FCSTD DOCUMENT  (FreeCAD 0.18.4R)
Label: Frame-03
License: CC-BY 3.0
LicenseURL: http://creativecommons.org/licenses/by/3.0/
objects: Part::Cylinder×968, Part::Box×648, Part::MultiFuse×634, Part::Cut×624, Part::Fillet×374, Part::Chamfer×146, Part::Mirroring×97, Part::Feature×58, Part::Loft×23, Part::Cone×22, App::DocumentObjectGroup×19, Part::Extrusion×14, Part::Part2DObjectPython×5, Part::Sphere×2, Mesh::Feature×2
note: 3615 computed .brp shape members not serialized (recipe doc carries the construction recipe); baked Part::Feature solids carry a one-line shape summary decoded from their .brp

FEATURE [Part::Box] Box  label="Cube250"
  AttacherType = Attacher::AttachEngine3D
  Height = 64
  Length = 126
  Width = 170
FEATURE [Part::Fillet] Fillet001
  Base = -> Box
  Edges = 2 edges r=15: [Edge1,Edge3]
FEATURE [Part::Fillet] Fillet
  Base = -> Fillet001
  Edges = 2 edges r=10: [Edge17,Edge18]
FEATURE [Part::Box] Box001  label="Cube251"
  AttacherType = Attacher::AttachEngine3D
  Height = 64
  Length = 120
  Placement = pos=(4,4,0) rot=(0,0,1;0rad)
  Width = 164
FEATURE [Part::Fillet] Fillet003
  Base = -> Box001
  Edges = 2 edges r=12: [Edge1,Edge3]
FEATURE [Part::Fillet] Fillet002
  Base = -> Fillet003
  Edges = 2 edges r=6: [Edge17,Edge18]
  Placement = pos=(-1,-1,0) rot=(0,0,1;0rad)
FEATURE [Part::Cut] Cut001
  Base = -> Fillet
  Refine = true
  Tool = -> Fillet002
FEATURE [Part::Cylinder] Cylinder004
  Angle = 360
  AttacherType = Attacher::AttachEngine3D
  Height = 174
  Placement = pos=(98,174,-23) rot=(1,0,0;1.5708rad)
  Radius = 52
FEATURE [Part::Cut] Cut
  Base = -> Cut001
  Refine = true
  Tool = -> Cylinder004
FEATURE [Part::Box] Box002  label="Cube252"
  AttacherType = Attacher::AttachEngine3D
  Height = 25
  Length = 131
  Placement = pos=(11,0,6) rot=(0,0,1;0rad)
  Width = 170
FEATURE [Part::Box] Box003  label="Cube253"
  AttacherType = Attacher::AttachEngine3D
  Height = 25
  Length = 148
  Placement = pos=(2,2,6) rot=(0,0,1;0rad)
  Width = 166
FEATURE [Part::Box] Box009  label="Cube192"
  AttacherType = Attacher::AttachEngine3D
  Height = 5.8
  Length = 13.6
  Placement = pos=(91.2,163,27) rot=(0,0,1;0rad)
  Width = 4
FEATURE [Part::Box] Box010  label="Cube254"
  AttacherType = Attacher::AttachEngine3D
  Height = 23
  Length = 37
  Placement = pos=(15,152,-23) rot=(0,0,1;0rad)
  Width = 18
FEATURE [Part::Cylinder] Cylinder012
  Angle = 360
  AttacherType = Attacher::AttachEngine3D
  Height = 22
  Placement = pos=(98,174,-23) rot=(1,0,0;1.5708rad)
  Radius = 52
FEATURE [Part::Box] Box011  label="Cube255"
  AttacherType = Attacher::AttachEngine3D
  Height = 9
  Length = 31
  Placement = pos=(17,156,-29) rot=(0,0,1;0rad)
  Width = 14
FEATURE [Part::Cylinder] Cylinder013
  Angle = 360
  AttacherType = Attacher::AttachEngine3D
  Height = 22
  Placement = pos=(98,174,-23) rot=(1,0,0;1.5708rad)
  Radius = 54
FEATURE [Part::Cut] Cut059
  Base = -> Box002
  Placement = pos=(0,0,2) rot=(0,0,1;0rad)
  Refine = true
  Tool = -> Box003
FEATURE [Part::Cut] Cut060
  Base = -> Cut059
  Placement = pos=(0,0,-3) rot=(0,0,1;0rad)
  Refine = true
FEATURE [Part::Cut] Cut061
  Base = -> Cut
  Refine = true
  Tool = -> Cut060
FEATURE [Part::Box] Box036  label="Cube274"
  AttacherType = Attacher::AttachEngine3D
  Height = 64
  Length = 21
  Width = 164
FEATURE [Part::Fillet] Fillet010
  Base = -> Box036
  Edges = 2 edges r=12: [Edge1,Edge3]
  Placement = pos=(3,3,0) rot=(0,0,1;0rad)
FEATURE [Part::Box] Box038  label="Cube276"
  AttacherType = Attacher::AttachEngine3D
  Height = 59
  Length = 16
  Placement = pos=(15,0,0) rot=(0,0,1;0rad)
  Width = 170
FEATURE [Part::Box] Box039  label="Cube277"
  AttacherType = Attacher::AttachEngine3D
  Height = 59
  Length = 21
  Placement = pos=(-13,3,0) rot=(0,0,1;0rad)
  Width = 164
FEATURE [Part::Box] Box040  label="Cube278"
  AttacherType = Attacher::AttachEngine3D
  Height = 59
  Length = 21
  Placement = pos=(-13,0,0) rot=(0,0,1;0rad)
  Width = 170
FEATURE [Part::Fillet] Fillet011
  Base = -> Box040
  Edges = 2 edges r=15: [Edge1,Edge3]
FEATURE [Part::Fillet] Fillet012
  Base = -> Box039
  Edges = 2 edges r=12: [Edge1,Edge3]
  Placement = pos=(3,0,0) rot=(0,0,1;0rad)
FEATURE [Part::Cut] Cut063
  Base = -> Fillet011
  Placement = pos=(13,0,0) rot=(0,0,1;0rad)
  Refine = true
  Tool = -> Fillet012
FEATURE [Part::Cut] Cut064
  Base = -> Cut063
  Refine = true
  Tool = -> Box038
FEATURE [Part::Box] Box041  label="Cube279"
  AttacherType = Attacher::AttachEngine3D
  Height = 28
  Length = 21
  Placement = pos=(-13,3,0) rot=(0,0,1;0rad)
  Width = 164
FEATURE [Part::Fillet] Fillet014
  Base = -> Box041
  Edges = 2 edges r=12: [Edge1,Edge3]
  Placement = pos=(2.5,0,0) rot=(0,0,1;0rad)
FEATURE [Part::Box] Box042  label="Cube280"
  AttacherType = Attacher::AttachEngine3D
  Height = 28
  Length = 21
  Placement = pos=(-13,0,0) rot=(0,0,1;0rad)
  Width = 170
FEATURE [Part::Fillet] Fillet013
  Base = -> Box042
  Edges = 2 edges r=15: [Edge1,Edge3]
FEATURE [Part::Cut] Cut067
  Base = -> Fillet013
  Placement = pos=(13,0,30) rot=(0,0,1;0rad)
  Refine = true
  Tool = -> Fillet014
FEATURE [Part::Box] Box043  label="Cube281"
  AttacherType = Attacher::AttachEngine3D
  Height = 59
  Length = 16
  Placement = pos=(14.5,0,0) rot=(0,0,1;0rad)
  Width = 170
FEATURE [Part::Cut] Cut066
  Base = -> Cut067
  Refine = true
  Tool = -> Box043
FEATURE [Part::Box] Box044  label="Cube282"
  AttacherType = Attacher::AttachEngine3D
  Height = 3
  Length = 3
  Placement = pos=(0,63,55) rot=(0,0,1;0rad)
  Width = 44
FEATURE [Part::Fillet] Fillet015
  Base = -> Box044
  Edges = 2 edges r=2: [Edge9,Edge11]
FEATURE [Part::Box] Box047  label="Cube285"
  AttacherType = Attacher::AttachEngine3D
  Height = 33
  Length = 21
  Placement = pos=(-13,3,0) rot=(0,0,1;0rad)
  Width = 164
FEATURE [Part::Fillet] Fillet016
  Base = -> Box047
  Edges = 2 edges r=12: [Edge1,Edge3]
  Placement = pos=(15.5,0,0) rot=(0,0,1;0rad)
FEATURE [Part::Box] Box070  label="Cube308"
  AttacherType = Attacher::AttachEngine3D
  Height = 4
  Length = 21
  Placement = pos=(-13,0,26) rot=(0,0,1;0rad)
  Width = 170
FEATURE [Part::Fillet] Fillet026
  Base = -> Box070
  Edges = 2 edges r=15: [Edge1,Edge3]
FEATURE [Part::Chamfer] Chamfer011
  Base = -> Fillet026
  Edges = 1 edges r=3.5: [Edge1]
  Placement = pos=(13,0,2) rot=(0,0,1;0rad)
FEATURE [Part::Box] Box071  label="Cube309"
  AttacherType = Attacher::AttachEngine3D
  Height = 4
  Length = 11
  Placement = pos=(10.5,0,28) rot=(0,0,1;0rad)
  Width = 170
FEATURE [Part::Cut] Cut077
  Base = -> Chamfer011
  Placement = pos=(0,0,-28) rot=(0,0,1;0rad)
  Refine = true
  Tool = -> Box071
FEATURE [Part::Box] Box072  label="Cube310"
  AttacherType = Attacher::AttachEngine3D
  Height = 4
  Length = 21
  Placement = pos=(-13,0,26) rot=(0,0,1;0rad)
  Width = 170
FEATURE [Part::Box] Box073  label="Cube311"
  AttacherType = Attacher::AttachEngine3D
  Height = 4
  Length = 11
  Placement = pos=(10.5,0,28) rot=(0,0,1;0rad)
  Width = 170
FEATURE [Part::Fillet] Fillet027
  Base = -> Box072
  Edges = 2 edges r=15: [Edge1,Edge3]
FEATURE [Part::Chamfer] Chamfer012
  Base = -> Fillet027
  Edges = 1 edges r=3.5: [Edge1]
  Placement = pos=(13,0,2) rot=(0,0,1;0rad)
FEATURE [Part::Cut] Cut078
  Base = -> Chamfer012
  Placement = pos=(0,0,-24) rot=(0,0,1;0rad)
  Refine = true
  Tool = -> Box073
FEATURE [Part::Box] Box074  label="Cube312"
  AttacherType = Attacher::AttachEngine3D
  Height = 4
  Length = 21
  Placement = pos=(-13,0,26) rot=(0,0,1;0rad)
  Width = 170
FEATURE [Part::Box] Box075  label="Cube313"
  AttacherType = Attacher::AttachEngine3D
  Height = 4
  Length = 11
  Placement = pos=(10.5,0,28) rot=(0,0,1;0rad)
  Width = 170
FEATURE [Part::Fillet] Fillet028
  Base = -> Box074
  Edges = 2 edges r=15: [Edge1,Edge3]
FEATURE [Part::Chamfer] Chamfer013
  Base = -> Fillet028
  Edges = 1 edges r=3.5: [Edge1]
  Placement = pos=(13,0,2) rot=(0,0,1;0rad)
FEATURE [Part::Cut] Cut079
  Base = -> Chamfer013
  Placement = pos=(0,0,-20) rot=(0,0,1;0rad)
  Refine = true
  Tool = -> Box075
FEATURE [Part::Box] Box076  label="Cube314"
  AttacherType = Attacher::AttachEngine3D
  Height = 4
  Length = 21
  Placement = pos=(-13,0,26) rot=(0,0,1;0rad)
  Width = 170
FEATURE [Part::Box] Box077  label="Cube315"
  AttacherType = Attacher::AttachEngine3D
  Height = 4
  Length = 11
  Placement = pos=(10.5,0,28) rot=(0,0,1;0rad)
  Width = 170
FEATURE [Part::Fillet] Fillet029
  Base = -> Box076
  Edges = 2 edges r=15: [Edge1,Edge3]
FEATURE [Part::Chamfer] Chamfer014
  Base = -> Fillet029
  Edges = 1 edges r=3.5: [Edge1]
  Placement = pos=(13,0,2) rot=(0,0,1;0rad)
FEATURE [Part::Cut] Cut080
  Base = -> Chamfer014
  Placement = pos=(0,0,-16) rot=(0,0,1;0rad)
  Refine = true
  Tool = -> Box077
FEATURE [Part::Box] Box078  label="Cube316"
  AttacherType = Attacher::AttachEngine3D
  Height = 4
  Length = 21
  Placement = pos=(-13,0,26) rot=(0,0,1;0rad)
  Width = 170
FEATURE [Part::Box] Box079  label="Cube317"
  AttacherType = Attacher::AttachEngine3D
  Height = 4
  Length = 11
  Placement = pos=(10.5,0,28) rot=(0,0,1;0rad)
  Width = 170
FEATURE [Part::Fillet] Fillet030
  Base = -> Box078
  Edges = 2 edges r=15: [Edge1,Edge3]
FEATURE [Part::Chamfer] Chamfer015
  Base = -> Fillet030
  Edges = 1 edges r=3.5: [Edge1]
  Placement = pos=(13,0,2) rot=(0,0,1;0rad)
FEATURE [Part::Cut] Cut081
  Base = -> Chamfer015
  Placement = pos=(0,0,-12) rot=(0,0,1;0rad)
  Refine = true
  Tool = -> Box079
FEATURE [Part::Box] Box080  label="Cube318"
  AttacherType = Attacher::AttachEngine3D
  Height = 4
  Length = 21
  Placement = pos=(-13,0,26) rot=(0,0,1;0rad)
  Width = 170
FEATURE [Part::Box] Box081  label="Cube319"
  AttacherType = Attacher::AttachEngine3D
  Height = 4
  Length = 11
  Placement = pos=(10.5,0,28) rot=(0,0,1;0rad)
  Width = 170
FEATURE [Part::Fillet] Fillet031
  Base = -> Box080
  Edges = 2 edges r=15: [Edge1,Edge3]
FEATURE [Part::Chamfer] Chamfer016
  Base = -> Fillet031
  Edges = 1 edges r=3.5: [Edge1]
  Placement = pos=(13,0,2) rot=(0,0,1;0rad)
FEATURE [Part::Cut] Cut082
  Base = -> Chamfer016
  Placement = pos=(0,0,-8) rot=(0,0,1;0rad)
  Refine = true
  Tool = -> Box081
FEATURE [Part::Box] Box082  label="Cube320"
  AttacherType = Attacher::AttachEngine3D
  Height = 4
  Length = 21
  Placement = pos=(-13,0,26) rot=(0,0,1;0rad)
  Width = 170
FEATURE [Part::Box] Box083  label="Cube321"
  AttacherType = Attacher::AttachEngine3D
  Height = 4
  Length = 11
  Placement = pos=(10.5,0,28) rot=(0,0,1;0rad)
  Width = 170
FEATURE [Part::Fillet] Fillet032
  Base = -> Box082
  Edges = 2 edges r=15: [Edge1,Edge3]
FEATURE [Part::Chamfer] Chamfer017
  Base = -> Fillet032
  Edges = 1 edges r=3.5: [Edge1]
  Placement = pos=(13,0,2) rot=(0,0,1;0rad)
FEATURE [Part::Cut] Cut083
  Base = -> Chamfer017
  Placement = pos=(0,0,-4) rot=(0,0,1;0rad)
  Refine = true
  Tool = -> Box083
FEATURE [Part::Box] Box084  label="Cube322"
  AttacherType = Attacher::AttachEngine3D
  Height = 4
  Length = 21
  Placement = pos=(-13,0,26) rot=(0,0,1;0rad)
  Width = 170
FEATURE [Part::Box] Box085  label="Cube323"
  AttacherType = Attacher::AttachEngine3D
  Height = 4
  Length = 11
  Placement = pos=(10.5,0,28) rot=(0,0,1;0rad)
  Width = 170
FEATURE [Part::Fillet] Fillet033
  Base = -> Box084
  Edges = 2 edges r=15: [Edge1,Edge3]
FEATURE [Part::Chamfer] Chamfer018
  Base = -> Fillet033
  Edges = 1 edges r=3.5: [Edge1]
  Placement = pos=(13,0,2) rot=(0,0,1;0rad)
FEATURE [Part::Cut] Cut084
  Base = -> Chamfer018
  Refine = true
  Tool = -> Box085
FEATURE [Part::MultiFuse] Fusion011
  Refine = true
  Shapes = -> [Cut084,Cut083,Cut080,Cut081,Cut078,Cut079,Cut082,Cut077]
FEATURE [Part::Box] Box086  label="Cube324"
  AttacherType = Attacher::AttachEngine3D
  Height = 30
  Length = 21
  Placement = pos=(-13,3,0) rot=(0,0,1;0rad)
  Width = 164
FEATURE [Part::Fillet] Fillet034
  Base = -> Box086
  Edges = 2 edges r=12: [Edge1,Edge3]
  Placement = pos=(15.5,0,0) rot=(0,0,1;0rad)
FEATURE [Part::Box] Box087  label="Cube325"
  AttacherType = Attacher::AttachEngine3D
  Height = 30
  Length = 21
  Placement = pos=(-13,2.5,0) rot=(0,0,1;0rad)
  Width = 165
FEATURE [Part::Fillet] Fillet035
  Base = -> Box087
  Edges = 2 edges r=12.5: [Edge1,Edge3]
  Placement = pos=(15,0,0) rot=(0,0,1;0rad)
FEATURE [Part::Cut] Cut086
  Base = -> Fillet035
  Refine = true
  Tool = -> Fillet034
FEATURE [Part::Box] Box088  label="Cube326"
  AttacherType = Attacher::AttachEngine3D
  Height = 30
  Length = 16
  Placement = pos=(10.5,0,0) rot=(0,0,1;0rad)
  Width = 170
FEATURE [Part::Cut] Cut087
  Base = -> Cut086
  Refine = true
  Tool = -> Box088
FEATURE [Part::Box] Box089  label="Cube327"
  AttacherType = Attacher::AttachEngine3D
  Height = 3
  Length = 21
  Placement = pos=(-5,0,30) rot=(0,0,1;0rad)
  Width = 170
FEATURE [Part::Feature] Face
  Placement = pos=(0,0,-10) rot=(0,0,1;0rad)
  shape: bbox 128.7 x 180.4 x 2e-07 mm, 1 faces, 0 solids (baked)
FEATURE [Part::Feature] Face002
  Placement = pos=(0,0,50) rot=(0,0,1;0rad)
  shape: bbox 110 x 176 x 2e-07 mm, 1 faces, 0 solids (baked)
FEATURE [Part::Loft] Loft
  Closed = false
  MaxDegree = 5
  Ruled = false
  Sections = -> [Face002,Face]
  Solid = true
FEATURE [Part::Feature] Face003
  Placement = pos=(0,0,50) rot=(0,0,1;0rad)
  shape: bbox 103.4 x 169.4 x 2e-07 mm, 1 faces, 0 solids (baked)
FEATURE [Part::Feature] Face004
  Placement = pos=(0,0,-10) rot=(0,0,1;0rad)
  shape: bbox 122.1 x 173.8 x 2e-07 mm, 1 faces, 0 solids (baked)
FEATURE [Part::Loft] Loft001
  Closed = false
  MaxDegree = 5
  Ruled = false
  Sections = -> [Face003,Face004]
  Solid = true
FEATURE [Part::Cut] Cut091
  Base = -> Loft
  Refine = true
  Tool = -> Loft001
FEATURE [Part::Box] Box094  label="Cube332"
  AttacherType = Attacher::AttachEngine3D
  Height = 30
  Length = 21
  Placement = pos=(-13,0,0) rot=(0,0,1;0rad)
  Width = 170
FEATURE [Part::Fillet] Fillet044
  Base = -> Box094
  Edges = 2 edges r=15: [Edge1,Edge3]
FEATURE [Part::Box] Box095  label="Cube333"
  AttacherType = Attacher::AttachEngine3D
  Height = 30
  Length = 21
  Placement = pos=(-13,3,0) rot=(0,0,1;0rad)
  Width = 164
FEATURE [Part::Fillet] Fillet045
  Base = -> Box095
  Edges = 2 edges r=12: [Edge1,Edge3]
  Placement = pos=(2.5,0,0) rot=(0,0,1;0rad)
FEATURE [Part::Cut] Cut092
  Base = -> Fillet044
  Placement = pos=(13,0,0) rot=(0,0,1;0rad)
  Refine = true
  Tool = -> Fillet045
FEATURE [Part::Box] Box096  label="Cube334"
  AttacherType = Attacher::AttachEngine3D
  Height = 30
  Length = 16
  Placement = pos=(14.5,0,0) rot=(0,0,1;0rad)
  Width = 170
FEATURE [Part::Cut] Cut093
  Base = -> Cut092
  Refine = true
  Tool = -> Box096
FEATURE [Part::Box] Box097  label="Cube335"
  AttacherType = Attacher::AttachEngine3D
  Height = 30
  Length = 16
  Placement = pos=(0,10,0) rot=(0,0,1;0rad)
  Width = 150
FEATURE [Part::Cut] Cut094
  Base = -> Cut093
  Refine = true
  Tool = -> Box097
FEATURE [Part::Box] Box098  label="Cube336"
  AttacherType = Attacher::AttachEngine3D
  Height = 30
  Length = 16
  Placement = pos=(10.5,0,0) rot=(0,0,1;0rad)
  Width = 170
FEATURE [Part::Box] Box099  label="Cube337"
  AttacherType = Attacher::AttachEngine3D
  Height = 30
  Length = 21
  Placement = pos=(-13,0,0) rot=(0,0,1;0rad)
  Width = 170
FEATURE [Part::Fillet] Fillet047
  Base = -> Box099
  Edges = 2 edges r=15: [Edge1,Edge3]
FEATURE [Part::Box] Box100  label="Cube338"
  AttacherType = Attacher::AttachEngine3D
  Height = 30
  Length = 21
  Placement = pos=(-13,3,0) rot=(0,0,1;0rad)
  Width = 164
FEATURE [Part::Fillet] Fillet046
  Base = -> Box100
  Edges = 2 edges r=12: [Edge1,Edge3]
  Placement = pos=(2.5,0,0) rot=(0,0,1;0rad)
FEATURE [Part::Cut] Cut096
  Base = -> Fillet047
  Placement = pos=(13,0,0) rot=(0,0,1;0rad)
  Refine = true
  Tool = -> Fillet046
FEATURE [Part::Cut] Cut097
  Base = -> Cut096
  Refine = true
  Tool = -> Box098
FEATURE [Part::Box] Box101  label="Cube339"
  AttacherType = Attacher::AttachEngine3D
  Height = 30
  Length = 16
  Placement = pos=(0,10.5,0) rot=(0,0,1;0rad)
  Width = 149
FEATURE [Part::Cut] Cut095
  Base = -> Cut097
  Refine = true
  Tool = -> Box101
FEATURE [Part::Box] Box102  label="Cube340"
  AttacherType = Attacher::AttachEngine3D
  Height = 55
  Length = 10
  Placement = pos=(0,7,68) rot=(0,1,0;0.226893rad)
  Width = 156
FEATURE [Part::Cut] Cut099
  Base = -> Cut066
  Refine = true
  Tool = -> Fillet015
FEATURE [Part::Cut] Cut100
  Base = -> Fusion011
  Refine = true
  Tool = -> Fillet016
FEATURE [Part::MultiFuse] Fusion016
  Refine = true
  Shapes = -> [Cut087,Cut100]
FEATURE [Part::Cut] Cut101
  Base = -> Fusion016
  Refine = true
  Tool = -> Box089
FEATURE [Part::Cut] Cut102  label="radiator-grid-00"
  Base = -> Cut101
  Refine = true
  Tool = -> Cut095
FEATURE [Part::Chamfer] Chamfer
  Base = -> Cut061
  Edges = 4 edges r=2.5: [Edge1,Edge4,Edge5,Edge8]
FEATURE [Part::Chamfer] Chamfer019
  Base = -> Chamfer
  Edges = 4 edges r=0.9: [Edge52,Edge80,Edge102,Edge110]
FEATURE [Part::Box] Box104  label="Cube342"
  AttacherType = Attacher::AttachEngine3D
  Height = 7.5
  Length = 4
  Placement = pos=(44,152,-31) rot=(0,0,1;0rad)
  Width = 22
FEATURE [Part::Box] Box105  label="Cube343"
  AttacherType = Attacher::AttachEngine3D
  Height = 18
  Length = 31
  Placement = pos=(17,158,-20) rot=(0,0,1;0rad)
  Width = 12
FEATURE [Part::Cylinder] Cylinder043
  Angle = 360
  AttacherType = Attacher::AttachEngine3D
  Height = 22
  Placement = pos=(98,174,-23) rot=(1,0,0;1.5708rad)
  Radius = 54
FEATURE [Part::Cut] Cut108
  Base = -> Box105
  Refine = true
  Tool = -> Cylinder043
FEATURE [Part::Box] Box106  label="Cube344"
  AttacherType = Attacher::AttachEngine3D
  Height = 21
  Length = 38
  Placement = pos=(15,167,-23) rot=(0,0,1;0rad)
  Width = 3
FEATURE [Part::Box] Box107  label="Cube345"
  AttacherType = Attacher::AttachEngine3D
  Height = 7
  Length = 10
  Placement = pos=(46,152,-30) rot=(0,0,1;0rad)
  Width = 25
FEATURE [Part::Cylinder] Cylinder044
  Angle = 360
  AttacherType = Attacher::AttachEngine3D
  Height = 25
  Placement = pos=(98,177,-23) rot=(0.799251,-0.424969,0.424969;1.79303rad)
  Radius = 52
FEATURE [Part::Cylinder] Cylinder045
  Angle = 360
  AttacherType = Attacher::AttachEngine3D
  Height = 28
  Placement = pos=(98,175,-23) rot=(0.799251,-0.424969,0.424969;1.79303rad)
  Radius = 50
FEATURE [Part::Cylinder] Cylinder046
  Angle = 360
  AttacherType = Attacher::AttachEngine3D
  Height = 30
  Placement = pos=(98,177,-30) rot=(0.799251,-0.424969,0.424969;1.79303rad)
  Radius = 48
FEATURE [Part::MultiFuse] Fusion018
  Refine = true
  Shapes = -> [Box107,Cylinder044]
FEATURE [Part::Box] Box108  label="Cube346"
  AttacherType = Attacher::AttachEngine3D
  Height = 7
  Length = 10
  Placement = pos=(48,147,-30) rot=(0,0,1;0rad)
  Width = 28
FEATURE [Part::Cut] Cut111
  Base = -> Fusion018
  Refine = true
  Tool = -> Cylinder045
FEATURE [Part::Cut] Cut112
  Base = -> Cut111
  Refine = true
  Tool = -> Cylinder046
FEATURE [Part::Cut] Cut113
  Base = -> Cut112
  Refine = true
  Tool = -> Box108
FEATURE [Part::Box] Box109  label="Cube347"
  AttacherType = Attacher::AttachEngine3D
  Height = 7
  Length = 45
  Placement = pos=(76,175,14) rot=(0,0,1;0rad)
  Width = 2
FEATURE [Part::MultiFuse] Fusion019
  Refine = true
  Shapes = -> [Cut113,Box109]
FEATURE [Part::Box] Box110  label="Cube348"
  AttacherType = Attacher::AttachEngine3D
  Height = 14
  Length = 10
  Placement = pos=(116,168,12) rot=(0,1,0;0.401426rad)
  Width = 9
FEATURE [Part::Fillet] Fillet050
  Base = -> Box102
  Edges = 4 edges r=5: [Edge9,Edge10,Edge11,Edge12]
  Placement = pos=(6,0,-1) rot=(0,0,1;0rad)
FEATURE [Part::Box] Box124  label="Cube024"
  AttacherType = Attacher::AttachEngine3D
  Height = 42
  Length = 26
  Placement = pos=(89,4.3,70) rot=(-1,0,0;0.038397rad)
  Width = 5
FEATURE [Part::Fillet] Fillet051
  Base = -> Box124
  Edges = 4 edges r=3: [Edge2,Edge4,Edge6,Edge8]
  Placement = pos=(-3,-2,0) rot=(0,0,1;0rad)
FEATURE [Part::Box] Box126  label="Cube048"
  AttacherType = Attacher::AttachEngine3D
  Height = 42
  Length = 58
  Placement = pos=(19.5,2,70) rot=(-1,0,0;0.038397rad)
  Width = 5
FEATURE [Part::Box] Box127  label="Cube049"
  AttacherType = Attacher::AttachEngine3D
  Height = 48
  Length = 11
  Placement = pos=(8.5,1,70) rot=(-0.179679,0.983544,0.018885;0.212918rad)
  Width = 7
FEATURE [Part::Cut] Cut129
  Base = -> Box126
  Refine = true
  Tool = -> Box127
FEATURE [Part::Fillet] Fillet052
  Base = -> Cut129
  Edges = 4 edges r=3: [Edge2,Edge4,Edge8,Edge12]
FEATURE [Part::MultiFuse] Fusion029  label="left-windows-holes"
  Refine = true
  Shapes = -> [Fillet051,Fillet052]
FEATURE [Part::Box] Box128  label="Cube362"
  AttacherType = Attacher::AttachEngine3D
  Height = 42
  Length = 26
  Placement = pos=(89,4.3,70) rot=(-1,0,0;0.038397rad)
  Width = 5
FEATURE [Part::Fillet] Fillet053
  Base = -> Box128
  Edges = 4 edges r=3: [Edge2,Edge4,Edge6,Edge8]
  Placement = pos=(-3,-2,0) rot=(0,0,1;0rad)
FEATURE [Part::Box] Box129  label="Cube363"
  AttacherType = Attacher::AttachEngine3D
  Height = 42
  Length = 58
  Placement = pos=(19.5,2,70) rot=(-1,0,0;0.038397rad)
  Width = 5
FEATURE [Part::Box] Box130  label="Cube364"
  AttacherType = Attacher::AttachEngine3D
  Height = 48
  Length = 11
  Placement = pos=(8.5,1,70) rot=(-0.179679,0.983544,0.018885;0.212918rad)
  Width = 7
FEATURE [Part::Cut] Cut130
  Base = -> Box129
  Refine = true
  Tool = -> Box130
FEATURE [Part::Fillet] Fillet054
  Base = -> Cut130
  Edges = 4 edges r=3: [Edge2,Edge4,Edge8,Edge12]
FEATURE [Part::MultiFuse] Fusion030
  Refine = true
  Shapes = -> [Fillet053,Fillet054]
FEATURE [Part::Mirroring] Part__Mirroring  label="right-windows-holes"
  Base = (0,0,0)
  Normal = (0,1,0)
  Placement = pos=(0,170,0) rot=(0,0,1;0rad)
  Source = -> Fusion030
FEATURE [Part::Box] Box131  label="Cube086"
  AttacherType = Attacher::AttachEngine3D
  Height = 25
  Length = 10
  Placement = pos=(150,40,0) rot=(0,0,1;0rad)
  Width = 100
FEATURE [Part::Box] Box132  label="Cube089"
  AttacherType = Attacher::AttachEngine3D
  Height = 40
  Length = 10
  Placement = pos=(150,19,0) rot=(-1,0,0;0.383972rad)
  Width = 20
FEATURE [Part::Box] Box133  label="Cube088"
  AttacherType = Attacher::AttachEngine3D
  Height = 40
  Length = 10
  Placement = pos=(150,19,0) rot=(-1,0,0;0.383972rad)
  Width = 20
FEATURE [Part::Mirroring] Part__Mirroring003  label="Cube088 (Mirror #13)"
  Base = (0,0,0)
  Normal = (0,1,0)
  Placement = pos=(0,180,0) rot=(0,0,1;0rad)
  Source = -> Box133
FEATURE [Part::MultiFuse] Fusion033
  Refine = true
  Shapes = -> [Box132,Part__Mirroring003]
FEATURE [Part::Cut] Cut132
  Base = -> Box131
  Placement = pos=(-30,-5,20) rot=(0,0,1;0rad)
  Refine = true
  Tool = -> Fusion033
FEATURE [Part::Fillet] Fillet055
  Base = -> Cut132
  Edges = 2 edges r=6: [Edge5,Edge6]
FEATURE [Part::Cut] Cut134
  Base = -> Fusion019
  Refine = true
  Tool = -> Box110
FEATURE [Part::Box] Box134  label="Cube365"
  AttacherType = Attacher::AttachEngine3D
  Height = 10
  Length = 10
  Placement = pos=(46,152,-31) rot=(0,1,0;0.785398rad)
  Width = 25
FEATURE [Part::Box] Box147  label="Cube074"
  AttacherType = Attacher::AttachEngine3D
  Height = 27
  Length = 7
  Placement = pos=(116,55,85) rot=(0,-1,0;0.034907rad)
  Width = 60
FEATURE [Part::Box] Box148  label="Cube079"
  AttacherType = Attacher::AttachEngine3D
  Height = 38
  Length = 5
  Placement = pos=(175,0,0) rot=(0,0,1;0rad)
  Width = 25
FEATURE [Part::Box] Box149  label="Cube080"
  AttacherType = Attacher::AttachEngine3D
  Height = 40
  Length = 5
  Placement = pos=(175,-24,-1) rot=(-1,0,0;0.038397rad)
  Width = 24
FEATURE [Part::Cut] Cut149
  Base = -> Box148
  Placement = pos=(0,1,1) rot=(0,0,1;0rad)
  Refine = true
  Tool = -> Box149
FEATURE [Part::Cylinder] Cylinder052
  Angle = 360
  AttacherType = Attacher::AttachEngine3D
  Height = 134
  Radius = 3.7
FEATURE [Part::Fillet] Fillet062
  Base = -> Cylinder052
  Edges = 2 edges r=2: [Edge1,Edge3]
  Placement = pos=(128,152,53) rot=(1,0,0;1.5708rad)
FEATURE [Part::Box] Box150  label="Cube378"
  AttacherType = Attacher::AttachEngine3D
  Height = 38
  Length = 5
  Placement = pos=(175,0,0) rot=(0,0,1;0rad)
  Width = 25
FEATURE [Part::Box] Box151  label="Cube379"
  AttacherType = Attacher::AttachEngine3D
  Height = 40
  Length = 5
  Placement = pos=(175,-24,-1) rot=(-1,0,0;0.038397rad)
  Width = 24
FEATURE [Part::Cut] Cut150
  Base = -> Box150
  Placement = pos=(-57,17,74) rot=(0,0,1;0rad)
  Refine = true
  Tool = -> Box151
FEATURE [Part::Mirroring] Part__Mirroring005  label="Cut212"
  Base = (0,0,0)
  Normal = (0,1,0)
  Placement = pos=(-57,154,73) rot=(0,0,1;0rad)
  Source = -> Cut149
FEATURE [Part::Fillet] Fillet063
  Base = -> Cut150
  Edges = 4 edges r=3: [Edge1,Edge3,Edge5,Edge10]
  Placement = pos=(3,0,-4) rot=(0,-1,0;0.034907rad)
FEATURE [Part::Fillet] Fillet064
  Base = -> Part__Mirroring005
  Edges = 4 edges r=3: [Edge1,Edge3,Edge5,Edge10]
  Placement = pos=(3,0,-4) rot=(0,-1,0;0.034907rad)
FEATURE [Part::Cylinder] Cylinder053
  Angle = 360
  AttacherType = Attacher::AttachEngine3D
  Height = 60
  Radius = 3.7
FEATURE [Part::Fillet] Fillet066
  Base = -> Cylinder053
  Edges = 2 edges r=2: [Edge1,Edge3]
  Placement = pos=(125,115,75) rot=(1,0,0;1.5708rad)
FEATURE [Part::Box] Box152  label="Cube070"
  AttacherType = Attacher::AttachEngine3D
  Height = 9
  Length = 14
  Width = 2
FEATURE [Part::Fillet] Fillet068
  Base = -> Box152
  Edges = 4 edges r=2: [Edge2,Edge4,Edge6,Edge8]
  Placement = pos=(68.5,0,46.5) rot=(0,0,1;0rad)
FEATURE [Part::Box] Box153  label="Cube071"
  AttacherType = Attacher::AttachEngine3D
  Height = 9
  Length = 14
  Width = 2
FEATURE [Part::Fillet] Fillet069
  Base = -> Box153
  Edges = 4 edges r=2: [Edge2,Edge4,Edge6,Edge8]
  Placement = pos=(68.5,168,46.5) rot=(0,0,1;0rad)
FEATURE [Part::MultiFuse] Fusion042
  Placement = pos=(-4,0,-13) rot=(0,0,1;0rad)
  Refine = true
  Shapes = -> [Fillet069,Fillet068]
FEATURE [Part::Box] Box154  label="Cube380"
  AttacherType = Attacher::AttachEngine3D
  Height = 9
  Length = 14
  Width = 2
FEATURE [Part::Fillet] Fillet071
  Base = -> Box154
  Edges = 4 edges r=2: [Edge2,Edge4,Edge6,Edge8]
  Placement = pos=(64.5,-1,36.5) rot=(0,0,1;0rad)
FEATURE [Part::Box] Box156  label="Cube382"
  AttacherType = Attacher::AttachEngine3D
  Height = 11
  Length = 16
  Width = 1
FEATURE [Part::Fillet] Fillet072
  Base = -> Box156
  Edges = 4 edges r=3: [Edge2,Edge4,Edge6,Edge8]
  Placement = pos=(63.5,-1,35.5) rot=(0,0,1;0rad)
FEATURE [Part::Box] Box157  label="Cube383"
  AttacherType = Attacher::AttachEngine3D
  Height = 9
  Length = 14
  Width = 2
FEATURE [Part::Fillet] Fillet073
  Base = -> Box157
  Edges = 4 edges r=2: [Edge2,Edge4,Edge6,Edge8]
  Placement = pos=(64.5,-1,36.5) rot=(0,0,1;0rad)
FEATURE [Part::Cut] Cut157  label="Cut591"
  Base = -> Fillet072
  Refine = true
  Tool = -> Fillet071
FEATURE [Part::Box] Box158  label="Cube384"
  AttacherType = Attacher::AttachEngine3D
  Height = 8
  Length = 13
  Placement = pos=(0.5,0,0.5) rot=(0,0,1;0rad)
  Width = 2
FEATURE [Part::Fillet] Fillet074
  Base = -> Box158
  Edges = 4 edges r=1.5: [Edge2,Edge4,Edge6,Edge8]
  Placement = pos=(64.5,-1,36.5) rot=(0,0,1;0rad)
FEATURE [Part::Cut] Cut158  label="Cut592"
  Base = -> Fillet073
  Refine = true
  Tool = -> Fillet074
FEATURE [Part::MultiFuse] Fusion043
  Refine = true
  Shapes = -> [Cut157,Cut158]
FEATURE [Part::Box] Box159  label="Cube385"
  AttacherType = Attacher::AttachEngine3D
  Height = 2
  Length = 13
  Placement = pos=(65,-1,40) rot=(0,0,1;0rad)
  Width = 1
FEATURE [Part::Box] Box160  label="Cube386"
  AttacherType = Attacher::AttachEngine3D
  Height = 8
  Length = 3
  Placement = pos=(75,-1,37) rot=(0,0,1;0rad)
  Width = 2
FEATURE [Part::Fillet] Fillet075
  Base = -> Box160
  Edges = 2 edges r=1.5: [Edge6,Edge8]
FEATURE [Part::MultiFuse] Fusion044
  Refine = true
  Shapes = -> [Fusion043,Box159,Fillet075]
FEATURE [Part::Cylinder] Cylinder054
  Angle = 360
  AttacherType = Attacher::AttachEngine3D
  Height = 1
  Placement = pos=(77,0,41) rot=(1,0,0;1.5708rad)
  Radius = 1.5
FEATURE [Part::Cut] Cut159  label="Cut584"
  Base = -> Fusion044
  Refine = true
  Tool = -> Cylinder054
FEATURE [Part::Fillet] Fillet076  label="left-door-knob"
  Base = -> Cut159
  Edges = 4 edges r=0.75: [Edge1,Edge5,Edge8,Edge11]
  Placement = pos=(0,0,5) rot=(0,0,1;0rad)
FEATURE [Part::Box] Box161  label="Cube387"
  AttacherType = Attacher::AttachEngine3D
  Height = 9
  Length = 14
  Width = 2
FEATURE [Part::Box] Box162  label="Cube388"
  AttacherType = Attacher::AttachEngine3D
  Height = 8
  Length = 3
  Placement = pos=(75,-1,37) rot=(0,0,1;0rad)
  Width = 2
FEATURE [Part::Fillet] Fillet079
  Base = -> Box162
  Edges = 2 edges r=1.5: [Edge6,Edge8]
FEATURE [Part::Box] Box163  label="Cube389"
  AttacherType = Attacher::AttachEngine3D
  Height = 11
  Length = 16
  Width = 1
FEATURE [Part::Fillet] Fillet078
  Base = -> Box163
  Edges = 4 edges r=3: [Edge2,Edge4,Edge6,Edge8]
  Placement = pos=(63.5,-1,35.5) rot=(0,0,1;0rad)
FEATURE [Part::Box] Box164  label="Cube390"
  AttacherType = Attacher::AttachEngine3D
  Height = 9
  Length = 14
  Width = 2
FEATURE [Part::Fillet] Fillet080
  Base = -> Box164
  Edges = 4 edges r=2: [Edge2,Edge4,Edge6,Edge8]
  Placement = pos=(64.5,-1,36.5) rot=(0,0,1;0rad)
FEATURE [Part::Fillet] Fillet081
  Base = -> Box161
  Edges = 4 edges r=2: [Edge2,Edge4,Edge6,Edge8]
  Placement = pos=(64.5,-1,36.5) rot=(0,0,1;0rad)
FEATURE [Part::Box] Box165  label="Cube391"
  AttacherType = Attacher::AttachEngine3D
  Height = 8
  Length = 13
  Placement = pos=(0.5,0,0.5) rot=(0,0,1;0rad)
  Width = 2
FEATURE [Part::Cylinder] Cylinder055
  Angle = 360
  AttacherType = Attacher::AttachEngine3D
  Height = 1
  Placement = pos=(77,0,41) rot=(1,0,0;1.5708rad)
  Radius = 1.5
FEATURE [Part::Box] Box166  label="Cube392"
  AttacherType = Attacher::AttachEngine3D
  Height = 2
  Length = 13
  Placement = pos=(65,-1,40) rot=(0,0,1;0rad)
  Width = 1
FEATURE [Part::Fillet] Fillet082
  Base = -> Box165
  Edges = 4 edges r=1.5: [Edge2,Edge4,Edge6,Edge8]
  Placement = pos=(64.5,-1,36.5) rot=(0,0,1;0rad)
FEATURE [Part::Cut] Cut161  label="Cut327"
  Base = -> Fillet081
  Refine = true
  Tool = -> Fillet082
FEATURE [Part::Cut] Cut162  label="Cut621"
  Base = -> Fillet078
  Refine = true
  Tool = -> Fillet080
FEATURE [Part::MultiFuse] Fusion046
  Refine = true
  Shapes = -> [Cut162,Cut161]
FEATURE [Part::MultiFuse] Fusion045
  Refine = true
  Shapes = -> [Fusion046,Box166,Fillet079]
FEATURE [Part::Cut] Cut160  label="Cut326"
  Base = -> Fusion045
  Refine = true
  Tool = -> Cylinder055
FEATURE [Part::Fillet] Fillet077
  Base = -> Cut160
  Edges = 4 edges r=0.75: [Edge1,Edge5,Edge8,Edge11]
FEATURE [Part::Mirroring] Part__Mirroring006  label="right-door-knob"
  Base = (0,0,0)
  Normal = (0,1,0)
  Placement = pos=(0,170,5) rot=(0,0,1;0rad)
  Source = -> Fillet077
FEATURE [Part::Part2DObjectPython] ShapeString  # Draft 2D object (typed FeaturePython)
  FontFile = <userpath>/Data/Temp/Futura Extra Bold.ttf
  MapMode = 5
  Placement = pos=(0,103,12) rot=(0.57735,-0.57735,-0.57735;2.0944rad)
  Size = 3.5
  String = IVECO
  Tracking = 0.5
FEATURE [Part::Extrusion] Extrude  label="iveco-logo"
  Base = -> ShapeString
  Dir = (1,0,0)
  DirMode = 0
  FaceMakerClass = Part::FaceMakerExtrusion
  LengthFwd = 0
  LengthRev = 0
  Placement = pos=(-1,0,0) rot=(0,0,1;0rad)
  Solid = false
  Symmetric = false
FEATURE [Part::Part2DObjectPython] ShapeString001  # Draft 2D object (typed FeaturePython)
  FontFile = <path>
  MapMode = 5
  Placement = pos=(0,55,34) rot=(0.57735,-0.57735,-0.57735;2.0944rad)
  Size = 1.35
  String = T
  Tracking = 0
FEATURE [Part::Part2DObjectPython] ShapeString002  # Draft 2D object (typed FeaturePython)
  FontFile = <path>
  MapMode = 5
  Placement = pos=(0,51,34) rot=(0.57735,-0.57735,-0.57735;2.0944rad)
  Size = 1.3
  String = urbo
  Tracking = 0
FEATURE [Part::Extrusion] Extrude001
  Base = -> ShapeString001
  Dir = (1,0,0)
  DirMode = 0
  FaceMakerClass = Part::FaceMakerExtrusion
  LengthFwd = 0
  LengthRev = 0
  Solid = false
  Symmetric = false
FEATURE [Part::Extrusion] Extrude002
  Base = -> ShapeString002
  Dir = (1,0,0)
  DirMode = 0
  FaceMakerClass = Part::FaceMakerExtrusion
  LengthFwd = 0
  LengthRev = 0
  Solid = false
  Symmetric = false
FEATURE [Part::MultiFuse] Fusion047  label="turbo-logo"
  Placement = pos=(-1,-3,6) rot=(0,0,1;0rad)
  Refine = true
  Shapes = -> [Extrude001,Extrude002]
FEATURE [Part::Box] Box167  label="Cube393"
  AttacherType = Attacher::AttachEngine3D
  Height = 21
  Length = 16
  Placement = pos=(-2,0,-30) rot=(0,0,1;0rad)
  Width = 170
FEATURE [Part::Cylinder] Cylinder056
  Angle = 360
  AttacherType = Attacher::AttachEngine3D
  Height = 21
  Placement = pos=(796.4,85,-30) rot=(0,0,1;2.96706rad)
  Radius = 800
FEATURE [Part::Box] Box168  label="Cube394"
  AttacherType = Attacher::AttachEngine3D
  Height = 21
  Length = 16
  Placement = pos=(-2,0,-30) rot=(0,0,1;0rad)
  Width = 170
FEATURE [Part::Cut] Cut163  label="Cut622"
  Base = -> Box168
  Refine = true
  Tool = -> Cylinder056
FEATURE [Part::Cut] Cut164  label="Cut177"
  Base = -> Box167
  Refine = true
  Tool = -> Cut163
FEATURE [Part::Fillet] Fillet083
  Base = -> Cut164
  Edges = 2 edges r=4: [Edge6,Edge12]
FEATURE [Part::Box] Box169  label="Cube395"
  AttacherType = Attacher::AttachEngine3D
  Height = 17
  Length = 20
  Placement = pos=(-2,0,-28) rot=(0,0,1;0rad)
  Width = 30
FEATURE [Part::Fillet] Fillet084
  Base = -> Box169
  Edges = 4 edges r=2: [Edge9,Edge10,Edge11,Edge12]
  Placement = pos=(-1,2,0) rot=(0,0,1;0rad)
FEATURE [Part::Box] Box170  label="Cube396"
  AttacherType = Attacher::AttachEngine3D
  Height = 17
  Length = 20
  Placement = pos=(-2,0,-28) rot=(0,0,1;0rad)
  Width = 30
FEATURE [Part::Fillet] Fillet085
  Base = -> Box170
  Edges = 4 edges r=2: [Edge9,Edge10,Edge11,Edge12]
  Placement = pos=(-1,138,0) rot=(0,0,1;0rad)
FEATURE [Part::MultiFuse] Fusion048
  Refine = true
  Shapes = -> [Fillet085,Fillet084]
FEATURE [Part::Box] Box171  label="Cube397"
  AttacherType = Attacher::AttachEngine3D
  Height = 17
  Length = 16
  Placement = pos=(-2,4,-30) rot=(0,0,1;0rad)
  Width = 162
FEATURE [Part::Fillet] Fillet086
  Base = -> Box171
  Edges = 2 edges r=3: [Edge1,Edge3]
  Placement = pos=(5,0,2) rot=(0,0,1;0rad)
FEATURE [Part::Cut] Cut165  label="Cut178"
  Base = -> Fillet083
  Refine = true
  Tool = -> Fillet086
FEATURE [Part::Box] Box172  label="Cube398"
  AttacherType = Attacher::AttachEngine3D
  Height = 17
  Length = 15
  Placement = pos=(2,30,-28) rot=(0,0,1;0rad)
  Width = 5
FEATURE [Part::Box] Box173  label="Cube399"
  AttacherType = Attacher::AttachEngine3D
  Height = 17
  Length = 15
  Placement = pos=(2,135,-28) rot=(0,0,1;0rad)
  Width = 5
FEATURE [Part::MultiFuse] Fusion049
  Refine = true
  Shapes = -> [Box173,Box172]
FEATURE [Part::Cut] Cut166  label="Cut623"
  Base = -> Fusion048
  Refine = true
  Tool = -> Fusion049
FEATURE [Part::Cut] Cut167  label="Cut624"
  Base = -> Cut165
  Refine = true
  Tool = -> Cut166
FEATURE [Part::Fillet] Fillet087
  Base = -> Cut167
  Edges = 4 edges r=2: [Edge60,Edge62,Edge92,Edge93]
FEATURE [Part::Box] Box174  label="Cube400"
  AttacherType = Attacher::AttachEngine3D
  Height = 21
  Length = 16
  Placement = pos=(6,5,-30) rot=(0,0,1;0rad)
  Width = 160
FEATURE [Part::Cylinder] Cylinder057
  Angle = 360
  AttacherType = Attacher::AttachEngine3D
  Height = 21
  Placement = pos=(504,85,-30) rot=(0,0,1;2.96706rad)
  Radius = 500
FEATURE [Part::Box] Box175  label="Cube401"
  AttacherType = Attacher::AttachEngine3D
  Height = 21
  Length = 16
  Placement = pos=(6,5,-30) rot=(0,0,1;0rad)
  Width = 160
FEATURE [Part::Cut] Cut168  label="Cut625"
  Base = -> Box174
  Refine = true
  Tool = -> Cylinder057
FEATURE [Part::Cut] Cut169  label="Cut626"
  Base = -> Box175
  Placement = pos=(2,0,0) rot=(0,0,1;0rad)
  Refine = true
  Tool = -> Cut168
FEATURE [Part::Fillet] Fillet088
  Base = -> Cut169
  Edges = 2 edges r=3: [Edge6,Edge12]
FEATURE [Part::Box] Box176  label="Cube402"
  AttacherType = Attacher::AttachEngine3D
  Height = 21
  Length = 16
  Placement = pos=(6,5,-30) rot=(0,0,1;0rad)
  Width = 160
FEATURE [Part::Box] Box177  label="Cube403"
  AttacherType = Attacher::AttachEngine3D
  Height = 21
  Length = 16
  Placement = pos=(6,5,-30) rot=(0,0,1;0rad)
  Width = 160
FEATURE [Part::Cylinder] Cylinder058
  Angle = 360
  AttacherType = Attacher::AttachEngine3D
  Height = 21
  Placement = pos=(504,85,-30) rot=(0,0,1;2.96706rad)
  Radius = 500
FEATURE [Part::Cut] Cut171  label="Cut628"
  Base = -> Box176
  Refine = true
  Tool = -> Cylinder058
FEATURE [Part::Cut] Cut170  label="Cut627"
  Base = -> Box177
  Placement = pos=(2,0,0) rot=(0,0,1;0rad)
  Refine = true
  Tool = -> Cut171
FEATURE [Part::Fillet] Fillet089
  Base = -> Cut170
  Edges = 2 edges r=3: [Edge6,Edge12]
  Placement = pos=(0,0,13) rot=(0,0,1;0rad)
FEATURE [Part::Box] Box178  label="Cube404"
  AttacherType = Attacher::AttachEngine3D
  Height = 21
  Length = 16
  Placement = pos=(6,5,-30) rot=(0,0,1;0rad)
  Width = 160
FEATURE [Part::Box] Box179  label="Cube405"
  AttacherType = Attacher::AttachEngine3D
  Height = 8
  Length = 8
  Placement = pos=(6,5,-30) rot=(0,0,1;0rad)
  Width = 160
FEATURE [Part::Cylinder] Cylinder059
  Angle = 360
  AttacherType = Attacher::AttachEngine3D
  Height = 21
  Placement = pos=(504,85,-30) rot=(0,0,1;2.96706rad)
  Radius = 500
FEATURE [Part::Cut] Cut173  label="Cut346"
  Base = -> Box178
  Refine = true
  Tool = -> Cylinder059
FEATURE [Part::Cut] Cut172  label="Cut345"
  Base = -> Box179
  Placement = pos=(0,0,21) rot=(0,0,1;0rad)
  Refine = true
  Tool = -> Cut173
FEATURE [Part::Cut] Cut174  label="Cut347"
  Base = -> Fillet087
  Refine = true
  Tool = -> Fillet088
FEATURE [Part::Fillet] Fillet090
  Base = -> Cut172
  Edges = 2 edges r=2: [Edge6,Edge13]
  Placement = pos=(0,0,-1) rot=(0,0,1;0rad)
FEATURE [Part::Cut] Cut175  label="Cut348"
  Base = -> Fillet090
  Refine = true
  Tool = -> Fillet089
FEATURE [Part::Box] Box180  label="Cube406"
  AttacherType = Attacher::AttachEngine3D
  Height = 10
  Length = 13
  Placement = pos=(0,30,-7) rot=(0,0,1;0rad)
  Width = 109
FEATURE [Part::Fillet] Fillet091
  Base = -> Box180
  Edges = 2 edges r=3: [Edge9,Edge11]
  Placement = pos=(1,0,1) rot=(0,0,1;0rad)
FEATURE [Part::Cut] Cut176  label="Cut349"
  Base = -> Cut175
  Refine = true
  Tool = -> Fillet091
FEATURE [Part::Box] Box181  label="Cube407"
  AttacherType = Attacher::AttachEngine3D
  Height = 17
  Length = 8
  Placement = pos=(0,53.5,-28) rot=(0,0,1;0rad)
  Width = 10
FEATURE [Part::Feature] Cut179  label="cab_tilt_lower002"
  Placement = pos=(15.5,45,-15) rot=(0,0,1;0rad)
  shape: bbox 4 x 120 x 28 mm, 33 faces (baked)
FEATURE [Part::Feature] Cut180  label="cab_tilt_upper002"
  Placement = pos=(15.5,45,-15) rot=(0,0,1;0rad)
  shape: bbox 5.33 x 120 x 34.16 mm, 49 faces (baked)
FEATURE [Part::Box] Box182  label="Cube408"
  AttacherType = Attacher::AttachEngine3D
  Height = 17
  Length = 8
  Placement = pos=(0,106.5,-28) rot=(0,0,1;0rad)
  Width = 10
FEATURE [Part::Cylinder] Cylinder060
  Angle = 360
  AttacherType = Attacher::AttachEngine3D
  Height = 13
  Placement = pos=(-2,58.5,-22) rot=(0,1,0;1.5708rad)
  Radius = 5
FEATURE [Part::Cylinder] Cylinder061
  Angle = 360
  AttacherType = Attacher::AttachEngine3D
  Height = 13
  Placement = pos=(-2,58.5,-22) rot=(0,1,0;1.5708rad)
  Radius = 1.6
FEATURE [Part::Cylinder] Cylinder062
  Angle = 360
  AttacherType = Attacher::AttachEngine3D
  Height = 2.5
  Placement = pos=(-2,58.5,-22) rot=(0,1,0;1.5708rad)
  Radius = 3.1
FEATURE [Part::MultiFuse] Fusion050
  Refine = true
  Shapes = -> [Cylinder062,Cylinder061]
FEATURE [Part::Cylinder] Cylinder063
  Angle = 360
  AttacherType = Attacher::AttachEngine3D
  Height = 13
  Placement = pos=(-2,58.5,-22) rot=(0,1,0;1.5708rad)
  Radius = 1.6
FEATURE [Part::Cylinder] Cylinder064
  Angle = 360
  AttacherType = Attacher::AttachEngine3D
  Height = 2.5
  Placement = pos=(-2,58.5,-22) rot=(0,1,0;1.5708rad)
  Radius = 3.1
FEATURE [Part::MultiFuse] Fusion052
  Placement = pos=(0,53,0) rot=(0,0,1;0rad)
  Refine = true
  Shapes = -> [Cylinder064,Cylinder063]
FEATURE [Part::Cylinder] Cylinder065
  Angle = 360
  AttacherType = Attacher::AttachEngine3D
  Height = 13
  Placement = pos=(-2,111.5,-22) rot=(0,1,0;1.5708rad)
  Radius = 5
FEATURE [Part::MultiFuse] Fusion053
  Refine = true
  Shapes = -> [Fusion052,Fusion050]
FEATURE [Part::MultiFuse] Fusion054
  Refine = true
  Shapes = -> [Cut174,Cut176,Box181,Box182,Cylinder060,Cylinder065]
FEATURE [Part::Cut] Cut181  label="Cut350"
  Base = -> Fusion054
  Refine = true
  Tool = -> Fusion053
FEATURE [Part::Fillet] Fillet092
  Base = -> Cut181
  Edges = 2 edges r=1: [Edge70,Edge189]
FEATURE [Part::Fillet] Fillet093
  Base = -> Fillet092
  Edges = 2 edges r=0.99: [Edge119,Edge180]
FEATURE [Part::Fillet] Fillet094
  Base = -> Fillet093
  Edges = 2 edges r=1: [Edge27,Edge225]
FEATURE [Part::Cylinder] Cylinder066
  Angle = 360
  AttacherType = Attacher::AttachEngine3D
  Height = 10
  Radius = 1.25
FEATURE [Part::Cylinder] Cylinder067
  Angle = 360
  AttacherType = Attacher::AttachEngine3D
  Height = 10
  Placement = pos=(0,4,0) rot=(0,0,1;0rad)
  Radius = 1.25
FEATURE [Part::Box] Box183  label="Cube409"
  AttacherType = Attacher::AttachEngine3D
  Height = 10
  Length = 2.5
  Placement = pos=(-1.25,0,0) rot=(0,0,1;0rad)
  Width = 4
FEATURE [Part::MultiFuse] Fusion055
  Refine = true
  Shapes = -> [Box183,Cylinder067,Cylinder066]
FEATURE [Part::Box] Box184  label="Cube410"
  AttacherType = Attacher::AttachEngine3D
  Height = 10
  Length = 2.5
  Placement = pos=(-1.25,0,0) rot=(0,0,1;0rad)
  Width = 4
FEATURE [Part::Cylinder] Cylinder068
  Angle = 360
  AttacherType = Attacher::AttachEngine3D
  Height = 10
  Placement = pos=(0,4,0) rot=(0,0,1;0rad)
  Radius = 1.25
FEATURE [Part::Cylinder] Cylinder069
  Angle = 360
  AttacherType = Attacher::AttachEngine3D
  Height = 10
  Radius = 1.25
FEATURE [Part::MultiFuse] Fusion056
  Placement = pos=(0,8,0) rot=(0,0,1;0rad)
  Refine = true
  Shapes = -> [Box184,Cylinder068,Cylinder069]
FEATURE [Part::Box] Box185  label="Cube411"
  AttacherType = Attacher::AttachEngine3D
  Height = 10
  Length = 2.5
  Placement = pos=(-1.25,0,0) rot=(0,0,1;0rad)
  Width = 4
FEATURE [Part::Cylinder] Cylinder070
  Angle = 360
  AttacherType = Attacher::AttachEngine3D
  Height = 10
  Placement = pos=(0,4,0) rot=(0,0,1;0rad)
  Radius = 1.25
FEATURE [Part::Cylinder] Cylinder071
  Angle = 360
  AttacherType = Attacher::AttachEngine3D
  Height = 10
  Radius = 1.25
FEATURE [Part::MultiFuse] Fusion057
  Placement = pos=(0,16,0) rot=(0,0,1;0rad)
  Refine = true
  Shapes = -> [Box185,Cylinder070,Cylinder071]
FEATURE [Part::Box] Box186  label="Cube412"
  AttacherType = Attacher::AttachEngine3D
  Height = 10
  Length = 2.5
  Placement = pos=(-1.25,0,0) rot=(0,0,1;0rad)
  Width = 4
FEATURE [Part::Cylinder] Cylinder072
  Angle = 360
  AttacherType = Attacher::AttachEngine3D
  Height = 10
  Placement = pos=(0,4,0) rot=(0,0,1;0rad)
  Radius = 1.25
FEATURE [Part::Cylinder] Cylinder073
  Angle = 360
  AttacherType = Attacher::AttachEngine3D
  Height = 10
  Radius = 1.25
FEATURE [Part::MultiFuse] Fusion058
  Placement = pos=(0,24,0) rot=(0,0,1;0rad)
  Refine = true
  Shapes = -> [Box186,Cylinder072,Cylinder073]
FEATURE [Part::Box] Box187  label="Cube413"
  AttacherType = Attacher::AttachEngine3D
  Height = 10
  Length = 2.5
  Placement = pos=(-1.25,0,0) rot=(0,0,1;0rad)
  Width = 4
FEATURE [Part::Cylinder] Cylinder074
  Angle = 360
  AttacherType = Attacher::AttachEngine3D
  Height = 10
  Placement = pos=(0,4,0) rot=(0,0,1;0rad)
  Radius = 1.25
FEATURE [Part::Cylinder] Cylinder075
  Angle = 360
  AttacherType = Attacher::AttachEngine3D
  Height = 10
  Radius = 1.25
FEATURE [Part::MultiFuse] Fusion059
  Placement = pos=(0,32,0) rot=(0,0,1;0rad)
  Refine = true
  Shapes = -> [Box187,Cylinder074,Cylinder075]
FEATURE [Part::MultiFuse] Fusion060
  Placement = pos=(12.5,67,-12) rot=(0,-1,0;1.0472rad)
  Refine = true
  Shapes = -> [Fusion055,Fusion057,Fusion058,Fusion056,Fusion059]
FEATURE [Part::Cut] Cut182  label="bumper-00"
  Base = -> Fillet094
  Placement = pos=(0,0,-1) rot=(0,0,1;0rad)
  Refine = true
  Tool = -> Fusion060
FEATURE [Part::MultiFuse] Fusion061
  Refine = true
  Shapes = -> [Fillet064,Box147,Part__Mirroring,Fusion029,Fillet063]
FEATURE [Part::Box] Box188  label="Cube414"
  AttacherType = Attacher::AttachEngine3D
  Height = 116
  Length = 66.5
  Placement = pos=(14.5,0,-0.5) rot=(0,0,1;0rad)
  Width = 180
FEATURE [Part::Box] Box189  label="Cube416"
  AttacherType = Attacher::AttachEngine3D
  Height = 117
  Length = 67.5
  Placement = pos=(14,0,-1) rot=(0,0,1;0rad)
  Width = 180
FEATURE [Part::Box] Box190  label="Cube415"
  AttacherType = Attacher::AttachEngine3D
  Height = 116
  Length = 67
  Placement = pos=(-53.2,0,65) rot=(0,1,0;0.218166rad)
  Width = 180
FEATURE [Part::Cut] Cut185  label="Cut630"
  Base = -> Box188
  Placement = pos=(0,-2,0) rot=(0,0,1;0rad)
  Refine = true
  Tool = -> Box190
FEATURE [Part::Box] Box191  label="Cube417"
  AttacherType = Attacher::AttachEngine3D
  Height = 116
  Length = 67
  Placement = pos=(-53.7,0,65) rot=(0,1,0;0.218166rad)
  Width = 180
FEATURE [Part::Cut] Cut184  label="Cut629"
  Base = -> Box189
  Placement = pos=(0,-2,0) rot=(0,0,1;0rad)
  Refine = true
  Tool = -> Box191
FEATURE [Part::Cut] Cut186
  Base = -> Cut091
  Refine = true
  Tool = -> Fusion061
FEATURE [Part::Cut] Cut187  label="doors-cut-01"
  Base = -> Cut184
  Placement = pos=(0.5,-3,0.5) rot=(0,0,1;0rad)
  Refine = true
  Tool = -> Cut185
FEATURE [Part::Cut] Cut188  label="Cut631"
  Base = -> Cut186
  Refine = true
  Tool = -> Fillet050
FEATURE [Part::Box] Box192  label="Cube418"
  AttacherType = Attacher::AttachEngine3D
  Height = 116
  Length = 67
  Placement = pos=(-53.2,0,65) rot=(0,1,0;0.218166rad)
  Width = 180
FEATURE [Part::Box] Box193  label="Cube419"
  AttacherType = Attacher::AttachEngine3D
  Height = 116
  Length = 67
  Placement = pos=(-53.7,0,65) rot=(0,1,0;0.218166rad)
  Width = 180
FEATURE [Part::Box] Box194  label="Cube420"
  AttacherType = Attacher::AttachEngine3D
  Height = 117
  Length = 67.5
  Placement = pos=(14,0,-1) rot=(0,0,1;0rad)
  Width = 180
FEATURE [Part::Cut] Cut190  label="Cut632"
  Base = -> Box194
  Placement = pos=(0,-2,0) rot=(0,0,1;0rad)
  Refine = true
  Tool = -> Box193
FEATURE [Part::Box] Box195  label="Cube421"
  AttacherType = Attacher::AttachEngine3D
  Height = 116
  Length = 66.5
  Placement = pos=(14.5,0,-0.5) rot=(0,0,1;0rad)
  Width = 180
FEATURE [Part::Cut] Cut191  label="Cut633"
  Base = -> Box195
  Placement = pos=(0,-2,0) rot=(0,0,1;0rad)
  Refine = true
  Tool = -> Box192
FEATURE [Part::Cut] Cut189  label="doors-cut-00"
  Base = -> Cut190
  Placement = pos=(0.5,-3,0.5) rot=(0,0,1;0rad)
  Refine = true
  Tool = -> Cut191
FEATURE [Part::Fillet] Fillet095
  Base = -> Cut188
  Edges = 4 edges r=3: [Edge209,Edge210,Edge211,Edge212]
FEATURE [Part::Cut] Cut192  label="Cut634"
  Base = -> Fillet095
  Refine = true
  Tool = -> Fillet066
FEATURE [Part::Box] Box196  label="Cube422"
  AttacherType = Attacher::AttachEngine3D
  Height = 64
  Length = 21
  Width = 164
FEATURE [Part::Fillet] Fillet096
  Base = -> Box196
  Edges = 2 edges r=18: [Edge1,Edge3]
  Placement = pos=(7,3,0) rot=(0,0,1;0rad)
FEATURE [Part::Cut] Cut193  label="Cut635"
  Base = -> Fillet010
  Refine = true
  Tool = -> Fillet096
FEATURE [Part::MultiFuse] Fusion062
  Refine = true
  Shapes = -> [Chamfer019,Cut193]
FEATURE [Part::Cut] Cut194  label="Cut636"
  Base = -> Fusion062
  Refine = true
  Tool = -> Cut064
FEATURE [Part::Cut] Cut195  label="Cut637"
  Base = -> Cut194
  Refine = true
  Tool = -> Fillet062
FEATURE [Part::Cut] Cut196  label="Cut638"
  Base = -> Cut195
  Refine = true
  Tool = -> Fillet055
FEATURE [Part::Cut] Cut197  label="Cut639"
  Base = -> Cut196
  Refine = true
  Tool = -> Fusion042
FEATURE [Part::Fillet] Fillet097
  Base = -> Cut197
  Edges = 2 edges r=3: [Edge74,Edge149]
FEATURE [Part::Box] Box197  label="Cube423"
  AttacherType = Attacher::AttachEngine3D
  Height = 2
  Length = 117
  Placement = pos=(6,3,54) rot=(0,0,1;0rad)
  Width = 164
FEATURE [Part::Fillet] Fillet098
  Base = -> Box197
  Edges = 2 edges r=15: [Edge1,Edge3]
FEATURE [Part::Fillet] Fillet099
  Base = -> Fillet098
  Edges = 2 edges r=6: [Edge17,Edge18]
FEATURE [Part::Box] Box198  label="Cube424"
  AttacherType = Attacher::AttachEngine3D
  Height = 2
  Length = 111
  Placement = pos=(6,3,54) rot=(0,0,1;0rad)
  Width = 158
FEATURE [Part::Fillet] Fillet101
  Base = -> Box198
  Edges = 2 edges r=12: [Edge1,Edge3]
FEATURE [Part::Fillet] Fillet100
  Base = -> Fillet101
  Edges = 2 edges r=3: [Edge17,Edge18]
  Placement = pos=(3,3,0) rot=(0,0,1;0rad)
FEATURE [Part::Cut] Cut198  label="Cut640"
  Base = -> Fillet099
  Placement = pos=(0,0,8) rot=(0,0,1;0rad)
  Refine = true
  Tool = -> Fillet100
FEATURE [Part::MultiFuse] Fusion063
  Refine = true
  Shapes = -> [Cut198,Fillet097]
FEATURE [Part::Cut] Cut199  label="Cut641"
  Base = -> Cut192
  Refine = true
  Tool = -> Cut187
FEATURE [Part::Cut] Cut200  label="cab-lower-part-00"
  Base = -> Fusion063
  Refine = true
  Tool = -> Cut189
FEATURE [Part::Box] Box203  label="Cube429"
  AttacherType = Attacher::AttachEngine3D
  Height = 58
  Length = 2.5
  Placement = pos=(0,10,0) rot=(0,0,1;0rad)
  Width = 0.5
FEATURE [Part::Box] Box204  label="Cube430"
  AttacherType = Attacher::AttachEngine3D
  Height = 58
  Length = 2.5
  Placement = pos=(0,159.5,0) rot=(0,0,1;0rad)
  Width = 0.5
FEATURE [Part::MultiFuse] Fusion065
  Refine = true
  Shapes = -> [Box204,Box203]
FEATURE [Part::Cylinder] Cylinder076
  Angle = 360
  AttacherType = Attacher::AttachEngine3D
  Height = 10
  Placement = pos=(13,13,0) rot=(0,0,1;3.38594rad)
  Radius = 14
FEATURE [Part::Fillet] Fillet104
  Base = -> Cylinder076
  Edges = 4 edges r=1: [Edge1,Edge2,Edge3,Edge4]
FEATURE [Part::Cylinder] Cylinder077
  Angle = 360
  AttacherType = Attacher::AttachEngine3D
  Height = 10
  Placement = pos=(13,13,0) rot=(0,0,1;3.38594rad)
  Radius = 10
FEATURE [Part::Cut] Cut205  label="Cut642"
  Base = -> Fillet104
  Refine = true
  Tool = -> Cylinder077
FEATURE [Part::Fillet] Fillet105
  Base = -> Cut205
  Edges = 1 edges r=3: [Edge20]
FEATURE [Part::Fillet] Fillet106
  Base = -> Fillet105
  Edges = 1 edges r=3: [Edge9]
FEATURE [Part::Cylinder] Cylinder078
  Angle = 360
  AttacherType = Attacher::AttachEngine3D
  Height = 10
  Placement = pos=(13,13,0) rot=(0,0,1;3.38594rad)
  Radius = 10
FEATURE [Part::Cylinder] Cylinder079
  Angle = 360
  AttacherType = Attacher::AttachEngine3D
  Height = 10
  Placement = pos=(13,13,0) rot=(0,0,1;3.38594rad)
  Radius = 14
FEATURE [Part::Fillet] Fillet108
  Base = -> Cylinder079
  Edges = 4 edges r=1: [Edge1,Edge2,Edge3,Edge4]
FEATURE [Part::Cut] Cut206  label="Cut643"
  Base = -> Fillet108
  Refine = true
  Tool = -> Cylinder078
FEATURE [Part::Fillet] Fillet109
  Base = -> Cut206
  Edges = 1 edges r=3: [Edge20]
FEATURE [Part::Fillet] Fillet107
  Base = -> Fillet109
  Edges = 1 edges r=3: [Edge9]
FEATURE [Part::Mirroring] Part__Mirroring008  label="Fillet107 (Mirror #8)"
  Base = (0,0,0)
  Normal = (0,1,0)
  Placement = pos=(0,170,0) rot=(0,0,1;0rad)
  Source = -> Fillet107
FEATURE [Part::Box] Box208  label="Cube434"
  AttacherType = Attacher::AttachEngine3D
  Height = 4
  Length = 10
  Placement = pos=(100,-19,13) rot=(0,0,1;0.139626rad)
  Width = 4
FEATURE [Part::Box] Box209  label="Cube435"
  AttacherType = Attacher::AttachEngine3D
  Height = 4
  Length = 10
  Placement = pos=(100,-19,13) rot=(0,0,1;0.139626rad)
  Width = 4
FEATURE [Part::Mirroring] Part__Mirroring010  label="Cube432 (Mirror #9)001"
  Base = (0,0,0)
  Normal = (1,0,0)
  Placement = pos=(200,0,0) rot=(0,0,1;0rad)
  Source = -> Box209
FEATURE [Part::Box] Box210  label="Cube436"
  AttacherType = Attacher::AttachEngine3D
  Height = 4
  Length = 10
  Placement = pos=(95,-15,13) rot=(0,0,1;0rad)
  Width = 4
FEATURE [Part::MultiFuse] Fusion068
  Refine = true
  Shapes = -> [Part__Mirroring010,Box208]
FEATURE [Part::Cut] Cut208  label="Cut644"
  Base = -> Box210
  Refine = true
  Tool = -> Fusion068
FEATURE [Part::Fillet] Fillet114
  Base = -> Cut208
  Edges = 3 edges r=0.5: [Edge4,Edge14,Edge15]
FEATURE [Part::Fillet] Fillet113
  Base = -> Fillet114
  Edges = 4 edges r=0.5: [Edge7,Edge11,Edge16,Edge20]
  Placement = pos=(-2,6,2) rot=(0,0,1;0rad)
FEATURE [Part::Mirroring] Part__Mirroring011  label="Fillet113 (Mirror #11)"
  Base = (0,0,0)
  Normal = (0,1,0)
  Placement = pos=(0,170,0) rot=(0,0,1;0rad)
  Source = -> Fillet113
FEATURE [Part::Box] Box211  label="Cube437"
  AttacherType = Attacher::AttachEngine3D
  Height = 1
  Length = 96
  Placement = pos=(26,4,116.5) rot=(0,0,1;0rad)
  Width = 162
FEATURE [Part::Box] Box212  label="Cube438"
  AttacherType = Attacher::AttachEngine3D
  Height = 1
  Length = 94
  Placement = pos=(26,6,116.5) rot=(0,0,1;0rad)
  Width = 158
FEATURE [Part::Fillet] Fillet115
  Base = -> Box212
  Edges = 2 edges r=4: [Edge5,Edge7]
FEATURE [Part::Fillet] Fillet116
  Base = -> Box211
  Edges = 2 edges r=6: [Edge5,Edge7]
FEATURE [Part::Fillet] Fillet117
  Base = -> Fillet116
  Edges = 2 edges r=2: [Edge17,Edge18]
FEATURE [Part::Cut] Cut209  label="Cut645"
  Base = -> Fillet117
  Refine = true
  Tool = -> Fillet115
FEATURE [Part::MultiFuse] Fusion071
  Refine = true
  Shapes = -> [Cut199,Cut209]
FEATURE [Part::Box] Box213  label="Cube439"
  AttacherType = Attacher::AttachEngine3D
  Height = 6.5
  Length = 110
  Placement = pos=(19,4,121.5) rot=(0,0,1;0rad)
  Width = 162
FEATURE [Part::Box] Box215  label="Cube441"
  AttacherType = Attacher::AttachEngine3D
  Height = 5.1
  Length = 100
  Placement = pos=(19.5,5.5,122.5) rot=(0,0,1;0rad)
  Width = 159
FEATURE [Part::Fillet] Fillet120
  Base = -> Box215
  Edges = 2 edges r=10: [Edge1,Edge3]
FEATURE [Part::Fillet] Fillet121
  Base = -> Fillet120
  Edges = 2 edges r=4.5: [Edge17,Edge18]
FEATURE [Part::Fillet] Fillet122
  Base = -> Fillet121
  Edges = 4 edges r=5: [Edge1,Edge4,Edge5,Edge8]
  Placement = pos=(0.7,0,-2) rot=(0,0,1;0rad)
FEATURE [Part::Cylinder] Cylinder080
  Angle = 360
  AttacherType = Attacher::AttachEngine3D
  Height = 10
  Placement = pos=(15,15,48) rot=(0,0,1;0rad)
  Radius = 15
FEATURE [Part::Cylinder] Cylinder081
  Angle = 360
  AttacherType = Attacher::AttachEngine3D
  Height = 10
  Placement = pos=(15,15,10) rot=(0,0,1;0rad)
  Radius = 13
FEATURE [Part::Cylinder] Cylinder082
  Angle = 360
  AttacherType = Attacher::AttachEngine3D
  Height = 42
  Placement = pos=(15,15,13) rot=(0,0,1;3.49066rad)
  Radius = 20
FEATURE [Part::Cylinder] Cylinder083
  Angle = 360
  AttacherType = Attacher::AttachEngine3D
  Height = 31
  Placement = pos=(15,15,19) rot=(0,0,1;3.49066rad)
  Radius = 18.5
FEATURE [Part::Cylinder] Cylinder084
  Angle = 360
  AttacherType = Attacher::AttachEngine3D
  Height = 3
  Placement = pos=(15,15,10) rot=(0,0,1;3.49066rad)
  Radius = 15
FEATURE [Part::Cylinder] Cylinder085
  Angle = 360
  AttacherType = Attacher::AttachEngine3D
  Height = 3
  Placement = pos=(15,15,55) rot=(0,0,1;3.49066rad)
  Radius = 17
FEATURE [Part::MultiFuse] Fusion074
  Refine = true
  Shapes = -> [Cylinder080,Cylinder081]
FEATURE [Part::Box] Box216  label="Cube442"
  AttacherType = Attacher::AttachEngine3D
  Height = 48
  Length = 10
  Placement = pos=(-4,5,10) rot=(0,0,1;0.785398rad)
  Width = 30
FEATURE [Part::Box] Box217  label="Cube443"
  AttacherType = Attacher::AttachEngine3D
  Height = 6
  Length = 10
  Placement = pos=(-4,10,10) rot=(0,0,1;0rad)
  Width = 2
FEATURE [Part::Cut] Cut245  label="Cut646"
  Base = -> Fusion071
  Refine = true
  Tool = -> Box213
FEATURE [Part::Fillet] Fillet123
  Base = -> Cut245
  Edges = 3 edges r=1.49: [Edge7,Edge21,Edge25]
FEATURE [Part::Box] Box220  label="Cube446"
  AttacherType = Attacher::AttachEngine3D
  Height = 5.1
  Length = 95
  Placement = pos=(23,7.5,122.5) rot=(0,0,1;0rad)
  Width = 155
FEATURE [Part::Fillet] Fillet124
  Base = -> Box220
  Edges = 2 edges r=3: [Edge5,Edge7]
FEATURE [Part::Fillet] Fillet125
  Base = -> Fillet124
  Edges = 2 edges r=8: [Edge17,Edge18]
FEATURE [Part::Fillet] Fillet126
  Base = -> Fillet125
  Edges = 1 edges r=4: [Edge4]
  Placement = pos=(0,0,-4) rot=(0,0,1;0rad)
FEATURE [Part::Cut] Cut246  label="Cut647"
  Base = -> Fillet122
  Refine = true
  Tool = -> Fillet126
FEATURE [Part::Box] Box221  label="Cube447"
  AttacherType = Attacher::AttachEngine3D
  Height = 1.5
  Length = 2
  Placement = pos=(0,65,14.5) rot=(0,0,1;0rad)
  Width = 36
FEATURE [Part::Box] Box222  label="Cube448"
  AttacherType = Attacher::AttachEngine3D
  Height = 1.5
  Length = 2
  Placement = pos=(0,68,18.5) rot=(0,0,1;0rad)
  Width = 33
FEATURE [Part::MultiFuse] Fusion094  label="iveco-logo_00"
  Placement = pos=(0,0,8) rot=(0,0,1;0rad)
  Refine = true
  Shapes = -> [Extrude,Box221,Box222]
FEATURE [Part::Cylinder] Cylinder133
  Angle = 360
  AttacherType = Attacher::AttachEngine3D
  Height = 4
  Placement = pos=(2,34,15) rot=(0,1,0;1.5708rad)
  Radius = 2.5
FEATURE [Part::Cylinder] Cylinder134
  Angle = 360
  AttacherType = Attacher::AttachEngine3D
  Height = 4
  Placement = pos=(2,34,15) rot=(0,1,0;1.5708rad)
  Radius = 0.9
FEATURE [Part::Cylinder] Cylinder135
  Angle = 360
  AttacherType = Attacher::AttachEngine3D
  Height = 7
  Placement = pos=(2,34,15) rot=(0,1,0;1.5708rad)
  Radius = 1.2
FEATURE [Part::Cylinder] Cylinder136
  Angle = 360
  AttacherType = Attacher::AttachEngine3D
  Height = 4
  Placement = pos=(2,34,15) rot=(0,1,0;1.5708rad)
  Radius = 2.7
FEATURE [Part::Cut] Cut247  label="Cut648"
  Base = -> Cylinder133
  Refine = true
  Tool = -> Cylinder134
FEATURE [Part::MultiFuse] Fusion095
  Refine = true
  Shapes = -> [Cylinder135,Cylinder136]
FEATURE [Part::Cylinder] Cylinder137
  Angle = 360
  AttacherType = Attacher::AttachEngine3D
  Height = 4
  Placement = pos=(2,34,15) rot=(0,1,0;1.5708rad)
  Radius = 2.5
FEATURE [Part::Cylinder] Cylinder138
  Angle = 360
  AttacherType = Attacher::AttachEngine3D
  Height = 4
  Placement = pos=(2,34,15) rot=(0,1,0;1.5708rad)
  Radius = 0.9
FEATURE [Part::Cut] Cut248  label="Cut649"
  Base = -> Cylinder137
  Placement = pos=(0,102,0) rot=(0,0,1;0rad)
  Refine = true
  Tool = -> Cylinder138
FEATURE [Part::Cylinder] Cylinder139
  Angle = 360
  AttacherType = Attacher::AttachEngine3D
  Height = 4
  Placement = pos=(2,34,15) rot=(0,1,0;1.5708rad)
  Radius = 2.7
FEATURE [Part::Cylinder] Cylinder140
  Angle = 360
  AttacherType = Attacher::AttachEngine3D
  Height = 7
  Placement = pos=(2,34,15) rot=(0,1,0;1.5708rad)
  Radius = 1.2
FEATURE [Part::MultiFuse] Fusion096
  Placement = pos=(0,102,0) rot=(0,0,1;0rad)
  Refine = true
  Shapes = -> [Cylinder140,Cylinder139]
FEATURE [Part::MultiFuse] Fusion097
  Refine = true
  Shapes = -> [Cut247,Cut248]
FEATURE [Part::MultiFuse] Fusion098
  Refine = true
  Shapes = -> [Fusion095,Fusion096]
FEATURE [Part::MultiFuse] Fusion099  label="radiator-grid-01"
  Placement = pos=(0,0,8) rot=(0,0,1;0rad)
  Refine = true
  Shapes = -> [Cut102,Fusion097]
FEATURE [Part::Cut] Cut252  label="Cut650"
  Base = -> Cylinder082
  Refine = true
  Tool = -> Cylinder083
FEATURE [Part::MultiFuse] Fusion106
  Refine = true
  Shapes = -> [Cylinder085,Cylinder084,Cut252]
FEATURE [Part::Cut] Cut253  label="Cut651"
  Base = -> Fusion106
  Refine = true
  Tool = -> Fusion074
FEATURE [Part::MultiFuse] Fusion107
  Refine = true
  Shapes = -> [Box217,Box216]
FEATURE [Part::Chamfer] Chamfer032
  Base = -> Cut253
  Edges = 1 edges r=4.99: [Edge32]
FEATURE [Part::Chamfer] Chamfer033
  Base = -> Chamfer032
  Edges = 1 edges r=5.49: [Edge33]
FEATURE [Part::Chamfer] Chamfer034
  Base = -> Chamfer033
  Edges = 1 edges r=2.99: [Edge36]
FEATURE [Part::Chamfer] Chamfer035
  Base = -> Chamfer034
  Edges = 1 edges r=3.49: [Edge36]
FEATURE [Part::Cut] Cut254
  Base = -> Chamfer035
  Refine = true
  Tool = -> Fusion107
FEATURE [Part::Chamfer] Chamfer036  label="left-deflector"
  Base = -> Cut254
  Edges = 1 edges r=0.9: [Edge25]
FEATURE [Part::Fillet] Fillet127
  Base = -> Cut200
  Edges = 2 edges r=4: [Edge286,Edge354]
FEATURE [Part::Cylinder] Cylinder149
  Angle = 360
  AttacherType = Attacher::AttachEngine3D
  Height = 13.5
  Placement = pos=(11.9886,10.7385,16) rot=(0.884029,-0.330525,-0.330525;1.69375rad)
  Radius = 2
FEATURE [Part::Cylinder] Cylinder150
  Angle = 360
  AttacherType = Attacher::AttachEngine3D
  Height = 10
  Placement = pos=(15,15,13) rot=(0,0,1;0rad)
  Radius = 13
FEATURE [Part::Cylinder] Cylinder151
  Angle = 360
  AttacherType = Attacher::AttachEngine3D
  Height = 10
  Placement = pos=(15,15,48) rot=(0,0,1;0rad)
  Radius = 15
FEATURE [Part::Cylinder] Cylinder152
  Angle = 360
  AttacherType = Attacher::AttachEngine3D
  Height = 10
  Placement = pos=(15,15,13) rot=(0,0,1;0rad)
  Radius = 19.9
FEATURE [Part::Cylinder] Cylinder153
  Angle = 360
  AttacherType = Attacher::AttachEngine3D
  Height = 13.5
  Placement = pos=(11.9886,10.7385,16) rot=(0.884029,-0.330525,-0.330525;1.69375rad)
  Radius = 2
FEATURE [Part::Chamfer] Chamfer037
  Base = -> Cylinder152
  Edges = 1 edges r=4.99: [Edge3]
FEATURE [Part::Cut] Cut256
  Base = -> Cylinder153
  Refine = true
  Tool = -> Chamfer037
FEATURE [Part::Cut] Cut257
  Base = -> Cylinder149
  Refine = true
  Tool = -> Cut256
FEATURE [Part::Cut] Cut258  label="Cut652"
  Base = -> Cut257
  Refine = true
  Tool = -> Cylinder150
FEATURE [Part::Cylinder] Cylinder154
  Angle = 360
  AttacherType = Attacher::AttachEngine3D
  Height = 11.5
  Placement = pos=(11.9886,10.7385,16) rot=(0.884029,-0.330525,-0.330525;1.69375rad)
  Radius = 0.9
FEATURE [Part::Cylinder] Cylinder155
  Angle = 360
  AttacherType = Attacher::AttachEngine3D
  Height = 11.5
  Placement = pos=(11.9886,10.7385,51) rot=(0.884029,-0.330525,-0.330525;1.69375rad)
  Radius = 0.9
FEATURE [Part::Cylinder] Cylinder156
  Angle = 360
  AttacherType = Attacher::AttachEngine3D
  Height = 13.5
  Placement = pos=(11.9886,10.7385,51) rot=(0.884029,-0.330525,-0.330525;1.69375rad)
  Radius = 2
FEATURE [Part::Cut] Cut259  label="Cut653"
  Base = -> Cylinder156
  Refine = true
  Tool = -> Cylinder151
FEATURE [Part::MultiFuse] Fusion108
  Refine = true
  Shapes = -> [Cylinder154,Cylinder155]
FEATURE [Part::MultiFuse] Fusion109
  Refine = true
  Shapes = -> [Cut259,Cut258]
FEATURE [Part::MultiFuse] Fusion110
  Refine = true
  Shapes = -> [Chamfer036,Fusion109]
FEATURE [Part::Cylinder] Cylinder157
  Angle = 360
  AttacherType = Attacher::AttachEngine3D
  Height = 11.5
  Placement = pos=(11.9886,10.7385,16) rot=(0.884029,-0.330525,-0.330525;1.69375rad)
  Radius = 1.2
FEATURE [Part::Cylinder] Cylinder158
  Angle = 360
  AttacherType = Attacher::AttachEngine3D
  Height = 11.5
  Placement = pos=(11.9886,10.7385,51) rot=(0.884029,-0.330525,-0.330525;1.69375rad)
  Radius = 1.2
FEATURE [Part::MultiFuse] Fusion111
  Refine = true
  Shapes = -> [Cylinder157,Cylinder158]
FEATURE [Part::Cut] Cut260  label="left-deflector_01"
  Base = -> Fusion110
  Refine = true
  Tool = -> Fusion108
FEATURE [Part::Cylinder] Cylinder159
  Angle = 360
  AttacherType = Attacher::AttachEngine3D
  Height = 11.5
  Placement = pos=(11.9886,10.7385,51) rot=(0.884029,-0.330525,-0.330525;1.69375rad)
  Radius = 1.2
FEATURE [Part::Cylinder] Cylinder160
  Angle = 360
  AttacherType = Attacher::AttachEngine3D
  Height = 11.5
  Placement = pos=(11.9886,10.7385,16) rot=(0.884029,-0.330525,-0.330525;1.69375rad)
  Radius = 1.2
FEATURE [Part::MultiFuse] Fusion112
  Refine = true
  Shapes = -> [Cylinder160,Cylinder159]
FEATURE [Part::Mirroring] Part__Mirroring012  label="Fusion111 (Mirror #12)"
  Base = (0,0,0)
  Normal = (0,1,0)
  Placement = pos=(0,170,0) rot=(0,0,1;0rad)
  Source = -> Fusion111
FEATURE [Part::Cylinder] Cylinder161
  Angle = 360
  AttacherType = Attacher::AttachEngine3D
  Height = 11.5
  Placement = pos=(11.9886,10.7385,16) rot=(0.884029,-0.330525,-0.330525;1.69375rad)
  Radius = 1.2
FEATURE [Part::Cylinder] Cylinder162
  Angle = 360
  AttacherType = Attacher::AttachEngine3D
  Height = 11.5
  Placement = pos=(11.9886,10.7385,51) rot=(0.884029,-0.330525,-0.330525;1.69375rad)
  Radius = 1.2
FEATURE [Part::MultiFuse] Fusion113
  Refine = true
  Shapes = -> [Cylinder161,Cylinder162]
FEATURE [Part::Mirroring] Part__Mirroring013  label="Fusion113 (Mirror #13)"
  Base = (0,0,0)
  Normal = (0,1,0)
  Placement = pos=(0,170,0) rot=(0,0,1;0rad)
  Source = -> Fusion113
FEATURE [Part::Cylinder] Cylinder163
  Angle = 360
  AttacherType = Attacher::AttachEngine3D
  Height = 11.5
  Placement = pos=(11.9886,10.7385,16) rot=(0.884029,-0.330525,-0.330525;1.69375rad)
  Radius = 1.2
FEATURE [Part::Cylinder] Cylinder164
  Angle = 360
  AttacherType = Attacher::AttachEngine3D
  Height = 11.5
  Placement = pos=(11.9886,10.7385,51) rot=(0.884029,-0.330525,-0.330525;1.69375rad)
  Radius = 1.2
FEATURE [Part::MultiFuse] Fusion114
  Refine = true
  Shapes = -> [Cylinder163,Cylinder164]
FEATURE [Part::MultiFuse] Fusion115
  Refine = true
  Shapes = -> [Fusion112,Part__Mirroring012]
FEATURE [Part::MultiFuse] Fusion116
  Refine = true
  Shapes = -> [Part__Mirroring013,Fusion114]
FEATURE [Part::Cut] Cut261  label="Cut654"
  Base = -> Fillet127
  Refine = true
  Tool = -> Fusion098
FEATURE [Part::Cut] Cut262  label="cab-lower-part-01"
  Base = -> Cut261
  Refine = true
  Tool = -> Fusion115
FEATURE [Part::Cylinder] Cylinder165
  Angle = 360
  AttacherType = Attacher::AttachEngine3D
  Height = 3
  Placement = pos=(15,15,55) rot=(0,0,1;3.49066rad)
  Radius = 17
FEATURE [Part::Cylinder] Cylinder166
  Angle = 360
  AttacherType = Attacher::AttachEngine3D
  Height = 3
  Placement = pos=(15,15,10) rot=(0,0,1;3.49066rad)
  Radius = 15
FEATURE [Part::Cylinder] Cylinder167
  Angle = 360
  AttacherType = Attacher::AttachEngine3D
  Height = 42
  Placement = pos=(15,15,13) rot=(0,0,1;3.49066rad)
  Radius = 20
FEATURE [Part::Cylinder] Cylinder168
  Angle = 360
  AttacherType = Attacher::AttachEngine3D
  Height = 31
  Placement = pos=(15,15,19) rot=(0,0,1;3.49066rad)
  Radius = 18.5
FEATURE [Part::Cut] Cut267  label="Cut657"
  Base = -> Cylinder167
  Refine = true
  Tool = -> Cylinder168
FEATURE [Part::MultiFuse] Fusion118
  Refine = true
  Shapes = -> [Cylinder165,Cylinder166,Cut267]
FEATURE [Part::Cylinder] Cylinder169
  Angle = 360
  AttacherType = Attacher::AttachEngine3D
  Height = 10
  Placement = pos=(15,15,48) rot=(0,0,1;0rad)
  Radius = 15
FEATURE [Part::Cylinder] Cylinder170
  Angle = 360
  AttacherType = Attacher::AttachEngine3D
  Height = 10
  Placement = pos=(15,15,10) rot=(0,0,1;0rad)
  Radius = 13
FEATURE [Part::MultiFuse] Fusion119
  Refine = true
  Shapes = -> [Cylinder169,Cylinder170]
FEATURE [Part::Cut] Cut266  label="Cut656"
  Base = -> Fusion118
  Refine = true
  Tool = -> Fusion119
FEATURE [Part::Chamfer] Chamfer042
  Base = -> Cut266
  Edges = 1 edges r=4.99: [Edge32]
FEATURE [Part::Chamfer] Chamfer041
  Base = -> Chamfer042
  Edges = 1 edges r=5.49: [Edge33]
FEATURE [Part::Chamfer] Chamfer040
  Base = -> Chamfer041
  Edges = 1 edges r=2.99: [Edge36]
FEATURE [Part::Chamfer] Chamfer039
  Base = -> Chamfer040
  Edges = 1 edges r=3.49: [Edge36]
FEATURE [Part::Box] Box223  label="Cube449"
  AttacherType = Attacher::AttachEngine3D
  Height = 6
  Length = 10
  Placement = pos=(-4,10,10) rot=(0,0,1;0rad)
  Width = 2
FEATURE [Part::Box] Box224  label="Cube450"
  AttacherType = Attacher::AttachEngine3D
  Height = 48
  Length = 10
  Placement = pos=(-4,5,10) rot=(0,0,1;0.785398rad)
  Width = 30
FEATURE [Part::MultiFuse] Fusion120
  Refine = true
  Shapes = -> [Box223,Box224]
FEATURE [Part::Cut] Cut265  label="Cut655"
  Base = -> Chamfer039
  Refine = true
  Tool = -> Fusion120
FEATURE [Part::Chamfer] Chamfer038  label="left-deflector001"
  Base = -> Cut265
  Edges = 1 edges r=0.9: [Edge25]
FEATURE [Part::Cylinder] Cylinder171
  Angle = 360
  AttacherType = Attacher::AttachEngine3D
  Height = 13.5
  Placement = pos=(11.9886,10.7385,51) rot=(0.884029,-0.330525,-0.330525;1.69375rad)
  Radius = 2
FEATURE [Part::Cylinder] Cylinder172
  Angle = 360
  AttacherType = Attacher::AttachEngine3D
  Height = 10
  Placement = pos=(15,15,48) rot=(0,0,1;0rad)
  Radius = 15
FEATURE [Part::Cut] Cut268  label="Cut658"
  Base = -> Cylinder171
  Refine = true
  Tool = -> Cylinder172
FEATURE [Part::Cylinder] Cylinder173
  Angle = 360
  AttacherType = Attacher::AttachEngine3D
  Height = 13.5
  Placement = pos=(11.9886,10.7385,16) rot=(0.884029,-0.330525,-0.330525;1.69375rad)
  Radius = 2
FEATURE [Part::Cylinder] Cylinder174
  Angle = 360
  AttacherType = Attacher::AttachEngine3D
  Height = 13.5
  Placement = pos=(11.9886,10.7385,16) rot=(0.884029,-0.330525,-0.330525;1.69375rad)
  Radius = 2
FEATURE [Part::Cylinder] Cylinder175
  Angle = 360
  AttacherType = Attacher::AttachEngine3D
  Height = 10
  Placement = pos=(15,15,13) rot=(0,0,1;0rad)
  Radius = 19.9
FEATURE [Part::Chamfer] Chamfer043
  Base = -> Cylinder175
  Edges = 1 edges r=4.99: [Edge3]
FEATURE [Part::Cut] Cut271  label="Cut661"
  Base = -> Cylinder174
  Refine = true
  Tool = -> Chamfer043
FEATURE [Part::Cut] Cut270  label="Cut660"
  Base = -> Cylinder173
  Refine = true
  Tool = -> Cut271
FEATURE [Part::Cylinder] Cylinder176
  Angle = 360
  AttacherType = Attacher::AttachEngine3D
  Height = 10
  Placement = pos=(15,15,13) rot=(0,0,1;0rad)
  Radius = 13
FEATURE [Part::Cut] Cut269  label="Cut659"
  Base = -> Cut270
  Refine = true
  Tool = -> Cylinder176
FEATURE [Part::MultiFuse] Fusion121
  Refine = true
  Shapes = -> [Cut268,Cut269]
FEATURE [Part::MultiFuse] Fusion117
  Refine = true
  Shapes = -> [Chamfer038,Fusion121]
FEATURE [Part::Cylinder] Cylinder177
  Angle = 360
  AttacherType = Attacher::AttachEngine3D
  Height = 11.5
  Placement = pos=(11.9886,10.7385,16) rot=(0.884029,-0.330525,-0.330525;1.69375rad)
  Radius = 0.9
FEATURE [Part::Cylinder] Cylinder178
  Angle = 360
  AttacherType = Attacher::AttachEngine3D
  Height = 11.5
  Placement = pos=(11.9886,10.7385,51) rot=(0.884029,-0.330525,-0.330525;1.69375rad)
  Radius = 0.9
FEATURE [Part::MultiFuse] Fusion122
  Refine = true
  Shapes = -> [Cylinder177,Cylinder178]
FEATURE [Part::Cut] Cut264  label="left-deflector_002"
  Base = -> Fusion117
  Refine = true
  Tool = -> Fusion122
FEATURE [Part::MultiFuse] Fusion123
  Refine = true
  Shapes = -> [Part__Mirroring011,Box009,Cut134]
FEATURE [Part::Cut] Cut272  label="Cut662"
  Base = -> Fusion123
  Refine = true
  Tool = -> Box134
FEATURE [Part::Fillet] Fillet128
  Base = -> Cut272
  Edges = 1 edges r=1: [Edge14]
FEATURE [Part::Cut] Cut273  label="Cut663"
  Base = -> Box010
  Refine = true
  Tool = -> Cylinder012
FEATURE [Part::Cut] Cut274  label="Cut664"
  Base = -> Cut273
  Refine = true
  Tool = -> Cut108
FEATURE [Part::Cut] Cut275  label="Cut665"
  Base = -> Cut274
  Refine = true
  Tool = -> Box106
FEATURE [Part::Box] Box225  label="Cube451"
  AttacherType = Attacher::AttachEngine3D
  Height = 20
  Length = 33
  Placement = pos=(15,156,-31) rot=(0,0,1;0rad)
  Width = 14
FEATURE [Part::Cylinder] Cylinder179
  Angle = 360
  AttacherType = Attacher::AttachEngine3D
  Height = 22
  Placement = pos=(98,174,-23) rot=(1,0,0;1.5708rad)
  Radius = 52
FEATURE [Part::Box] Box226  label="Cube452"
  AttacherType = Attacher::AttachEngine3D
  Height = 9
  Length = 5
  Placement = pos=(46,152,-32) rot=(0,0,1;0rad)
  Width = 22
FEATURE [Part::MultiFuse] Fusion
  Refine = true
  Shapes = -> [Cylinder179,Box226]
FEATURE [Part::Cut] Cut276  label="Cut666"
  Base = -> Box225
  Refine = true
  Tool = -> Fusion
FEATURE [Part::MultiFuse] Fusion124
  Refine = true
  Shapes = -> [Cylinder013,Box104]
FEATURE [Part::Cut] Cut277  label="Cut667"
  Base = -> Box011
  Refine = true
  Tool = -> Fusion124
FEATURE [Part::Cut] Cut278  label="Cut668"
  Base = -> Cut276
  Refine = true
  Tool = -> Cut277
FEATURE [Part::Box] Box227  label="Cube453"
  AttacherType = Attacher::AttachEngine3D
  Height = 2
  Length = 33
  Placement = pos=(15,156,-31) rot=(0,0,1;0rad)
  Width = 14
FEATURE [Part::Box] Box228  label="Cube454"
  AttacherType = Attacher::AttachEngine3D
  Height = 20
  Length = 33
  Placement = pos=(15,169,-29) rot=(0,0,1;0rad)
  Width = 3
FEATURE [Part::Cut] Cut279  label="Cut669"
  Base = -> Box228
  Refine = true
  Tool = -> Box227
FEATURE [Part::Cut] Cut280  label="Cut670"
  Base = -> Cut278
  Refine = true
  Tool = -> Cut279
FEATURE [Part::Box] Box229  label="Cube455"
  AttacherType = Attacher::AttachEngine3D
  Height = 12
  Length = 28
  Placement = pos=(17,165,-24) rot=(-1,0,0;0.279253rad)
  Width = 3
FEATURE [Part::Cylinder] Cylinder180
  Angle = 360
  AttacherType = Attacher::AttachEngine3D
  Height = 22
  Placement = pos=(98,174,-23) rot=(1,0,0;1.5708rad)
  Radius = 54
FEATURE [Part::Box] Box230  label="Cube456"
  AttacherType = Attacher::AttachEngine3D
  Height = 9
  Length = 5
  Placement = pos=(44,152,-32) rot=(0,0,1;0rad)
  Width = 22
FEATURE [Part::MultiFuse] Fusion125
  Refine = true
  Shapes = -> [Cylinder180,Box230]
FEATURE [Part::Cut] Cut281  label="Cut671"
  Base = -> Box229
  Placement = pos=(0,1,0) rot=(0,0,1;0rad)
  Refine = true
  Tool = -> Fusion125
FEATURE [Part::Cut] Cut282  label="Cut672"
  Base = -> Cut280
  Refine = true
  Tool = -> Cut281
FEATURE [Part::Box] Box231  label="Cube457"
  AttacherType = Attacher::AttachEngine3D
  Height = 23
  Length = 37
  Placement = pos=(15,152,-23) rot=(0,0,1;0rad)
  Width = 18
FEATURE [Part::Cylinder] Cylinder
  Angle = 360
  AttacherType = Attacher::AttachEngine3D
  Height = 22
  Placement = pos=(98,174,-23) rot=(1,0,0;1.5708rad)
  Radius = 52
FEATURE [Part::Cut] Cut285  label="Cut675"
  Base = -> Box231
  Refine = true
  Tool = -> Cylinder
FEATURE [Part::Box] Box232  label="Cube458"
  AttacherType = Attacher::AttachEngine3D
  Height = 18
  Length = 31
  Placement = pos=(17,158,-20) rot=(0,0,1;0rad)
  Width = 12
FEATURE [Part::Cylinder] Cylinder181
  Angle = 360
  AttacherType = Attacher::AttachEngine3D
  Height = 22
  Placement = pos=(98,174,-23) rot=(1,0,0;1.5708rad)
  Radius = 54
FEATURE [Part::Cut] Cut286  label="Cut676"
  Base = -> Box232
  Refine = true
  Tool = -> Cylinder181
FEATURE [Part::Cut] Cut284  label="Cut674"
  Base = -> Cut285
  Refine = true
  Tool = -> Cut286
FEATURE [Part::Box] Box233  label="Cube459"
  AttacherType = Attacher::AttachEngine3D
  Height = 21
  Length = 38
  Placement = pos=(15,167,-23) rot=(0,0,1;0rad)
  Width = 3
FEATURE [Part::Cut] Cut283  label="Cut673"
  Base = -> Cut284
  Refine = true
  Tool = -> Box233
FEATURE [Part::Box] Box234  label="Cube460"
  AttacherType = Attacher::AttachEngine3D
  Height = 20
  Length = 33
  Placement = pos=(15,156,-31) rot=(0,0,1;0rad)
  Width = 14
FEATURE [Part::Cylinder] Cylinder182
  Angle = 360
  AttacherType = Attacher::AttachEngine3D
  Height = 22
  Placement = pos=(98,174,-23) rot=(1,0,0;1.5708rad)
  Radius = 52
FEATURE [Part::Box] Box235  label="Cube461"
  AttacherType = Attacher::AttachEngine3D
  Height = 9
  Length = 5
  Placement = pos=(46,152,-32) rot=(0,0,1;0rad)
  Width = 22
FEATURE [Part::MultiFuse] Fusion128
  Refine = true
  Shapes = -> [Cylinder182,Box235]
FEATURE [Part::Cut] Cut290  label="Cut680"
  Base = -> Box234
  Refine = true
  Tool = -> Fusion128
FEATURE [Part::Box] Box236  label="Cube462"
  AttacherType = Attacher::AttachEngine3D
  Height = 9
  Length = 31
  Placement = pos=(17,156,-29) rot=(0,0,1;0rad)
  Width = 14
FEATURE [Part::Cylinder] Cylinder183
  Angle = 360
  AttacherType = Attacher::AttachEngine3D
  Height = 22
  Placement = pos=(98,174,-23) rot=(1,0,0;1.5708rad)
  Radius = 54
FEATURE [Part::Box] Box237  label="Cube463"
  AttacherType = Attacher::AttachEngine3D
  Height = 7.5
  Length = 4
  Placement = pos=(44,152,-31) rot=(0,0,1;0rad)
  Width = 22
FEATURE [Part::MultiFuse] Fusion129
  Refine = true
  Shapes = -> [Cylinder183,Box237]
FEATURE [Part::Cut] Cut291  label="Cut681"
  Base = -> Box236
  Refine = true
  Tool = -> Fusion129
FEATURE [Part::Cut] Cut289  label="Cut679"
  Base = -> Cut290
  Refine = true
  Tool = -> Cut291
FEATURE [Part::Box] Box238  label="Cube464"
  AttacherType = Attacher::AttachEngine3D
  Height = 20
  Length = 33
  Placement = pos=(15,169,-29) rot=(0,0,1;0rad)
  Width = 3
FEATURE [Part::Box] Box239  label="Cube465"
  AttacherType = Attacher::AttachEngine3D
  Height = 2
  Length = 33
  Placement = pos=(15,156,-31) rot=(0,0,1;0rad)
  Width = 14
FEATURE [Part::Cut] Cut292  label="Cut682"
  Base = -> Box238
  Refine = true
  Tool = -> Box239
FEATURE [Part::Cut] Cut288  label="Cut678"
  Base = -> Cut289
  Refine = true
  Tool = -> Cut292
FEATURE [Part::Box] Box240  label="Cube466"
  AttacherType = Attacher::AttachEngine3D
  Height = 12
  Length = 28
  Placement = pos=(17,165,-24) rot=(-1,0,0;0.279253rad)
  Width = 3
FEATURE [Part::Cylinder] Cylinder184
  Angle = 360
  AttacherType = Attacher::AttachEngine3D
  Height = 22
  Placement = pos=(98,174,-23) rot=(1,0,0;1.5708rad)
  Radius = 54
FEATURE [Part::Box] Box241  label="Cube467"
  AttacherType = Attacher::AttachEngine3D
  Height = 9
  Length = 5
  Placement = pos=(44,152,-32) rot=(0,0,1;0rad)
  Width = 22
FEATURE [Part::MultiFuse] Fusion130
  Refine = true
  Shapes = -> [Cylinder184,Box241]
FEATURE [Part::Cut] Cut293  label="Cut683"
  Base = -> Box240
  Placement = pos=(0,1,0) rot=(0,0,1;0rad)
  Refine = true
  Tool = -> Fusion130
FEATURE [Part::Cut] Cut287  label="Cut677"
  Base = -> Cut288
  Refine = true
  Tool = -> Cut293
FEATURE [Part::Box] Box242  label="Cube468"
  AttacherType = Attacher::AttachEngine3D
  Height = 4
  Length = 10
  Placement = pos=(95,-15,13) rot=(0,0,1;0rad)
  Width = 4
FEATURE [Part::Box] Box243  label="Cube469"
  AttacherType = Attacher::AttachEngine3D
  Height = 4
  Length = 10
  Placement = pos=(100,-19,13) rot=(0,0,1;0.139626rad)
  Width = 4
FEATURE [Part::Mirroring] Part__Mirroring016  label="Cube432 (Mirror #9)002"
  Base = (0,0,0)
  Normal = (1,0,0)
  Placement = pos=(200,0,0) rot=(0,0,1;0rad)
  Source = -> Box243
FEATURE [Part::Box] Box244  label="Cube470"
  AttacherType = Attacher::AttachEngine3D
  Height = 4
  Length = 10
  Placement = pos=(100,-19,13) rot=(0,0,1;0.139626rad)
  Width = 4
FEATURE [Part::MultiFuse] Fusion132
  Refine = true
  Shapes = -> [Part__Mirroring016,Box244]
FEATURE [Part::Cut] Cut295  label="Cut685"
  Base = -> Box242
  Refine = true
  Tool = -> Fusion132
FEATURE [Part::Fillet] Fillet131
  Base = -> Cut295
  Edges = 3 edges r=0.5: [Edge4,Edge14,Edge15]
FEATURE [Part::Fillet] Fillet130
  Base = -> Fillet131
  Edges = 4 edges r=0.5: [Edge7,Edge11,Edge16,Edge20]
  Placement = pos=(-2,6,2) rot=(0,0,1;0rad)
FEATURE [Part::Mirroring] Part__Mirroring015  label="Fillet113 (Mirror #11)001"
  Base = (0,0,0)
  Normal = (0,1,0)
  Placement = pos=(0,170,0) rot=(0,0,1;0rad)
  Source = -> Fillet130
FEATURE [Part::Box] Box245  label="Cube471"
  AttacherType = Attacher::AttachEngine3D
  Height = 5.8
  Length = 13.6
  Placement = pos=(91.2,163,27) rot=(0,0,1;0rad)
  Width = 4
FEATURE [Part::Box] Box246  label="Cube472"
  AttacherType = Attacher::AttachEngine3D
  Height = 7
  Length = 10
  Placement = pos=(46,152,-30) rot=(0,0,1;0rad)
  Width = 25
FEATURE [Part::Cylinder] Cylinder185
  Angle = 360
  AttacherType = Attacher::AttachEngine3D
  Height = 25
  Placement = pos=(98,177,-23) rot=(0.799251,-0.424969,0.424969;1.79303rad)
  Radius = 52
FEATURE [Part::MultiFuse] Fusion134
  Refine = true
  Shapes = -> [Box246,Cylinder185]
FEATURE [Part::Cylinder] Cylinder186
  Angle = 360
  AttacherType = Attacher::AttachEngine3D
  Height = 28
  Placement = pos=(98,175,-23) rot=(0.799251,-0.424969,0.424969;1.79303rad)
  Radius = 50
FEATURE [Part::Cut] Cut299
  Base = -> Fusion134
  Refine = true
  Tool = -> Cylinder186
FEATURE [Part::Cylinder] Cylinder187
  Angle = 360
  AttacherType = Attacher::AttachEngine3D
  Height = 30
  Placement = pos=(98,177,-30) rot=(0.799251,-0.424969,0.424969;1.79303rad)
  Radius = 48
FEATURE [Part::Cut] Cut298  label="Cut687"
  Base = -> Cut299
  Refine = true
  Tool = -> Cylinder187
FEATURE [Part::Box] Box247  label="Cube473"
  AttacherType = Attacher::AttachEngine3D
  Height = 7
  Length = 10
  Placement = pos=(48,147,-30) rot=(0,0,1;0rad)
  Width = 28
FEATURE [Part::Cut] Cut297  label="Cut686"
  Base = -> Cut298
  Refine = true
  Tool = -> Box247
FEATURE [Part::Box] Box248  label="Cube474"
  AttacherType = Attacher::AttachEngine3D
  Height = 7
  Length = 45
  Placement = pos=(76,175,14) rot=(0,0,1;0rad)
  Width = 2
FEATURE [Part::MultiFuse] Fusion133
  Refine = true
  Shapes = -> [Cut297,Box248]
FEATURE [Part::Box] Box249  label="Cube475"
  AttacherType = Attacher::AttachEngine3D
  Height = 14
  Length = 10
  Placement = pos=(116,168,12) rot=(0,1,0;0.401426rad)
  Width = 9
FEATURE [Part::Cut] Cut296
  Base = -> Fusion133
  Refine = true
  Tool = -> Box249
FEATURE [Part::MultiFuse] Fusion131
  Refine = true
  Shapes = -> [Part__Mirroring015,Box245,Cut296]
FEATURE [Part::Box] Box250  label="Cube476"
  AttacherType = Attacher::AttachEngine3D
  Height = 10
  Length = 10
  Placement = pos=(46,152,-31) rot=(0,1,0;0.785398rad)
  Width = 25
FEATURE [Part::Cut] Cut294  label="Cut684"
  Base = -> Fusion131
  Refine = true
  Tool = -> Box250
FEATURE [Part::Fillet] Fillet129
  Base = -> Cut294
  Edges = 1 edges r=1: [Edge14]
FEATURE [Part::Cylinder] Cylinder188
  Angle = 360
  AttacherType = Attacher::AttachEngine3D
  Height = 33
  Placement = pos=(98,175,-23) rot=(1,0,0;1.5708rad)
  Radius = 50
FEATURE [Part::Cylinder] Cylinder189
  Angle = 360
  AttacherType = Attacher::AttachEngine3D
  Height = 35
  Placement = pos=(98,177,-23) rot=(1,0,0;1.5708rad)
  Radius = 52
FEATURE [Part::Cylinder] Cylinder190
  Angle = 360
  AttacherType = Attacher::AttachEngine3D
  Height = 33
  Placement = pos=(98,177,-30) rot=(1,0,0;1.5708rad)
  Radius = 48
FEATURE [Part::MultiFuse] Fusion135
  Refine = true
  Shapes = -> [Cylinder188,Cylinder190]
FEATURE [Part::Cut] Cut300
  Base = -> Cylinder189
  Refine = true
  Tool = -> Fusion135
FEATURE [Part::Box] Box251  label="Cube477"
  AttacherType = Attacher::AttachEngine3D
  Height = 10
  Length = 6.5
  Placement = pos=(145.5,142,-33) rot=(0,0,1;0rad)
  Width = 35
FEATURE [Part::Box] Box252  label="Cube478"
  AttacherType = Attacher::AttachEngine3D
  Height = 10
  Length = 4.5
  Placement = pos=(143.5,140,-33) rot=(0,0,1;0rad)
  Width = 35
FEATURE [Part::Cut] Cut301
  Base = -> Box251
  Refine = true
  Tool = -> Box252
FEATURE [Part::MultiFuse] Fusion136
  Refine = true
  Shapes = -> [Cut300,Cut301]
FEATURE [Part::Chamfer] Chamfer044
  Base = -> Fusion136
  Edges = 1 edges r=1.99: [Edge8]
FEATURE [Part::Chamfer] Chamfer045
  Base = -> Chamfer044
  Edges = 1 edges r=2.49: [Edge30]
FEATURE [Part::Box] Box253  label="Cube479"
  AttacherType = Attacher::AttachEngine3D
  Height = 11
  Length = 7.5
  Placement = pos=(117.3,133.5,15) rot=(0,1,0;0.471239rad)
  Width = 35
FEATURE [Part::Cylinder] Cylinder192
  Angle = 360
  AttacherType = Attacher::AttachEngine3D
  Height = 23
  Placement = pos=(98,175,-23) rot=(0.829023,-0.395424,0.395424;1.75721rad)
  Radius = 50
FEATURE [Part::Cut] Cut302
  Base = -> Chamfer045
  Refine = true
  Tool = -> Box253
FEATURE [Part::Cylinder] Cylinder193
  Angle = 360
  AttacherType = Attacher::AttachEngine3D
  Height = 33
  Placement = pos=(98,175,-23) rot=(1,0,0;1.5708rad)
  Radius = 48
FEATURE [Part::Cut] Cut303
  Base = -> Cylinder192
  Refine = true
  Tool = -> Cylinder193
FEATURE [Part::MultiFuse] Fusion137
  Refine = true
  Shapes = -> [Cut302,Cut303]
FEATURE [Part::Chamfer] Chamfer046
  Base = -> Fusion137
  Edges = 1 edges r=1.99: [Edge50]
  Placement = pos=(1,0,-1) rot=(0,0,1;0rad)
FEATURE [Part::Fillet] Fillet132
  Base = -> Chamfer046
  Edges = 1 edges r=1: [Edge53]
FEATURE [Part::Cylinder] Cylinder194
  Angle = 360
  AttacherType = Attacher::AttachEngine3D
  Height = 10
  Placement = pos=(144,152,0) rot=(1,0,0;1.5708rad)
  Radius = 3
FEATURE [Part::Cylinder] Cylinder195
  Angle = 360
  AttacherType = Attacher::AttachEngine3D
  Height = 10
  Placement = pos=(144,152,0) rot=(1,0,0;1.5708rad)
  Radius = 1.5
FEATURE [Part::Cut] Cut304
  Base = -> Cylinder194
  Placement = pos=(-13,0,12) rot=(0,0,1;0rad)
  Refine = true
  Tool = -> Cylinder195
FEATURE [Part::Cylinder] Cylinder196
  Angle = 360
  AttacherType = Attacher::AttachEngine3D
  Height = 10
  Placement = pos=(144,152,0) rot=(1,0,0;1.5708rad)
  Radius = 3
FEATURE [Part::Cylinder] Cylinder197
  Angle = 360
  AttacherType = Attacher::AttachEngine3D
  Height = 10
  Placement = pos=(144,152,0) rot=(1,0,0;1.5708rad)
  Radius = 1.5
FEATURE [Part::Cut] Cut305
  Base = -> Cylinder196
  Placement = pos=(0,0,-6) rot=(0,0,1;0rad)
  Refine = true
  Tool = -> Cylinder197
FEATURE [Part::MultiFuse] Fusion138  label="right-rear-wing"
  Placement = pos=(0,0,8) rot=(0,0,1;0rad)
  Refine = true
  Shapes = -> [Fillet132,Cut305,Cut304]
FEATURE [Part::Cylinder] Cylinder198
  Angle = 360
  AttacherType = Attacher::AttachEngine3D
  Height = 35
  Placement = pos=(98,177,-23) rot=(1,0,0;1.5708rad)
  Radius = 52
FEATURE [Part::Cylinder] Cylinder199
  Angle = 360
  AttacherType = Attacher::AttachEngine3D
  Height = 33
  Placement = pos=(98,175,-23) rot=(1,0,0;1.5708rad)
  Radius = 50
FEATURE [Part::Cylinder] Cylinder200
  Angle = 360
  AttacherType = Attacher::AttachEngine3D
  Height = 33
  Placement = pos=(98,177,-30) rot=(1,0,0;1.5708rad)
  Radius = 48
FEATURE [Part::MultiFuse] Fusion142
  Refine = true
  Shapes = -> [Cylinder199,Cylinder200]
FEATURE [Part::Cut] Cut307
  Base = -> Cylinder198
  Refine = true
  Tool = -> Fusion142
FEATURE [Part::Box] Box254  label="Cube480"
  AttacherType = Attacher::AttachEngine3D
  Height = 10
  Length = 6.5
  Placement = pos=(145.5,142,-33) rot=(0,0,1;0rad)
  Width = 35
FEATURE [Part::Box] Box255  label="Cube481"
  AttacherType = Attacher::AttachEngine3D
  Height = 10
  Length = 4.5
  Placement = pos=(143.5,140,-33) rot=(0,0,1;0rad)
  Width = 35
FEATURE [Part::Cut] Cut308
  Base = -> Box254
  Refine = true
  Tool = -> Box255
FEATURE [Part::MultiFuse] Fusion141
  Refine = true
  Shapes = -> [Cut307,Cut308]
FEATURE [Part::Chamfer] Chamfer049
  Base = -> Fusion141
  Edges = 1 edges r=1.99: [Edge8]
FEATURE [Part::Chamfer] Chamfer048
  Base = -> Chamfer049
  Edges = 1 edges r=2.49: [Edge30]
FEATURE [Part::Box] Box256  label="Cube482"
  AttacherType = Attacher::AttachEngine3D
  Height = 11
  Length = 7.5
  Placement = pos=(117.3,133.5,15) rot=(0,1,0;0.471239rad)
  Width = 35
FEATURE [Part::Cut] Cut306
  Base = -> Chamfer048
  Refine = true
  Tool = -> Box256
FEATURE [Part::Cylinder] Cylinder201
  Angle = 360
  AttacherType = Attacher::AttachEngine3D
  Height = 23
  Placement = pos=(98,175,-23) rot=(0.829023,-0.395424,0.395424;1.75721rad)
  Radius = 50
FEATURE [Part::Cylinder] Cylinder202
  Angle = 360
  AttacherType = Attacher::AttachEngine3D
  Height = 33
  Placement = pos=(98,175,-23) rot=(1,0,0;1.5708rad)
  Radius = 48
FEATURE [Part::Cut] Cut309
  Base = -> Cylinder201
  Refine = true
  Tool = -> Cylinder202
FEATURE [Part::MultiFuse] Fusion140
  Refine = true
  Shapes = -> [Cut306,Cut309]
FEATURE [Part::Chamfer] Chamfer047
  Base = -> Fusion140
  Edges = 1 edges r=1.99: [Edge50]
  Placement = pos=(1,0,-1) rot=(0,0,1;0rad)
FEATURE [Part::Fillet] Fillet133
  Base = -> Chamfer047
  Edges = 1 edges r=1: [Edge53]
FEATURE [Part::Cylinder] Cylinder203
  Angle = 360
  AttacherType = Attacher::AttachEngine3D
  Height = 10
  Placement = pos=(144,152,0) rot=(1,0,0;1.5708rad)
  Radius = 3
FEATURE [Part::Cylinder] Cylinder204
  Angle = 360
  AttacherType = Attacher::AttachEngine3D
  Height = 10
  Placement = pos=(144,152,0) rot=(1,0,0;1.5708rad)
  Radius = 1.5
FEATURE [Part::Cut] Cut310
  Base = -> Cylinder203
  Placement = pos=(0,0,-6) rot=(0,0,1;0rad)
  Refine = true
  Tool = -> Cylinder204
FEATURE [Part::Cylinder] Cylinder205
  Angle = 360
  AttacherType = Attacher::AttachEngine3D
  Height = 10
  Placement = pos=(144,152,0) rot=(1,0,0;1.5708rad)
  Radius = 3
FEATURE [Part::Cylinder] Cylinder206
  Angle = 360
  AttacherType = Attacher::AttachEngine3D
  Height = 10
  Placement = pos=(144,152,0) rot=(1,0,0;1.5708rad)
  Radius = 1.5
FEATURE [Part::Cut] Cut311
  Base = -> Cylinder205
  Placement = pos=(-13,0,12) rot=(0,0,1;0rad)
  Refine = true
  Tool = -> Cylinder206
FEATURE [Part::MultiFuse] Fusion139  label="right-rear-wing001"
  Refine = true
  Shapes = -> [Fillet133,Cut310,Cut311]
FEATURE [Part::Mirroring] Part__Mirroring018  label="left-rear-wing"
  Base = (0,0,0)
  Normal = (0,1,0)
  Placement = pos=(0,170,9) rot=(0,0,1;0rad)
  Source = -> Fusion139
FEATURE [Part::MultiFuse] Fusion143  label="cab-upper-part-01"
  Refine = true
  Shapes = -> [Fillet123,Cut246]
FEATURE [Part::Box] Box257  label="Cube483"
  AttacherType = Attacher::AttachEngine3D
  Height = 34
  Length = 5
  Placement = pos=(7,38,2) rot=(0,0,1;0rad)
  Width = 94
FEATURE [Part::Chamfer] Chamfer050
  Base = -> Box257
  Edges = 1 edges r=4.99: [Edge6]
FEATURE [Part::Cylinder] Cylinder207
  Angle = 360
  AttacherType = Attacher::AttachEngine3D
  Height = 10
  Placement = pos=(12,57.5,21) rot=(0,1,0;1.5708rad)
  Radius = 1.25
FEATURE [Part::Cylinder] Cylinder208
  Angle = 360
  AttacherType = Attacher::AttachEngine3D
  Height = 10
  Placement = pos=(12,112.5,21) rot=(0,1,0;1.5708rad)
  Radius = 1.25
FEATURE [Part::Cylinder] Cylinder209
  Angle = 360
  AttacherType = Attacher::AttachEngine3D
  Height = 10
  Placement = pos=(12,85,16) rot=(0,1,0;1.5708rad)
  Radius = 1.25
FEATURE [Part::MultiFuse] Fusion144
  Placement = pos=(-7,0,0) rot=(0,0,1;0rad)
  Refine = true
  Shapes = -> [Cylinder207,Cylinder209,Cylinder208]
FEATURE [Part::MultiFuse] Fusion145
  Refine = true
  Shapes = -> [Cut262,Chamfer050]
FEATURE [Part::Cut] Cut312  label="cab-lower-part-02"
  Base = -> Fusion145
  Refine = true
  Tool = -> Fusion144
FEATURE [Part::Fillet] Fillet134
  Base = -> Cut287
  Edges = 2 edges r=1: [Edge4,Edge32]
FEATURE [Part::MultiFuse] Fusion146
  Refine = true
  Shapes = -> [Cut283,Fillet129,Fillet134]
FEATURE [Part::Mirroring] Part__Mirroring019  label="left-wing"
  Base = (0,0,0)
  Normal = (0,1,0)
  Placement = pos=(0,170,0) rot=(0,0,1;0rad)
  Source = -> Fusion146
FEATURE [Part::Fillet] Fillet135
  Base = -> Cut282
  Edges = 2 edges r=1: [Edge4,Edge32]
FEATURE [Part::MultiFuse] Fusion147  label="right-wing"
  Refine = true
  Shapes = -> [Cut275,Fillet128,Fillet135]
FEATURE [Part::Box] Box258  label="Cube484"
  AttacherType = Attacher::AttachEngine3D
  Height = 42
  Length = 58
  Placement = pos=(19.5,0,70) rot=(0,0,1;0rad)
  Width = 1
FEATURE [Part::Box] Box259  label="Cube485"
  AttacherType = Attacher::AttachEngine3D
  Height = 48
  Length = 11
  Placement = pos=(8.5,0,70) rot=(0,1,0;0.20944rad)
  Width = 5
FEATURE [Part::Cut] Cut313  label="Cut014369"
  Base = -> Box258
  Placement = pos=(0,0.5,0) rot=(0,0,1;0rad)
  Refine = true
  Tool = -> Box259
FEATURE [Part::Box] Box260  label="Cube486"
  AttacherType = Attacher::AttachEngine3D
  Height = 39
  Length = 59
  Placement = pos=(19,0,73.5) rot=(0,0,1;0rad)
  Width = 0.5
FEATURE [Part::Box] Box261  label="Cube487"
  AttacherType = Attacher::AttachEngine3D
  Height = 48
  Length = 11
  Placement = pos=(8,0,70) rot=(0,1,0;0.20944rad)
  Width = 5
FEATURE [Part::Cut] Cut314  label="Cut689"
  Base = -> Box260
  Refine = true
  Tool = -> Box261
FEATURE [Part::Box] Box262  label="Cube488"
  AttacherType = Attacher::AttachEngine3D
  Height = 35
  Length = 17
  Placement = pos=(20.5,0,75.5) rot=(0,0,1;0rad)
  Width = 5
FEATURE [Part::Box] Box263  label="Cube489"
  AttacherType = Attacher::AttachEngine3D
  Height = 48
  Length = 11
  Placement = pos=(9.5,0,70) rot=(0,1,0;0.20944rad)
  Width = 5
FEATURE [Part::Cut] Cut315  label="Cut690"
  Base = -> Box262
  Refine = true
  Tool = -> Box263
FEATURE [Part::Box] Box264  label="Cube490"
  AttacherType = Attacher::AttachEngine3D
  Height = 36
  Length = 37.5
  Placement = pos=(39,0,75) rot=(0,0,1;0rad)
  Width = 5
FEATURE [Part::Fillet] Fillet138
  Base = -> Box264
  Edges = 2 edges r=2.5: [Edge6,Edge8]
FEATURE [Part::Fillet] Fillet139
  Base = -> Fillet138
  Edges = 2 edges r=1: [Edge17,Edge18]
FEATURE [Part::Part2DObjectPython] ShapeString003  # Draft 2D object (typed FeaturePython)
  FontFile = <path>
  MapMode = 5
  Placement = pos=(57,0,71) rot=(1,0,0;1.5708rad)
  Size = 4
  String = 250-30
  Tracking = 0
FEATURE [Part::Extrusion] Extrude003
  Base = -> ShapeString003
  Dir = (0,1,0)
  DirMode = 0
  FaceMakerClass = Part::FaceMakerExtrusion
  LengthFwd = 0
  LengthRev = 0
  Placement = pos=(1,-0.25,-1.25) rot=(-1,0,0;0.036652rad)
  Solid = false
  Symmetric = false
FEATURE [Part::Box] Box278  label="Cube504"
  AttacherType = Attacher::AttachEngine3D
  Height = 39
  Length = 27
  Placement = pos=(89.5,0,74.5) rot=(0,0,1;0rad)
  Width = 0.5
FEATURE [Part::Fillet] Fillet161
  Base = -> Box278
  Edges = 4 edges r=3.5: [Edge2,Edge4,Edge6,Edge8]
  Placement = pos=(-3,-2,0) rot=(0,0,1;0rad)
FEATURE [Part::Box] Box279  label="Cube505"
  AttacherType = Attacher::AttachEngine3D
  Height = 36
  Length = 24
  Placement = pos=(89,0,74) rot=(0,0,1;0rad)
  Width = 6
FEATURE [Part::Fillet] Fillet162
  Base = -> Box279
  Edges = 4 edges r=2.5: [Edge2,Edge4,Edge6,Edge8]
  Placement = pos=(-1,-2,2) rot=(0,0,1;0rad)
FEATURE [Part::Box] Box280  label="Cube506"
  AttacherType = Attacher::AttachEngine3D
  Height = 42
  Length = 26
  Placement = pos=(90,0,71) rot=(0,0,1;0rad)
  Width = 1
FEATURE [Part::Fillet] Fillet163
  Base = -> Box280
  Edges = 4 edges r=3: [Edge2,Edge4,Edge6,Edge8]
  Placement = pos=(-3,-1.5,0) rot=(0,0,1;0rad)
FEATURE [Part::Box] Box281  label="Cube507"
  AttacherType = Attacher::AttachEngine3D
  Height = 44
  Length = 27
  Placement = pos=(89.5,0.25,69.5) rot=(0,0,1;0rad)
  Width = 0.25
FEATURE [Part::Fillet] Fillet164
  Base = -> Box281
  Edges = 4 edges r=3.5: [Edge2,Edge4,Edge6,Edge8]
  Placement = pos=(-3,-2,0) rot=(0,0,1;0rad)
FEATURE [Part::Fillet] Fillet165
  Base = -> Fillet161
  Edges = 2 edges r=0.49: [Edge1,Edge8]
FEATURE [Part::Fillet] Fillet166
  Base = -> Fillet164
  Edges = 2 edges r=0.24: [Edge1,Edge8]
FEATURE [Part::MultiFuse] Fusion156
  Refine = true
  Shapes = -> [Fillet166,Fillet165,Fillet163]
FEATURE [Part::Cut] Cut323  label="Cut691"
  Base = -> Fusion156
  Refine = true
  Tool = -> Fillet162
FEATURE [Part::Fillet] Fillet167  label="rear-left-window-frame"
  Base = -> Cut323
  Edges = 2 edges r=1: [Edge81,Edge85]
  Placement = pos=(-1,2,7) rot=(-1,0,0;0.036652rad)
FEATURE [Part::Box] Box282  label="Cube508"
  AttacherType = Attacher::AttachEngine3D
  Height = 39
  Length = 27
  Placement = pos=(89.5,0,74.5) rot=(0,0,1;0rad)
  Width = 0.5
FEATURE [Part::Box] Box283  label="Cube509"
  AttacherType = Attacher::AttachEngine3D
  Height = 44
  Length = 27
  Placement = pos=(89.5,0.25,69.5) rot=(0,0,1;0rad)
  Width = 0.25
FEATURE [Part::Box] Box284  label="Cube510"
  AttacherType = Attacher::AttachEngine3D
  Height = 42
  Length = 26
  Placement = pos=(90,0,71) rot=(0,0,1;0rad)
  Width = 1
FEATURE [Part::Fillet] Fillet169
  Base = -> Box284
  Edges = 4 edges r=3: [Edge2,Edge4,Edge6,Edge8]
  Placement = pos=(-3,-1.5,0) rot=(0,0,1;0rad)
FEATURE [Part::Box] Box285  label="Cube511"
  AttacherType = Attacher::AttachEngine3D
  Height = 36
  Length = 24
  Placement = pos=(89,0,74) rot=(0,0,1;0rad)
  Width = 6
FEATURE [Part::Fillet] Fillet171
  Base = -> Box282
  Edges = 4 edges r=3.5: [Edge2,Edge4,Edge6,Edge8]
  Placement = pos=(-3,-2,0) rot=(0,0,1;0rad)
FEATURE [Part::Fillet] Fillet172
  Base = -> Box285
  Edges = 4 edges r=2.5: [Edge2,Edge4,Edge6,Edge8]
  Placement = pos=(-1,-2,2) rot=(0,0,1;0rad)
FEATURE [Part::Fillet] Fillet173
  Base = -> Box283
  Edges = 4 edges r=3.5: [Edge2,Edge4,Edge6,Edge8]
  Placement = pos=(-3,-2,0) rot=(0,0,1;0rad)
FEATURE [Part::Fillet] Fillet170
  Base = -> Fillet173
  Edges = 2 edges r=0.24: [Edge1,Edge8]
FEATURE [Part::Fillet] Fillet174
  Base = -> Fillet171
  Edges = 2 edges r=0.49: [Edge1,Edge8]
FEATURE [Part::MultiFuse] Fusion157
  Refine = true
  Shapes = -> [Fillet170,Fillet174,Fillet169]
FEATURE [Part::Cut] Cut324  label="Cut692"
  Base = -> Fusion157
  Refine = true
  Tool = -> Fillet172
FEATURE [Part::Fillet] Fillet168  label="rear-left-window-frame001"
  Base = -> Cut324
  Edges = 2 edges r=1: [Edge81,Edge85]
  Placement = pos=(-1,2,-1) rot=(-1,0,0;0.036652rad)
FEATURE [Part::Mirroring] Part__Mirroring022  label="rear-right-window-frame"
  Base = (0,0,0)
  Normal = (0,1,0)
  Placement = pos=(0,170,8) rot=(0,0,1;0rad)
  Source = -> Fillet168
FEATURE [Part::Fillet] Fillet175
  Base = -> Cut314
  Edges = 4 edges r=3: [Edge6,Edge7,Edge8,Edge11]
FEATURE [Part::Box] Box286  label="Cube512"
  AttacherType = Attacher::AttachEngine3D
  Height = 44
  Length = 59
  Placement = pos=(19,0.25,68.5) rot=(0,0,1;0rad)
  Width = 0.25
FEATURE [Part::Box] Box287  label="Cube513"
  AttacherType = Attacher::AttachEngine3D
  Height = 48
  Length = 11
  Placement = pos=(8,0,69) rot=(0,1,0;0.20944rad)
  Width = 5
FEATURE [Part::Cut] Cut325  label="Cut693"
  Base = -> Box286
  Refine = true
  Tool = -> Box287
FEATURE [Part::Fillet] Fillet177
  Base = -> Cut313
  Edges = 4 edges r=3: [Edge6,Edge7,Edge8,Edge11]
FEATURE [Part::Fillet] Fillet178
  Base = -> Fillet175
  Edges = 2 edges r=0.49: [Edge4,Edge5]
FEATURE [Part::Fillet] Fillet180
  Base = -> Cut315
  Edges = 4 edges r=2.5: [Edge6,Edge7,Edge8,Edge11]
FEATURE [Part::MultiFuse] Fusion159
  Refine = true
  Shapes = -> [Fillet139,Fillet180]
FEATURE [Part::Part2DObjectPython] ShapeString005  # Draft 2D object (typed FeaturePython)
  FontFile = <path>
  MapMode = 5
  Placement = pos=(57,0,71) rot=(1,0,0;1.5708rad)
  Size = 4
  String = 250-30
  Tracking = 0
FEATURE [Part::Extrusion] Extrude005
  Base = -> ShapeString005
  Dir = (0,1,0)
  DirMode = 0
  FaceMakerClass = Part::FaceMakerExtrusion
  LengthFwd = 0
  LengthRev = 0
  Placement = pos=(130,170.324,-1.35235) rot=(0,-0.018325,0.999832;3.14159rad)
  Solid = false
  Symmetric = false
FEATURE [Part::Box] Box288  label="Cube514"
  AttacherType = Attacher::AttachEngine3D
  Height = 42
  Length = 58
  Placement = pos=(19.5,0,70) rot=(0,0,1;0rad)
  Width = 1
FEATURE [Part::Box] Box289  label="Cube515"
  AttacherType = Attacher::AttachEngine3D
  Height = 48
  Length = 11
  Placement = pos=(8.5,0,70) rot=(0,1,0;0.20944rad)
  Width = 5
FEATURE [Part::Cut] Cut328  label="Cut014370"
  Base = -> Box288
  Placement = pos=(0,0.5,0) rot=(0,0,1;0rad)
  Refine = true
  Tool = -> Box289
FEATURE [Part::Fillet] Fillet185
  Base = -> Cut328
  Edges = 4 edges r=3: [Edge6,Edge7,Edge8,Edge11]
FEATURE [Part::Box] Box290  label="Cube516"
  AttacherType = Attacher::AttachEngine3D
  Height = 39
  Length = 59
  Placement = pos=(19,0,73.5) rot=(0,0,1;0rad)
  Width = 0.5
FEATURE [Part::Box] Box291  label="Cube517"
  AttacherType = Attacher::AttachEngine3D
  Height = 48
  Length = 11
  Placement = pos=(8,0,70) rot=(0,1,0;0.20944rad)
  Width = 5
FEATURE [Part::Cut] Cut329  label="Cut695"
  Base = -> Box290
  Refine = true
  Tool = -> Box291
FEATURE [Part::Fillet] Fillet187
  Base = -> Cut329
  Edges = 4 edges r=3: [Edge6,Edge7,Edge8,Edge11]
FEATURE [Part::Fillet] Fillet186
  Base = -> Fillet187
  Edges = 2 edges r=0.49: [Edge4,Edge5]
FEATURE [Part::Box] Box292  label="Cube518"
  AttacherType = Attacher::AttachEngine3D
  Height = 44
  Length = 59
  Placement = pos=(19,0.25,68.5) rot=(0,0,1;0rad)
  Width = 0.25
FEATURE [Part::Box] Box293  label="Cube519"
  AttacherType = Attacher::AttachEngine3D
  Height = 48
  Length = 11
  Placement = pos=(8,0,69) rot=(0,1,0;0.20944rad)
  Width = 5
FEATURE [Part::Cut] Cut330  label="Cut696"
  Base = -> Box292
  Refine = true
  Tool = -> Box293
FEATURE [Part::Box] Box294  label="Cube520"
  AttacherType = Attacher::AttachEngine3D
  Height = 36
  Length = 37.5
  Placement = pos=(39,0,75) rot=(0,0,1;0rad)
  Width = 5
FEATURE [Part::Fillet] Fillet191
  Base = -> Box294
  Edges = 2 edges r=2.5: [Edge6,Edge8]
FEATURE [Part::Fillet] Fillet190
  Base = -> Fillet191
  Edges = 2 edges r=1: [Edge17,Edge18]
FEATURE [Part::Box] Box295  label="Cube521"
  AttacherType = Attacher::AttachEngine3D
  Height = 35
  Length = 17
  Placement = pos=(20.5,0,75.5) rot=(0,0,1;0rad)
  Width = 5
FEATURE [Part::Box] Box296  label="Cube522"
  AttacherType = Attacher::AttachEngine3D
  Height = 48
  Length = 11
  Placement = pos=(9.5,0,70) rot=(0,1,0;0.20944rad)
  Width = 5
FEATURE [Part::Cut] Cut331  label="Cut014371"
  Base = -> Box295
  Refine = true
  Tool = -> Box296
FEATURE [Part::Fillet] Fillet192
  Base = -> Cut331
  Edges = 4 edges r=2.5: [Edge6,Edge7,Edge8,Edge11]
FEATURE [Part::MultiFuse] Fusion161
  Refine = true
  Shapes = -> [Fillet190,Fillet192]
FEATURE [Part::Fillet] Fillet193
  Base = -> Cut325
  Edges = 4 edges r=3: [Edge6,Edge7,Edge8,Edge11]
FEATURE [Part::Fillet] Fillet194
  Base = -> Fillet193
  Edges = 2 edges r=0.24: [Edge4,Edge5]
FEATURE [Part::MultiFuse] Fusion163
  Refine = true
  Shapes = -> [Fillet177,Fillet178,Fillet194]
FEATURE [Part::Cut] Cut332  label="Cut014372"
  Base = -> Fusion163
  Refine = true
  Tool = -> Fusion159
FEATURE [Part::Fillet] Fillet195
  Base = -> Cut332
  Edges = 2 edges r=1: [Edge60,Edge64]
FEATURE [Part::Fillet] Fillet196
  Base = -> Fillet195
  Edges = 2 edges r=0.49: [Edge20,Edge24]
  Placement = pos=(0,0,0) rot=(-1,0,0;0.036652rad)
FEATURE [Part::MultiFuse] Fusion164  label="front-left-window-frame"
  Placement = pos=(0,0,8) rot=(0,0,1;0rad)
  Refine = true
  Shapes = -> [Fillet196,Extrude003]
FEATURE [Part::Fillet] Fillet197
  Base = -> Cut330
  Edges = 4 edges r=3: [Edge6,Edge7,Edge8,Edge11]
FEATURE [Part::MultiFuse] Fusion165
  Refine = true
  Shapes = -> [Fillet185,Fillet197,Fillet186]
FEATURE [Part::Cut] Cut333  label="Cut014373"
  Base = -> Fusion165
  Refine = true
  Tool = -> Fusion161
FEATURE [Part::Fillet] Fillet198
  Base = -> Cut333
  Edges = 1 edges r=1: [Edge114]
FEATURE [Part::Fillet] Fillet199
  Base = -> Fillet198
  Edges = 1 edges r=0.49: [Edge24]
  Placement = pos=(0,0,0) rot=(-1,0,0;0.036652rad)
FEATURE [Part::Mirroring] Part__Mirroring023  label="Fillet199 (Mirror #19)"
  Base = (0,0,0)
  Normal = (0,1,0)
  Placement = pos=(0,170,0) rot=(0,0,1;0rad)
  Source = -> Fillet199
FEATURE [Part::MultiFuse] Fusion166  label="front-right-window-frame"
  Placement = pos=(0,0,8) rot=(0,0,1;0rad)
  Refine = true
  Shapes = -> [Part__Mirroring023,Extrude005]
FEATURE [Part::Box] Box297  label="Cube523"
  AttacherType = Attacher::AttachEngine3D
  Height = 57
  Length = 8
  Placement = pos=(-0.5,6,67) rot=(0,1,0;0.244346rad)
  Width = 158
FEATURE [Part::Fillet] Fillet200
  Base = -> Box297
  Edges = 4 edges r=5: [Edge9,Edge10,Edge11,Edge12]
  Placement = pos=(6,0,-1) rot=(0,0,1;0rad)
FEATURE [Part::Feature] Face005
  Placement = pos=(0,0,-10) rot=(0,0,1;0rad)
  shape: bbox 128.7 x 180.4 x 2e-07 mm, 1 faces, 0 solids (baked)
FEATURE [Part::Feature] Face006
  Placement = pos=(0,0,50) rot=(0,0,1;0rad)
  shape: bbox 110 x 176 x 2e-07 mm, 1 faces, 0 solids (baked)
FEATURE [Part::Loft] Loft002
  Closed = false
  MaxDegree = 5
  Ruled = false
  Sections = -> [Face006,Face005]
  Solid = true
FEATURE [Part::Cut] Cut334  label="Cut014374"
  Base = -> Fillet200
  Refine = true
  Tool = -> Loft002
FEATURE [Part::Box] Box298  label="Cube524"
  AttacherType = Attacher::AttachEngine3D
  Height = 57
  Length = 6.5
  Placement = pos=(-0.5,6,67) rot=(0,1,0;0.244346rad)
  Width = 158
FEATURE [Part::Fillet] Fillet201
  Base = -> Box298
  Edges = 4 edges r=5: [Edge9,Edge10,Edge11,Edge12]
  Placement = pos=(6,0,-1) rot=(0,0,1;0rad)
FEATURE [Part::Cut] Cut335  label="Cut701"
  Base = -> Fillet201
  Placement = pos=(-1,0,0) rot=(0,0,1;0rad)
  Refine = true
  Tool = -> Cut334
FEATURE [Part::Feature] Face007
  Placement = pos=(0,0,-10) rot=(0,0,1;0rad)
  shape: bbox 128.7 x 180.4 x 2e-07 mm, 1 faces, 0 solids (baked)
FEATURE [Part::Feature] Face008
  Placement = pos=(0,0,50) rot=(0,0,1;0rad)
  shape: bbox 110 x 176 x 2e-07 mm, 1 faces, 0 solids (baked)
FEATURE [Part::Loft] Loft003
  Closed = false
  MaxDegree = 5
  Ruled = false
  Sections = -> [Face008,Face007]
  Solid = true
FEATURE [Part::Cut] Cut336  label="Cut702"
  Base = -> Cut335
  Refine = true
  Tool = -> Loft003
FEATURE [Part::Box] Box299  label="Cube525"
  AttacherType = Attacher::AttachEngine3D
  Height = 55
  Length = 10
  Placement = pos=(0,7,68) rot=(0,1,0;0.244346rad)
  Width = 156
FEATURE [Part::Fillet] Fillet202
  Base = -> Box299
  Edges = 4 edges r=5: [Edge9,Edge10,Edge11,Edge12]
  Placement = pos=(5,0,-1) rot=(0,0,1;0rad)
FEATURE [Part::Cut] Cut337  label="Cut703"
  Base = -> Cut336
  Refine = true
  Tool = -> Fillet202
FEATURE [Part::Box] Box300  label="Cube526"
  AttacherType = Attacher::AttachEngine3D
  Height = 55
  Length = 6
  Placement = pos=(0,7,68) rot=(0,1,0;0.244346rad)
  Width = 156
FEATURE [Part::Fillet] Fillet203
  Base = -> Box300
  Edges = 4 edges r=5: [Edge9,Edge10,Edge11,Edge12]
  Placement = pos=(6,0,-1) rot=(0,0,1;0rad)
FEATURE [Part::Box] Box301  label="Cube527"
  AttacherType = Attacher::AttachEngine3D
  Height = 57
  Length = 8
  Placement = pos=(-0.5,6,67) rot=(0,1,0;0.244346rad)
  Width = 158
FEATURE [Part::Fillet] Fillet204
  Base = -> Box301
  Edges = 4 edges r=5: [Edge9,Edge10,Edge11,Edge12]
  Placement = pos=(6,0,-1) rot=(0,0,1;0rad)
FEATURE [Part::Feature] Face009
  Placement = pos=(0,0,50) rot=(0,0,1;0rad)
  shape: bbox 110 x 176 x 2e-07 mm, 1 faces, 0 solids (baked)
FEATURE [Part::Feature] Face010
  Placement = pos=(0,0,-10) rot=(0,0,1;0rad)
  shape: bbox 128.7 x 180.4 x 2e-07 mm, 1 faces, 0 solids (baked)
FEATURE [Part::Loft] Loft004
  Closed = false
  MaxDegree = 5
  Ruled = false
  Sections = -> [Face009,Face010]
  Solid = true
FEATURE [Part::Cut] Cut339  label="Cut705"
  Base = -> Fillet204
  Refine = true
  Tool = -> Loft004
FEATURE [Part::Cut] Cut338  label="Cut704"
  Base = -> Fillet203
  Placement = pos=(-1,0,0) rot=(0,0,1;0rad)
  Refine = true
  Tool = -> Cut339
FEATURE [Part::Feature] Face011
  Placement = pos=(0,0,50) rot=(0,0,1;0rad)
  shape: bbox 110 x 176 x 2e-07 mm, 1 faces, 0 solids (baked)
FEATURE [Part::Feature] Face012
  Placement = pos=(0,0,-10) rot=(0,0,1;0rad)
  shape: bbox 128.7 x 180.4 x 2e-07 mm, 1 faces, 0 solids (baked)
FEATURE [Part::Loft] Loft005
  Closed = false
  MaxDegree = 5
  Placement = pos=(1,0,0) rot=(0,0,1;0rad)
  Ruled = false
  Sections = -> [Face011,Face012]
  Solid = true
FEATURE [Part::Cut] Cut340  label="Cut706"
  Base = -> Cut338
  Refine = true
  Tool = -> Loft005
FEATURE [Part::MultiFuse] Fusion167
  Refine = true
  Shapes = -> [Cut337,Cut340]
FEATURE [Part::Box] Box302  label="Cube528"
  AttacherType = Attacher::AttachEngine3D
  Height = 53
  Length = 10
  Placement = pos=(-1,8,69) rot=(0,1,0;0.244346rad)
  Width = 154
FEATURE [Part::Fillet] Fillet205
  Base = -> Box302
  Edges = 4 edges r=5: [Edge9,Edge10,Edge11,Edge12]
  Placement = pos=(6,0,-1) rot=(0,0,1;0rad)
FEATURE [Part::Cut] Cut341  label="Cut707"
  Base = -> Fusion167
  Refine = true
  Tool = -> Fillet205
FEATURE [Part::Fillet] Fillet206  label="windshield-frame"
  Base = -> Cut341
  Edges = 1 edges r=1: [Edge49]
  Placement = pos=(0,0,8) rot=(0,0,1;0rad)
FEATURE [Part::Box] Box303  label="Cube529"
  AttacherType = Attacher::AttachEngine3D
  Height = 39
  Length = 0.5
  Placement = pos=(175,0.5,0.5) rot=(0,0,1;0rad)
  Width = 26
FEATURE [Part::Box] Box304  label="Cube530"
  AttacherType = Attacher::AttachEngine3D
  Height = 42
  Length = 5
  Placement = pos=(175,-23.5,-1) rot=(-1,0,0;0.038397rad)
  Width = 24
FEATURE [Part::Cut] Cut342  label="Cut708"
  Base = -> Box303
  Placement = pos=(-57,16,73) rot=(0,0,1;0rad)
  Refine = true
  Tool = -> Box304
FEATURE [Part::Box] Box305  label="Cube531"
  AttacherType = Attacher::AttachEngine3D
  Height = 38
  Length = 1.5
  Placement = pos=(175,0,0) rot=(0,0,1;0rad)
  Width = 25
FEATURE [Part::Box] Box306  label="Cube532"
  AttacherType = Attacher::AttachEngine3D
  Height = 40
  Length = 5
  Placement = pos=(175,-24,-1) rot=(-1,0,0;0.038397rad)
  Width = 24
FEATURE [Part::Cut] Cut343  label="Cut709"
  Base = -> Box305
  Placement = pos=(-57,17,74) rot=(0,0,1;0rad)
  Refine = true
  Tool = -> Box306
FEATURE [Part::Fillet] Fillet208
  Base = -> Cut343
  Edges = 4 edges r=3: [Edge5,Edge7,Edge8,Edge11]
  Placement = pos=(3,0,0) rot=(0,0,1;0rad)
FEATURE [Part::Box] Box307  label="Cube533"
  AttacherType = Attacher::AttachEngine3D
  Height = 36
  Length = 5
  Placement = pos=(175,0,0) rot=(0,0,1;0rad)
  Width = 23
FEATURE [Part::Box] Box308  label="Cube534"
  AttacherType = Attacher::AttachEngine3D
  Height = 40
  Length = 5
  Placement = pos=(175,-24,-1) rot=(-1,0,0;0.038397rad)
  Width = 24
FEATURE [Part::Cut] Cut344  label="Cut710"
  Base = -> Box307
  Placement = pos=(-57,17,74) rot=(0,0,1;0rad)
  Refine = true
  Tool = -> Box308
FEATURE [Part::Fillet] Fillet209
  Base = -> Cut344
  Edges = 4 edges r=2.5: [Edge5,Edge7,Edge8,Edge11]
  Placement = pos=(0,1,1) rot=(0,0,1;0rad)
FEATURE [Part::Box] Box315  label="Cube541"
  AttacherType = Attacher::AttachEngine3D
  Height = 25
  Length = 5
  Placement = pos=(118,56,86) rot=(0,0,1;0rad)
  Width = 58
FEATURE [Part::Fillet] Fillet217
  Base = -> Box315
  Edges = 4 edges r=2: [Edge9,Edge10,Edge11,Edge12]
FEATURE [Part::Box] Box316  label="Cube542"
  AttacherType = Attacher::AttachEngine3D
  Height = 27
  Length = 1.5
  Placement = pos=(118,55,85) rot=(0,0,1;0rad)
  Width = 60
FEATURE [Part::Fillet] Fillet218
  Base = -> Box316
  Edges = 4 edges r=3: [Edge9,Edge10,Edge11,Edge12]
  Placement = pos=(3,0,0) rot=(0,0,1;0rad)
FEATURE [Part::Box] Box317  label="Cube543"
  AttacherType = Attacher::AttachEngine3D
  Height = 28
  Length = 0.5
  Placement = pos=(118,54.5,84.5) rot=(0,0,1;0rad)
  Width = 61
FEATURE [Part::Fillet] Fillet219
  Base = -> Box317
  Edges = 4 edges r=3.5: [Edge9,Edge10,Edge11,Edge12]
  Placement = pos=(4,0,0) rot=(0,0,1;0rad)
FEATURE [Part::Fillet] Fillet222
  Base = -> Cut342
  Edges = 4 edges r=4: [Edge5,Edge7,Edge8,Edge11]
  Placement = pos=(4,0,0) rot=(0,0,1;0rad)
FEATURE [Part::MultiFuse] Fusion171
  Refine = true
  Shapes = -> [Fillet222,Fillet208]
FEATURE [Part::Cut] Cut351  label="Cut711"
  Base = -> Fusion171
  Placement = pos=(3.5,0,-4) rot=(0,-1,0;0.034907rad)
  Refine = true
  Tool = -> Fillet209
FEATURE [Part::Fillet] Fillet223
  Base = -> Cut351
  Edges = 1 edges r=1: [Edge34]
FEATURE [Part::Fillet] Fillet224  label="back-left-window-frame"
  Base = -> Fillet223
  Edges = 1 edges r=0.49: [Edge9]
  Placement = pos=(0,0,8) rot=(0,0,1;0rad)
FEATURE [Part::Box] Box318  label="Cube544"
  AttacherType = Attacher::AttachEngine3D
  Height = 40
  Length = 5
  Placement = pos=(175,-24,-1) rot=(-1,0,0;0.038397rad)
  Width = 24
FEATURE [Part::Box] Box319  label="Cube545"
  AttacherType = Attacher::AttachEngine3D
  Height = 40
  Length = 5
  Placement = pos=(175,-24,-1) rot=(-1,0,0;0.038397rad)
  Width = 24
FEATURE [Part::Box] Box320  label="Cube546"
  AttacherType = Attacher::AttachEngine3D
  Height = 38
  Length = 1.5
  Placement = pos=(175,0,0) rot=(0,0,1;0rad)
  Width = 25
FEATURE [Part::Box] Box321  label="Cube547"
  AttacherType = Attacher::AttachEngine3D
  Height = 42
  Length = 5
  Placement = pos=(175,-23.5,-1) rot=(-1,0,0;0.038397rad)
  Width = 24
FEATURE [Part::Cut] Cut354  label="Cut714"
  Base = -> Box320
  Placement = pos=(-57,17,74) rot=(0,0,1;0rad)
  Refine = true
  Tool = -> Box319
FEATURE [Part::Box] Box322  label="Cube548"
  AttacherType = Attacher::AttachEngine3D
  Height = 39
  Length = 0.5
  Placement = pos=(175,0.5,0.5) rot=(0,0,1;0rad)
  Width = 26
FEATURE [Part::Box] Box323  label="Cube549"
  AttacherType = Attacher::AttachEngine3D
  Height = 36
  Length = 5
  Placement = pos=(175,0,0) rot=(0,0,1;0rad)
  Width = 23
FEATURE [Part::Cut] Cut353  label="Cut713"
  Base = -> Box323
  Placement = pos=(-57,17,74) rot=(0,0,1;0rad)
  Refine = true
  Tool = -> Box318
FEATURE [Part::Fillet] Fillet228
  Base = -> Cut353
  Edges = 4 edges r=2.5: [Edge5,Edge7,Edge8,Edge11]
  Placement = pos=(0,1,1) rot=(0,0,1;0rad)
FEATURE [Part::Cut] Cut355  label="Cut715"
  Base = -> Box322
  Placement = pos=(-57,16,73) rot=(0,0,1;0rad)
  Refine = true
  Tool = -> Box321
FEATURE [Part::Fillet] Fillet227
  Base = -> Cut355
  Edges = 4 edges r=4: [Edge5,Edge7,Edge8,Edge11]
  Placement = pos=(4,0,0) rot=(0,0,1;0rad)
FEATURE [Part::Fillet] Fillet229
  Base = -> Cut354
  Edges = 4 edges r=3: [Edge5,Edge7,Edge8,Edge11]
  Placement = pos=(3,0,0) rot=(0,0,1;0rad)
FEATURE [Part::MultiFuse] Fusion172
  Refine = true
  Shapes = -> [Fillet227,Fillet229]
FEATURE [Part::Cut] Cut352  label="Cut712"
  Base = -> Fusion172
  Placement = pos=(3.5,0,-4) rot=(0,-1,0;0.034907rad)
  Refine = true
  Tool = -> Fillet228
FEATURE [Part::Fillet] Fillet226
  Base = -> Cut352
  Edges = 1 edges r=1: [Edge34]
FEATURE [Part::Fillet] Fillet225  label="back-left-window-frame001"
  Base = -> Fillet226
  Edges = 1 edges r=0.49: [Edge9]
FEATURE [Part::Mirroring] Part__Mirroring024  label="back-right-window-frame"
  Base = (0,0,0)
  Normal = (0,1,0)
  Placement = pos=(0,170,8) rot=(0,0,1;0rad)
  Source = -> Fillet225
FEATURE [Part::MultiFuse] Fusion173
  Refine = true
  Shapes = -> [Fillet218,Fillet219]
FEATURE [Part::Cut] Cut356  label="Cut716"
  Base = -> Fusion173
  Refine = true
  Tool = -> Fillet217
FEATURE [Part::Fillet] Fillet230
  Base = -> Cut356
  Edges = 1 edges r=1: [Edge48]
FEATURE [Part::Fillet] Fillet231  label="back-window-frame"
  Base = -> Fillet230
  Edges = 1 edges r=0.49: [Edge40]
  Placement = pos=(3.5,0,4) rot=(0,-1,0;0.034907rad)
FEATURE [Part::Box] Box324  label="Cube550"
  AttacherType = Attacher::AttachEngine3D
  Height = 38
  Length = 8
  Placement = pos=(125,10,65) rot=(0,0,1;0rad)
  Width = 31
FEATURE [Part::Box] Box325  label="Cube551"
  AttacherType = Attacher::AttachEngine3D
  Height = 17.5
  Length = 8
  Placement = pos=(126,21,44) rot=(0,0,1;0rad)
  Width = 20
FEATURE [Part::Cone] Cone
  Angle = 360
  AttacherType = Attacher::AttachEngine3D
  Height = 5
  Placement = pos=(136,31,22) rot=(0,0,1;0rad)
  Radius1 = 10
  Radius2 = 7
FEATURE [Part::Feature] Face013
  Placement = pos=(-1,0,0) rot=(0,0,1;0rad)
  shape: bbox 8.8 x 22 x 2e-07 mm, 1 faces, 0 solids (baked)
FEATURE [Part::Feature] Face014
  Placement = pos=(0,0,-3) rot=(0,0,1;0rad)
  shape: bbox 21.12 x 16.6 x 2e-07 mm, 1 faces, 0 solids (baked)
FEATURE [Part::Cone] Cone001
  Angle = 360
  AttacherType = Attacher::AttachEngine3D
  Height = 8
  Placement = pos=(136,31,17) rot=(0,0,1;0rad)
  Radius1 = 10
  Radius2 = 7
FEATURE [Part::Cut] Cut357  label="Cut717"
  Base = -> Cone
  Refine = true
  Tool = -> Cone001
FEATURE [Part::Loft] Loft006
  Closed = false
  MaxDegree = 5
  Ruled = false
  Sections = -> [Face013,Face014]
  Solid = true
FEATURE [Part::Fillet] Fillet232
  Base = -> Cut357
  Edges = 1 edges r=1: [Edge3]
FEATURE [Part::MultiFuse] Fusion174
  Refine = true
  Shapes = -> [Box325,Loft006,Fillet232]
FEATURE [Part::Fillet] Fillet233
  Base = -> Fusion174
  Edges = 8 edges r=1: [Edge5,Edge7,Edge9,Edge10,Edge14,Edge15,Edge17,Edge19]
FEATURE [Part::Box] Box326  label="Cube552"
  AttacherType = Attacher::AttachEngine3D
  Height = 36
  Length = 1.25
  Placement = pos=(125.5,10,66) rot=(0,0,1;0rad)
  Width = 2
FEATURE [Part::Box] Box327  label="Cube553"
  AttacherType = Attacher::AttachEngine3D
  Height = 36
  Length = 1.25
  Placement = pos=(127.25,10,66) rot=(0,0,1;0rad)
  Width = 2
FEATURE [Part::Box] Box328  label="Cube554"
  AttacherType = Attacher::AttachEngine3D
  Height = 36
  Length = 1.25
  Placement = pos=(129,10,66) rot=(0,0,1;0rad)
  Width = 2
FEATURE [Part::Box] Box329  label="Cube555"
  AttacherType = Attacher::AttachEngine3D
  Height = 36
  Length = 1.25
  Placement = pos=(130.75,10,66) rot=(0,0,1;0rad)
  Width = 2
FEATURE [Part::MultiFuse] Fusion175
  Placement = pos=(0.25,0,0) rot=(0,0,1;0rad)
  Refine = true
  Shapes = -> [Box326,Box327,Box329,Box328]
FEATURE [Part::Cut] Cut358
  Base = -> Box324
  Refine = true
  Tool = -> Fusion175
FEATURE [Part::Box] Box330  label="Cube556"
  AttacherType = Attacher::AttachEngine3D
  Height = 0.5
  Length = 8
  Placement = pos=(125,10,78) rot=(0,0,1;0rad)
  Width = 2
FEATURE [Part::Box] Box331  label="Cube557"
  AttacherType = Attacher::AttachEngine3D
  Height = 0.5
  Length = 8
  Placement = pos=(125,10,90) rot=(0,0,1;0rad)
  Width = 2
FEATURE [Part::MultiFuse] Fusion176
  Refine = true
  Shapes = -> [Cut358,Box330,Box331]
FEATURE [Part::Box] Box332  label="Cube558"
  AttacherType = Attacher::AttachEngine3D
  Height = 2
  Length = 8
  Placement = pos=(125,21,63) rot=(0,0,1;0rad)
  Width = 20
FEATURE [Part::MultiFuse] Fusion177
  Refine = true
  Shapes = -> [Fusion176,Box332]
FEATURE [Part::Fillet] Fillet234
  Base = -> Fusion177
  Edges = 1 edges r=1.99: [Edge7]
FEATURE [Part::Fillet] Fillet235
  Base = -> Fillet234
  Edges = 1 edges r=3: [Edge30]
FEATURE [Part::Fillet] Fillet236
  Base = -> Fillet235
  Edges = 2 edges r=1: [Edge4,Edge20]
FEATURE [Part::Fillet] Fillet237
  Base = -> Fillet236
  Edges = 2 edges r=1: [Edge7,Edge29]
  Placement = pos=(2,0,-3) rot=(0,-1,0;0.034907rad)
FEATURE [Part::Feature] Face015
  shape: bbox 8.795 x 22 x 0.3071 mm, 1 faces, 0 solids (baked)
FEATURE [Part::Feature] Face016
  Placement = pos=(0,0,1.5) rot=(0,0,1;0rad)
  shape: bbox 8.801 x 22 x 2.006e-07 mm, 1 faces, 0 solids (baked)
FEATURE [Part::Loft] Loft007
  Closed = false
  MaxDegree = 5
  Ruled = false
  Sections = -> [Face015,Face016]
  Solid = true
FEATURE [Part::MultiFuse] Fusion178  label="air-intake-upper-00"
  Placement = pos=(0.5,0,0) rot=(0,0,1;0rad)
  Refine = true
  Shapes = -> [Fillet233,Loft007,Fillet237]
FEATURE [Part::Box] Box336  label="Cube562"
  AttacherType = Attacher::AttachEngine3D
  Height = 10
  Length = 10
  Placement = pos=(-2,71,-23) rot=(0,0,1;0rad)
  Width = 28
FEATURE [Part::Fillet] Fillet240
  Base = -> Box336
  Edges = 4 edges r=1: [Edge9,Edge10,Edge11,Edge12]
  Placement = pos=(0,0,1) rot=(0,0,1;0rad)
FEATURE [Part::Cut] Cut360  label="Cut719"
  Base = -> Cut182
  Refine = true
  Tool = -> Fillet240
FEATURE [Part::Box] Box337  label="Cube563"
  AttacherType = Attacher::AttachEngine3D
  Height = 10
  Length = 9.5
  Placement = pos=(-2,72,-22) rot=(0,0,1;0rad)
  Width = 26
FEATURE [Part::Box] Box338  label="Cube564"
  AttacherType = Attacher::AttachEngine3D
  Height = 8
  Length = 8
  Placement = pos=(-2,71,-21) rot=(0,0,1;0rad)
  Width = 28
FEATURE [Part::Cut] Cut361  label="Cut720"
  Base = -> Box337
  Refine = true
  Tool = -> Box338
FEATURE [Part::Fillet] Fillet241
  Base = -> Cut361
  Edges = 4 edges r=3: [Edge1,Edge3,Edge7,Edge16]
FEATURE [Part::Cylinder] Cylinder211
  Angle = 360
  AttacherType = Attacher::AttachEngine3D
  Height = 10
  Placement = pos=(2,85,-22) rot=(0,0,1;0rad)
  Radius = 1.6
FEATURE [Part::Cylinder] Cylinder212
  Angle = 360
  AttacherType = Attacher::AttachEngine3D
  Height = 10
  Placement = pos=(-2,85,-22) rot=(0,0,-1;1.5708rad)
  Radius = 10
FEATURE [Part::Box] Box339  label="Cube565"
  AttacherType = Attacher::AttachEngine3D
  Height = 8
  Length = 10
  Placement = pos=(-9,75,-21) rot=(0,0,1;0rad)
  Width = 20
FEATURE [Part::Cut] Cut362  label="Cut721"
  Base = -> Cylinder212
  Refine = true
  Tool = -> Box339
FEATURE [Part::Cylinder] Cylinder213
  Angle = 360
  AttacherType = Attacher::AttachEngine3D
  Height = 8
  Placement = pos=(-1,85,-21) rot=(0,0,-1;1.5708rad)
  Radius = 8.5
FEATURE [Part::Cut] Cut363  label="Cut722"
  Base = -> Cut362
  Refine = true
  Tool = -> Cylinder213
FEATURE [Part::MultiFuse] Fusion181
  Refine = true
  Shapes = -> [Fillet241,Cut363]
FEATURE [Part::Cylinder] Cylinder214
  Angle = 360
  AttacherType = Attacher::AttachEngine3D
  Height = 9
  Placement = pos=(2,85,-31) rot=(0,0,1;0rad)
  Radius = 3
FEATURE [Part::MultiFuse] Fusion182
  Refine = true
  Shapes = -> [Cut360,Cylinder214]
FEATURE [Part::Cylinder] Cylinder215
  Angle = 360
  AttacherType = Attacher::AttachEngine3D
  Height = 21
  Placement = pos=(2,85,-31) rot=(0,0,1;0rad)
  Radius = 1.6
FEATURE [Part::Cut] Cut364  label="bumper-01"
  Base = -> Fusion182
  Placement = pos=(0,0,8) rot=(0,0,1;0rad)
  Refine = true
  Tool = -> Cylinder215
FEATURE [Part::Cut] Cut365  label="Cut723"
  Base = -> Fusion181
  Placement = pos=(0.5,0,0) rot=(0,0,1;0rad)
  Refine = true
  Tool = -> Cylinder211
FEATURE [Part::Box] Box340  label="Cube566"
  AttacherType = Attacher::AttachEngine3D
  Height = 10
  Length = 10
  Placement = pos=(8,75,-22) rot=(0,0,1;0rad)
  Width = 20
FEATURE [Part::Cut] Cut366  label="bumper-insert-00"
  Base = -> Cut365
  Placement = pos=(0,0,8) rot=(0,0,1;0rad)
  Refine = true
  Tool = -> Box340
FEATURE [Part::Box] Box342  label="Cube568"
  AttacherType = Attacher::AttachEngine3D
  Height = 10
  Length = 29
  Placement = pos=(51,55,118) rot=(0,0,1;0rad)
  Width = 54
FEATURE [Part::Fillet] Fillet242
  Base = -> Box342
  Edges = 4 edges r=4: [Edge2,Edge6,Edge10,Edge12]
  Placement = pos=(3,3,0) rot=(0,0,1;0rad)
FEATURE [Part::Box] Box343  label="Cube569"
  AttacherType = Attacher::AttachEngine3D
  Height = 10
  Length = 29
  Placement = pos=(54,58,115.5) rot=(0,0,1;0rad)
  Width = 54
FEATURE [Part::Cut] Cut367  label="top-closer"
  Base = -> Fillet242
  Placement = pos=(0,0,8) rot=(0,0,1;0rad)
  Refine = true
  Tool = -> Box343
FEATURE [Part::Box] Box344  label="Cube570"
  AttacherType = Attacher::AttachEngine3D
  Height = 42
  Length = 26
  Placement = pos=(89,4.3,70) rot=(0,0,1;0rad)
  Width = 1
FEATURE [Part::Fillet] Fillet243
  Base = -> Box344
  Edges = 4 edges r=3: [Edge2,Edge4,Edge6,Edge8]
  Placement = pos=(-3,-2,0) rot=(0,0,1;0rad)
FEATURE [Part::Box] Box345  label="Cube571"
  AttacherType = Attacher::AttachEngine3D
  Height = 42
  Length = 58
  Placement = pos=(19.5,2,70) rot=(0,0,1;0rad)
  Width = 1
FEATURE [Part::Box] Box346  label="Cube572"
  AttacherType = Attacher::AttachEngine3D
  Height = 48
  Length = 11
  Placement = pos=(8.5,-2,70) rot=(-0.179679,0.983544,0.018885;0.212918rad)
  Width = 11
FEATURE [Part::Cut] Cut368  label="Cut724"
  Base = -> Box345
  Refine = true
  Tool = -> Box346
FEATURE [Part::Fillet] Fillet244
  Base = -> Cut368
  Edges = 4 edges r=3: [Edge6,Edge7,Edge8,Edge11]
FEATURE [Part::Box] Box347  label="Cube573"
  AttacherType = Attacher::AttachEngine3D
  Height = 40
  Length = 24
  Placement = pos=(90,4.3,71) rot=(0,0,1;0rad)
  Width = 5
FEATURE [Part::Fillet] Fillet245
  Base = -> Box347
  Edges = 4 edges r=2: [Edge2,Edge4,Edge6,Edge8]
  Placement = pos=(-3,-2,0) rot=(0,0,1;0rad)
FEATURE [Part::Cut] Cut369  label="Cut725"
  Base = -> Fillet243
  Placement = pos=(0,0.4,0) rot=(-1,0,0;0.034907rad)
  Refine = true
  Tool = -> Fillet245
FEATURE [Part::Box] Box348  label="Cube574"
  AttacherType = Attacher::AttachEngine3D
  Height = 48
  Length = 11
  Placement = pos=(9.5,-2,70) rot=(-0.179679,0.983544,0.018885;0.212918rad)
  Width = 11
FEATURE [Part::Box] Box349  label="Cube575"
  AttacherType = Attacher::AttachEngine3D
  Height = 40
  Length = 57
  Placement = pos=(19.5,2,71) rot=(0,0,1;0rad)
  Width = 5
FEATURE [Part::Cut] Cut370  label="Cut726"
  Base = -> Box349
  Refine = true
  Tool = -> Box348
FEATURE [Part::Fillet] Fillet246
  Base = -> Cut370
  Edges = 4 edges r=2.5: [Edge6,Edge7,Edge8,Edge11]
FEATURE [Part::Cut] Cut371  label="Cut727"
  Base = -> Fillet244
  Placement = pos=(0,0.7,0) rot=(-1,0,0;0.034907rad)
  Refine = true
  Tool = -> Fillet246
FEATURE [Part::Box] Box350  label="Cube576"
  AttacherType = Attacher::AttachEngine3D
  Height = 42
  Length = 26
  Placement = pos=(89,4.3,70) rot=(0,0,1;0rad)
  Width = 1
FEATURE [Part::Box] Box351  label="Cube577"
  AttacherType = Attacher::AttachEngine3D
  Height = 40
  Length = 24
  Placement = pos=(90,4.3,71) rot=(0,0,1;0rad)
  Width = 5
FEATURE [Part::Fillet] Fillet247
  Base = -> Box351
  Edges = 4 edges r=2: [Edge2,Edge4,Edge6,Edge8]
  Placement = pos=(-3,-2,0) rot=(0,0,1;0rad)
FEATURE [Part::Fillet] Fillet248
  Base = -> Box350
  Edges = 4 edges r=3: [Edge2,Edge4,Edge6,Edge8]
  Placement = pos=(-3,-2,0) rot=(0,0,1;0rad)
FEATURE [Part::Cut] Cut372  label="Cut728"
  Base = -> Fillet248
  Placement = pos=(0,0.4,0) rot=(-1,0,0;0.034907rad)
  Refine = true
  Tool = -> Fillet247
FEATURE [Part::Box] Box352  label="Cube578"
  AttacherType = Attacher::AttachEngine3D
  Height = 48
  Length = 11
  Placement = pos=(8.5,-2,70) rot=(-0.179679,0.983544,0.018885;0.212918rad)
  Width = 11
FEATURE [Part::Box] Box353  label="Cube579"
  AttacherType = Attacher::AttachEngine3D
  Height = 42
  Length = 58
  Placement = pos=(19.5,2,70) rot=(0,0,1;0rad)
  Width = 1
FEATURE [Part::Cut] Cut374  label="Cut730"
  Base = -> Box353
  Refine = true
  Tool = -> Box352
FEATURE [Part::Fillet] Fillet250
  Base = -> Cut374
  Edges = 4 edges r=3: [Edge6,Edge7,Edge8,Edge11]
FEATURE [Part::Box] Box354  label="Cube580"
  AttacherType = Attacher::AttachEngine3D
  Height = 40
  Length = 57
  Placement = pos=(19.5,2,71) rot=(0,0,1;0rad)
  Width = 5
FEATURE [Part::Box] Box355  label="Cube581"
  AttacherType = Attacher::AttachEngine3D
  Height = 48
  Length = 11
  Placement = pos=(9.5,-2,70) rot=(-0.179679,0.983544,0.018885;0.212918rad)
  Width = 11
FEATURE [Part::Cut] Cut375  label="Cut731"
  Base = -> Box354
  Refine = true
  Tool = -> Box355
FEATURE [Part::Fillet] Fillet249
  Base = -> Cut375
  Edges = 4 edges r=2.5: [Edge6,Edge7,Edge8,Edge11]
FEATURE [Part::Cut] Cut373  label="Cut729"
  Base = -> Fillet250
  Placement = pos=(0,0.7,0) rot=(-1,0,0;0.034907rad)
  Refine = true
  Tool = -> Fillet249
FEATURE [Part::Mirroring] Part__Mirroring025  label="Cut490 (Mirror #20)"
  Base = (0,0,0)
  Normal = (0,1,0)
  Placement = pos=(0,170,0) rot=(0,0,1;0rad)
  Source = -> Cut372
FEATURE [Part::Mirroring] Part__Mirroring026  label="Cut494 (Mirror #21)"
  Base = (0,0,0)
  Normal = (0,1,0)
  Placement = pos=(0,170,0) rot=(0,0,1;0rad)
  Source = -> Cut373
FEATURE [Part::Box] Box356  label="Cube582"
  AttacherType = Attacher::AttachEngine3D
  Height = 27
  Length = 1
  Placement = pos=(118,55,85) rot=(0,0,1;0rad)
  Width = 60
FEATURE [Part::Box] Box357  label="Cube583"
  AttacherType = Attacher::AttachEngine3D
  Height = 38
  Length = 1
  Placement = pos=(175,0,0) rot=(0,0,1;0rad)
  Width = 25
FEATURE [Part::Box] Box358  label="Cube584"
  AttacherType = Attacher::AttachEngine3D
  Height = 40
  Length = 5
  Placement = pos=(175,-24,-1) rot=(-1,0,0;0.038397rad)
  Width = 24
FEATURE [Part::Cut] Cut376  label="Cut732"
  Base = -> Box357
  Placement = pos=(-57,17,74) rot=(0,0,1;0rad)
  Refine = true
  Tool = -> Box358
FEATURE [Part::Fillet] Fillet251
  Base = -> Box356
  Edges = 4 edges r=3: [Edge9,Edge10,Edge11,Edge12]
FEATURE [Part::Fillet] Fillet252
  Base = -> Cut376
  Edges = 4 edges r=3: [Edge5,Edge7,Edge8,Edge11]
FEATURE [Part::Box] Box359  label="Cube585"
  AttacherType = Attacher::AttachEngine3D
  Height = 36
  Length = 1
  Placement = pos=(175,1,1) rot=(0,0,1;0rad)
  Width = 23
FEATURE [Part::Box] Box360  label="Cube586"
  AttacherType = Attacher::AttachEngine3D
  Height = 40
  Length = 5
  Placement = pos=(175,-23,-1) rot=(-1,0,0;0.038397rad)
  Width = 24
FEATURE [Part::Cut] Cut377  label="Cut733"
  Base = -> Box359
  Placement = pos=(-57,17,74) rot=(0,0,1;0rad)
  Refine = true
  Tool = -> Box360
FEATURE [Part::Fillet] Fillet253
  Base = -> Cut377
  Edges = 4 edges r=2.5: [Edge5,Edge7,Edge8,Edge11]
FEATURE [Part::Cut] Cut378  label="Cut734"
  Base = -> Fillet252
  Placement = pos=(4.3,0,-4) rot=(0,-1,0;0.034907rad)
  Refine = true
  Tool = -> Fillet253
FEATURE [Part::Box] Box361  label="Cube587"
  AttacherType = Attacher::AttachEngine3D
  Height = 25
  Length = 5
  Placement = pos=(118,56,86) rot=(0,0,1;0rad)
  Width = 58
FEATURE [Part::Fillet] Fillet254
  Base = -> Box361
  Edges = 4 edges r=2.5: [Edge9,Edge10,Edge11,Edge12]
FEATURE [Part::Cut] Cut379  label="Cut735"
  Base = -> Fillet251
  Placement = pos=(4.35,0,-3.95) rot=(0,-1,0;0.034907rad)
  Refine = true
  Tool = -> Fillet254
FEATURE [Part::Box] Box362  label="Cube588"
  AttacherType = Attacher::AttachEngine3D
  Height = 38
  Length = 1
  Placement = pos=(175,0,0) rot=(0,0,1;0rad)
  Width = 25
FEATURE [Part::Box] Box363  label="Cube589"
  AttacherType = Attacher::AttachEngine3D
  Height = 40
  Length = 5
  Placement = pos=(175,-24,-1) rot=(-1,0,0;0.038397rad)
  Width = 24
FEATURE [Part::Cut] Cut381  label="Cut737"
  Base = -> Box362
  Placement = pos=(-57,17,74) rot=(0,0,1;0rad)
  Refine = true
  Tool = -> Box363
FEATURE [Part::Fillet] Fillet255
  Base = -> Cut381
  Edges = 4 edges r=3: [Edge5,Edge7,Edge8,Edge11]
FEATURE [Part::Box] Box364  label="Cube590"
  AttacherType = Attacher::AttachEngine3D
  Height = 36
  Length = 1
  Placement = pos=(175,1,1) rot=(0,0,1;0rad)
  Width = 23
FEATURE [Part::Box] Box365  label="Cube591"
  AttacherType = Attacher::AttachEngine3D
  Height = 40
  Length = 5
  Placement = pos=(175,-23,-1) rot=(-1,0,0;0.038397rad)
  Width = 24
FEATURE [Part::Cut] Cut382  label="Cut738"
  Base = -> Box364
  Placement = pos=(-57,17,74) rot=(0,0,1;0rad)
  Refine = true
  Tool = -> Box365
FEATURE [Part::Fillet] Fillet256
  Base = -> Cut382
  Edges = 4 edges r=2.5: [Edge5,Edge7,Edge8,Edge11]
FEATURE [Part::Cut] Cut380  label="Cut736"
  Base = -> Fillet255
  Placement = pos=(4.3,0,-4) rot=(0,-1,0;0.034907rad)
  Refine = true
  Tool = -> Fillet256
FEATURE [Part::Mirroring] Part__Mirroring027  label="Cut508 (Mirror #22)"
  Base = (0,0,0)
  Normal = (0,1,0)
  Placement = pos=(0,170,0) rot=(0,0,1;0rad)
  Source = -> Cut380
FEATURE [Part::Feature] Face019
  Placement = pos=(0,0,-10) rot=(0,0,1;0rad)
  shape: bbox 128.7 x 180.4 x 2e-07 mm, 1 faces, 0 solids (baked)
FEATURE [Part::Feature] Face020
  Placement = pos=(0,0,50) rot=(0,0,1;0rad)
  shape: bbox 110 x 176 x 2e-07 mm, 1 faces, 0 solids (baked)
FEATURE [Part::Loft] Loft009
  Closed = false
  MaxDegree = 5
  Ruled = false
  Sections = -> [Face020,Face019]
  Solid = true
FEATURE [Part::Box] Box367  label="Cube593"
  AttacherType = Attacher::AttachEngine3D
  Height = 55
  Length = 10
  Placement = pos=(0,7,68) rot=(0,1,0;0.226893rad)
  Width = 156
FEATURE [Part::Fillet] Fillet257
  Base = -> Box367
  Edges = 4 edges r=5: [Edge9,Edge10,Edge11,Edge12]
  Placement = pos=(6,0,-1) rot=(0,0,1;0rad)
FEATURE [Part::Cut] Cut383  label="Cut739"
  Base = -> Fillet257
  Refine = true
  Tool = -> Loft009
FEATURE [Part::Box] Box368  label="Cube594"
  AttacherType = Attacher::AttachEngine3D
  Height = 55
  Length = 10
  Placement = pos=(0,7,68) rot=(0,1,0;0.226893rad)
  Width = 156
FEATURE [Part::Fillet] Fillet258
  Base = -> Box368
  Edges = 4 edges r=5: [Edge9,Edge10,Edge11,Edge12]
  Placement = pos=(6,0,-1) rot=(0,0,1;0rad)
FEATURE [Part::Cut] Cut384  label="Cut740"
  Base = -> Fillet258
  Refine = true
  Tool = -> Cut383
FEATURE [Part::Feature] Face021
  Placement = pos=(0,0,-10) rot=(0,0,1;0rad)
  shape: bbox 128.7 x 180.4 x 2e-07 mm, 1 faces, 0 solids (baked)
FEATURE [Part::Feature] Face022
  Placement = pos=(0,0,50) rot=(0,0,1;0rad)
  shape: bbox 110 x 176 x 2e-07 mm, 1 faces, 0 solids (baked)
FEATURE [Part::Loft] Loft010
  Closed = false
  MaxDegree = 5
  Placement = pos=(1,0,0) rot=(0,0,1;0rad)
  Ruled = false
  Sections = -> [Face022,Face021]
  Solid = true
FEATURE [Part::Box] Box369  label="Cube595"
  AttacherType = Attacher::AttachEngine3D
  Height = 53
  Length = 10
  Placement = pos=(0,8,69) rot=(0,1,0;0.226893rad)
  Width = 154
FEATURE [Part::Fillet] Fillet259
  Base = -> Box369
  Edges = 4 edges r=4.5: [Edge9,Edge10,Edge11,Edge12]
  Placement = pos=(6,0,-1) rot=(0,0,1;0rad)
FEATURE [Part::Cut] Cut385  label="Cut741"
  Base = -> Cut384
  Refine = true
  Tool = -> Loft010
FEATURE [Part::Cut] Cut386  label="Cut742"
  Base = -> Cut385
  Placement = pos=(1.9,0,-0.5) rot=(0,0,1;0rad)
  Refine = true
  Tool = -> Fillet259
FEATURE [Part::MultiFuse] Fusion183  label="windows-mounts"
  Placement = pos=(0,0,8) rot=(0,0,1;0rad)
  Refine = true
  Shapes = -> [Cut369,Part__Mirroring026,Part__Mirroring025,Cut371,Cut378,Cut379,Part__Mirroring027,Cut386]
FEATURE [Part::Cylinder] Cylinder216
  Angle = 360
  AttacherType = Attacher::AttachEngine3D
  Height = 10
  Placement = pos=(118,31,59.5) rot=(0,1,0;1.5708rad)
  Radius = 1.3
FEATURE [Part::Cylinder] Cylinder217
  Angle = 360
  AttacherType = Attacher::AttachEngine3D
  Height = 10
  Placement = pos=(118,31,46.5) rot=(0,1,0;1.5708rad)
  Radius = 1.3
FEATURE [Part::MultiFuse] Fusion184
  Refine = true
  Shapes = -> [Cylinder216,Cylinder217]
FEATURE [Part::Cylinder] Cylinder218
  Angle = 360
  AttacherType = Attacher::AttachEngine3D
  Height = 10
  Placement = pos=(118,31,46.5) rot=(0,1,0;1.5708rad)
  Radius = 0.9
FEATURE [Part::Cylinder] Cylinder219
  Angle = 360
  AttacherType = Attacher::AttachEngine3D
  Height = 10
  Placement = pos=(118,31,59.5) rot=(0,1,0;1.5708rad)
  Radius = 0.9
FEATURE [Part::MultiFuse] Fusion185
  Placement = pos=(4,0,0) rot=(0,0,1;0rad)
  Refine = true
  Shapes = -> [Cylinder219,Cylinder218]
FEATURE [Part::Cylinder] Cylinder220
  Angle = 360
  AttacherType = Attacher::AttachEngine3D
  Height = 2
  Placement = pos=(118,31,59.5) rot=(0,1,0;1.5708rad)
  Radius = 2
FEATURE [Part::Cylinder] Cylinder221
  Angle = 360
  AttacherType = Attacher::AttachEngine3D
  Height = 2
  Placement = pos=(118,31,46.5) rot=(0,1,0;1.5708rad)
  Radius = 2
FEATURE [Part::MultiFuse] Fusion186
  Placement = pos=(8,0,0) rot=(0,0,1;0rad)
  Refine = true
  Shapes = -> [Cylinder220,Cylinder221]
FEATURE [Part::MultiFuse] Fusion187
  Refine = true
  Shapes = -> [Fusion178,Fusion186]
FEATURE [Part::Cut] Cut387  label="air-intake-upper-01"
  Base = -> Fusion187
  Placement = pos=(0,0,8) rot=(0,0,1;0rad)
  Refine = true
  Tool = -> Fusion185
FEATURE [Part::Box] Box370  label="Cube596"
  AttacherType = Attacher::AttachEngine3D
  Height = 6
  Length = 2
  Placement = pos=(89,3,29) rot=(0,0,1;0rad)
  Width = 2
FEATURE [Part::Box] Box371  label="Cube597"
  AttacherType = Attacher::AttachEngine3D
  Height = 6
  Length = 2
  Placement = pos=(105,3,29) rot=(0,0,1;0rad)
  Width = 2
FEATURE [Part::MultiFuse] Fusion188
  Refine = true
  Shapes = -> [Box370,Box371]
FEATURE [Part::Chamfer] Chamfer051
  Base = -> Fusion188
  Edges = 2 edges r=1.99: [Edge8,Edge20]
FEATURE [Part::Box] Box372  label="Cube598"
  AttacherType = Attacher::AttachEngine3D
  Height = 6
  Length = 2
  Placement = pos=(89,3,29) rot=(0,0,1;0rad)
  Width = 2
FEATURE [Part::Box] Box373  label="Cube599"
  AttacherType = Attacher::AttachEngine3D
  Height = 6
  Length = 2
  Placement = pos=(105,3,29) rot=(0,0,1;0rad)
  Width = 2
FEATURE [Part::MultiFuse] Fusion189
  Refine = true
  Shapes = -> [Box372,Box373]
FEATURE [Part::Chamfer] Chamfer052
  Base = -> Fusion189
  Edges = 2 edges r=1.99: [Edge8,Edge20]
FEATURE [Part::Mirroring] Part__Mirroring028  label="Chamfer052 (Mirror #23)"
  Base = (0,0,0)
  Normal = (0,1,0)
  Placement = pos=(0,170,0) rot=(0,0,1;0rad)
  Source = -> Chamfer052
FEATURE [Part::Cut] Cut388  label="Cut743"
  Base = -> Cut312
  Refine = true
  Tool = -> Fusion184
FEATURE [Part::MultiFuse] Fusion190  label="cab-lower-part-03"
  Refine = true
  Shapes = -> [Cut388,Chamfer051,Part__Mirroring028]
FEATURE [Part::Box] Box374  label="Cube600"
  AttacherType = Attacher::AttachEngine3D
  Height = 1
  Length = 2
  Placement = pos=(14,4,0) rot=(0,0,1;0rad)
  Width = 1
FEATURE [Part::Box] Box376  label="Cube602"
  AttacherType = Attacher::AttachEngine3D
  Height = 1
  Length = 2
  Placement = pos=(14,4,32) rot=(0,0,1;0rad)
  Width = 1
FEATURE [Part::Box] Box377  label="Cube603"
  AttacherType = Attacher::AttachEngine3D
  Height = 1
  Length = 2
  Placement = pos=(14,1,60) rot=(0,0,1;0rad)
  Width = 1
FEATURE [Part::Box] Box378  label="Cube604"
  AttacherType = Attacher::AttachEngine3D
  Height = 1
  Length = 2
  Placement = pos=(81,1,32) rot=(0,0,1;0rad)
  Width = 1
FEATURE [Part::Box] Box379  label="Cube605"
  AttacherType = Attacher::AttachEngine3D
  Height = 1
  Length = 2
  Placement = pos=(81,1,60) rot=(0,0,1;0rad)
  Width = 1
FEATURE [Part::Box] Box380  label="Cube606"
  AttacherType = Attacher::AttachEngine3D
  Height = 1
  Length = 2
  Placement = pos=(81,4,64) rot=(0,0,1;0rad)
  Width = 1
FEATURE [Part::Box] Box381  label="Cube607"
  AttacherType = Attacher::AttachEngine3D
  Height = 1
  Length = 2
  Placement = pos=(81,5,90) rot=(0,0,1;0rad)
  Width = 1
FEATURE [Part::MultiFuse] Fusion191
  Refine = true
  Shapes = -> [Box374,Box379,Box377,Box376,Box378]
FEATURE [Part::Box] Box382  label="Cube608"
  AttacherType = Attacher::AttachEngine3D
  Height = 1
  Length = 2
  Placement = pos=(81,1,60) rot=(0,0,1;0rad)
  Width = 1
FEATURE [Part::Box] Box383  label="Cube609"
  AttacherType = Attacher::AttachEngine3D
  Height = 1
  Length = 2
  Placement = pos=(14,1,60) rot=(0,0,1;0rad)
  Width = 1
FEATURE [Part::Box] Box384  label="Cube610"
  AttacherType = Attacher::AttachEngine3D
  Height = 1
  Length = 2
  Placement = pos=(14,4,32) rot=(0,0,1;0rad)
  Width = 1
FEATURE [Part::Box] Box385  label="Cube611"
  AttacherType = Attacher::AttachEngine3D
  Height = 1
  Length = 2
  Placement = pos=(81,1,32) rot=(0,0,1;0rad)
  Width = 1
FEATURE [Part::Box] Box386  label="Cube612"
  AttacherType = Attacher::AttachEngine3D
  Height = 1
  Length = 2
  Placement = pos=(14,4,0) rot=(0,0,1;0rad)
  Width = 1
FEATURE [Part::MultiFuse] Fusion192
  Refine = true
  Shapes = -> [Box386,Box382,Box383,Box384,Box385]
FEATURE [Part::Mirroring] Part__Mirroring029  label="Fusion192 (Mirror #24)"
  Base = (0,0,0)
  Normal = (0,1,0)
  Placement = pos=(0,170,0) rot=(0,0,1;0rad)
  Source = -> Fusion192
FEATURE [Part::Box] Box387  label="Cube613"
  AttacherType = Attacher::AttachEngine3D
  Height = 1
  Length = 2
  Placement = pos=(80,5,115.5) rot=(0,0,1;0rad)
  Width = 2
FEATURE [Part::Box] Box388  label="Cube614"
  AttacherType = Attacher::AttachEngine3D
  Height = 1
  Length = 2
  Placement = pos=(15,5,64) rot=(0,0,1;0rad)
  Width = 1
FEATURE [Part::Box] Box389  label="Cube615"
  AttacherType = Attacher::AttachEngine3D
  Height = 1
  Length = 2
  Placement = pos=(21,5,90) rot=(0,0,1;0rad)
  Width = 1
FEATURE [Part::Box] Box390  label="Cube616"
  AttacherType = Attacher::AttachEngine3D
  Height = 1
  Length = 2
  Placement = pos=(26.5,5.4,115.5) rot=(0,0,1;0rad)
  Width = 2
FEATURE [Part::Box] Box391  label="Cube617"
  AttacherType = Attacher::AttachEngine3D
  Height = 1
  Length = 2
  Placement = pos=(37,6,115.5) rot=(0,0,1;0rad)
  Width = 1
FEATURE [Part::Box] Box392  label="Cube618"
  AttacherType = Attacher::AttachEngine3D
  Height = 1
  Length = 2
  Placement = pos=(53,6,115.5) rot=(0,0,1;0rad)
  Width = 1
FEATURE [Part::Box] Box393  label="Cube619"
  AttacherType = Attacher::AttachEngine3D
  Height = 1
  Length = 2
  Placement = pos=(70,6,115.5) rot=(0,0,1;0rad)
  Width = 1
FEATURE [Part::MultiFuse] Fusion194
  Refine = true
  Shapes = -> [Box380,Box381,Box387,Box388,Box389,Box390,Box391,Box392,Box393]
FEATURE [Part::Box] Box394  label="Cube620"
  AttacherType = Attacher::AttachEngine3D
  Height = 1
  Length = 2
  Placement = pos=(80,5,115.5) rot=(0,0,1;0rad)
  Width = 2
FEATURE [Part::Box] Box395  label="Cube621"
  AttacherType = Attacher::AttachEngine3D
  Height = 1
  Length = 2
  Placement = pos=(53,6,115.5) rot=(0,0,1;0rad)
  Width = 1
FEATURE [Part::Box] Box396  label="Cube622"
  AttacherType = Attacher::AttachEngine3D
  Height = 1
  Length = 2
  Placement = pos=(70,6,115.5) rot=(0,0,1;0rad)
  Width = 1
FEATURE [Part::Box] Box397  label="Cube623"
  AttacherType = Attacher::AttachEngine3D
  Height = 1
  Length = 2
  Placement = pos=(15,5,64) rot=(0,0,1;0rad)
  Width = 1
FEATURE [Part::Box] Box398  label="Cube624"
  AttacherType = Attacher::AttachEngine3D
  Height = 1
  Length = 2
  Placement = pos=(21,5,90) rot=(0,0,1;0rad)
  Width = 1
FEATURE [Part::Box] Box399  label="Cube625"
  AttacherType = Attacher::AttachEngine3D
  Height = 1
  Length = 2
  Placement = pos=(37,6,115.5) rot=(0,0,1;0rad)
  Width = 1
FEATURE [Part::Box] Box400  label="Cube626"
  AttacherType = Attacher::AttachEngine3D
  Height = 1
  Length = 2
  Placement = pos=(26.5,5.4,115.5) rot=(0,0,1;0rad)
  Width = 2
FEATURE [Part::Box] Box401  label="Cube627"
  AttacherType = Attacher::AttachEngine3D
  Height = 1
  Length = 2
  Placement = pos=(81,5,90) rot=(0,0,1;0rad)
  Width = 1
FEATURE [Part::Box] Box402  label="Cube628"
  AttacherType = Attacher::AttachEngine3D
  Height = 1
  Length = 2
  Placement = pos=(81,4,64) rot=(0,0,1;0rad)
  Width = 1
FEATURE [Part::MultiFuse] Fusion195
  Refine = true
  Shapes = -> [Box402,Box401,Box394,Box397,Box398,Box400,Box399,Box395,Box396]
FEATURE [Part::Mirroring] Part__Mirroring030  label="Fusion195 (Mirror #25)"
  Base = (0,0,0)
  Normal = (0,1,0)
  Placement = pos=(0,170,0) rot=(0,0,1;0rad)
  Source = -> Fusion195
FEATURE [Part::MultiFuse] Fusion196  label="doors-retainers-upper-part"
  Placement = pos=(0,0,8) rot=(0,0,1;0rad)
  Refine = true
  Shapes = -> [Fusion194,Part__Mirroring030]
FEATURE [Part::MultiFuse] Fusion197  label="doors-retainers-lower-part"
  Placement = pos=(0,0,8) rot=(0,0,1;0rad)
  Refine = true
  Shapes = -> [Part__Mirroring029,Fusion191]
FEATURE [Part::Chamfer] Chamfer053  label="cab-lower-part-04"
  Base = -> Fusion190
  Edges = 1 edges r=0.9: [Edge492]
FEATURE [Part::Cylinder] Cylinder222
  Angle = 360
  AttacherType = Attacher::AttachEngine3D
  Height = 10
  Placement = pos=(15,15,10) rot=(0,0,1;0rad)
  Radius = 13.5
FEATURE [Part::Cylinder] Cylinder223
  Angle = 360
  AttacherType = Attacher::AttachEngine3D
  Height = 10
  Placement = pos=(15,15,10) rot=(0,0,1;0rad)
  Radius = 13.5
FEATURE [Part::Cut] Cut390  label="left-deflector_02"
  Base = -> Cut260
  Placement = pos=(0,0,8) rot=(0,0,1;0rad)
  Refine = true
  Tool = -> Cylinder222
FEATURE [Part::Cut] Cut391  label="Cut744"
  Base = -> Cut264
  Refine = true
  Tool = -> Cylinder223
FEATURE [Part::Mirroring] Part__Mirroring031  label="right-deflector_02"
  Base = (0,0,0)
  Normal = (0,1,0)
  Placement = pos=(0,170,8) rot=(0,0,1;0rad)
  Source = -> Cut391
FEATURE [Part::Cylinder] Cylinder224
  Angle = 360
  AttacherType = Attacher::AttachEngine3D
  Height = 25
  Placement = pos=(15,15,5) rot=(0,0,1;0rad)
  Radius = 13.5
FEATURE [Part::Cylinder] Cylinder225
  Angle = 360
  AttacherType = Attacher::AttachEngine3D
  Height = 25
  Placement = pos=(15,15,5) rot=(0,0,1;0rad)
  Radius = 15.5
FEATURE [Part::Cut] Cut392  label="Cut745"
  Base = -> Cylinder225
  Refine = true
  Tool = -> Cylinder224
FEATURE [Part::Cylinder] Cylinder226
  Angle = 360
  AttacherType = Attacher::AttachEngine3D
  Height = 25
  Placement = pos=(15,15,5) rot=(0,0,1;0rad)
  Radius = 13.5
FEATURE [Part::Cylinder] Cylinder227
  Angle = 360
  AttacherType = Attacher::AttachEngine3D
  Height = 25
  Placement = pos=(15,15,5) rot=(0,0,1;0rad)
  Radius = 15.5
FEATURE [Part::Cut] Cut393  label="Cut746"
  Base = -> Cylinder227
  Refine = true
  Tool = -> Cylinder226
FEATURE [Part::Mirroring] Part__Mirroring032  label="Cut522 (Mirror #25)"
  Base = (0,0,0)
  Normal = (0,1,0)
  Placement = pos=(0,170,0) rot=(0,0,1;0rad)
  Source = -> Cut393
FEATURE [Part::MultiFuse] Fusion198
  Placement = pos=(-0.5,0,0) rot=(0,0,1;0rad)
  Refine = true
  Shapes = -> [Part__Mirroring032,Cut392]
FEATURE [Part::Cut] Cut394  label="Cut747"
  Base = -> Cut094
  Refine = true
  Tool = -> Fusion198
FEATURE [Part::MultiFuse] Fusion199
  Refine = true
  Shapes = -> [Cut099,Cut394]
FEATURE [Part::Cut] Cut395  label="Cut748"
  Base = -> Fusion199
  Refine = true
  Tool = -> Fusion065
FEATURE [Part::MultiFuse] Fusion200
  Refine = true
  Shapes = -> [Part__Mirroring008,Fillet106]
FEATURE [Part::Chamfer] Chamfer054
  Base = -> Cut395
  Edges = 5 edges r=1: [Edge9,Edge64,Edge71,Edge89,Edge97]
FEATURE [Part::MultiFuse] Fusion201
  Refine = true
  Shapes = -> [Chamfer054,Fusion200]
FEATURE [Part::Cut] Cut396  label="front-panel-01"
  Base = -> Fusion201
  Placement = pos=(0,0,8) rot=(0,0,1;0rad)
  Refine = true
  Tool = -> Fusion116
FEATURE [Part::Cylinder] Cylinder228
  Angle = 360
  AttacherType = Attacher::AttachEngine3D
  Height = 10
  Placement = pos=(30,11,114) rot=(1,0,0;1.5708rad)
  Radius = 1
FEATURE [Part::Cylinder] Cylinder229
  Angle = 360
  AttacherType = Attacher::AttachEngine3D
  Height = 10
  Placement = pos=(26,11,66) rot=(1,0,0;1.5708rad)
  Radius = 1
FEATURE [Part::MultiFuse] Fusion202
  Refine = true
  Shapes = -> [Cylinder228,Cylinder229]
FEATURE [Part::Cylinder] Cylinder230
  Angle = 360
  AttacherType = Attacher::AttachEngine3D
  Height = 10
  Placement = pos=(26,11,66) rot=(1,0,0;1.5708rad)
  Radius = 1
FEATURE [Part::Cylinder] Cylinder231
  Angle = 360
  AttacherType = Attacher::AttachEngine3D
  Height = 10
  Placement = pos=(30,11,114) rot=(1,0,0;1.5708rad)
  Radius = 1
FEATURE [Part::MultiFuse] Fusion203
  Refine = true
  Shapes = -> [Cylinder231,Cylinder230]
FEATURE [Part::Mirroring] Part__Mirroring033  label="Fusion203 (Mirror #26)"
  Base = (0,0,0)
  Normal = (0,1,0)
  Placement = pos=(0,170,0) rot=(0,0,1;0rad)
  Source = -> Fusion203
FEATURE [Part::MultiFuse] Fusion204
  Refine = true
  Shapes = -> [Fusion202,Part__Mirroring033]
FEATURE [Part::Cylinder] Cylinder232
  Angle = 360
  AttacherType = Attacher::AttachEngine3D
  Height = 10
  Placement = pos=(119,65,45) rot=(0,1,0;1.5708rad)
  Radius = 1
FEATURE [Part::Cylinder] Cylinder233
  Angle = 360
  AttacherType = Attacher::AttachEngine3D
  Height = 10
  Placement = pos=(119,105,45) rot=(0,1,0;1.5708rad)
  Radius = 1
FEATURE [Part::MultiFuse] Fusion205
  Placement = pos=(0,0,2) rot=(0,0,1;0rad)
  Refine = true
  Shapes = -> [Cylinder232,Cylinder233]
FEATURE [Part::Cut] Cut397  label="cab-upper-part-02"
  Base = -> Fusion143
  Placement = pos=(0,0,8) rot=(0,0,1;0rad)
  Refine = true
  Tool = -> Fusion204
FEATURE [Part::Cut] Cut398  label="cab-lower-part-05"
  Base = -> Chamfer053
  Placement = pos=(0,0,8) rot=(0,0,1;0rad)
  Refine = true
  Tool = -> Fusion205
FEATURE [Part::Cylinder] Cylinder236
  Angle = 360
  AttacherType = Attacher::AttachEngine3D
  Height = 62
  Placement = pos=(25,21,0) rot=(0,0,1;3.28122rad)
  Radius = 29
FEATURE [Part::Cylinder] Cylinder237
  Angle = 360
  AttacherType = Attacher::AttachEngine3D
  Height = 62
  Placement = pos=(25,21,0) rot=(0,0,1;0rad)
  Radius = 18
FEATURE [Part::Cut] Cut401  label="Cut749"
  Base = -> Cylinder236
  Refine = true
  Tool = -> Cylinder237
FEATURE [Part::Box] Box406  label="Cube632"
  AttacherType = Attacher::AttachEngine3D
  Height = 2
  Length = 48
  Placement = pos=(5,3,0) rot=(0,0,1;0rad)
  Width = 15
FEATURE [Part::Cylinder] Cylinder238
  Angle = 360
  AttacherType = Attacher::AttachEngine3D
  Height = 62
  Placement = pos=(25,21,0) rot=(0,0,1;0rad)
  Radius = 16.5
FEATURE [Part::Cylinder] Cylinder239
  Angle = 360
  AttacherType = Attacher::AttachEngine3D
  Height = 62
  Placement = pos=(25,21,0) rot=(0,0,1;3.3074rad)
  Radius = 18
FEATURE [Part::Cut] Cut402  label="Cut750"
  Base = -> Cylinder239
  Refine = true
  Tool = -> Cylinder238
FEATURE [Part::Cut] Cut403  label="Cut751"
  Base = -> Box406
  Refine = true
  Tool = -> Cut401
FEATURE [Part::Box] Box407  label="Cube633"
  AttacherType = Attacher::AttachEngine3D
  Height = 62
  Length = 3
  Placement = pos=(6,18,0) rot=(0,0,1;0rad)
  Width = 1
FEATURE [Part::Cut] Cut404  label="Cut752"
  Base = -> Cut402
  Refine = true
  Tool = -> Box407
FEATURE [Part::Cylinder] Cylinder240
  Angle = 360
  AttacherType = Attacher::AttachEngine3D
  Height = 22
  Placement = pos=(98,18,-23) rot=(1,0,0;1.5708rad)
  Radius = 52
FEATURE [Part::Cut] Cut405  label="Cut753"
  Base = -> Cut403
  Refine = true
  Tool = -> Cylinder240
FEATURE [Part::Cylinder] Cylinder241
  Angle = 360
  AttacherType = Attacher::AttachEngine3D
  Height = 13
  Placement = pos=(11.9886,10.7385,16) rot=(0.884029,-0.330525,-0.330525;1.69375rad)
  Radius = 1.2
FEATURE [Part::Cylinder] Cylinder242
  Angle = 360
  AttacherType = Attacher::AttachEngine3D
  Height = 13
  Placement = pos=(11.9886,10.7385,51) rot=(0.884029,-0.330525,-0.330525;1.69375rad)
  Radius = 1.2
FEATURE [Part::MultiFuse] Fusion206
  Placement = pos=(0.87,1,0) rot=(0,0,1;0rad)
  Refine = true
  Shapes = -> [Cylinder241,Cylinder242]
FEATURE [Part::Cylinder] Cylinder243
  Angle = 360
  AttacherType = Attacher::AttachEngine3D
  Height = 1.6
  Placement = pos=(11.9886,10.7385,16) rot=(0.884029,-0.330525,-0.330525;1.69375rad)
  Radius = 2
FEATURE [Part::Cylinder] Cylinder244
  Angle = 360
  AttacherType = Attacher::AttachEngine3D
  Height = 1.6
  Placement = pos=(11.9886,10.7385,51) rot=(0.884029,-0.330525,-0.330525;1.69375rad)
  Radius = 2
FEATURE [Part::MultiFuse] Fusion207
  Placement = pos=(0.87,1,0) rot=(0,0,1;0rad)
  Refine = true
  Shapes = -> [Cylinder243,Cylinder244]
FEATURE [Part::MultiFuse] Fusion208
  Refine = true
  Shapes = -> [Cut404,Cut405,Fusion207]
FEATURE [Part::Cut] Cut406  label="Cut754"
  Base = -> Fusion208
  Refine = true
  Tool = -> Fusion206
FEATURE [Part::Cylinder] Cylinder245
  Angle = 360
  AttacherType = Attacher::AttachEngine3D
  Height = 10
  Placement = pos=(18,15,-5) rot=(0,0,1;0rad)
  Radius = 0.9
FEATURE [Part::Cylinder] Cylinder246
  Angle = 360
  AttacherType = Attacher::AttachEngine3D
  Height = 10
  Placement = pos=(49,15,-5) rot=(0,0,1;0rad)
  Radius = 0.9
FEATURE [Part::MultiFuse] Fusion209
  Refine = true
  Shapes = -> [Cylinder245,Cylinder246]
FEATURE [Part::Cylinder] Cylinder247
  Angle = 360
  AttacherType = Attacher::AttachEngine3D
  Height = 10
  Placement = pos=(18,15,-5) rot=(0,0,1;0rad)
  Radius = 1.2
FEATURE [Part::Cylinder] Cylinder248
  Angle = 360
  AttacherType = Attacher::AttachEngine3D
  Height = 10
  Placement = pos=(49,15,-5) rot=(0,0,1;0rad)
  Radius = 1.2
FEATURE [Part::MultiFuse] Fusion210
  Refine = true
  Shapes = -> [Cylinder247,Cylinder248]
FEATURE [Part::Cut] Cut407  label="Cut755"
  Base = -> Cut406
  Refine = true
  Tool = -> Fusion210
FEATURE [Part::Cylinder] Cylinder249
  Angle = 360
  AttacherType = Attacher::AttachEngine3D
  Height = 10
  Placement = pos=(18,15,-5) rot=(0,0,1;0rad)
  Radius = 0.9
FEATURE [Part::Cylinder] Cylinder250
  Angle = 360
  AttacherType = Attacher::AttachEngine3D
  Height = 10
  Placement = pos=(49,15,-5) rot=(0,0,1;0rad)
  Radius = 0.9
FEATURE [Part::MultiFuse] Fusion211
  Refine = true
  Shapes = -> [Cylinder249,Cylinder250]
FEATURE [Part::Mirroring] Part__Mirroring034  label="Fusion211 (Mirror #27)"
  Base = (0,0,0)
  Normal = (0,1,0)
  Placement = pos=(0,170,0) rot=(0,0,1;0rad)
  Source = -> Fusion211
FEATURE [Part::Cut] Cut408  label="left-wing-01"
  Base = -> Part__Mirroring019
  Placement = pos=(0,0,8) rot=(0,0,1;0rad)
  Refine = true
  Tool = -> Fusion209
FEATURE [Part::Cut] Cut409  label="right-wing-01"
  Base = -> Fusion147
  Placement = pos=(0,0,8) rot=(0,0,1;0rad)
  Refine = true
  Tool = -> Part__Mirroring034
FEATURE [Part::Cylinder] Cylinder251
  Angle = 360
  AttacherType = Attacher::AttachEngine3D
  Height = 8.5
  Placement = pos=(13.2,11,53.5) rot=(0,0,1;0rad)
  Radius = 2.5
FEATURE [Part::Cylinder] Cylinder254
  Angle = 360
  AttacherType = Attacher::AttachEngine3D
  Height = 11.5
  Placement = pos=(13.2,11,2) rot=(0,0,1;0rad)
  Radius = 2.5
FEATURE [Part::Box] Box408  label="Cube"
  AttacherType = Attacher::AttachEngine3D
  Height = 3
  Length = 10
  Placement = pos=(8,1,7) rot=(0,0,1;0rad)
  Width = 10
FEATURE [Part::Cylinder] Cylinder255
  Angle = 360
  AttacherType = Attacher::AttachEngine3D
  Height = 3
  Placement = pos=(13.2,11,7) rot=(0,0,1;0rad)
  Radius = 3
FEATURE [Part::Cylinder] Cylinder256
  Angle = 360
  AttacherType = Attacher::AttachEngine3D
  Height = 3
  Placement = pos=(13.2,11,7) rot=(0,0,1;0rad)
  Radius = 3
FEATURE [Part::Box] Box409  label="Cube634"
  AttacherType = Attacher::AttachEngine3D
  Height = 3
  Length = 10
  Placement = pos=(8,1,7) rot=(0,0,1;0rad)
  Width = 10
FEATURE [Part::MultiFuse] Fusion212
  Refine = true
  Shapes = -> [Box408,Cylinder255]
FEATURE [Part::MultiFuse] Fusion213
  Placement = pos=(0,0,49) rot=(0,0,1;0rad)
  Refine = true
  Shapes = -> [Cylinder256,Box409]
FEATURE [Part::MultiFuse] Fusion214
  Refine = true
  Shapes = -> [Fusion213,Fusion212]
FEATURE [Part::Cylinder] Cylinder257
  Angle = 360
  AttacherType = Attacher::AttachEngine3D
  Height = 8.5
  Placement = pos=(13.2,11,53.5) rot=(0,0,1;0rad)
  Radius = 1.1
FEATURE [Part::Cylinder] Cylinder258
  Angle = 360
  AttacherType = Attacher::AttachEngine3D
  Height = 13.5
  Placement = pos=(13.2,11,0) rot=(0,0,1;0rad)
  Radius = 1.1
FEATURE [Part::MultiFuse] Fusion215
  Refine = true
  Shapes = -> [Cylinder257,Cylinder258]
FEATURE [Part::MultiFuse] Fusion216
  Refine = true
  Shapes = -> [Cylinder251,Cylinder254]
FEATURE [Part::MultiFuse] Fusion217
  Refine = true
  Shapes = -> [Cut407,Fusion216]
FEATURE [Part::Cut] Cut410  label="Cut756"
  Base = -> Fusion217
  Refine = true
  Tool = -> Fusion214
FEATURE [Part::Cut] Cut411  label="inner-door-swing-arm-left"
  Base = -> Cut410
  Placement = pos=(0,0,8) rot=(0,0,1;0rad)
  Refine = true
  Tool = -> Fusion215
FEATURE [Part::Cylinder] Cylinder259
  Angle = 360
  AttacherType = Attacher::AttachEngine3D
  Height = 62
  Placement = pos=(25,21,0) rot=(0,0,1;3.28122rad)
  Radius = 29
FEATURE [Part::Cylinder] Cylinder260
  Angle = 360
  AttacherType = Attacher::AttachEngine3D
  Height = 62
  Placement = pos=(25,21,0) rot=(0,0,1;0rad)
  Radius = 18
FEATURE [Part::Cut] Cut412  label="Cut757"
  Base = -> Cylinder259
  Refine = true
  Tool = -> Cylinder260
FEATURE [Part::Box] Box410  label="Cube635"
  AttacherType = Attacher::AttachEngine3D
  Height = 2
  Length = 48
  Placement = pos=(5,3,0) rot=(0,0,1;0rad)
  Width = 15
FEATURE [Part::Cylinder] Cylinder261
  Angle = 360
  AttacherType = Attacher::AttachEngine3D
  Height = 62
  Placement = pos=(25,21,0) rot=(0,0,1;0rad)
  Radius = 16.5
FEATURE [Part::Cylinder] Cylinder262
  Angle = 360
  AttacherType = Attacher::AttachEngine3D
  Height = 62
  Placement = pos=(25,21,0) rot=(0,0,1;3.3074rad)
  Radius = 18
FEATURE [Part::Cut] Cut413  label="Cut758"
  Base = -> Cylinder262
  Refine = true
  Tool = -> Cylinder261
FEATURE [Part::Cut] Cut414  label="Cut759"
  Base = -> Box410
  Refine = true
  Tool = -> Cut412
FEATURE [Part::Box] Box411  label="Cube636"
  AttacherType = Attacher::AttachEngine3D
  Height = 62
  Length = 3
  Placement = pos=(6,18,0) rot=(0,0,1;0rad)
  Width = 1
FEATURE [Part::Cut] Cut415  label="Cut760"
  Base = -> Cut413
  Refine = true
  Tool = -> Box411
FEATURE [Part::Cylinder] Cylinder263
  Angle = 360
  AttacherType = Attacher::AttachEngine3D
  Height = 22
  Placement = pos=(98,18,-23) rot=(1,0,0;1.5708rad)
  Radius = 52
FEATURE [Part::Cut] Cut416  label="Cut761"
  Base = -> Cut414
  Refine = true
  Tool = -> Cylinder263
FEATURE [Part::Cylinder] Cylinder264
  Angle = 360
  AttacherType = Attacher::AttachEngine3D
  Height = 13
  Placement = pos=(11.9886,10.7385,16) rot=(0.884029,-0.330525,-0.330525;1.69375rad)
  Radius = 1.2
FEATURE [Part::Cylinder] Cylinder265
  Angle = 360
  AttacherType = Attacher::AttachEngine3D
  Height = 13
  Placement = pos=(11.9886,10.7385,51) rot=(0.884029,-0.330525,-0.330525;1.69375rad)
  Radius = 1.2
FEATURE [Part::MultiFuse] Fusion218
  Placement = pos=(0.87,1,0) rot=(0,0,1;0rad)
  Refine = true
  Shapes = -> [Cylinder264,Cylinder265]
FEATURE [Part::Cylinder] Cylinder266
  Angle = 360
  AttacherType = Attacher::AttachEngine3D
  Height = 1.6
  Placement = pos=(11.9886,10.7385,16) rot=(0.884029,-0.330525,-0.330525;1.69375rad)
  Radius = 2
FEATURE [Part::Cylinder] Cylinder267
  Angle = 360
  AttacherType = Attacher::AttachEngine3D
  Height = 1.6
  Placement = pos=(11.9886,10.7385,51) rot=(0.884029,-0.330525,-0.330525;1.69375rad)
  Radius = 2
FEATURE [Part::MultiFuse] Fusion219
  Placement = pos=(0.87,1,0) rot=(0,0,1;0rad)
  Refine = true
  Shapes = -> [Cylinder266,Cylinder267]
FEATURE [Part::MultiFuse] Fusion220
  Refine = true
  Shapes = -> [Cut415,Cut416,Fusion219]
FEATURE [Part::Cut] Cut417  label="Cut762"
  Base = -> Fusion220
  Refine = true
  Tool = -> Fusion218
FEATURE [Part::Cylinder] Cylinder268
  Angle = 360
  AttacherType = Attacher::AttachEngine3D
  Height = 10
  Placement = pos=(18,15,-5) rot=(0,0,1;0rad)
  Radius = 1.2
FEATURE [Part::Cylinder] Cylinder269
  Angle = 360
  AttacherType = Attacher::AttachEngine3D
  Height = 10
  Placement = pos=(49,15,-5) rot=(0,0,1;0rad)
  Radius = 1.2
FEATURE [Part::MultiFuse] Fusion221
  Refine = true
  Shapes = -> [Cylinder268,Cylinder269]
FEATURE [Part::Cut] Cut418  label="Cut763"
  Base = -> Cut417
  Refine = true
  Tool = -> Fusion221
FEATURE [Part::Cylinder] Cylinder270
  Angle = 360
  AttacherType = Attacher::AttachEngine3D
  Height = 8.5
  Placement = pos=(13.2,11,53.5) rot=(0,0,1;0rad)
  Radius = 2.5
FEATURE [Part::Cylinder] Cylinder271
  Angle = 360
  AttacherType = Attacher::AttachEngine3D
  Height = 11.5
  Placement = pos=(13.2,11,2) rot=(0,0,1;0rad)
  Radius = 2.5
FEATURE [Part::Box] Box412  label="Cube637"
  AttacherType = Attacher::AttachEngine3D
  Height = 3
  Length = 10
  Placement = pos=(8,1,7) rot=(0,0,1;0rad)
  Width = 10
FEATURE [Part::Cylinder] Cylinder272
  Angle = 360
  AttacherType = Attacher::AttachEngine3D
  Height = 3
  Placement = pos=(13.2,11,7) rot=(0,0,1;0rad)
  Radius = 3
FEATURE [Part::Cylinder] Cylinder273
  Angle = 360
  AttacherType = Attacher::AttachEngine3D
  Height = 3
  Placement = pos=(13.2,11,7) rot=(0,0,1;0rad)
  Radius = 3
FEATURE [Part::Box] Box413  label="Cube638"
  AttacherType = Attacher::AttachEngine3D
  Height = 3
  Length = 10
  Placement = pos=(8,1,7) rot=(0,0,1;0rad)
  Width = 10
FEATURE [Part::MultiFuse] Fusion222
  Refine = true
  Shapes = -> [Box412,Cylinder272]
FEATURE [Part::MultiFuse] Fusion223
  Placement = pos=(0,0,49) rot=(0,0,1;0rad)
  Refine = true
  Shapes = -> [Cylinder273,Box413]
FEATURE [Part::MultiFuse] Fusion224
  Refine = true
  Shapes = -> [Fusion223,Fusion222]
FEATURE [Part::Cylinder] Cylinder274
  Angle = 360
  AttacherType = Attacher::AttachEngine3D
  Height = 8.5
  Placement = pos=(13.2,11,53.5) rot=(0,0,1;0rad)
  Radius = 1.1
FEATURE [Part::Cylinder] Cylinder275
  Angle = 360
  AttacherType = Attacher::AttachEngine3D
  Height = 13.5
  Placement = pos=(13.2,11,0) rot=(0,0,1;0rad)
  Radius = 1.1
FEATURE [Part::MultiFuse] Fusion225
  Refine = true
  Shapes = -> [Cylinder274,Cylinder275]
FEATURE [Part::MultiFuse] Fusion226
  Refine = true
  Shapes = -> [Cylinder270,Cylinder271]
FEATURE [Part::MultiFuse] Fusion227
  Refine = true
  Shapes = -> [Cut418,Fusion226]
FEATURE [Part::Cut] Cut419  label="Cut764"
  Base = -> Fusion227
  Refine = true
  Tool = -> Fusion224
FEATURE [Part::Cut] Cut420  label="inner-door-swing-arm-left001"
  Base = -> Cut419
  Refine = true
  Tool = -> Fusion225
FEATURE [Part::Mirroring] Part__Mirroring035  label="inner-door-swing-arm-right"
  Base = (0,0,0)
  Normal = (0,1,0)
  Placement = pos=(0,170,8) rot=(0,0,1;0rad)
  Source = -> Cut420
FEATURE [Part::Cylinder] Cylinder276
  Angle = 360
  AttacherType = Attacher::AttachEngine3D
  Height = 22
  Placement = pos=(0,0,0) rot=(1,0,0;1.5708rad)
  Radius = 41
FEATURE [Part::Cylinder] Cylinder277
  Angle = 360
  AttacherType = Attacher::AttachEngine3D
  Height = 22
  Placement = pos=(0,0,0) rot=(1,0,0;1.5708rad)
  Radius = 20
FEATURE [Part::Cut] Cut421  label="Cut765"
  Base = -> Cylinder276
  Refine = true
  Tool = -> Cylinder277
FEATURE [Part::Fillet] Fillet260  label="wheel-000"
  Base = -> Cut421
  Edges = 2 edges r=1: [Edge1,Edge3]
  Placement = pos=(0,17,0) rot=(0,0,1;0rad)
FEATURE [Part::Cylinder] Cylinder278
  Angle = 360
  AttacherType = Attacher::AttachEngine3D
  Height = 22
  Placement = pos=(0,0,0) rot=(1,0,0;1.5708rad)
  Radius = 41
FEATURE [Part::Cylinder] Cylinder279
  Angle = 360
  AttacherType = Attacher::AttachEngine3D
  Height = 22
  Placement = pos=(0,0,0) rot=(1,0,0;1.5708rad)
  Radius = 20
FEATURE [Part::Cut] Cut422  label="Cut766"
  Base = -> Cylinder278
  Refine = true
  Tool = -> Cylinder279
FEATURE [Part::Fillet] Fillet261  label="wheel-001"
  Base = -> Cut422
  Edges = 2 edges r=1: [Edge1,Edge3]
  Placement = pos=(0,175,0) rot=(0,0,1;0rad)
FEATURE [Part::Box] Box414  label="floor"
  AttacherType = Attacher::AttachEngine3D
  Height = 1
  Length = 600
  Placement = pos=(-10,-15,-93) rot=(0,0,1;0rad)
  Width = 200
FEATURE [Part::Cylinder] Cylinder288
  Angle = 360
  AttacherType = Attacher::AttachEngine3D
  Height = 22
  Placement = pos=(0,0,0) rot=(1,0,0;1.5708rad)
  Radius = 41
FEATURE [Part::Cylinder] Cylinder289
  Angle = 360
  AttacherType = Attacher::AttachEngine3D
  Height = 22
  Placement = pos=(0,0,0) rot=(1,0,0;1.5708rad)
  Radius = 41
FEATURE [Part::Cylinder] Cylinder290
  Angle = 360
  AttacherType = Attacher::AttachEngine3D
  Height = 22
  Placement = pos=(0,0,0) rot=(1,0,0;1.5708rad)
  Radius = 20
FEATURE [Part::Cut] Cut427  label="Cut767"
  Base = -> Cylinder289
  Refine = true
  Tool = -> Cylinder290
FEATURE [Part::Fillet] Fillet267  label="wheel-007"
  Base = -> Cut427
  Edges = 2 edges r=1: [Edge1,Edge3]
  Placement = pos=(0,174,0) rot=(0,0,1;0rad)
FEATURE [Part::Cylinder] Cylinder291
  Angle = 360
  AttacherType = Attacher::AttachEngine3D
  Height = 22
  Placement = pos=(0,0,0) rot=(1,0,0;1.5708rad)
  Radius = 20
FEATURE [Part::Cut] Cut428  label="Cut768"
  Base = -> Cylinder288
  Refine = true
  Tool = -> Cylinder291
FEATURE [Part::Fillet] Fillet266  label="wheel-006"
  Base = -> Cut428
  Edges = 2 edges r=1: [Edge1,Edge3]
  Placement = pos=(0,18,0) rot=(0,0,1;0rad)
FEATURE [Part::Box] Box416  label="Cube641"
  AttacherType = Attacher::AttachEngine3D
  Height = 20
  Length = 490
  Placement = pos=(0,0,-92) rot=(0,0,1;0rad)
  Width = 11.5
FEATURE [Part::Box] Box417  label="Cube642"
  AttacherType = Attacher::AttachEngine3D
  Height = 17
  Length = 490
  Placement = pos=(0,1.5,-90.5) rot=(0,0,1;0rad)
  Width = 10
FEATURE [Part::Cut] Cut429  label="Cut769"
  Base = -> Box416
  Refine = true
  Tool = -> Box417
FEATURE [Part::Fillet] Fillet268
  Base = -> Cut429
  Edges = 2 edges r=3: [Edge11,Edge23]
  Placement = pos=(0,-1.5,0) rot=(0,0,1;0rad)
FEATURE [Part::Box] Box418  label="Cube643"
  AttacherType = Attacher::AttachEngine3D
  Height = 20
  Length = 490
  Placement = pos=(0,0,-92) rot=(0,0,1;0rad)
  Width = 11.5
FEATURE [Part::Box] Box419  label="Cube644"
  AttacherType = Attacher::AttachEngine3D
  Height = 17
  Length = 490
  Placement = pos=(0,1.5,-90.5) rot=(0,0,1;0rad)
  Width = 10
FEATURE [Part::Cut] Cut430  label="Cut770"
  Base = -> Box418
  Refine = true
  Tool = -> Box419
FEATURE [Part::Fillet] Fillet269
  Base = -> Cut430
  Edges = 2 edges r=3: [Edge11,Edge23]
FEATURE [Part::Mirroring] Part__Mirroring036  label="Fillet269 (Mirror #29)"
  Base = (0,0,0)
  Normal = (0,1,0)
  Placement = pos=(0,61.5,0) rot=(0,0,1;0rad)
  Source = -> Fillet269
FEATURE [Part::MultiFuse] Fusion231  label="frame-00"
  Placement = pos=(23.5,55,74) rot=(0,0,1;0rad)
  Refine = true
  Shapes = -> [Part__Mirroring036,Fillet268]
FEATURE [App::DocumentObjectGroup] Group  label="cab"
  Group = -> [Fillet076,Part__Mirroring006,Fusion047,Fusion094,Fusion099,Fusion138,Part__Mirroring018,Fillet167,Part__Mirroring022,Fusion164,Fusion166,Fillet206,Fillet224,Part__Mirroring024,Fillet231,Cut364,Cut366,Cut367,Fusion183,Cut387,Fusion196,Fusion197,Cut390,Part__Mirroring031,Cut396,Cut397,Cut398,Cut408,Cut409,Cut411,Part__Mirroring035,Cut180,Cut179]
FEATURE [Part::Cylinder] Cylinder310
  Angle = 360
  AttacherType = Attacher::AttachEngine3D
  Height = 22
  Placement = pos=(0,0,0) rot=(1,0,0;1.5708rad)
  Radius = 41
FEATURE [Part::Cylinder] Cylinder311
  Angle = 360
  AttacherType = Attacher::AttachEngine3D
  Height = 22
  Placement = pos=(0,0,0) rot=(1,0,0;1.5708rad)
  Radius = 20
FEATURE [Part::Cut] Cut432  label="Cut771"
  Base = -> Cylinder310
  Refine = true
  Tool = -> Cylinder311
FEATURE [Part::Fillet] Fillet273  label="wheel-008"
  Base = -> Cut432
  Edges = 2 edges r=1: [Edge1,Edge3]
  Placement = pos=(0,17,0) rot=(0,0,1;0rad)
FEATURE [Part::Cylinder] Cylinder312
  Angle = 360
  AttacherType = Attacher::AttachEngine3D
  Height = 22
  Placement = pos=(0,0,0) rot=(1,0,0;1.5708rad)
  Radius = 41
FEATURE [Part::Cylinder] Cylinder313
  Angle = 360
  AttacherType = Attacher::AttachEngine3D
  Height = 22
  Placement = pos=(0,0,0) rot=(1,0,0;1.5708rad)
  Radius = 20
FEATURE [Part::Cut] Cut433  label="Cut772"
  Base = -> Cylinder312
  Refine = true
  Tool = -> Cylinder313
FEATURE [Part::Fillet] Fillet274  label="wheel-009"
  Base = -> Cut433
  Edges = 2 edges r=1: [Edge1,Edge3]
  Placement = pos=(0,177,0) rot=(0,0,1;0rad)
FEATURE [Part::Cylinder] Cylinder314
  Angle = 360
  AttacherType = Attacher::AttachEngine3D
  Height = 22
  Placement = pos=(0,0,0) rot=(1,0,0;1.5708rad)
  Radius = 41
FEATURE [Part::Cylinder] Cylinder315
  Angle = 360
  AttacherType = Attacher::AttachEngine3D
  Height = 22
  Placement = pos=(0,0,0) rot=(1,0,0;1.5708rad)
  Radius = 20
FEATURE [Part::Cut] Cut434  label="Cut773"
  Base = -> Cylinder314
  Refine = true
  Tool = -> Cylinder315
FEATURE [Part::Fillet] Fillet275  label="wheel-010"
  Base = -> Cut434
  Edges = 2 edges r=1: [Edge1,Edge3]
  Placement = pos=(0,41,0) rot=(0,0,1;0rad)
FEATURE [Part::Cylinder] Cylinder316
  Angle = 360
  AttacherType = Attacher::AttachEngine3D
  Height = 22
  Placement = pos=(0,0,0) rot=(1,0,0;1.5708rad)
  Radius = 41
FEATURE [Part::Cylinder] Cylinder317
  Angle = 360
  AttacherType = Attacher::AttachEngine3D
  Height = 22
  Placement = pos=(0,0,0) rot=(1,0,0;1.5708rad)
  Radius = 20
FEATURE [Part::Cut] Cut435  label="Cut774"
  Base = -> Cylinder316
  Refine = true
  Tool = -> Cylinder317
FEATURE [Part::Fillet] Fillet276  label="wheel-011"
  Base = -> Cut435
  Edges = 2 edges r=1: [Edge1,Edge3]
  Placement = pos=(1,153,0) rot=(0,0,1;0rad)
FEATURE [Part::MultiFuse] Fusion243  label="wheels-rear001"
  Placement = pos=(0,0,-130) rot=(1,0,0;1.5708rad)
  Refine = true
  Shapes = -> [Fillet273,Fillet276,Fillet274,Fillet275]
FEATURE [Part::Chamfer] Chamfer055  label="wheels-rear"
  Base = -> Fusion243
  Edges = 8 edges r=5: [Edge8,Edge9,Edge18,Edge19,Edge28,Edge29,Edge38,Edge39]
  Placement = pos=(453,129,-51) rot=(-1,0,0;1.5708rad)
FEATURE [Part::MultiFuse] Fusion244
  Placement = pos=(348,0,-51) rot=(0,0,1;0rad)
  Refine = true
  Shapes = -> [Fillet266,Fillet267]
FEATURE [Part::Chamfer] Chamfer056  label="whees-middle"
  Base = -> Fusion244
  Edges = 4 edges r=5: [Edge8,Edge9,Edge18,Edge19]
FEATURE [Part::MultiFuse] Fusion245
  Placement = pos=(98,0,-51) rot=(0,0,1;0rad)
  Refine = true
  Shapes = -> [Fillet260,Fillet261]
FEATURE [Part::Chamfer] Chamfer057  label="whels-front"
  Base = -> Fusion245
  Edges = 4 edges r=5: [Edge8,Edge9,Edge18,Edge19]
FEATURE [Part::Cylinder] Cylinder318
  Angle = 360
  AttacherType = Attacher::AttachEngine3D
  Height = 20
  Radius = 23.5
FEATURE [Part::Cylinder] Cylinder319
  Angle = 360
  AttacherType = Attacher::AttachEngine3D
  Height = 17
  Radius = 23.5
FEATURE [Part::Cylinder] Cylinder320
  Angle = 360
  AttacherType = Attacher::AttachEngine3D
  Height = 17
  Radius = 22.1
FEATURE [Part::Cut] Cut436  label="Cut775"
  Base = -> Cylinder319
  Placement = pos=(0,0,1.5) rot=(0,0,1;0rad)
  Refine = true
  Tool = -> Cylinder320
FEATURE [Part::Cut] Cut437  label="Cut776"
  Base = -> Cylinder318
  Refine = true
  Tool = -> Cut436
FEATURE [Part::Cylinder] Cylinder321
  Angle = 360
  AttacherType = Attacher::AttachEngine3D
  Height = 17
  Radius = 22
FEATURE [Part::Cylinder] Cylinder322
  Angle = 360
  AttacherType = Attacher::AttachEngine3D
  Height = 10
  Placement = pos=(0,0,0.5) rot=(0,0,1;0rad)
  Radius = 23.5
FEATURE [Part::Cut] Cut438  label="Cut777"
  Base = -> Cylinder322
  Placement = pos=(0,0,4.5) rot=(0,0,1;0rad)
  Refine = true
  Tool = -> Cylinder321
FEATURE [Part::Cylinder] Cylinder323
  Angle = 360
  AttacherType = Attacher::AttachEngine3D
  Height = 20
  Radius = 18.5
FEATURE [Part::MultiFuse] Fusion246
  Refine = true
  Shapes = -> [Cut438,Cut437]
FEATURE [Part::Cut] Cut439  label="Cut778"
  Base = -> Fusion246
  Refine = true
  Tool = -> Cylinder323
FEATURE [Part::Cone] Cone002
  Angle = 360
  AttacherType = Attacher::AttachEngine3D
  Height = 7
  Placement = pos=(0,0,15) rot=(0,0,1;0rad)
  Radius1 = 21
  Radius2 = 15
FEATURE [Part::Cylinder] Cylinder324
  Angle = 360
  AttacherType = Attacher::AttachEngine3D
  Height = 10
  Placement = pos=(0,0,15) rot=(0,0,1;0rad)
  Radius = 20.5
FEATURE [Part::Cut] Cut440  label="Cut779"
  Base = -> Cut439
  Refine = true
  Tool = -> Cylinder324
FEATURE [Part::Fillet] Fillet277
  Base = -> Cut440
  Edges = 1 edges r=1: [Edge20]
FEATURE [Part::Cylinder] Cylinder325
  Angle = 360
  AttacherType = Attacher::AttachEngine3D
  Height = 12
  Radius = 20
FEATURE [Part::Cylinder] Cylinder326
  Angle = 360
  AttacherType = Attacher::AttachEngine3D
  Height = 26
  Radius = 10
FEATURE [Part::Cylinder] Cylinder327
  Angle = 360
  AttacherType = Attacher::AttachEngine3D
  Height = 8
  Placement = pos=(12,0,16) rot=(0,1,0;1.01229rad)
  Radius = 2.5
FEATURE [Part::Mirroring] Part__Mirroring037  label="Cylinder107 (Mirror #1)004"
  Base = (0,0,0)
  Normal = (1,0,0)
  Source = -> Cylinder327
FEATURE [Part::Cylinder] Cylinder328
  Angle = 360
  AttacherType = Attacher::AttachEngine3D
  Height = 8
  Placement = pos=(12,0,16) rot=(0,1,0;1.01229rad)
  Radius = 2.5
FEATURE [Part::MultiFuse] Fusion247
  Refine = true
  Shapes = -> [Cylinder328,Part__Mirroring037]
FEATURE [Part::Cylinder] Cylinder329
  Angle = 360
  AttacherType = Attacher::AttachEngine3D
  Height = 8
  Placement = pos=(12,0,16) rot=(0,1,0;1.01229rad)
  Radius = 2.5
FEATURE [Part::Cylinder] Cylinder330
  Angle = 360
  AttacherType = Attacher::AttachEngine3D
  Height = 8
  Placement = pos=(12,0,16) rot=(0,1,0;1.01229rad)
  Radius = 2.5
FEATURE [Part::Mirroring] Part__Mirroring038  label="Cylinder107 (Mirror #1)005"
  Base = (0,0,0)
  Normal = (1,0,0)
  Source = -> Cylinder330
FEATURE [Part::MultiFuse] Fusion248
  Placement = pos=(0,0,0) rot=(0,0,1;0.628319rad)
  Refine = true
  Shapes = -> [Cylinder329,Part__Mirroring038]
FEATURE [Part::Cylinder] Cylinder331
  Angle = 360
  AttacherType = Attacher::AttachEngine3D
  Height = 8
  Placement = pos=(12,0,16) rot=(0,1,0;1.01229rad)
  Radius = 2.5
FEATURE [Part::Cylinder] Cylinder332
  Angle = 360
  AttacherType = Attacher::AttachEngine3D
  Height = 8
  Placement = pos=(12,0,16) rot=(0,1,0;1.01229rad)
  Radius = 2.5
FEATURE [Part::Mirroring] Part__Mirroring039  label="Cylinder107 (Mirror #1)006"
  Base = (0,0,0)
  Normal = (1,0,0)
  Source = -> Cylinder332
FEATURE [Part::MultiFuse] Fusion249
  Placement = pos=(0,0,0) rot=(0,0,1;1.25664rad)
  Refine = true
  Shapes = -> [Cylinder331,Part__Mirroring039]
FEATURE [Part::Cylinder] Cylinder333
  Angle = 360
  AttacherType = Attacher::AttachEngine3D
  Height = 8
  Placement = pos=(12,0,16) rot=(0,1,0;1.01229rad)
  Radius = 2.5
FEATURE [Part::Cylinder] Cylinder334
  Angle = 360
  AttacherType = Attacher::AttachEngine3D
  Height = 8
  Placement = pos=(12,0,16) rot=(0,1,0;1.01229rad)
  Radius = 2.5
FEATURE [Part::Mirroring] Part__Mirroring040  label="Cylinder107 (Mirror #1)007"
  Base = (0,0,0)
  Normal = (1,0,0)
  Source = -> Cylinder334
FEATURE [Part::MultiFuse] Fusion250
  Placement = pos=(0,0,0) rot=(0,0,1;1.88496rad)
  Refine = true
  Shapes = -> [Cylinder333,Part__Mirroring040]
FEATURE [Part::Cylinder] Cylinder335
  Angle = 360
  AttacherType = Attacher::AttachEngine3D
  Height = 8
  Placement = pos=(12,0,16) rot=(0,1,0;1.01229rad)
  Radius = 2.5
FEATURE [Part::Cylinder] Cylinder336
  Angle = 360
  AttacherType = Attacher::AttachEngine3D
  Height = 8
  Placement = pos=(12,0,16) rot=(0,1,0;1.01229rad)
  Radius = 2.5
FEATURE [Part::Mirroring] Part__Mirroring041  label="Cylinder107 (Mirror #1)008"
  Base = (0,0,0)
  Normal = (1,0,0)
  Source = -> Cylinder336
FEATURE [Part::MultiFuse] Fusion251
  Placement = pos=(0,0,0) rot=(0,0,1;2.51327rad)
  Refine = true
  Shapes = -> [Cylinder335,Part__Mirroring041]
FEATURE [Part::MultiFuse] Fusion252
  Placement = pos=(0,0,-1) rot=(0,0,1;0rad)
  Refine = true
  Shapes = -> [Fusion247,Fusion248,Fusion249,Fusion250,Fusion251]
FEATURE [Part::Cylinder] Cylinder337
  Angle = 360
  AttacherType = Attacher::AttachEngine3D
  Height = 10
  Placement = pos=(12.5,0,13) rot=(0,0,1;0rad)
  Radius = 1.1
FEATURE [Part::Cylinder] Cylinder338
  Angle = 360
  AttacherType = Attacher::AttachEngine3D
  Height = 10
  Placement = pos=(-12.5,0,13) rot=(0,0,1;0rad)
  Radius = 1.1
FEATURE [Part::MultiFuse] Fusion253
  Placement = pos=(0,0,0) rot=(0,0,1;0.314159rad)
  Refine = true
  Shapes = -> [Cylinder337,Cylinder338]
FEATURE [Part::Cylinder] Cylinder339
  Angle = 360
  AttacherType = Attacher::AttachEngine3D
  Height = 10
  Placement = pos=(12.5,0,13) rot=(0,0,1;0rad)
  Radius = 1.1
FEATURE [Part::Cylinder] Cylinder340
  Angle = 360
  AttacherType = Attacher::AttachEngine3D
  Height = 10
  Placement = pos=(-12.5,0,13) rot=(0,0,1;0rad)
  Radius = 1.1
FEATURE [Part::MultiFuse] Fusion254
  Placement = pos=(0,0,0) rot=(0,0,1;0.942478rad)
  Refine = true
  Shapes = -> [Cylinder339,Cylinder340]
FEATURE [Part::Cylinder] Cylinder341
  Angle = 360
  AttacherType = Attacher::AttachEngine3D
  Height = 10
  Placement = pos=(12.5,0,13) rot=(0,0,1;0rad)
  Radius = 1.1
FEATURE [Part::Cylinder] Cylinder342
  Angle = 360
  AttacherType = Attacher::AttachEngine3D
  Height = 10
  Placement = pos=(-12.5,0,13) rot=(0,0,1;0rad)
  Radius = 1.1
FEATURE [Part::MultiFuse] Fusion255
  Placement = pos=(0,0,0) rot=(0,0,1;1.5708rad)
  Refine = true
  Shapes = -> [Cylinder341,Cylinder342]
FEATURE [Part::Cylinder] Cylinder343
  Angle = 360
  AttacherType = Attacher::AttachEngine3D
  Height = 10
  Placement = pos=(12.5,0,13) rot=(0,0,1;0rad)
  Radius = 1.1
FEATURE [Part::Cylinder] Cylinder344
  Angle = 360
  AttacherType = Attacher::AttachEngine3D
  Height = 10
  Placement = pos=(-12.5,0,13) rot=(0,0,1;0rad)
  Radius = 1.1
FEATURE [Part::MultiFuse] Fusion256
  Placement = pos=(0,0,0) rot=(0,0,1;2.19911rad)
  Refine = true
  Shapes = -> [Cylinder343,Cylinder344]
FEATURE [Part::Cylinder] Cylinder345
  Angle = 360
  AttacherType = Attacher::AttachEngine3D
  Height = 10
  Placement = pos=(12.5,0,13) rot=(0,0,1;0rad)
  Radius = 1.1
FEATURE [Part::Cylinder] Cylinder346
  Angle = 360
  AttacherType = Attacher::AttachEngine3D
  Height = 10
  Placement = pos=(-12.5,0,13) rot=(0,0,1;0rad)
  Radius = 1.1
FEATURE [Part::MultiFuse] Fusion257
  Placement = pos=(0,0,0) rot=(0,0,1;2.82743rad)
  Refine = true
  Shapes = -> [Cylinder345,Cylinder346]
FEATURE [Part::MultiFuse] Fusion258
  Refine = true
  Shapes = -> [Fusion253,Fusion254,Fusion257,Fusion256,Fusion255]
FEATURE [Part::Cone] Cone003
  Angle = 360
  AttacherType = Attacher::AttachEngine3D
  Height = 10
  Placement = pos=(0,0,9) rot=(0,0,1;0rad)
  Radius1 = 24
  Radius2 = 15
FEATURE [Part::Cut] Cut441  label="Cut780"
  Base = -> Cone002
  Refine = true
  Tool = -> Cylinder326
FEATURE [Part::Cut] Cut442  label="Cut781"
  Base = -> Cut441
  Refine = true
  Tool = -> Cone003
FEATURE [Part::MultiFuse] Fusion259
  Refine = true
  Shapes = -> [Fillet277,Cut442]
FEATURE [Part::Cut] Cut443  label="Cut782"
  Base = -> Fusion259
  Refine = true
  Tool = -> Cylinder325
FEATURE [Part::Chamfer] Chamfer058
  Base = -> Cut443
  Edges = 1 edges r=1.49: [Edge39]
FEATURE [Part::Chamfer] Chamfer059
  Base = -> Chamfer058
  Edges = 1 edges r=2: [Edge10]
FEATURE [Part::Cut] Cut444  label="Cut783"
  Base = -> Chamfer059
  Refine = true
  Tool = -> Fusion252
FEATURE [Part::Cut] Cut445  label="Cut784"
  Base = -> Cut444
  Refine = true
  Tool = -> Fusion258
FEATURE [Part::Fillet] Fillet278
  Base = -> Cut445
  Edges = 1 edges r=1.5: [Edge121]
FEATURE [Part::Fillet] Fillet279  label="rim"
  Base = -> Fillet278
  Edges = 1 edges r=1.5: [Edge161]
FEATURE [Part::Cylinder] Cylinder347
  Angle = 360
  AttacherType = Attacher::AttachEngine3D
  Height = 10
  Placement = pos=(0,0,0.5) rot=(0,0,1;0rad)
  Radius = 23.5
FEATURE [Part::Cylinder] Cylinder348
  Angle = 360
  AttacherType = Attacher::AttachEngine3D
  Height = 17
  Radius = 22
FEATURE [Part::Cut] Cut451  label="Cut790"
  Base = -> Cylinder347
  Placement = pos=(0,0,4.5) rot=(0,0,1;0rad)
  Refine = true
  Tool = -> Cylinder348
FEATURE [Part::Cylinder] Cylinder349
  Angle = 360
  AttacherType = Attacher::AttachEngine3D
  Height = 20
  Radius = 23.5
FEATURE [Part::Cylinder] Cylinder350
  Angle = 360
  AttacherType = Attacher::AttachEngine3D
  Height = 17
  Radius = 23.5
FEATURE [Part::Cylinder] Cylinder351
  Angle = 360
  AttacherType = Attacher::AttachEngine3D
  Height = 17
  Radius = 22.1
FEATURE [Part::Cut] Cut453  label="Cut792"
  Base = -> Cylinder350
  Placement = pos=(0,0,1.5) rot=(0,0,1;0rad)
  Refine = true
  Tool = -> Cylinder351
FEATURE [Part::Cut] Cut452  label="Cut791"
  Base = -> Cylinder349
  Refine = true
  Tool = -> Cut453
FEATURE [Part::MultiFuse] Fusion261
  Refine = true
  Shapes = -> [Cut451,Cut452]
FEATURE [Part::Cylinder] Cylinder352
  Angle = 360
  AttacherType = Attacher::AttachEngine3D
  Height = 20
  Radius = 18.5
FEATURE [Part::Cut] Cut450  label="Cut789"
  Base = -> Fusion261
  Refine = true
  Tool = -> Cylinder352
FEATURE [Part::Cylinder] Cylinder353
  Angle = 360
  AttacherType = Attacher::AttachEngine3D
  Height = 10
  Placement = pos=(0,0,15) rot=(0,0,1;0rad)
  Radius = 20.5
FEATURE [Part::Cut] Cut449  label="Cut788"
  Base = -> Cut450
  Refine = true
  Tool = -> Cylinder353
FEATURE [Part::Fillet] Fillet282
  Base = -> Cut449
  Edges = 1 edges r=1: [Edge20]
FEATURE [Part::Cone] Cone004
  Angle = 360
  AttacherType = Attacher::AttachEngine3D
  Height = 7
  Placement = pos=(0,0,15) rot=(0,0,1;0rad)
  Radius1 = 21
  Radius2 = 15
FEATURE [Part::Cylinder] Cylinder354
  Angle = 360
  AttacherType = Attacher::AttachEngine3D
  Height = 26
  Radius = 10
FEATURE [Part::Cut] Cut455  label="Cut794"
  Base = -> Cone004
  Refine = true
  Tool = -> Cylinder354
FEATURE [Part::Cone] Cone005
  Angle = 360
  AttacherType = Attacher::AttachEngine3D
  Height = 10
  Placement = pos=(0,0,9) rot=(0,0,1;0rad)
  Radius1 = 24
  Radius2 = 15
FEATURE [Part::Cut] Cut454  label="Cut793"
  Base = -> Cut455
  Refine = true
  Tool = -> Cone005
FEATURE [Part::MultiFuse] Fusion260
  Refine = true
  Shapes = -> [Fillet282,Cut454]
FEATURE [Part::Cylinder] Cylinder355
  Angle = 360
  AttacherType = Attacher::AttachEngine3D
  Height = 12
  Radius = 20
FEATURE [Part::Cut] Cut448  label="Cut787"
  Base = -> Fusion260
  Refine = true
  Tool = -> Cylinder355
FEATURE [Part::Chamfer] Chamfer061
  Base = -> Cut448
  Edges = 1 edges r=1.49: [Edge39]
FEATURE [Part::Chamfer] Chamfer060
  Base = -> Chamfer061
  Edges = 1 edges r=2: [Edge10]
FEATURE [Part::Cylinder] Cylinder356
  Angle = 360
  AttacherType = Attacher::AttachEngine3D
  Height = 8
  Placement = pos=(12,0,16) rot=(0,1,0;1.01229rad)
  Radius = 2.5
FEATURE [Part::Cylinder] Cylinder357
  Angle = 360
  AttacherType = Attacher::AttachEngine3D
  Height = 8
  Placement = pos=(12,0,16) rot=(0,1,0;1.01229rad)
  Radius = 2.5
FEATURE [Part::Mirroring] Part__Mirroring042  label="Cylinder107 (Mirror #1)009"
  Base = (0,0,0)
  Normal = (1,0,0)
  Source = -> Cylinder357
FEATURE [Part::MultiFuse] Fusion263
  Refine = true
  Shapes = -> [Cylinder356,Part__Mirroring042]
FEATURE [Part::Cylinder] Cylinder358
  Angle = 360
  AttacherType = Attacher::AttachEngine3D
  Height = 8
  Placement = pos=(12,0,16) rot=(0,1,0;1.01229rad)
  Radius = 2.5
FEATURE [Part::Cylinder] Cylinder359
  Angle = 360
  AttacherType = Attacher::AttachEngine3D
  Height = 8
  Placement = pos=(12,0,16) rot=(0,1,0;1.01229rad)
  Radius = 2.5
FEATURE [Part::Mirroring] Part__Mirroring043  label="Cylinder107 (Mirror #1)010"
  Base = (0,0,0)
  Normal = (1,0,0)
  Source = -> Cylinder359
FEATURE [Part::MultiFuse] Fusion264
  Placement = pos=(0,0,0) rot=(0,0,1;0.628319rad)
  Refine = true
  Shapes = -> [Cylinder358,Part__Mirroring043]
FEATURE [Part::Cylinder] Cylinder360
  Angle = 360
  AttacherType = Attacher::AttachEngine3D
  Height = 8
  Placement = pos=(12,0,16) rot=(0,1,0;1.01229rad)
  Radius = 2.5
FEATURE [Part::Cylinder] Cylinder361
  Angle = 360
  AttacherType = Attacher::AttachEngine3D
  Height = 8
  Placement = pos=(12,0,16) rot=(0,1,0;1.01229rad)
  Radius = 2.5
FEATURE [Part::Mirroring] Part__Mirroring044  label="Cylinder107 (Mirror #1)011"
  Base = (0,0,0)
  Normal = (1,0,0)
  Source = -> Cylinder361
FEATURE [Part::MultiFuse] Fusion265
  Placement = pos=(0,0,0) rot=(0,0,1;1.25664rad)
  Refine = true
  Shapes = -> [Cylinder360,Part__Mirroring044]
FEATURE [Part::Cylinder] Cylinder362
  Angle = 360
  AttacherType = Attacher::AttachEngine3D
  Height = 8
  Placement = pos=(12,0,16) rot=(0,1,0;1.01229rad)
  Radius = 2.5
FEATURE [Part::Cylinder] Cylinder363
  Angle = 360
  AttacherType = Attacher::AttachEngine3D
  Height = 8
  Placement = pos=(12,0,16) rot=(0,1,0;1.01229rad)
  Radius = 2.5
FEATURE [Part::Mirroring] Part__Mirroring045  label="Cylinder107 (Mirror #1)012"
  Base = (0,0,0)
  Normal = (1,0,0)
  Source = -> Cylinder363
FEATURE [Part::MultiFuse] Fusion266
  Placement = pos=(0,0,0) rot=(0,0,1;1.88496rad)
  Refine = true
  Shapes = -> [Cylinder362,Part__Mirroring045]
FEATURE [Part::Cylinder] Cylinder364
  Angle = 360
  AttacherType = Attacher::AttachEngine3D
  Height = 8
  Placement = pos=(12,0,16) rot=(0,1,0;1.01229rad)
  Radius = 2.5
FEATURE [Part::Cylinder] Cylinder365
  Angle = 360
  AttacherType = Attacher::AttachEngine3D
  Height = 8
  Placement = pos=(12,0,16) rot=(0,1,0;1.01229rad)
  Radius = 2.5
FEATURE [Part::Mirroring] Part__Mirroring046  label="Cylinder107 (Mirror #1)013"
  Base = (0,0,0)
  Normal = (1,0,0)
  Source = -> Cylinder365
FEATURE [Part::MultiFuse] Fusion267
  Placement = pos=(0,0,0) rot=(0,0,1;2.51327rad)
  Refine = true
  Shapes = -> [Cylinder364,Part__Mirroring046]
FEATURE [Part::MultiFuse] Fusion262
  Placement = pos=(0,0,-1) rot=(0,0,1;0rad)
  Refine = true
  Shapes = -> [Fusion263,Fusion264,Fusion265,Fusion266,Fusion267]
FEATURE [Part::Cut] Cut447  label="Cut786"
  Base = -> Chamfer060
  Refine = true
  Tool = -> Fusion262
FEATURE [Part::Cylinder] Cylinder366
  Angle = 360
  AttacherType = Attacher::AttachEngine3D
  Height = 10
  Placement = pos=(12.5,0,13) rot=(0,0,1;0rad)
  Radius = 1.1
FEATURE [Part::Cylinder] Cylinder367
  Angle = 360
  AttacherType = Attacher::AttachEngine3D
  Height = 10
  Placement = pos=(-12.5,0,13) rot=(0,0,1;0rad)
  Radius = 1.1
FEATURE [Part::MultiFuse] Fusion269
  Placement = pos=(0,0,0) rot=(0,0,1;0.314159rad)
  Refine = true
  Shapes = -> [Cylinder366,Cylinder367]
FEATURE [Part::Cylinder] Cylinder368
  Angle = 360
  AttacherType = Attacher::AttachEngine3D
  Height = 10
  Placement = pos=(12.5,0,13) rot=(0,0,1;0rad)
  Radius = 1.1
FEATURE [Part::Cylinder] Cylinder369
  Angle = 360
  AttacherType = Attacher::AttachEngine3D
  Height = 10
  Placement = pos=(-12.5,0,13) rot=(0,0,1;0rad)
  Radius = 1.1
FEATURE [Part::MultiFuse] Fusion270
  Placement = pos=(0,0,0) rot=(0,0,1;0.942478rad)
  Refine = true
  Shapes = -> [Cylinder368,Cylinder369]
FEATURE [Part::Cylinder] Cylinder370
  Angle = 360
  AttacherType = Attacher::AttachEngine3D
  Height = 10
  Placement = pos=(12.5,0,13) rot=(0,0,1;0rad)
  Radius = 1.1
FEATURE [Part::Cylinder] Cylinder371
  Angle = 360
  AttacherType = Attacher::AttachEngine3D
  Height = 10
  Placement = pos=(-12.5,0,13) rot=(0,0,1;0rad)
  Radius = 1.1
FEATURE [Part::MultiFuse] Fusion271
  Placement = pos=(0,0,0) rot=(0,0,1;2.82743rad)
  Refine = true
  Shapes = -> [Cylinder370,Cylinder371]
FEATURE [Part::Cylinder] Cylinder372
  Angle = 360
  AttacherType = Attacher::AttachEngine3D
  Height = 10
  Placement = pos=(12.5,0,13) rot=(0,0,1;0rad)
  Radius = 1.1
FEATURE [Part::Cylinder] Cylinder373
  Angle = 360
  AttacherType = Attacher::AttachEngine3D
  Height = 10
  Placement = pos=(-12.5,0,13) rot=(0,0,1;0rad)
  Radius = 1.1
FEATURE [Part::MultiFuse] Fusion272
  Placement = pos=(0,0,0) rot=(0,0,1;2.19911rad)
  Refine = true
  Shapes = -> [Cylinder372,Cylinder373]
FEATURE [Part::Cylinder] Cylinder374
  Angle = 360
  AttacherType = Attacher::AttachEngine3D
  Height = 10
  Placement = pos=(12.5,0,13) rot=(0,0,1;0rad)
  Radius = 1.1
FEATURE [Part::Cylinder] Cylinder375
  Angle = 360
  AttacherType = Attacher::AttachEngine3D
  Height = 10
  Placement = pos=(-12.5,0,13) rot=(0,0,1;0rad)
  Radius = 1.1
FEATURE [Part::MultiFuse] Fusion273
  Placement = pos=(0,0,0) rot=(0,0,1;1.5708rad)
  Refine = true
  Shapes = -> [Cylinder374,Cylinder375]
FEATURE [Part::MultiFuse] Fusion268
  Refine = true
  Shapes = -> [Fusion269,Fusion270,Fusion271,Fusion272,Fusion273]
FEATURE [Part::Cut] Cut446  label="Cut785"
  Base = -> Cut447
  Refine = true
  Tool = -> Fusion268
FEATURE [Part::Fillet] Fillet281
  Base = -> Cut446
  Edges = 1 edges r=1.5: [Edge121]
FEATURE [Part::Fillet] Fillet280
  Base = -> Fillet281
  Edges = 1 edges r=1.5: [Edge161]
FEATURE [Part::Mirroring] Part__Mirroring047  label="Fillet065 (Mirror #11)"
  Base = (0,0,0)
  Normal = (0,0,1)
  Placement = pos=(0,0,44) rot=(0,0,1;0rad)
  Source = -> Fillet280
FEATURE [Part::Cylinder] Cylinder376
  Angle = 360
  AttacherType = Attacher::AttachEngine3D
  Height = 4
  Placement = pos=(0,0,15) rot=(0,0,1;0rad)
  Radius = 15
FEATURE [Part::Feature] Face025
  shape: bbox 17.79 x 17.28 x 2e-07 mm, 1 faces, 0 solids (baked)
FEATURE [Part::Extrusion] Extrude006
  Base = -> Face025
  Dir = (0,0,6)
  DirMode = 0
  FaceMakerClass = Part::FaceMakerExtrusion
  LengthFwd = 0
  LengthRev = 0
  Placement = pos=(0,0,15) rot=(0,0,1;0rad)
  Solid = false
  Symmetric = false
FEATURE [Part::Cylinder] Cylinder377
  Angle = 360
  AttacherType = Attacher::AttachEngine3D
  Height = 10
  Placement = pos=(0,0,19) rot=(0,0,1;0rad)
  Radius = 10
FEATURE [Part::Cylinder] Cylinder378
  Angle = 360
  AttacherType = Attacher::AttachEngine3D
  Height = 5
  Placement = pos=(0,0,24) rot=(0,0,1;0rad)
  Radius = 8
FEATURE [Part::Cut] Cut456  label="Cut795"
  Base = -> Cylinder377
  Refine = true
  Tool = -> Cylinder378
FEATURE [Part::MultiFuse] Fusion274
  Refine = true
  Shapes = -> [Cylinder376,Cut456]
FEATURE [Part::Cylinder] Cylinder379
  Angle = 360
  AttacherType = Attacher::AttachEngine3D
  Height = 10
  Placement = pos=(0,0,21) rot=(0,0,1;0rad)
  Radius = 2
FEATURE [Part::Cylinder] Cylinder380
  Angle = 360
  AttacherType = Attacher::AttachEngine3D
  Height = 10
  Placement = pos=(12.5,0,13) rot=(0,0,1;0rad)
  Radius = 0.8
FEATURE [Part::Cylinder] Cylinder381
  Angle = 360
  AttacherType = Attacher::AttachEngine3D
  Height = 10
  Placement = pos=(-12.5,0,13) rot=(0,0,1;0rad)
  Radius = 0.8
FEATURE [Part::MultiFuse] Fusion277
  Placement = pos=(0,0,0) rot=(0,0,1;0.314159rad)
  Refine = true
  Shapes = -> [Cylinder380,Cylinder381]
FEATURE [Part::Cylinder] Cylinder382
  Angle = 360
  AttacherType = Attacher::AttachEngine3D
  Height = 10
  Placement = pos=(12.5,0,13) rot=(0,0,1;0rad)
  Radius = 0.8
FEATURE [Part::Cylinder] Cylinder383
  Angle = 360
  AttacherType = Attacher::AttachEngine3D
  Height = 10
  Placement = pos=(-12.5,0,13) rot=(0,0,1;0rad)
  Radius = 0.8
FEATURE [Part::MultiFuse] Fusion276
  Placement = pos=(0,0,0) rot=(0,0,1;0.942478rad)
  Refine = true
  Shapes = -> [Cylinder382,Cylinder383]
FEATURE [Part::Cylinder] Cylinder384
  Angle = 360
  AttacherType = Attacher::AttachEngine3D
  Height = 10
  Placement = pos=(12.5,0,13) rot=(0,0,1;0rad)
  Radius = 0.8
FEATURE [Part::Cylinder] Cylinder385
  Angle = 360
  AttacherType = Attacher::AttachEngine3D
  Height = 10
  Placement = pos=(-12.5,0,13) rot=(0,0,1;0rad)
  Radius = 0.8
FEATURE [Part::MultiFuse] Fusion278
  Placement = pos=(0,0,0) rot=(0,0,1;1.5708rad)
  Refine = true
  Shapes = -> [Cylinder384,Cylinder385]
FEATURE [Part::Cylinder] Cylinder386
  Angle = 360
  AttacherType = Attacher::AttachEngine3D
  Height = 10
  Placement = pos=(12.5,0,13) rot=(0,0,1;0rad)
  Radius = 0.8
FEATURE [Part::Cylinder] Cylinder387
  Angle = 360
  AttacherType = Attacher::AttachEngine3D
  Height = 10
  Placement = pos=(-12.5,0,13) rot=(0,0,1;0rad)
  Radius = 0.8
FEATURE [Part::MultiFuse] Fusion279
  Placement = pos=(0,0,0) rot=(0,0,1;2.19911rad)
  Refine = true
  Shapes = -> [Cylinder386,Cylinder387]
FEATURE [Part::Cylinder] Cylinder388
  Angle = 360
  AttacherType = Attacher::AttachEngine3D
  Height = 10
  Placement = pos=(12.5,0,13) rot=(0,0,1;0rad)
  Radius = 0.8
FEATURE [Part::Cylinder] Cylinder389
  Angle = 360
  AttacherType = Attacher::AttachEngine3D
  Height = 10
  Placement = pos=(-12.5,0,13) rot=(0,0,1;0rad)
  Radius = 0.8
FEATURE [Part::MultiFuse] Fusion280
  Placement = pos=(0,0,0) rot=(0,0,1;2.82743rad)
  Refine = true
  Shapes = -> [Cylinder388,Cylinder389]
FEATURE [Part::MultiFuse] Fusion275
  Placement = pos=(0,0,-2) rot=(0,0,1;0rad)
  Refine = true
  Shapes = -> [Fusion277,Fusion276,Fusion280,Fusion279,Fusion278]
FEATURE [Part::Cylinder] Cylinder390
  Angle = 360
  AttacherType = Attacher::AttachEngine3D
  Height = 3
  Placement = pos=(0,0,12) rot=(0,0,1;0rad)
  Radius = 10
FEATURE [Part::Cylinder] Cylinder391
  Angle = 360
  AttacherType = Attacher::AttachEngine3D
  Height = 3
  Placement = pos=(0,0,12) rot=(0,0,1;0rad)
  Radius = 15
FEATURE [Part::Cylinder] Cylinder392
  Angle = 360
  AttacherType = Attacher::AttachEngine3D
  Height = 3
  Placement = pos=(0,0,12) rot=(0,0,1;0.139626rad)
  Radius = 18.4
FEATURE [Part::Cylinder] Cylinder393
  Angle = 360
  AttacherType = Attacher::AttachEngine3D
  Height = 3
  Placement = pos=(0,0,12) rot=(0,0,1;1.39626rad)
  Radius = 18.4
FEATURE [Part::Cylinder] Cylinder394
  Angle = 360
  AttacherType = Attacher::AttachEngine3D
  Height = 3
  Placement = pos=(0,0,12) rot=(0,0,1;2.6529rad)
  Radius = 18.4
FEATURE [Part::Cylinder] Cylinder395
  Angle = 360
  AttacherType = Attacher::AttachEngine3D
  Height = 3
  Placement = pos=(0,0,12) rot=(0,0,1;3.90954rad)
  Radius = 18.4
FEATURE [Part::Cylinder] Cylinder396
  Angle = 360
  AttacherType = Attacher::AttachEngine3D
  Height = 3
  Placement = pos=(0,0,12) rot=(0,0,-1;1.11701rad)
  Radius = 18.4
FEATURE [Part::MultiFuse] Fusion281
  Refine = true
  Shapes = -> [Cylinder392,Cylinder393,Cylinder394,Cylinder395,Cylinder396]
FEATURE [Part::Cut] Cut457  label="Cut796"
  Base = -> Fusion274
  Refine = true
  Tool = -> Cylinder379
FEATURE [Part::MultiFuse] Fusion282
  Refine = true
  Shapes = -> [Extrude006,Cylinder390]
FEATURE [Part::MultiFuse] Fusion283
  Refine = true
  Shapes = -> [Cut457,Cylinder391]
FEATURE [Part::MultiFuse] Fusion284
  Refine = true
  Shapes = -> [Fusion281,Fusion283]
FEATURE [Part::Cut] Cut458  label="Cut797"
  Base = -> Fusion284
  Refine = true
  Tool = -> Fusion282
FEATURE [Part::Cut] Cut459  label="hub-rear-00"
  Base = -> Cut458
  Refine = true
  Tool = -> Fusion275
FEATURE [Part::Cylinder] Cylinder397
  Angle = 360
  AttacherType = Attacher::AttachEngine3D
  Height = 8
  Placement = pos=(0,0,29) rot=(0,0,1;0rad)
  Radius = 10
FEATURE [Part::Cylinder] Cylinder398
  Angle = 360
  AttacherType = Attacher::AttachEngine3D
  Height = 5
  Placement = pos=(0,0,25) rot=(0,0,1;0rad)
  Radius = 8
FEATURE [Part::Cylinder] Cylinder399
  Angle = 360
  AttacherType = Attacher::AttachEngine3D
  Height = 6
  Placement = pos=(0,0,25) rot=(0,0,1;0rad)
  Radius = 6
FEATURE [Part::MultiFuse] Fusion285
  Refine = true
  Shapes = -> [Cylinder397,Cylinder398]
FEATURE [Part::Cut] Cut460  label="Cut798"
  Base = -> Fusion285
  Refine = true
  Tool = -> Cylinder399
FEATURE [Part::Cylinder] Cylinder400
  Angle = 360
  AttacherType = Attacher::AttachEngine3D
  Height = 2
  Placement = pos=(0,0,-6) rot=(0,0,1;0rad)
  Radius = 7.5
FEATURE [Part::Fillet] Fillet283
  Base = -> Cylinder400
  Edges = 1 edges r=1: [Edge1]
  Placement = pos=(0,0,-6) rot=(0,0,1;0rad)
FEATURE [Part::Cylinder] Cylinder401
  Angle = 360
  AttacherType = Attacher::AttachEngine3D
  Height = 0.3
  Placement = pos=(0,0,-10.3) rot=(0,0,1;0rad)
  Radius = 1.5
FEATURE [Part::Cut] Cut461  label="Cut799"
  Base = -> Fillet283
  Refine = true
  Tool = -> Cylinder401
FEATURE [Part::Fillet] Fillet284
  Base = -> Cut461
  Edges = 1 edges r=0.29: [Edge6]
  Placement = pos=(0,0,48) rot=(0,0,1;0rad)
FEATURE [Part::Feature] Face026
  shape: bbox 1.791 x 1.578 x 2e-07 mm, 1 faces, 0 solids (baked)
FEATURE [Part::Feature] Face027
  shape: bbox 1.791 x 1.578 x 2e-07 mm, 1 faces, 0 solids (baked)
FEATURE [Part::Extrusion] Extrude007
  Base = -> Face027
  Dir = (0,0,0.3)
  DirMode = 0
  FaceMakerClass = Part::FaceMakerExtrusion
  LengthFwd = 0
  LengthRev = 0
  Placement = pos=(0.75,0,47.5) rot=(0,0,1;0rad)
  Solid = false
  Symmetric = false
FEATURE [Part::Extrusion] Extrude008
  Base = -> Face026
  Dir = (0,0,0.3)
  DirMode = 0
  FaceMakerClass = Part::FaceMakerExtrusion
  LengthFwd = 0
  LengthRev = 0
  Placement = pos=(-0.75,0,47.5) rot=(0,0,1;3.14159rad)
  Solid = false
  Symmetric = false
FEATURE [Part::MultiFuse] Fusion286
  Refine = true
  Shapes = -> [Extrude008,Extrude007]
FEATURE [Part::Feature] Face028
  shape: bbox 1.791 x 1.578 x 2e-07 mm, 1 faces, 0 solids (baked)
FEATURE [Part::Extrusion] Extrude009
  Base = -> Face028
  Dir = (0,0,0.3)
  DirMode = 0
  FaceMakerClass = Part::FaceMakerExtrusion
  LengthFwd = 0
  LengthRev = 0
  Placement = pos=(-0.75,0,47.5) rot=(0,0,1;3.14159rad)
  Solid = false
  Symmetric = false
FEATURE [Part::Feature] Face029
  shape: bbox 1.791 x 1.578 x 2e-07 mm, 1 faces, 0 solids (baked)
FEATURE [Part::Extrusion] Extrude010
  Base = -> Face029
  Dir = (0,0,0.3)
  DirMode = 0
  FaceMakerClass = Part::FaceMakerExtrusion
  LengthFwd = 0
  LengthRev = 0
  Placement = pos=(0.75,0,47.5) rot=(0,0,1;0rad)
  Solid = false
  Symmetric = false
FEATURE [Part::MultiFuse] Fusion287
  Placement = pos=(0,0,0) rot=(0,0,1;2.0944rad)
  Refine = true
  Shapes = -> [Extrude009,Extrude010]
FEATURE [Part::Feature] Face030
  shape: bbox 1.791 x 1.578 x 2e-07 mm, 1 faces, 0 solids (baked)
FEATURE [Part::Extrusion] Extrude011
  Base = -> Face030
  Dir = (0,0,0.3)
  DirMode = 0
  FaceMakerClass = Part::FaceMakerExtrusion
  LengthFwd = 0
  LengthRev = 0
  Placement = pos=(-0.75,0,47.5) rot=(0,0,1;3.14159rad)
  Solid = false
  Symmetric = false
FEATURE [Part::Feature] Face031
  shape: bbox 1.791 x 1.578 x 2e-07 mm, 1 faces, 0 solids (baked)
FEATURE [Part::Extrusion] Extrude012
  Base = -> Face031
  Dir = (0,0,0.3)
  DirMode = 0
  FaceMakerClass = Part::FaceMakerExtrusion
  LengthFwd = 0
  LengthRev = 0
  Placement = pos=(0.75,0,47.5) rot=(0,0,1;0rad)
  Solid = false
  Symmetric = false
FEATURE [Part::MultiFuse] Fusion288
  Placement = pos=(0,0,0) rot=(0,0,1;4.18879rad)
  Refine = true
  Shapes = -> [Extrude011,Extrude012]
FEATURE [Part::MultiFuse] Fusion289  label="hub-cap-rear-00"
  Refine = true
  Shapes = -> [Cut460,Fillet284,Fusion288,Fusion287,Fusion286]
FEATURE [Part::Cylinder] Cylinder486
  Angle = 360
  AttacherType = Attacher::AttachEngine3D
  Height = 20
  Radius = 23.5
FEATURE [Part::Cylinder] Cylinder487
  Angle = 360
  AttacherType = Attacher::AttachEngine3D
  Height = 17
  Radius = 23.5
FEATURE [Part::Cylinder] Cylinder488
  Angle = 360
  AttacherType = Attacher::AttachEngine3D
  Height = 17
  Radius = 22.1
FEATURE [Part::Cut] Cut488  label="Cut800"
  Base = -> Cylinder487
  Placement = pos=(0,0,1.5) rot=(0,0,1;0rad)
  Refine = true
  Tool = -> Cylinder488
FEATURE [Part::Cut] Cut489  label="Cut801"
  Base = -> Cylinder486
  Refine = true
  Tool = -> Cut488
FEATURE [Part::Cylinder] Cylinder489
  Angle = 360
  AttacherType = Attacher::AttachEngine3D
  Height = 17
  Radius = 22
FEATURE [Part::Cylinder] Cylinder490
  Angle = 360
  AttacherType = Attacher::AttachEngine3D
  Height = 10
  Placement = pos=(0,0,0.5) rot=(0,0,1;0rad)
  Radius = 23.5
FEATURE [Part::Cut] Cut490  label="Cut802"
  Base = -> Cylinder490
  Placement = pos=(0,0,4.5) rot=(0,0,1;0rad)
  Refine = true
  Tool = -> Cylinder489
FEATURE [Part::Cylinder] Cylinder491
  Angle = 360
  AttacherType = Attacher::AttachEngine3D
  Height = 20
  Radius = 18.5
FEATURE [Part::MultiFuse] Fusion336
  Refine = true
  Shapes = -> [Cut490,Cut489]
FEATURE [Part::Cut] Cut491  label="Cut803"
  Base = -> Fusion336
  Refine = true
  Tool = -> Cylinder491
FEATURE [Part::Cone] Cone010
  Angle = 360
  AttacherType = Attacher::AttachEngine3D
  Height = 7
  Placement = pos=(0,0,15) rot=(0,0,1;0rad)
  Radius1 = 21
  Radius2 = 15
FEATURE [Part::Cylinder] Cylinder492
  Angle = 360
  AttacherType = Attacher::AttachEngine3D
  Height = 10
  Placement = pos=(0,0,15) rot=(0,0,1;0rad)
  Radius = 20.5
FEATURE [Part::Cut] Cut492  label="Cut804"
  Base = -> Cut491
  Refine = true
  Tool = -> Cylinder492
FEATURE [Part::Fillet] Fillet293
  Base = -> Cut492
  Edges = 1 edges r=1: [Edge20]
FEATURE [Part::Cylinder] Cylinder493
  Angle = 360
  AttacherType = Attacher::AttachEngine3D
  Height = 12
  Radius = 20
FEATURE [Part::Cylinder] Cylinder494
  Angle = 360
  AttacherType = Attacher::AttachEngine3D
  Height = 26
  Radius = 10
FEATURE [Part::Cylinder] Cylinder495
  Angle = 360
  AttacherType = Attacher::AttachEngine3D
  Height = 8
  Placement = pos=(12,0,16) rot=(0,1,0;1.01229rad)
  Radius = 2.5
FEATURE [Part::Mirroring] Part__Mirroring060  label="Cylinder107 (Mirror #1)024"
  Base = (0,0,0)
  Normal = (1,0,0)
  Source = -> Cylinder495
FEATURE [Part::Cylinder] Cylinder496
  Angle = 360
  AttacherType = Attacher::AttachEngine3D
  Height = 8
  Placement = pos=(12,0,16) rot=(0,1,0;1.01229rad)
  Radius = 2.5
FEATURE [Part::MultiFuse] Fusion337
  Refine = true
  Shapes = -> [Cylinder496,Part__Mirroring060]
FEATURE [Part::Cylinder] Cylinder497
  Angle = 360
  AttacherType = Attacher::AttachEngine3D
  Height = 8
  Placement = pos=(12,0,16) rot=(0,1,0;1.01229rad)
  Radius = 2.5
FEATURE [Part::Cylinder] Cylinder498
  Angle = 360
  AttacherType = Attacher::AttachEngine3D
  Height = 8
  Placement = pos=(12,0,16) rot=(0,1,0;1.01229rad)
  Radius = 2.5
FEATURE [Part::Mirroring] Part__Mirroring061  label="Cylinder107 (Mirror #1)025"
  Base = (0,0,0)
  Normal = (1,0,0)
  Source = -> Cylinder498
FEATURE [Part::MultiFuse] Fusion338
  Placement = pos=(0,0,0) rot=(0,0,1;0.628319rad)
  Refine = true
  Shapes = -> [Cylinder497,Part__Mirroring061]
FEATURE [Part::Cylinder] Cylinder499
  Angle = 360
  AttacherType = Attacher::AttachEngine3D
  Height = 8
  Placement = pos=(12,0,16) rot=(0,1,0;1.01229rad)
  Radius = 2.5
FEATURE [Part::Cylinder] Cylinder500
  Angle = 360
  AttacherType = Attacher::AttachEngine3D
  Height = 8
  Placement = pos=(12,0,16) rot=(0,1,0;1.01229rad)
  Radius = 2.5
FEATURE [Part::Mirroring] Part__Mirroring062  label="Cylinder107 (Mirror #1)026"
  Base = (0,0,0)
  Normal = (1,0,0)
  Source = -> Cylinder500
FEATURE [Part::MultiFuse] Fusion339
  Placement = pos=(0,0,0) rot=(0,0,1;1.25664rad)
  Refine = true
  Shapes = -> [Cylinder499,Part__Mirroring062]
FEATURE [Part::Cylinder] Cylinder501
  Angle = 360
  AttacherType = Attacher::AttachEngine3D
  Height = 8
  Placement = pos=(12,0,16) rot=(0,1,0;1.01229rad)
  Radius = 2.5
FEATURE [Part::Cylinder] Cylinder502
  Angle = 360
  AttacherType = Attacher::AttachEngine3D
  Height = 8
  Placement = pos=(12,0,16) rot=(0,1,0;1.01229rad)
  Radius = 2.5
FEATURE [Part::Mirroring] Part__Mirroring063  label="Cylinder107 (Mirror #1)027"
  Base = (0,0,0)
  Normal = (1,0,0)
  Source = -> Cylinder502
FEATURE [Part::MultiFuse] Fusion340
  Placement = pos=(0,0,0) rot=(0,0,1;1.88496rad)
  Refine = true
  Shapes = -> [Cylinder501,Part__Mirroring063]
FEATURE [Part::Cylinder] Cylinder503
  Angle = 360
  AttacherType = Attacher::AttachEngine3D
  Height = 8
  Placement = pos=(12,0,16) rot=(0,1,0;1.01229rad)
  Radius = 2.5
FEATURE [Part::Cylinder] Cylinder504
  Angle = 360
  AttacherType = Attacher::AttachEngine3D
  Height = 8
  Placement = pos=(12,0,16) rot=(0,1,0;1.01229rad)
  Radius = 2.5
FEATURE [Part::Mirroring] Part__Mirroring064  label="Cylinder107 (Mirror #1)028"
  Base = (0,0,0)
  Normal = (1,0,0)
  Source = -> Cylinder504
FEATURE [Part::MultiFuse] Fusion341
  Placement = pos=(0,0,0) rot=(0,0,1;2.51327rad)
  Refine = true
  Shapes = -> [Cylinder503,Part__Mirroring064]
FEATURE [Part::MultiFuse] Fusion342
  Placement = pos=(0,0,-1) rot=(0,0,1;0rad)
  Refine = true
  Shapes = -> [Fusion337,Fusion338,Fusion339,Fusion340,Fusion341]
FEATURE [Part::Cylinder] Cylinder505
  Angle = 360
  AttacherType = Attacher::AttachEngine3D
  Height = 10
  Placement = pos=(12.5,0,13) rot=(0,0,1;0rad)
  Radius = 1.1
FEATURE [Part::Cylinder] Cylinder506
  Angle = 360
  AttacherType = Attacher::AttachEngine3D
  Height = 10
  Placement = pos=(-12.5,0,13) rot=(0,0,1;0rad)
  Radius = 1.1
FEATURE [Part::MultiFuse] Fusion343
  Placement = pos=(0,0,0) rot=(0,0,1;0.314159rad)
  Refine = true
  Shapes = -> [Cylinder505,Cylinder506]
FEATURE [Part::Cylinder] Cylinder507
  Angle = 360
  AttacherType = Attacher::AttachEngine3D
  Height = 10
  Placement = pos=(12.5,0,13) rot=(0,0,1;0rad)
  Radius = 1.1
FEATURE [Part::Cylinder] Cylinder508
  Angle = 360
  AttacherType = Attacher::AttachEngine3D
  Height = 10
  Placement = pos=(-12.5,0,13) rot=(0,0,1;0rad)
  Radius = 1.1
FEATURE [Part::MultiFuse] Fusion344
  Placement = pos=(0,0,0) rot=(0,0,1;0.942478rad)
  Refine = true
  Shapes = -> [Cylinder507,Cylinder508]
FEATURE [Part::Cylinder] Cylinder509
  Angle = 360
  AttacherType = Attacher::AttachEngine3D
  Height = 10
  Placement = pos=(12.5,0,13) rot=(0,0,1;0rad)
  Radius = 1.1
FEATURE [Part::Cylinder] Cylinder510
  Angle = 360
  AttacherType = Attacher::AttachEngine3D
  Height = 10
  Placement = pos=(-12.5,0,13) rot=(0,0,1;0rad)
  Radius = 1.1
FEATURE [Part::MultiFuse] Fusion345
  Placement = pos=(0,0,0) rot=(0,0,1;1.5708rad)
  Refine = true
  Shapes = -> [Cylinder509,Cylinder510]
FEATURE [Part::Cylinder] Cylinder511
  Angle = 360
  AttacherType = Attacher::AttachEngine3D
  Height = 10
  Placement = pos=(12.5,0,13) rot=(0,0,1;0rad)
  Radius = 1.1
FEATURE [Part::Cylinder] Cylinder512
  Angle = 360
  AttacherType = Attacher::AttachEngine3D
  Height = 10
  Placement = pos=(-12.5,0,13) rot=(0,0,1;0rad)
  Radius = 1.1
FEATURE [Part::MultiFuse] Fusion346
  Placement = pos=(0,0,0) rot=(0,0,1;2.19911rad)
  Refine = true
  Shapes = -> [Cylinder511,Cylinder512]
FEATURE [Part::Cylinder] Cylinder513
  Angle = 360
  AttacherType = Attacher::AttachEngine3D
  Height = 10
  Placement = pos=(12.5,0,13) rot=(0,0,1;0rad)
  Radius = 1.1
FEATURE [Part::Cylinder] Cylinder514
  Angle = 360
  AttacherType = Attacher::AttachEngine3D
  Height = 10
  Placement = pos=(-12.5,0,13) rot=(0,0,1;0rad)
  Radius = 1.1
FEATURE [Part::MultiFuse] Fusion347
  Placement = pos=(0,0,0) rot=(0,0,1;2.82743rad)
  Refine = true
  Shapes = -> [Cylinder513,Cylinder514]
FEATURE [Part::MultiFuse] Fusion348
  Refine = true
  Shapes = -> [Fusion343,Fusion344,Fusion347,Fusion346,Fusion345]
FEATURE [Part::Cone] Cone011
  Angle = 360
  AttacherType = Attacher::AttachEngine3D
  Height = 10
  Placement = pos=(0,0,9) rot=(0,0,1;0rad)
  Radius1 = 24
  Radius2 = 15
FEATURE [Part::Cut] Cut493  label="Cut805"
  Base = -> Cone010
  Refine = true
  Tool = -> Cylinder494
FEATURE [Part::Cut] Cut494  label="Cut806"
  Base = -> Cut493
  Refine = true
  Tool = -> Cone011
FEATURE [Part::MultiFuse] Fusion349
  Refine = true
  Shapes = -> [Fillet293,Cut494]
FEATURE [Part::Cut] Cut495  label="Cut807"
  Base = -> Fusion349
  Refine = true
  Tool = -> Cylinder493
FEATURE [Part::Chamfer] Chamfer066
  Base = -> Cut495
  Edges = 1 edges r=1.49: [Edge39]
FEATURE [Part::Chamfer] Chamfer067
  Base = -> Chamfer066
  Edges = 1 edges r=2: [Edge10]
FEATURE [Part::Cut] Cut496  label="Cut808"
  Base = -> Chamfer067
  Refine = true
  Tool = -> Fusion342
FEATURE [Part::Cut] Cut497  label="Cut809"
  Base = -> Cut496
  Refine = true
  Tool = -> Fusion348
FEATURE [Part::Fillet] Fillet294
  Base = -> Cut497
  Edges = 1 edges r=1.5: [Edge121]
FEATURE [Part::Fillet] Fillet295  label="rim-left-front"
  Base = -> Fillet294
  Edges = 1 edges r=1.5: [Edge161]
  Placement = pos=(98,16,-51) rot=(1,0,0;1.5708rad)
FEATURE [Part::Cylinder] Cylinder515
  Angle = 360
  AttacherType = Attacher::AttachEngine3D
  Height = 20
  Radius = 23.5
FEATURE [Part::Cylinder] Cylinder516
  Angle = 360
  AttacherType = Attacher::AttachEngine3D
  Height = 17
  Radius = 23.5
FEATURE [Part::Cylinder] Cylinder517
  Angle = 360
  AttacherType = Attacher::AttachEngine3D
  Height = 17
  Radius = 22.1
FEATURE [Part::Cut] Cut498  label="Cut810"
  Base = -> Cylinder516
  Placement = pos=(0,0,1.5) rot=(0,0,1;0rad)
  Refine = true
  Tool = -> Cylinder517
FEATURE [Part::Cut] Cut499  label="Cut811"
  Base = -> Cylinder515
  Refine = true
  Tool = -> Cut498
FEATURE [Part::Cylinder] Cylinder518
  Angle = 360
  AttacherType = Attacher::AttachEngine3D
  Height = 17
  Radius = 22
FEATURE [Part::Cylinder] Cylinder519
  Angle = 360
  AttacherType = Attacher::AttachEngine3D
  Height = 10
  Placement = pos=(0,0,0.5) rot=(0,0,1;0rad)
  Radius = 23.5
FEATURE [Part::Cut] Cut500  label="Cut812"
  Base = -> Cylinder519
  Placement = pos=(0,0,4.5) rot=(0,0,1;0rad)
  Refine = true
  Tool = -> Cylinder518
FEATURE [Part::Cylinder] Cylinder520
  Angle = 360
  AttacherType = Attacher::AttachEngine3D
  Height = 20
  Radius = 18.5
FEATURE [Part::MultiFuse] Fusion350
  Refine = true
  Shapes = -> [Cut500,Cut499]
FEATURE [Part::Cut] Cut501  label="Cut813"
  Base = -> Fusion350
  Refine = true
  Tool = -> Cylinder520
FEATURE [Part::Cone] Cone012
  Angle = 360
  AttacherType = Attacher::AttachEngine3D
  Height = 7
  Placement = pos=(0,0,15) rot=(0,0,1;0rad)
  Radius1 = 21
  Radius2 = 15
FEATURE [Part::Cylinder] Cylinder521
  Angle = 360
  AttacherType = Attacher::AttachEngine3D
  Height = 10
  Placement = pos=(0,0,15) rot=(0,0,1;0rad)
  Radius = 20.5
FEATURE [Part::Cut] Cut502  label="Cut814"
  Base = -> Cut501
  Refine = true
  Tool = -> Cylinder521
FEATURE [Part::Fillet] Fillet296
  Base = -> Cut502
  Edges = 1 edges r=1: [Edge20]
FEATURE [Part::Cylinder] Cylinder522
  Angle = 360
  AttacherType = Attacher::AttachEngine3D
  Height = 12
  Radius = 20
FEATURE [Part::Cylinder] Cylinder523
  Angle = 360
  AttacherType = Attacher::AttachEngine3D
  Height = 26
  Radius = 10
FEATURE [Part::Cylinder] Cylinder524
  Angle = 360
  AttacherType = Attacher::AttachEngine3D
  Height = 8
  Placement = pos=(12,0,16) rot=(0,1,0;1.01229rad)
  Radius = 2.5
FEATURE [Part::Mirroring] Part__Mirroring065  label="Cylinder107 (Mirror #1)029"
  Base = (0,0,0)
  Normal = (1,0,0)
  Source = -> Cylinder524
FEATURE [Part::Cylinder] Cylinder525
  Angle = 360
  AttacherType = Attacher::AttachEngine3D
  Height = 8
  Placement = pos=(12,0,16) rot=(0,1,0;1.01229rad)
  Radius = 2.5
FEATURE [Part::MultiFuse] Fusion351
  Refine = true
  Shapes = -> [Cylinder525,Part__Mirroring065]
FEATURE [Part::Cylinder] Cylinder526
  Angle = 360
  AttacherType = Attacher::AttachEngine3D
  Height = 8
  Placement = pos=(12,0,16) rot=(0,1,0;1.01229rad)
  Radius = 2.5
FEATURE [Part::Cylinder] Cylinder527
  Angle = 360
  AttacherType = Attacher::AttachEngine3D
  Height = 8
  Placement = pos=(12,0,16) rot=(0,1,0;1.01229rad)
  Radius = 2.5
FEATURE [Part::Mirroring] Part__Mirroring066  label="Cylinder107 (Mirror #1)030"
  Base = (0,0,0)
  Normal = (1,0,0)
  Source = -> Cylinder527
FEATURE [Part::MultiFuse] Fusion352
  Placement = pos=(0,0,0) rot=(0,0,1;0.628319rad)
  Refine = true
  Shapes = -> [Cylinder526,Part__Mirroring066]
FEATURE [Part::Cylinder] Cylinder528
  Angle = 360
  AttacherType = Attacher::AttachEngine3D
  Height = 8
  Placement = pos=(12,0,16) rot=(0,1,0;1.01229rad)
  Radius = 2.5
FEATURE [Part::Cylinder] Cylinder529
  Angle = 360
  AttacherType = Attacher::AttachEngine3D
  Height = 8
  Placement = pos=(12,0,16) rot=(0,1,0;1.01229rad)
  Radius = 2.5
FEATURE [Part::Mirroring] Part__Mirroring067  label="Cylinder107 (Mirror #1)031"
  Base = (0,0,0)
  Normal = (1,0,0)
  Source = -> Cylinder529
FEATURE [Part::MultiFuse] Fusion353
  Placement = pos=(0,0,0) rot=(0,0,1;1.25664rad)
  Refine = true
  Shapes = -> [Cylinder528,Part__Mirroring067]
FEATURE [Part::Cylinder] Cylinder530
  Angle = 360
  AttacherType = Attacher::AttachEngine3D
  Height = 8
  Placement = pos=(12,0,16) rot=(0,1,0;1.01229rad)
  Radius = 2.5
FEATURE [Part::Cylinder] Cylinder531
  Angle = 360
  AttacherType = Attacher::AttachEngine3D
  Height = 8
  Placement = pos=(12,0,16) rot=(0,1,0;1.01229rad)
  Radius = 2.5
FEATURE [Part::Mirroring] Part__Mirroring068  label="Cylinder107 (Mirror #1)032"
  Base = (0,0,0)
  Normal = (1,0,0)
  Source = -> Cylinder531
FEATURE [Part::MultiFuse] Fusion354
  Placement = pos=(0,0,0) rot=(0,0,1;1.88496rad)
  Refine = true
  Shapes = -> [Cylinder530,Part__Mirroring068]
FEATURE [Part::Cylinder] Cylinder532
  Angle = 360
  AttacherType = Attacher::AttachEngine3D
  Height = 8
  Placement = pos=(12,0,16) rot=(0,1,0;1.01229rad)
  Radius = 2.5
FEATURE [Part::Cylinder] Cylinder533
  Angle = 360
  AttacherType = Attacher::AttachEngine3D
  Height = 8
  Placement = pos=(12,0,16) rot=(0,1,0;1.01229rad)
  Radius = 2.5
FEATURE [Part::Mirroring] Part__Mirroring069  label="Cylinder107 (Mirror #1)033"
  Base = (0,0,0)
  Normal = (1,0,0)
  Source = -> Cylinder533
FEATURE [Part::MultiFuse] Fusion355
  Placement = pos=(0,0,0) rot=(0,0,1;2.51327rad)
  Refine = true
  Shapes = -> [Cylinder532,Part__Mirroring069]
FEATURE [Part::MultiFuse] Fusion356
  Placement = pos=(0,0,-1) rot=(0,0,1;0rad)
  Refine = true
  Shapes = -> [Fusion351,Fusion352,Fusion353,Fusion354,Fusion355]
FEATURE [Part::Cylinder] Cylinder534
  Angle = 360
  AttacherType = Attacher::AttachEngine3D
  Height = 10
  Placement = pos=(12.5,0,13) rot=(0,0,1;0rad)
  Radius = 1.1
FEATURE [Part::Cylinder] Cylinder535
  Angle = 360
  AttacherType = Attacher::AttachEngine3D
  Height = 10
  Placement = pos=(-12.5,0,13) rot=(0,0,1;0rad)
  Radius = 1.1
FEATURE [Part::MultiFuse] Fusion357
  Placement = pos=(0,0,0) rot=(0,0,1;0.314159rad)
  Refine = true
  Shapes = -> [Cylinder534,Cylinder535]
FEATURE [Part::Cylinder] Cylinder536
  Angle = 360
  AttacherType = Attacher::AttachEngine3D
  Height = 10
  Placement = pos=(12.5,0,13) rot=(0,0,1;0rad)
  Radius = 1.1
FEATURE [Part::Cylinder] Cylinder537
  Angle = 360
  AttacherType = Attacher::AttachEngine3D
  Height = 10
  Placement = pos=(-12.5,0,13) rot=(0,0,1;0rad)
  Radius = 1.1
FEATURE [Part::MultiFuse] Fusion358
  Placement = pos=(0,0,0) rot=(0,0,1;0.942478rad)
  Refine = true
  Shapes = -> [Cylinder536,Cylinder537]
FEATURE [Part::Cylinder] Cylinder538
  Angle = 360
  AttacherType = Attacher::AttachEngine3D
  Height = 10
  Placement = pos=(12.5,0,13) rot=(0,0,1;0rad)
  Radius = 1.1
FEATURE [Part::Cylinder] Cylinder539
  Angle = 360
  AttacherType = Attacher::AttachEngine3D
  Height = 10
  Placement = pos=(-12.5,0,13) rot=(0,0,1;0rad)
  Radius = 1.1
FEATURE [Part::MultiFuse] Fusion359
  Placement = pos=(0,0,0) rot=(0,0,1;1.5708rad)
  Refine = true
  Shapes = -> [Cylinder538,Cylinder539]
FEATURE [Part::Cylinder] Cylinder540
  Angle = 360
  AttacherType = Attacher::AttachEngine3D
  Height = 10
  Placement = pos=(12.5,0,13) rot=(0,0,1;0rad)
  Radius = 1.1
FEATURE [Part::Cylinder] Cylinder541
  Angle = 360
  AttacherType = Attacher::AttachEngine3D
  Height = 10
  Placement = pos=(-12.5,0,13) rot=(0,0,1;0rad)
  Radius = 1.1
FEATURE [Part::MultiFuse] Fusion360
  Placement = pos=(0,0,0) rot=(0,0,1;2.19911rad)
  Refine = true
  Shapes = -> [Cylinder540,Cylinder541]
FEATURE [Part::Cylinder] Cylinder542
  Angle = 360
  AttacherType = Attacher::AttachEngine3D
  Height = 10
  Placement = pos=(12.5,0,13) rot=(0,0,1;0rad)
  Radius = 1.1
FEATURE [Part::Cylinder] Cylinder543
  Angle = 360
  AttacherType = Attacher::AttachEngine3D
  Height = 10
  Placement = pos=(-12.5,0,13) rot=(0,0,1;0rad)
  Radius = 1.1
FEATURE [Part::MultiFuse] Fusion361
  Placement = pos=(0,0,0) rot=(0,0,1;2.82743rad)
  Refine = true
  Shapes = -> [Cylinder542,Cylinder543]
FEATURE [Part::MultiFuse] Fusion362
  Refine = true
  Shapes = -> [Fusion357,Fusion358,Fusion361,Fusion360,Fusion359]
FEATURE [Part::Cone] Cone013
  Angle = 360
  AttacherType = Attacher::AttachEngine3D
  Height = 10
  Placement = pos=(0,0,9) rot=(0,0,1;0rad)
  Radius1 = 24
  Radius2 = 15
FEATURE [Part::Cut] Cut503  label="Cut815"
  Base = -> Cone012
  Refine = true
  Tool = -> Cylinder523
FEATURE [Part::Cut] Cut504  label="Cut816"
  Base = -> Cut503
  Refine = true
  Tool = -> Cone013
FEATURE [Part::MultiFuse] Fusion363
  Refine = true
  Shapes = -> [Fillet296,Cut504]
FEATURE [Part::Cut] Cut505  label="Cut817"
  Base = -> Fusion363
  Refine = true
  Tool = -> Cylinder522
FEATURE [Part::Chamfer] Chamfer068
  Base = -> Cut505
  Edges = 1 edges r=1.49: [Edge39]
FEATURE [Part::Chamfer] Chamfer069
  Base = -> Chamfer068
  Edges = 1 edges r=2: [Edge10]
FEATURE [Part::Cut] Cut506  label="Cut818"
  Base = -> Chamfer069
  Refine = true
  Tool = -> Fusion356
FEATURE [Part::Cut] Cut507  label="Cut819"
  Base = -> Cut506
  Refine = true
  Tool = -> Fusion362
FEATURE [Part::Fillet] Fillet297
  Base = -> Cut507
  Edges = 1 edges r=1.5: [Edge121]
FEATURE [Part::Fillet] Fillet298  label="rim-left-front001"
  Base = -> Fillet297
  Edges = 1 edges r=1.5: [Edge161]
  Placement = pos=(98,17,-52) rot=(1,0,0;1.5708rad)
FEATURE [Part::Mirroring] Part__Mirroring070  label="rim-right-front"
  Base = (0,0,0)
  Normal = (0,1,0)
  Placement = pos=(0,171,1) rot=(0,0,1;0rad)
  Source = -> Fillet298
FEATURE [Part::Cylinder] Cylinder544
  Angle = 360
  AttacherType = Attacher::AttachEngine3D
  Height = 20
  Radius = 23.5
FEATURE [Part::Cylinder] Cylinder545
  Angle = 360
  AttacherType = Attacher::AttachEngine3D
  Height = 17
  Radius = 23.5
FEATURE [Part::Cylinder] Cylinder546
  Angle = 360
  AttacherType = Attacher::AttachEngine3D
  Height = 17
  Radius = 22.1
FEATURE [Part::Cut] Cut508  label="Cut820"
  Base = -> Cylinder545
  Placement = pos=(0,0,1.5) rot=(0,0,1;0rad)
  Refine = true
  Tool = -> Cylinder546
FEATURE [Part::Cut] Cut509  label="Cut821"
  Base = -> Cylinder544
  Refine = true
  Tool = -> Cut508
FEATURE [Part::Cylinder] Cylinder547
  Angle = 360
  AttacherType = Attacher::AttachEngine3D
  Height = 17
  Radius = 22
FEATURE [Part::Cylinder] Cylinder548
  Angle = 360
  AttacherType = Attacher::AttachEngine3D
  Height = 10
  Placement = pos=(0,0,0.5) rot=(0,0,1;0rad)
  Radius = 23.5
FEATURE [Part::Cut] Cut510  label="Cut822"
  Base = -> Cylinder548
  Placement = pos=(0,0,4.5) rot=(0,0,1;0rad)
  Refine = true
  Tool = -> Cylinder547
FEATURE [Part::Cylinder] Cylinder549
  Angle = 360
  AttacherType = Attacher::AttachEngine3D
  Height = 20
  Radius = 18.5
FEATURE [Part::MultiFuse] Fusion364
  Refine = true
  Shapes = -> [Cut510,Cut509]
FEATURE [Part::Cut] Cut511  label="Cut823"
  Base = -> Fusion364
  Refine = true
  Tool = -> Cylinder549
FEATURE [Part::Cone] Cone014
  Angle = 360
  AttacherType = Attacher::AttachEngine3D
  Height = 7
  Placement = pos=(0,0,15) rot=(0,0,1;0rad)
  Radius1 = 21
  Radius2 = 15
FEATURE [Part::Cylinder] Cylinder550
  Angle = 360
  AttacherType = Attacher::AttachEngine3D
  Height = 10
  Placement = pos=(0,0,15) rot=(0,0,1;0rad)
  Radius = 20.5
FEATURE [Part::Cut] Cut512  label="Cut824"
  Base = -> Cut511
  Refine = true
  Tool = -> Cylinder550
FEATURE [Part::Fillet] Fillet299
  Base = -> Cut512
  Edges = 1 edges r=1: [Edge20]
FEATURE [Part::Cylinder] Cylinder551
  Angle = 360
  AttacherType = Attacher::AttachEngine3D
  Height = 12
  Radius = 20
FEATURE [Part::Cylinder] Cylinder552
  Angle = 360
  AttacherType = Attacher::AttachEngine3D
  Height = 26
  Radius = 10
FEATURE [Part::Cylinder] Cylinder553
  Angle = 360
  AttacherType = Attacher::AttachEngine3D
  Height = 8
  Placement = pos=(12,0,16) rot=(0,1,0;1.01229rad)
  Radius = 2.5
FEATURE [Part::Mirroring] Part__Mirroring071  label="Cylinder107 (Mirror #1)034"
  Base = (0,0,0)
  Normal = (1,0,0)
  Source = -> Cylinder553
FEATURE [Part::Cylinder] Cylinder554
  Angle = 360
  AttacherType = Attacher::AttachEngine3D
  Height = 8
  Placement = pos=(12,0,16) rot=(0,1,0;1.01229rad)
  Radius = 2.5
FEATURE [Part::MultiFuse] Fusion365
  Refine = true
  Shapes = -> [Cylinder554,Part__Mirroring071]
FEATURE [Part::Cylinder] Cylinder555
  Angle = 360
  AttacherType = Attacher::AttachEngine3D
  Height = 8
  Placement = pos=(12,0,16) rot=(0,1,0;1.01229rad)
  Radius = 2.5
FEATURE [Part::Cylinder] Cylinder556
  Angle = 360
  AttacherType = Attacher::AttachEngine3D
  Height = 8
  Placement = pos=(12,0,16) rot=(0,1,0;1.01229rad)
  Radius = 2.5
FEATURE [Part::Mirroring] Part__Mirroring072  label="Cylinder107 (Mirror #1)035"
  Base = (0,0,0)
  Normal = (1,0,0)
  Source = -> Cylinder556
FEATURE [Part::MultiFuse] Fusion366
  Placement = pos=(0,0,0) rot=(0,0,1;0.628319rad)
  Refine = true
  Shapes = -> [Cylinder555,Part__Mirroring072]
FEATURE [Part::Cylinder] Cylinder557
  Angle = 360
  AttacherType = Attacher::AttachEngine3D
  Height = 8
  Placement = pos=(12,0,16) rot=(0,1,0;1.01229rad)
  Radius = 2.5
FEATURE [Part::Cylinder] Cylinder558
  Angle = 360
  AttacherType = Attacher::AttachEngine3D
  Height = 8
  Placement = pos=(12,0,16) rot=(0,1,0;1.01229rad)
  Radius = 2.5
FEATURE [Part::Mirroring] Part__Mirroring073  label="Cylinder107 (Mirror #1)036"
  Base = (0,0,0)
  Normal = (1,0,0)
  Source = -> Cylinder558
FEATURE [Part::MultiFuse] Fusion367
  Placement = pos=(0,0,0) rot=(0,0,1;1.25664rad)
  Refine = true
  Shapes = -> [Cylinder557,Part__Mirroring073]
FEATURE [Part::Cylinder] Cylinder559
  Angle = 360
  AttacherType = Attacher::AttachEngine3D
  Height = 8
  Placement = pos=(12,0,16) rot=(0,1,0;1.01229rad)
  Radius = 2.5
FEATURE [Part::Cylinder] Cylinder560
  Angle = 360
  AttacherType = Attacher::AttachEngine3D
  Height = 8
  Placement = pos=(12,0,16) rot=(0,1,0;1.01229rad)
  Radius = 2.5
FEATURE [Part::Mirroring] Part__Mirroring074  label="Cylinder107 (Mirror #1)037"
  Base = (0,0,0)
  Normal = (1,0,0)
  Source = -> Cylinder560
FEATURE [Part::MultiFuse] Fusion368
  Placement = pos=(0,0,0) rot=(0,0,1;1.88496rad)
  Refine = true
  Shapes = -> [Cylinder559,Part__Mirroring074]
FEATURE [Part::Cylinder] Cylinder561
  Angle = 360
  AttacherType = Attacher::AttachEngine3D
  Height = 8
  Placement = pos=(12,0,16) rot=(0,1,0;1.01229rad)
  Radius = 2.5
FEATURE [Part::Cylinder] Cylinder562
  Angle = 360
  AttacherType = Attacher::AttachEngine3D
  Height = 8
  Placement = pos=(12,0,16) rot=(0,1,0;1.01229rad)
  Radius = 2.5
FEATURE [Part::Mirroring] Part__Mirroring075  label="Cylinder107 (Mirror #1)038"
  Base = (0,0,0)
  Normal = (1,0,0)
  Source = -> Cylinder562
FEATURE [Part::MultiFuse] Fusion369
  Placement = pos=(0,0,0) rot=(0,0,1;2.51327rad)
  Refine = true
  Shapes = -> [Cylinder561,Part__Mirroring075]
FEATURE [Part::MultiFuse] Fusion370
  Placement = pos=(0,0,-1) rot=(0,0,1;0rad)
  Refine = true
  Shapes = -> [Fusion365,Fusion366,Fusion367,Fusion368,Fusion369]
FEATURE [Part::Cylinder] Cylinder563
  Angle = 360
  AttacherType = Attacher::AttachEngine3D
  Height = 10
  Placement = pos=(12.5,0,13) rot=(0,0,1;0rad)
  Radius = 1.1
FEATURE [Part::Cylinder] Cylinder564
  Angle = 360
  AttacherType = Attacher::AttachEngine3D
  Height = 10
  Placement = pos=(-12.5,0,13) rot=(0,0,1;0rad)
  Radius = 1.1
FEATURE [Part::MultiFuse] Fusion371
  Placement = pos=(0,0,0) rot=(0,0,1;0.314159rad)
  Refine = true
  Shapes = -> [Cylinder563,Cylinder564]
FEATURE [Part::Cylinder] Cylinder565
  Angle = 360
  AttacherType = Attacher::AttachEngine3D
  Height = 10
  Placement = pos=(12.5,0,13) rot=(0,0,1;0rad)
  Radius = 1.1
FEATURE [Part::Cylinder] Cylinder566
  Angle = 360
  AttacherType = Attacher::AttachEngine3D
  Height = 10
  Placement = pos=(-12.5,0,13) rot=(0,0,1;0rad)
  Radius = 1.1
FEATURE [Part::MultiFuse] Fusion372
  Placement = pos=(0,0,0) rot=(0,0,1;0.942478rad)
  Refine = true
  Shapes = -> [Cylinder565,Cylinder566]
FEATURE [Part::Cylinder] Cylinder567
  Angle = 360
  AttacherType = Attacher::AttachEngine3D
  Height = 10
  Placement = pos=(12.5,0,13) rot=(0,0,1;0rad)
  Radius = 1.1
FEATURE [Part::Cylinder] Cylinder568
  Angle = 360
  AttacherType = Attacher::AttachEngine3D
  Height = 10
  Placement = pos=(-12.5,0,13) rot=(0,0,1;0rad)
  Radius = 1.1
FEATURE [Part::MultiFuse] Fusion373
  Placement = pos=(0,0,0) rot=(0,0,1;1.5708rad)
  Refine = true
  Shapes = -> [Cylinder567,Cylinder568]
FEATURE [Part::Cylinder] Cylinder569
  Angle = 360
  AttacherType = Attacher::AttachEngine3D
  Height = 10
  Placement = pos=(12.5,0,13) rot=(0,0,1;0rad)
  Radius = 1.1
FEATURE [Part::Cylinder] Cylinder570
  Angle = 360
  AttacherType = Attacher::AttachEngine3D
  Height = 10
  Placement = pos=(-12.5,0,13) rot=(0,0,1;0rad)
  Radius = 1.1
FEATURE [Part::MultiFuse] Fusion374
  Placement = pos=(0,0,0) rot=(0,0,1;2.19911rad)
  Refine = true
  Shapes = -> [Cylinder569,Cylinder570]
FEATURE [Part::Cylinder] Cylinder571
  Angle = 360
  AttacherType = Attacher::AttachEngine3D
  Height = 10
  Placement = pos=(12.5,0,13) rot=(0,0,1;0rad)
  Radius = 1.1
FEATURE [Part::Cylinder] Cylinder572
  Angle = 360
  AttacherType = Attacher::AttachEngine3D
  Height = 10
  Placement = pos=(-12.5,0,13) rot=(0,0,1;0rad)
  Radius = 1.1
FEATURE [Part::MultiFuse] Fusion375
  Placement = pos=(0,0,0) rot=(0,0,1;2.82743rad)
  Refine = true
  Shapes = -> [Cylinder571,Cylinder572]
FEATURE [Part::MultiFuse] Fusion376
  Refine = true
  Shapes = -> [Fusion371,Fusion372,Fusion375,Fusion374,Fusion373]
FEATURE [Part::Cone] Cone015
  Angle = 360
  AttacherType = Attacher::AttachEngine3D
  Height = 10
  Placement = pos=(0,0,9) rot=(0,0,1;0rad)
  Radius1 = 24
  Radius2 = 15
FEATURE [Part::Cut] Cut513  label="Cut825"
  Base = -> Cone014
  Refine = true
  Tool = -> Cylinder552
FEATURE [Part::Cut] Cut514  label="Cut826"
  Base = -> Cut513
  Refine = true
  Tool = -> Cone015
FEATURE [Part::MultiFuse] Fusion377
  Refine = true
  Shapes = -> [Fillet299,Cut514]
FEATURE [Part::Cut] Cut515  label="Cut827"
  Base = -> Fusion377
  Refine = true
  Tool = -> Cylinder551
FEATURE [Part::Chamfer] Chamfer070
  Base = -> Cut515
  Edges = 1 edges r=1.49: [Edge39]
FEATURE [Part::Chamfer] Chamfer071
  Base = -> Chamfer070
  Edges = 1 edges r=2: [Edge10]
FEATURE [Part::Cut] Cut516  label="Cut828"
  Base = -> Chamfer071
  Refine = true
  Tool = -> Fusion370
FEATURE [Part::Cut] Cut517  label="Cut829"
  Base = -> Cut516
  Refine = true
  Tool = -> Fusion376
FEATURE [Part::Fillet] Fillet300
  Base = -> Cut517
  Edges = 1 edges r=1.5: [Edge121]
FEATURE [Part::Fillet] Fillet301  label="rim-left-middle"
  Base = -> Fillet300
  Edges = 1 edges r=1.5: [Edge161]
  Placement = pos=(348,17,-51) rot=(1,0,0;1.5708rad)
FEATURE [Part::Cylinder] Cylinder573
  Angle = 360
  AttacherType = Attacher::AttachEngine3D
  Height = 20
  Radius = 23.5
FEATURE [Part::Cylinder] Cylinder574
  Angle = 360
  AttacherType = Attacher::AttachEngine3D
  Height = 17
  Radius = 23.5
FEATURE [Part::Cylinder] Cylinder575
  Angle = 360
  AttacherType = Attacher::AttachEngine3D
  Height = 17
  Radius = 22.1
FEATURE [Part::Cut] Cut518  label="Cut830"
  Base = -> Cylinder574
  Placement = pos=(0,0,1.5) rot=(0,0,1;0rad)
  Refine = true
  Tool = -> Cylinder575
FEATURE [Part::Cut] Cut519  label="Cut831"
  Base = -> Cylinder573
  Refine = true
  Tool = -> Cut518
FEATURE [Part::Cylinder] Cylinder576
  Angle = 360
  AttacherType = Attacher::AttachEngine3D
  Height = 17
  Radius = 22
FEATURE [Part::Cylinder] Cylinder577
  Angle = 360
  AttacherType = Attacher::AttachEngine3D
  Height = 10
  Placement = pos=(0,0,0.5) rot=(0,0,1;0rad)
  Radius = 23.5
FEATURE [Part::Cut] Cut520  label="Cut832"
  Base = -> Cylinder577
  Placement = pos=(0,0,4.5) rot=(0,0,1;0rad)
  Refine = true
  Tool = -> Cylinder576
FEATURE [Part::Cylinder] Cylinder578
  Angle = 360
  AttacherType = Attacher::AttachEngine3D
  Height = 20
  Radius = 18.5
FEATURE [Part::MultiFuse] Fusion378
  Refine = true
  Shapes = -> [Cut520,Cut519]
FEATURE [Part::Cut] Cut521  label="Cut833"
  Base = -> Fusion378
  Refine = true
  Tool = -> Cylinder578
FEATURE [Part::Cone] Cone016
  Angle = 360
  AttacherType = Attacher::AttachEngine3D
  Height = 7
  Placement = pos=(0,0,15) rot=(0,0,1;0rad)
  Radius1 = 21
  Radius2 = 15
FEATURE [Part::Cylinder] Cylinder579
  Angle = 360
  AttacherType = Attacher::AttachEngine3D
  Height = 10
  Placement = pos=(0,0,15) rot=(0,0,1;0rad)
  Radius = 20.5
FEATURE [Part::Cut] Cut522  label="Cut834"
  Base = -> Cut521
  Refine = true
  Tool = -> Cylinder579
FEATURE [Part::Fillet] Fillet302
  Base = -> Cut522
  Edges = 1 edges r=1: [Edge20]
FEATURE [Part::Cylinder] Cylinder580
  Angle = 360
  AttacherType = Attacher::AttachEngine3D
  Height = 12
  Radius = 20
FEATURE [Part::Cylinder] Cylinder581
  Angle = 360
  AttacherType = Attacher::AttachEngine3D
  Height = 26
  Radius = 10
FEATURE [Part::Cylinder] Cylinder582
  Angle = 360
  AttacherType = Attacher::AttachEngine3D
  Height = 8
  Placement = pos=(12,0,16) rot=(0,1,0;1.01229rad)
  Radius = 2.5
FEATURE [Part::Mirroring] Part__Mirroring076  label="Cylinder107 (Mirror #1)039"
  Base = (0,0,0)
  Normal = (1,0,0)
  Source = -> Cylinder582
FEATURE [Part::Cylinder] Cylinder583
  Angle = 360
  AttacherType = Attacher::AttachEngine3D
  Height = 8
  Placement = pos=(12,0,16) rot=(0,1,0;1.01229rad)
  Radius = 2.5
FEATURE [Part::MultiFuse] Fusion379
  Refine = true
  Shapes = -> [Cylinder583,Part__Mirroring076]
FEATURE [Part::Cylinder] Cylinder584
  Angle = 360
  AttacherType = Attacher::AttachEngine3D
  Height = 8
  Placement = pos=(12,0,16) rot=(0,1,0;1.01229rad)
  Radius = 2.5
FEATURE [Part::Cylinder] Cylinder585
  Angle = 360
  AttacherType = Attacher::AttachEngine3D
  Height = 8
  Placement = pos=(12,0,16) rot=(0,1,0;1.01229rad)
  Radius = 2.5
FEATURE [Part::Mirroring] Part__Mirroring077  label="Cylinder107 (Mirror #1)040"
  Base = (0,0,0)
  Normal = (1,0,0)
  Source = -> Cylinder585
FEATURE [Part::MultiFuse] Fusion380
  Placement = pos=(0,0,0) rot=(0,0,1;0.628319rad)
  Refine = true
  Shapes = -> [Cylinder584,Part__Mirroring077]
FEATURE [Part::Cylinder] Cylinder586
  Angle = 360
  AttacherType = Attacher::AttachEngine3D
  Height = 8
  Placement = pos=(12,0,16) rot=(0,1,0;1.01229rad)
  Radius = 2.5
FEATURE [Part::Cylinder] Cylinder587
  Angle = 360
  AttacherType = Attacher::AttachEngine3D
  Height = 8
  Placement = pos=(12,0,16) rot=(0,1,0;1.01229rad)
  Radius = 2.5
FEATURE [Part::Mirroring] Part__Mirroring078  label="Cylinder107 (Mirror #1)041"
  Base = (0,0,0)
  Normal = (1,0,0)
  Source = -> Cylinder587
FEATURE [Part::MultiFuse] Fusion381
  Placement = pos=(0,0,0) rot=(0,0,1;1.25664rad)
  Refine = true
  Shapes = -> [Cylinder586,Part__Mirroring078]
FEATURE [Part::Cylinder] Cylinder588
  Angle = 360
  AttacherType = Attacher::AttachEngine3D
  Height = 8
  Placement = pos=(12,0,16) rot=(0,1,0;1.01229rad)
  Radius = 2.5
FEATURE [Part::Cylinder] Cylinder589
  Angle = 360
  AttacherType = Attacher::AttachEngine3D
  Height = 8
  Placement = pos=(12,0,16) rot=(0,1,0;1.01229rad)
  Radius = 2.5
FEATURE [Part::Mirroring] Part__Mirroring079  label="Cylinder107 (Mirror #1)042"
  Base = (0,0,0)
  Normal = (1,0,0)
  Source = -> Cylinder589
FEATURE [Part::MultiFuse] Fusion382
  Placement = pos=(0,0,0) rot=(0,0,1;1.88496rad)
  Refine = true
  Shapes = -> [Cylinder588,Part__Mirroring079]
FEATURE [Part::Cylinder] Cylinder590
  Angle = 360
  AttacherType = Attacher::AttachEngine3D
  Height = 8
  Placement = pos=(12,0,16) rot=(0,1,0;1.01229rad)
  Radius = 2.5
FEATURE [Part::Cylinder] Cylinder591
  Angle = 360
  AttacherType = Attacher::AttachEngine3D
  Height = 8
  Placement = pos=(12,0,16) rot=(0,1,0;1.01229rad)
  Radius = 2.5
FEATURE [Part::Mirroring] Part__Mirroring080  label="Cylinder107 (Mirror #1)043"
  Base = (0,0,0)
  Normal = (1,0,0)
  Source = -> Cylinder591
FEATURE [Part::MultiFuse] Fusion383
  Placement = pos=(0,0,0) rot=(0,0,1;2.51327rad)
  Refine = true
  Shapes = -> [Cylinder590,Part__Mirroring080]
FEATURE [Part::MultiFuse] Fusion384
  Placement = pos=(0,0,-1) rot=(0,0,1;0rad)
  Refine = true
  Shapes = -> [Fusion379,Fusion380,Fusion381,Fusion382,Fusion383]
FEATURE [Part::Cylinder] Cylinder592
  Angle = 360
  AttacherType = Attacher::AttachEngine3D
  Height = 10
  Placement = pos=(12.5,0,13) rot=(0,0,1;0rad)
  Radius = 1.1
FEATURE [Part::Cylinder] Cylinder593
  Angle = 360
  AttacherType = Attacher::AttachEngine3D
  Height = 10
  Placement = pos=(-12.5,0,13) rot=(0,0,1;0rad)
  Radius = 1.1
FEATURE [Part::MultiFuse] Fusion385
  Placement = pos=(0,0,0) rot=(0,0,1;0.314159rad)
  Refine = true
  Shapes = -> [Cylinder592,Cylinder593]
FEATURE [Part::Cylinder] Cylinder594
  Angle = 360
  AttacherType = Attacher::AttachEngine3D
  Height = 10
  Placement = pos=(12.5,0,13) rot=(0,0,1;0rad)
  Radius = 1.1
FEATURE [Part::Cylinder] Cylinder595
  Angle = 360
  AttacherType = Attacher::AttachEngine3D
  Height = 10
  Placement = pos=(-12.5,0,13) rot=(0,0,1;0rad)
  Radius = 1.1
FEATURE [Part::MultiFuse] Fusion386
  Placement = pos=(0,0,0) rot=(0,0,1;0.942478rad)
  Refine = true
  Shapes = -> [Cylinder594,Cylinder595]
FEATURE [Part::Cylinder] Cylinder596
  Angle = 360
  AttacherType = Attacher::AttachEngine3D
  Height = 10
  Placement = pos=(12.5,0,13) rot=(0,0,1;0rad)
  Radius = 1.1
FEATURE [Part::Cylinder] Cylinder597
  Angle = 360
  AttacherType = Attacher::AttachEngine3D
  Height = 10
  Placement = pos=(-12.5,0,13) rot=(0,0,1;0rad)
  Radius = 1.1
FEATURE [Part::MultiFuse] Fusion387
  Placement = pos=(0,0,0) rot=(0,0,1;1.5708rad)
  Refine = true
  Shapes = -> [Cylinder596,Cylinder597]
FEATURE [Part::Cylinder] Cylinder598
  Angle = 360
  AttacherType = Attacher::AttachEngine3D
  Height = 10
  Placement = pos=(12.5,0,13) rot=(0,0,1;0rad)
  Radius = 1.1
FEATURE [Part::Cylinder] Cylinder599
  Angle = 360
  AttacherType = Attacher::AttachEngine3D
  Height = 10
  Placement = pos=(-12.5,0,13) rot=(0,0,1;0rad)
  Radius = 1.1
FEATURE [Part::MultiFuse] Fusion388
  Placement = pos=(0,0,0) rot=(0,0,1;2.19911rad)
  Refine = true
  Shapes = -> [Cylinder598,Cylinder599]
FEATURE [Part::Cylinder] Cylinder600
  Angle = 360
  AttacherType = Attacher::AttachEngine3D
  Height = 10
  Placement = pos=(12.5,0,13) rot=(0,0,1;0rad)
  Radius = 1.1
FEATURE [Part::Cylinder] Cylinder601
  Angle = 360
  AttacherType = Attacher::AttachEngine3D
  Height = 10
  Placement = pos=(-12.5,0,13) rot=(0,0,1;0rad)
  Radius = 1.1
FEATURE [Part::MultiFuse] Fusion389
  Placement = pos=(0,0,0) rot=(0,0,1;2.82743rad)
  Refine = true
  Shapes = -> [Cylinder600,Cylinder601]
FEATURE [Part::MultiFuse] Fusion390
  Refine = true
  Shapes = -> [Fusion385,Fusion386,Fusion389,Fusion388,Fusion387]
FEATURE [Part::Cone] Cone017
  Angle = 360
  AttacherType = Attacher::AttachEngine3D
  Height = 10
  Placement = pos=(0,0,9) rot=(0,0,1;0rad)
  Radius1 = 24
  Radius2 = 15
FEATURE [Part::Cut] Cut523  label="Cut835"
  Base = -> Cone016
  Refine = true
  Tool = -> Cylinder581
FEATURE [Part::Cut] Cut524  label="Cut836"
  Base = -> Cut523
  Refine = true
  Tool = -> Cone017
FEATURE [Part::MultiFuse] Fusion391
  Refine = true
  Shapes = -> [Fillet302,Cut524]
FEATURE [Part::Cut] Cut525  label="Cut837"
  Base = -> Fusion391
  Refine = true
  Tool = -> Cylinder580
FEATURE [Part::Chamfer] Chamfer072
  Base = -> Cut525
  Edges = 1 edges r=1.49: [Edge39]
FEATURE [Part::Chamfer] Chamfer073
  Base = -> Chamfer072
  Edges = 1 edges r=2: [Edge10]
FEATURE [Part::Cut] Cut526  label="Cut838"
  Base = -> Chamfer073
  Refine = true
  Tool = -> Fusion384
FEATURE [Part::Cut] Cut527  label="Cut839"
  Base = -> Cut526
  Refine = true
  Tool = -> Fusion390
FEATURE [Part::Fillet] Fillet303
  Base = -> Cut527
  Edges = 1 edges r=1.5: [Edge121]
FEATURE [Part::Fillet] Fillet304  label="rim-left-front003"
  Base = -> Fillet303
  Edges = 1 edges r=1.5: [Edge161]
  Placement = pos=(98,17,-52) rot=(1,0,0;1.5708rad)
FEATURE [Part::Mirroring] Part__Mirroring081  label="rim-right-middle"
  Base = (0,0,0)
  Normal = (0,1,0)
  Placement = pos=(250,170,1) rot=(0,0,1;0rad)
  Source = -> Fillet304
FEATURE [Part::Cut] Cut528  label="hub-front"
  Refine = true
  Tool = -> Fusion019
FEATURE [Part::Fillet] Fillet305  label="hub-bolts-cover-left-front"
  Edges = 1 edges r=0.49: [Edge1]
  Placement = pos=(98,16,-51) rot=(1,0,0;1.5708rad)
FEATURE [Part::MultiFuse] Fusion392  label="hub-cap-front"
  Placement = pos=(0,0,-9) rot=(0,0,1;0rad)
  Refine = true
  Shapes = -> [Fusion033]
FEATURE [Part::Cut] Cut529  label="hub-middle"
  Refine = true
FEATURE [Part::Cut] Cut530  label="hub-cap-middle"
  Refine = true
  Tool = -> Cylinder063
FEATURE [Part::Fillet] Fillet306  label="hub-bolts-cover-left-middle"
  Edges = 1 edges r=0.49: [Edge1]
  Placement = pos=(348,17,-51) rot=(1,0,0;1.5708rad)
FEATURE [Part::MultiFuse] Fusion397  label="hub-left-rear"
  Placement = pos=(453,39,-51) rot=(1,0,0;1.5708rad)
  Refine = true
  Shapes = -> [Cut459,Fusion289]
FEATURE [Part::MultiFuse] Fusion398  label="rim-left-rear"
  Placement = pos=(453,39,-51) rot=(1,0,0;1.5708rad)
  Refine = true
  Shapes = -> [Fillet279,Part__Mirroring047]
FEATURE [Part::MultiFuse] Fusion399
  Placement = pos=(448,39,-52) rot=(1,0,0;1.5708rad)
  Refine = true
  Shapes = -> [Cut459,Fusion289]
FEATURE [Part::MultiFuse] Fusion400
  Placement = pos=(448,39,-52) rot=(1,0,0;1.5708rad)
  Refine = true
  Shapes = -> [Fillet279,Part__Mirroring047]
FEATURE [Part::Mirroring] Part__Mirroring084  label="hub-right-rear"
  Base = (448,-1.14441e-05,-50.0744)
  Normal = (0,1,-4.76837e-07)
  Placement = pos=(5,170,1) rot=(0,0,1;0rad)
  Source = -> Fusion399
FEATURE [Part::Mirroring] Part__Mirroring085  label="rim-right-rear"
  Base = (0,0,0)
  Normal = (0,1,0)
  Placement = pos=(5,170,1) rot=(0,0,1;0rad)
  Source = -> Fusion400
FEATURE [Part::MultiFuse] Fusion401  label="hub-left-front"
  Placement = pos=(98,16,-51) rot=(1,0,0;1.5708rad)
  Refine = true
  Shapes = -> [Fusion392,Cut528]
FEATURE [Part::MultiFuse] Fusion402
  Placement = pos=(98,17,-51) rot=(1,0,0;1.5708rad)
  Refine = true
  Shapes = -> [Fusion392,Cut528]
FEATURE [Part::Fillet] Fillet307  label="hub-bolts-cover-front001"
  Edges = 1 edges r=0.49: [Edge1]
  Placement = pos=(98,17,-51) rot=(1,0,0;1.5708rad)
FEATURE [Part::Mirroring] Part__Mirroring086  label="hub-right-front"
  Base = (0,0,0)
  Normal = (0,1,0)
  Placement = pos=(0,171,0) rot=(0,0,1;0rad)
  Source = -> Fusion402
FEATURE [Part::Mirroring] Part__Mirroring087  label="hub-bolts-cover-right-front"
  Base = (0,0,0)
  Normal = (0,1,0)
  Placement = pos=(0,171,0) rot=(0,0,1;0rad)
  Source = -> Fillet307
FEATURE [Part::MultiFuse] Fusion403  label="hub-left-center"
  Placement = pos=(348,17,-51) rot=(1,0,0;1.5708rad)
  Refine = true
  Shapes = -> [Cut529,Cut530]
FEATURE [Part::Fillet] Fillet308  label="hub-bolts-cover-middle001"
  Edges = 1 edges r=0.49: [Edge1]
  Placement = pos=(348,17,-51) rot=(1,0,0;1.5708rad)
FEATURE [Part::MultiFuse] Fusion404
  Placement = pos=(348,17,-51) rot=(1,0,0;1.5708rad)
  Refine = true
  Shapes = -> [Cut529,Cut530]
FEATURE [Part::Mirroring] Part__Mirroring088  label="hub-bolts-cover-right-middle"
  Base = (0,0,0)
  Normal = (0,1,0)
  Placement = pos=(0,170,0) rot=(0,0,1;0rad)
  Source = -> Fillet308
FEATURE [Part::Mirroring] Part__Mirroring089  label="hub-right-centre"
  Base = (0,0,0)
  Normal = (0,1,0)
  Placement = pos=(0,170,0) rot=(0,0,1;0rad)
  Source = -> Fusion404
FEATURE [App::DocumentObjectGroup] Group001  label="wheels"
  Group = -> [Chamfer055,Chamfer057,Fillet295,Part__Mirroring070,Fusion397,Fusion398,Part__Mirroring084,Part__Mirroring085,Fillet305,Fusion401,Part__Mirroring086,Part__Mirroring087,Fusion403,Chamfer056,Fillet301,Fillet306,Part__Mirroring089,Part__Mirroring081,Part__Mirroring088]
FEATURE [Part::Box] Box423  label="Cube647"
  AttacherType = Attacher::AttachEngine3D
  Height = 17
  Length = 10
  Placement = pos=(-2,0,1.5) rot=(0,0,1;0rad)
  Width = 60
FEATURE [Part::Fillet] Fillet309
  Base = -> Box423
  Edges = 4 edges r=3: [Edge9,Edge10,Edge11,Edge12]
  Placement = pos=(485.5,55,-23) rot=(0,0,1;0rad)
FEATURE [Part::Box] Box424  label="Cube648"
  AttacherType = Attacher::AttachEngine3D
  Height = 10
  Length = 10
  Placement = pos=(483.5,63,-7.5) rot=(0,0,1;0rad)
  Width = 44
FEATURE [Part::Cut] Cut531  label="Cut840"
  Base = -> Fillet309
  Refine = true
  Tool = -> Box424
FEATURE [Part::Cylinder] Cylinder602
  Angle = 360
  AttacherType = Attacher::AttachEngine3D
  Height = 10
  Placement = pos=(3,60,10) rot=(1,0,0;1.5708rad)
  Radius = 1.2
FEATURE [Part::Cylinder] Cylinder603
  Angle = 360
  AttacherType = Attacher::AttachEngine3D
  Height = 10
  Placement = pos=(3,10,10) rot=(1,0,0;1.5708rad)
  Radius = 1.2
FEATURE [Part::MultiFuse] Fusion407
  Placement = pos=(485.5,55,-23) rot=(0,0,1;0rad)
  Refine = true
  Shapes = -> [Cylinder602,Cylinder603]
FEATURE [Part::Chamfer] Chamfer074
  Base = -> Cut531
  Edges = 2 edges r=2.99: [Edge18,Edge25]
FEATURE [Part::Cut] Cut533  label="Cut841"
  Base = -> Chamfer074
  Refine = true
  Tool = -> Fusion407
FEATURE [Part::Cylinder] Cylinder604
  Angle = 360
  AttacherType = Attacher::AttachEngine3D
  Height = 10
  Placement = pos=(483.5,85,-14.5) rot=(0,1,0;1.5708rad)
  Radius = 2.6
FEATURE [Part::Cylinder] Cylinder605
  Angle = 360
  AttacherType = Attacher::AttachEngine3D
  Height = 10
  Placement = pos=(483.5,79,-10.5) rot=(0,1,0;1.5708rad)
  Radius = 1.2
FEATURE [Part::Cylinder] Cylinder606
  Angle = 360
  AttacherType = Attacher::AttachEngine3D
  Height = 10
  Placement = pos=(483.5,91,-10.5) rot=(0,1,0;1.5708rad)
  Radius = 1.2
FEATURE [Part::Cylinder] Cylinder607
  Angle = 360
  AttacherType = Attacher::AttachEngine3D
  Height = 10
  Placement = pos=(483.5,79,-18.5) rot=(0,1,0;1.5708rad)
  Radius = 1.2
FEATURE [Part::Cylinder] Cylinder608
  Angle = 360
  AttacherType = Attacher::AttachEngine3D
  Height = 10
  Placement = pos=(483.5,91,-18.5) rot=(0,1,0;1.5708rad)
  Radius = 1.2
FEATURE [Part::MultiFuse] Fusion408
  Refine = true
  Shapes = -> [Cylinder604,Cylinder608,Cylinder605,Cylinder606,Cylinder607]
FEATURE [Part::Cut] Cut534  label="cross-member-rear-SINGLE"
  Base = -> Cut533
  Placement = pos=(5,0,5) rot=(0,0,1;0rad)
  Refine = true
  Tool = -> Fusion408
FEATURE [Part::Cylinder] Cylinder640  label="Cylinder722"
  Angle = 360
  AttacherType = Attacher::AttachEngine3D
  Height = 7
  Placement = pos=(60,105,0) rot=(0,0,1;4.18879rad)
  Radius = 105
FEATURE [Part::Cylinder] Cylinder641  label="Cylinder723"
  Angle = 360
  AttacherType = Attacher::AttachEngine3D
  Height = 7
  Placement = pos=(60,105,0) rot=(0,0,1;4.10152rad)
  Radius = 103
FEATURE [Part::Cut] Cut109  label="leafspring-rear-left"
  Base = -> Cylinder640
  Placement = pos=(440,4,-64) rot=(1,0,0;1.5708rad)
  Refine = true
  Tool = -> Cylinder641
FEATURE [Part::Cylinder] Cylinder642  label="Cylinder724"
  Angle = 360
  AttacherType = Attacher::AttachEngine3D
  Height = 7
  Placement = pos=(60,105,0) rot=(0,0,1;4.18879rad)
  Radius = 105
FEATURE [Part::Cylinder] Cylinder643  label="Cylinder642"
  Angle = 360
  AttacherType = Attacher::AttachEngine3D
  Height = 7
  Placement = pos=(60,105,0) rot=(0,0,1;4.10152rad)
  Radius = 103
FEATURE [Part::Cut] Cut110  label="leafspring-rear-right"
  Base = -> Cylinder642
  Placement = pos=(440,83,-64) rot=(1,0,0;1.5708rad)
  Refine = true
  Tool = -> Cylinder643
FEATURE [Part::MultiFuse] Fusion091  label="leafsprings-front"
  Placement = pos=(-402,45,23) rot=(0,0,1;0rad)
  Refine = true
  Shapes = -> [Cut109,Cut110]
FEATURE [Part::Cylinder] Cylinder644  label="Cylinder703"
  Angle = 360
  AttacherType = Attacher::AttachEngine3D
  Height = 7
  Placement = pos=(60,105,0) rot=(0,0,1;4.10152rad)
  Radius = 103
FEATURE [Part::Cylinder] Cylinder645  label="Cylinder704"
  Angle = 360
  AttacherType = Attacher::AttachEngine3D
  Height = 7
  Placement = pos=(60,105,0) rot=(0,0,1;4.10152rad)
  Radius = 103
FEATURE [Part::Cylinder] Cylinder646  label="Cylinder705"
  Angle = 360
  AttacherType = Attacher::AttachEngine3D
  Height = 7
  Placement = pos=(60,105,0) rot=(0,0,1;4.18879rad)
  Radius = 105
FEATURE [Part::Cut] Cut551  label="leafspring-rear-left001"
  Base = -> Cylinder646
  Placement = pos=(440,4,-64) rot=(1,0,0;1.5708rad)
  Refine = true
  Tool = -> Cylinder645
FEATURE [Part::Cylinder] Cylinder647  label="Cylinder725"
  Angle = 360
  AttacherType = Attacher::AttachEngine3D
  Height = 7
  Placement = pos=(60,105,0) rot=(0,0,1;4.18879rad)
  Radius = 105
FEATURE [Part::Cut] Cut550  label="leafspring-rear-right001"
  Base = -> Cylinder647
  Placement = pos=(440,83,-64) rot=(1,0,0;1.5708rad)
  Refine = true
  Tool = -> Cylinder644
FEATURE [Part::MultiFuse] Fusion432  label="leafsprings-rear"
  Placement = pos=(-47,45,23) rot=(0,0,1;0rad)
  Refine = true
  Shapes = -> [Cut551,Cut550]
FEATURE [Part::Cylinder] Cylinder654  label="Cylinder731"
  Angle = 360
  AttacherType = Attacher::AttachEngine3D
  Height = 10
  Placement = pos=(0,0,12.7) rot=(1,0,0;1.5708rad)
  Radius = 2
FEATURE [Part::Cylinder] Cylinder655  label="Cylinder732"
  Angle = 360
  AttacherType = Attacher::AttachEngine3D
  Height = 10
  Placement = pos=(0,0,0) rot=(1,0,0;1.5708rad)
  Radius = 2
FEATURE [Part::Box] Box439  label="Cube658"
  AttacherType = Attacher::AttachEngine3D
  Height = 20
  Length = 8
  Placement = pos=(-4,-1,-3.5) rot=(0,0,1;0rad)
  Width = 1
FEATURE [Part::Fillet] Fillet320
  Base = -> Box439
  Edges = 4 edges r=2.99: [Edge2,Edge4,Edge6,Edge8]
FEATURE [Part::MultiFuse] Fusion437
  Refine = true
  Shapes = -> [Cylinder654,Cylinder655]
FEATURE [Part::Cut] Cut559  label="Cut850"
  Base = -> Fillet320
  Placement = pos=(150,42,-27) rot=(0,-1,0;0.174533rad)
  Refine = true
  Tool = -> Fusion437
FEATURE [Part::Cylinder] Cylinder656  label="Cylinder733"
  Angle = 360
  AttacherType = Attacher::AttachEngine3D
  Height = 10
  Placement = pos=(0,0,12.7) rot=(1,0,0;1.5708rad)
  Radius = 2
FEATURE [Part::Cylinder] Cylinder657  label="Cylinder734"
  Angle = 360
  AttacherType = Attacher::AttachEngine3D
  Height = 10
  Placement = pos=(0,0,0) rot=(1,0,0;1.5708rad)
  Radius = 2
FEATURE [Part::MultiFuse] Fusion438
  Refine = true
  Shapes = -> [Cylinder656,Cylinder657]
FEATURE [Part::Box] Box440  label="Cube659"
  AttacherType = Attacher::AttachEngine3D
  Height = 20
  Length = 8
  Placement = pos=(-4,-1,-3.5) rot=(0,0,1;0rad)
  Width = 1
FEATURE [Part::Fillet] Fillet321
  Base = -> Box440
  Edges = 4 edges r=2.99: [Edge2,Edge4,Edge6,Edge8]
FEATURE [Part::Cut] Cut560  label="Cut851"
  Base = -> Fillet321
  Placement = pos=(150,50,-27) rot=(0,-1,0;0.174533rad)
  Refine = true
  Tool = -> Fusion438
FEATURE [Part::MultiFuse] Fusion439  label="leafspring-bisquits-front-left"
  Placement = pos=(0.5,0,4) rot=(0,0,1;0rad)
  Refine = true
  Shapes = -> [Cut559,Cut560]
FEATURE [Part::Cylinder] Cylinder658  label="Cylinder797"
  Angle = 360
  AttacherType = Attacher::AttachEngine3D
  Height = 10
  Placement = pos=(0,0,12.7) rot=(1,0,0;1.5708rad)
  Radius = 2
FEATURE [Part::Cylinder] Cylinder659  label="Cylinder712"
  Angle = 360
  AttacherType = Attacher::AttachEngine3D
  Height = 10
  Placement = pos=(0,0,0) rot=(1,0,0;1.5708rad)
  Radius = 2
FEATURE [Part::Box] Box441  label="Cube660"
  AttacherType = Attacher::AttachEngine3D
  Height = 20
  Length = 8
  Placement = pos=(-4,-1,-3.5) rot=(0,0,1;0rad)
  Width = 1
FEATURE [Part::Fillet] Fillet322
  Base = -> Box441
  Edges = 4 edges r=2.99: [Edge2,Edge4,Edge6,Edge8]
FEATURE [Part::MultiFuse] Fusion441
  Refine = true
  Shapes = -> [Cylinder658,Cylinder659]
FEATURE [Part::Cut] Cut561  label="Cut852"
  Base = -> Fillet322
  Placement = pos=(150,42,-27) rot=(0,-1,0;0.174533rad)
  Refine = true
  Tool = -> Fusion441
FEATURE [Part::Cylinder] Cylinder660  label="Cylinder1138"
  Angle = 360
  AttacherType = Attacher::AttachEngine3D
  Height = 10
  Placement = pos=(0,0,12.7) rot=(1,0,0;1.5708rad)
  Radius = 2
FEATURE [Part::Cylinder] Cylinder661  label="Cylinder799"
  Angle = 360
  AttacherType = Attacher::AttachEngine3D
  Height = 10
  Placement = pos=(0,0,0) rot=(1,0,0;1.5708rad)
  Radius = 2
FEATURE [Part::MultiFuse] Fusion442
  Refine = true
  Shapes = -> [Cylinder660,Cylinder661]
FEATURE [Part::Box] Box442  label="Cube661"
  AttacherType = Attacher::AttachEngine3D
  Height = 20
  Length = 8
  Placement = pos=(-4,-1,-3.5) rot=(0,0,1;0rad)
  Width = 1
FEATURE [Part::Fillet] Fillet323
  Base = -> Box442
  Edges = 4 edges r=2.99: [Edge2,Edge4,Edge6,Edge8]
FEATURE [Part::Cut] Cut562  label="Cut853"
  Base = -> Fillet323
  Placement = pos=(150,50,-27) rot=(0,-1,0;0.174533rad)
  Refine = true
  Tool = -> Fusion442
FEATURE [Part::MultiFuse] Fusion440  label="leafspring-bisquits-front-right"
  Placement = pos=(0.5,79,4) rot=(0,0,1;0rad)
  Refine = true
  Shapes = -> [Cut561,Cut562]
FEATURE [Part::Cylinder] Cylinder662  label="Cylinder800"
  Angle = 360
  AttacherType = Attacher::AttachEngine3D
  Height = 10
  Placement = pos=(0,0,12.7) rot=(1,0,0;1.5708rad)
  Radius = 2
FEATURE [Part::Cylinder] Cylinder663  label="Cylinder1139"
  Angle = 360
  AttacherType = Attacher::AttachEngine3D
  Height = 10
  Placement = pos=(0,0,0) rot=(1,0,0;1.5708rad)
  Radius = 2
FEATURE [Part::Box] Box443  label="Cube662"
  AttacherType = Attacher::AttachEngine3D
  Height = 20
  Length = 8
  Placement = pos=(-4,-1,-3.5) rot=(0,0,1;0rad)
  Width = 1
FEATURE [Part::Fillet] Fillet324
  Base = -> Box443
  Edges = 4 edges r=2.99: [Edge2,Edge4,Edge6,Edge8]
FEATURE [Part::MultiFuse] Fusion444
  Refine = true
  Shapes = -> [Cylinder662,Cylinder663]
FEATURE [Part::Cut] Cut563  label="Cut854"
  Base = -> Fillet324
  Placement = pos=(150,42,-27) rot=(0,-1,0;0.174533rad)
  Refine = true
  Tool = -> Fusion444
FEATURE [Part::Cylinder] Cylinder664  label="Cylinder1140"
  Angle = 360
  AttacherType = Attacher::AttachEngine3D
  Height = 10
  Placement = pos=(0,0,12.7) rot=(1,0,0;1.5708rad)
  Radius = 2
FEATURE [Part::Cylinder] Cylinder665  label="Cylinder803"
  Angle = 360
  AttacherType = Attacher::AttachEngine3D
  Height = 10
  Placement = pos=(0,0,0) rot=(1,0,0;1.5708rad)
  Radius = 2
FEATURE [Part::MultiFuse] Fusion445
  Refine = true
  Shapes = -> [Cylinder664,Cylinder665]
FEATURE [Part::Box] Box444  label="Cube663"
  AttacherType = Attacher::AttachEngine3D
  Height = 20
  Length = 8
  Placement = pos=(-4,-1,-3.5) rot=(0,0,1;0rad)
  Width = 1
FEATURE [Part::Fillet] Fillet325
  Base = -> Box444
  Edges = 4 edges r=2.99: [Edge2,Edge4,Edge6,Edge8]
FEATURE [Part::Cut] Cut564  label="Cut855"
  Base = -> Fillet325
  Placement = pos=(150,50,-27) rot=(0,-1,0;0.174533rad)
  Refine = true
  Tool = -> Fusion445
FEATURE [Part::MultiFuse] Fusion443  label="leafspring-bisquits-rear-left"
  Placement = pos=(355.5,0,4) rot=(0,0,1;0rad)
  Refine = true
  Shapes = -> [Cut563,Cut564]
FEATURE [Part::Cylinder] Cylinder666  label="Cylinder742"
  Angle = 360
  AttacherType = Attacher::AttachEngine3D
  Height = 10
  Placement = pos=(0,0,12.7) rot=(1,0,0;1.5708rad)
  Radius = 2
FEATURE [Part::Cylinder] Cylinder667  label="Cylinder743"
  Angle = 360
  AttacherType = Attacher::AttachEngine3D
  Height = 10
  Placement = pos=(0,0,0) rot=(1,0,0;1.5708rad)
  Radius = 2
FEATURE [Part::Box] Box445  label="Cube664"
  AttacherType = Attacher::AttachEngine3D
  Height = 20
  Length = 8
  Placement = pos=(-4,-1,-3.5) rot=(0,0,1;0rad)
  Width = 1
FEATURE [Part::Fillet] Fillet326
  Base = -> Box445
  Edges = 4 edges r=2.99: [Edge2,Edge4,Edge6,Edge8]
FEATURE [Part::MultiFuse] Fusion447
  Refine = true
  Shapes = -> [Cylinder666,Cylinder667]
FEATURE [Part::Cut] Cut565  label="Cut856"
  Base = -> Fillet326
  Placement = pos=(150,42,-27) rot=(0,-1,0;0.174533rad)
  Refine = true
  Tool = -> Fusion447
FEATURE [Part::Cylinder] Cylinder668  label="Cylinder744"
  Angle = 360
  AttacherType = Attacher::AttachEngine3D
  Height = 10
  Placement = pos=(0,0,12.7) rot=(1,0,0;1.5708rad)
  Radius = 2
FEATURE [Part::Cylinder] Cylinder669  label="Cylinder804"
  Angle = 360
  AttacherType = Attacher::AttachEngine3D
  Height = 10
  Placement = pos=(0,0,0) rot=(1,0,0;1.5708rad)
  Radius = 2
FEATURE [Part::MultiFuse] Fusion448
  Refine = true
  Shapes = -> [Cylinder668,Cylinder669]
FEATURE [Part::Box] Box446  label="Cube665"
  AttacherType = Attacher::AttachEngine3D
  Height = 20
  Length = 8
  Placement = pos=(-4,-1,-3.5) rot=(0,0,1;0rad)
  Width = 1
FEATURE [Part::Fillet] Fillet327
  Base = -> Box446
  Edges = 4 edges r=2.99: [Edge2,Edge4,Edge6,Edge8]
FEATURE [Part::Cut] Cut566  label="Cut857"
  Base = -> Fillet327
  Placement = pos=(150,50,-27) rot=(0,-1,0;0.174533rad)
  Refine = true
  Tool = -> Fusion448
FEATURE [Part::MultiFuse] Fusion446  label="leafspring-bisquits-rear-right"
  Placement = pos=(355.5,79,4) rot=(0,0,1;0rad)
  Refine = true
  Shapes = -> [Cut565,Cut566]
FEATURE [Part::Cylinder] Cylinder671  label="Cylinder1141"
  Angle = 360
  AttacherType = Attacher::AttachEngine3D
  Height = 15
  Placement = pos=(395.5,54,-28) rot=(1,0,0;1.5708rad)
  Radius = 2.1
FEATURE [Part::Box] Box447  label="Cube666"
  AttacherType = Attacher::AttachEngine3D
  Height = 12
  Length = 12
  Placement = pos=(389.5,39.75,-32) rot=(0,0,1;0rad)
  Width = 13.75
FEATURE [Part::Box] Box448  label="Cube667"
  AttacherType = Attacher::AttachEngine3D
  Height = 8
  Length = 12
  Placement = pos=(389.5,41.75,-32) rot=(0,0,1;0rad)
  Width = 7.5
FEATURE [Part::Cut] Cut567  label="Cut858"
  Base = -> Box447
  Refine = true
  Tool = -> Box448
FEATURE [Part::Box] Box449  label="Cube668"
  AttacherType = Attacher::AttachEngine3D
  Height = 10
  Length = 16
  Placement = pos=(387.5,49.75,-20) rot=(0,0,1;0rad)
  Width = 3.75
FEATURE [Part::Cylinder] Cylinder672  label="Cylinder1142"
  Angle = 360
  AttacherType = Attacher::AttachEngine3D
  Height = 15
  Placement = pos=(391.5,54,-15) rot=(1,0,0;1.5708rad)
  Radius = 1.6
FEATURE [Part::Cylinder] Cylinder673  label="Cylinder1143"
  Angle = 360
  AttacherType = Attacher::AttachEngine3D
  Height = 15
  Placement = pos=(399.5,54,-15) rot=(1,0,0;1.5708rad)
  Radius = 1.6
FEATURE [Part::MultiFuse] Fusion449
  Refine = true
  Shapes = -> [Box449,Cut567]
FEATURE [Part::Fillet] Fillet328
  Base = -> Fusion449
  Edges = 3 edges r=3: [Edge6,Edge7,Edge16]
FEATURE [Part::Fillet] Fillet329
  Base = -> Fillet328
  Edges = 4 edges r=4: [Edge29,Edge32,Edge40,Edge43]
FEATURE [Part::Chamfer] Chamfer079
  Base = -> Fillet329
  Edges = 2 edges r=1.99: [Edge21,Edge44]
FEATURE [Part::Cylinder] Cylinder674  label="Cylinder1144"
  Angle = 360
  AttacherType = Attacher::AttachEngine3D
  Height = 2
  Placement = pos=(391.5,49.75,-15) rot=(1,0,0;1.5708rad)
  Radius = 3.1
FEATURE [Part::Cylinder] Cylinder675  label="Cylinder1145"
  Angle = 360
  AttacherType = Attacher::AttachEngine3D
  Height = 2
  Placement = pos=(399.5,49.75,-15) rot=(1,0,0;1.5708rad)
  Radius = 3.1
FEATURE [Part::MultiFuse] Fusion450
  Refine = true
  Shapes = -> [Cylinder674,Cylinder675,Cylinder671,Cylinder673,Cylinder672]
FEATURE [Part::Cut] Cut568  label="leafspring-mount-rear-left"
  Base = -> Chamfer079
  Placement = pos=(5,0,5) rot=(0,0,1;0rad)
  Refine = true
  Tool = -> Fusion450
FEATURE [Part::Box] Box450  label="Cube669"
  AttacherType = Attacher::AttachEngine3D
  Height = 12
  Length = 12
  Placement = pos=(389.5,39.75,-32) rot=(0,0,1;0rad)
  Width = 13.75
FEATURE [Part::Box] Box451  label="Cube670"
  AttacherType = Attacher::AttachEngine3D
  Height = 8
  Length = 12
  Placement = pos=(389.5,41.75,-32) rot=(0,0,1;0rad)
  Width = 7.5
FEATURE [Part::Cylinder] Cylinder676  label="Cylinder1379"
  Angle = 360
  AttacherType = Attacher::AttachEngine3D
  Height = 2
  Placement = pos=(399.5,49.75,-15) rot=(1,0,0;1.5708rad)
  Radius = 3.1
FEATURE [Part::Cylinder] Cylinder677  label="Cylinder1380"
  Angle = 360
  AttacherType = Attacher::AttachEngine3D
  Height = 2
  Placement = pos=(391.5,49.75,-15) rot=(1,0,0;1.5708rad)
  Radius = 3.1
FEATURE [Part::Cut] Cut570  label="Cut859"
  Base = -> Box450
  Refine = true
  Tool = -> Box451
FEATURE [Part::Cylinder] Cylinder678  label="Cylinder1381"
  Angle = 360
  AttacherType = Attacher::AttachEngine3D
  Height = 15
  Placement = pos=(395.5,54,-28) rot=(1,0,0;1.5708rad)
  Radius = 2.1
FEATURE [Part::Box] Box452  label="Cube671"
  AttacherType = Attacher::AttachEngine3D
  Height = 10
  Length = 16
  Placement = pos=(387.5,49.75,-20) rot=(0,0,1;0rad)
  Width = 3.75
FEATURE [Part::MultiFuse] Fusion451
  Refine = true
  Shapes = -> [Box452,Cut570]
FEATURE [Part::Cylinder] Cylinder679  label="Cylinder1299"
  Angle = 360
  AttacherType = Attacher::AttachEngine3D
  Height = 15
  Placement = pos=(399.5,54,-15) rot=(1,0,0;1.5708rad)
  Radius = 1.6
FEATURE [Part::Fillet] Fillet331
  Base = -> Fusion451
  Edges = 3 edges r=3: [Edge6,Edge7,Edge16]
FEATURE [Part::Fillet] Fillet330
  Base = -> Fillet331
  Edges = 4 edges r=4: [Edge29,Edge32,Edge40,Edge43]
FEATURE [Part::Chamfer] Chamfer080
  Base = -> Fillet330
  Edges = 2 edges r=1.99: [Edge21,Edge44]
FEATURE [Part::Cylinder] Cylinder680  label="Cylinder1300"
  Angle = 360
  AttacherType = Attacher::AttachEngine3D
  Height = 15
  Placement = pos=(391.5,54,-15) rot=(1,0,0;1.5708rad)
  Radius = 1.6
FEATURE [Part::MultiFuse] Fusion452
  Refine = true
  Shapes = -> [Cylinder677,Cylinder676,Cylinder678,Cylinder679,Cylinder680]
FEATURE [Part::Cut] Cut569  label="leafspring-mount-rear-right001"
  Base = -> Chamfer080
  Refine = true
  Tool = -> Fusion452
FEATURE [Part::Mirroring] Part__Mirroring092  label="leafspring-mount-rear-right"
  Base = (0,0,0)
  Normal = (0,1,0)
  Placement = pos=(5,170,5) rot=(0,0,1;0rad)
  Source = -> Cut569
FEATURE [Part::Cylinder] Cylinder681  label="Cylinder1301"
  Angle = 360
  AttacherType = Attacher::AttachEngine3D
  Height = 4
  Radius = 4.5
FEATURE [Part::Cylinder] Cylinder001
  Angle = 360
  AttacherType = Attacher::AttachEngine3D
  Height = 4
  Placement = pos=(12,0,0) rot=(0,0,1;0rad)
  Radius = 4.5
FEATURE [Part::Box] Box453
  AttacherType = Attacher::AttachEngine3D
  Height = 1
  Length = 12
  Placement = pos=(0,-4,0) rot=(0,0,1;0rad)
  Width = 8
FEATURE [Part::MultiFuse] Fusion453
  Refine = true
  Shapes = -> [Box453,Cylinder001,Cylinder681]
FEATURE [Part::Box] Box454
  AttacherType = Attacher::AttachEngine3D
  Height = 4
  Length = 12
  Placement = pos=(0,-4,0) rot=(0,0,1;0rad)
  Width = 1
FEATURE [Part::Box] Box455
  AttacherType = Attacher::AttachEngine3D
  Height = 4
  Length = 12
  Placement = pos=(0,3,0) rot=(0,0,1;0rad)
  Width = 1
FEATURE [Part::Box] Box456
  AttacherType = Attacher::AttachEngine3D
  Height = 1
  Length = 12
  Placement = pos=(0,3.5,3) rot=(0,0,1;0rad)
  Width = 0.5
FEATURE [Part::MultiFuse] Fusion001
  Refine = true
  Shapes = -> [Fusion453,Box455,Box454]
FEATURE [Part::Box] Box004
  AttacherType = Attacher::AttachEngine3D
  Height = 1
  Length = 12
  Placement = pos=(0,-4,3) rot=(0,0,1;0rad)
  Width = 0.5
FEATURE [Part::MultiFuse] Fusion002
  Refine = true
  Shapes = -> [Fusion001,Box456,Box004]
FEATURE [Part::Cylinder] Cylinder002
  Angle = 360
  AttacherType = Attacher::AttachEngine3D
  Height = 4
  Radius = 1.5
FEATURE [Part::Box] Box005
  AttacherType = Attacher::AttachEngine3D
  Height = 10
  Length = 10
  Placement = pos=(-5,0,0) rot=(0,0,1;0rad)
  Width = 10
FEATURE [Part::Cut] Cut571  label="Cut860"
  Base = -> Cylinder002
  Placement = pos=(0,-4,0) rot=(0,0,1;0rad)
  Refine = true
  Tool = -> Box005
FEATURE [Part::Cylinder] Cylinder003
  Angle = 360
  AttacherType = Attacher::AttachEngine3D
  Height = 4
  Radius = 1.5
FEATURE [Part::Box] Box006
  AttacherType = Attacher::AttachEngine3D
  Height = 10
  Length = 10
  Placement = pos=(-5,0,0) rot=(0,0,1;0rad)
  Width = 10
FEATURE [Part::Cut] Cut572  label="Cut861"
  Base = -> Cylinder003
  Placement = pos=(12,-4,0) rot=(0,0,1;0rad)
  Refine = true
  Tool = -> Box006
FEATURE [Part::Cylinder] Cylinder682  label="Cylinder1302"
  Angle = 360
  AttacherType = Attacher::AttachEngine3D
  Height = 4
  Radius = 1.5
FEATURE [Part::Box] Box007
  AttacherType = Attacher::AttachEngine3D
  Height = 10
  Length = 10
  Placement = pos=(-5,0,0) rot=(0,0,1;0rad)
  Width = 10
FEATURE [Part::Cut] Cut002
  Base = -> Cylinder682
  Placement = pos=(0,4,0) rot=(0,0,1;3.14159rad)
  Refine = true
  Tool = -> Box007
FEATURE [Part::Cylinder] Cylinder005
  Angle = 360
  AttacherType = Attacher::AttachEngine3D
  Height = 4
  Radius = 1.5
FEATURE [Part::Box] Box008
  AttacherType = Attacher::AttachEngine3D
  Height = 10
  Length = 10
  Placement = pos=(-5,0,0) rot=(0,0,1;0rad)
  Width = 10
FEATURE [Part::Cut] Cut003
  Base = -> Cylinder005
  Placement = pos=(12,4,0) rot=(0,0,1;3.14159rad)
  Refine = true
  Tool = -> Box008
FEATURE [Part::MultiFuse] Fusion003
  Refine = true
  Shapes = -> [Fusion002,Cut003,Cut002,Cut572,Cut571]
FEATURE [Part::Cylinder] Cylinder006
  Angle = 360
  AttacherType = Attacher::AttachEngine3D
  Height = 10
  Radius = 1.6
FEATURE [Part::Cylinder] Cylinder007
  Angle = 360
  AttacherType = Attacher::AttachEngine3D
  Height = 10
  Placement = pos=(12,0,0) rot=(0,0,1;0rad)
  Radius = 1.6
FEATURE [Part::MultiFuse] Fusion004
  Refine = true
  Shapes = -> [Cylinder007,Cylinder006]
FEATURE [Part::Cut] Cut004
  Base = -> Fusion003
  Refine = true
  Tool = -> Fusion004
FEATURE [Part::Cylinder] Cylinder008
  Angle = 360
  AttacherType = Attacher::AttachEngine3D
  Height = 7
  Placement = pos=(6,3.5,153) rot=(1,0,0;1.5708rad)
  Radius = 150
FEATURE [Part::Cut] Cut005
  Base = -> Cut004
  Refine = true
  Tool = -> Cylinder008
FEATURE [Part::Box] Box457
  AttacherType = Attacher::AttachEngine3D
  Height = 3
  Length = 6
  Placement = pos=(3,-3.5,1) rot=(0,0,1;0rad)
  Width = 7
FEATURE [Part::Cut] Cut006
  Base = -> Cut005
  Refine = true
  Tool = -> Box457
FEATURE [Part::Box] Box015
  AttacherType = Attacher::AttachEngine3D
  Height = 1.5
  Length = 26
  Placement = pos=(-6,-6,0) rot=(0,0,1;0rad)
  Width = 13
FEATURE [Part::Cut] Cut012
  Base = -> Cut006
  Placement = pos=(0,0,-1.5) rot=(0,0,1;0rad)
  Refine = true
  Tool = -> Box015
FEATURE [Part::Box] Box016
  AttacherType = Attacher::AttachEngine3D
  Height = 1
  Length = 8
  Placement = pos=(2,-4,0) rot=(0,0,1;0rad)
  Width = 8
FEATURE [Part::MultiFuse] Fusion008  label="leafspring-spacer-front-left"
  Placement = pos=(92,45,-42.5) rot=(0,0,1;0rad)
  Refine = true
  Shapes = -> [Cut012,Box016]
FEATURE [Part::Cylinder] Cylinder683  label="Cylinder1303"
  Angle = 360
  AttacherType = Attacher::AttachEngine3D
  Height = 4
  Radius = 4.5
FEATURE [Part::Cylinder] Cylinder684  label="Cylinder1304"
  Angle = 360
  AttacherType = Attacher::AttachEngine3D
  Height = 4
  Placement = pos=(12,0,0) rot=(0,0,1;0rad)
  Radius = 4.5
FEATURE [Part::Box] Box458
  AttacherType = Attacher::AttachEngine3D
  Height = 1
  Length = 12
  Placement = pos=(0,-4,0) rot=(0,0,1;0rad)
  Width = 8
FEATURE [Part::MultiFuse] Fusion454
  Refine = true
  Shapes = -> [Box458,Cylinder684,Cylinder683]
FEATURE [Part::Box] Box459
  AttacherType = Attacher::AttachEngine3D
  Height = 4
  Length = 12
  Placement = pos=(0,-4,0) rot=(0,0,1;0rad)
  Width = 1
FEATURE [Part::Box] Box460
  AttacherType = Attacher::AttachEngine3D
  Height = 4
  Length = 12
  Placement = pos=(0,3,0) rot=(0,0,1;0rad)
  Width = 1
FEATURE [Part::Box] Box461
  AttacherType = Attacher::AttachEngine3D
  Height = 1
  Length = 12
  Placement = pos=(0,3.5,3) rot=(0,0,1;0rad)
  Width = 0.5
FEATURE [Part::MultiFuse] Fusion455
  Refine = true
  Shapes = -> [Fusion454,Box460,Box459]
FEATURE [Part::Box] Box462
  AttacherType = Attacher::AttachEngine3D
  Height = 1
  Length = 12
  Placement = pos=(0,-4,3) rot=(0,0,1;0rad)
  Width = 0.5
FEATURE [Part::MultiFuse] Fusion456
  Refine = true
  Shapes = -> [Fusion455,Box461,Box462]
FEATURE [Part::Cylinder] Cylinder685  label="Cylinder1382"
  Angle = 360
  AttacherType = Attacher::AttachEngine3D
  Height = 4
  Radius = 1.5
FEATURE [Part::Box] Box463
  AttacherType = Attacher::AttachEngine3D
  Height = 10
  Length = 10
  Placement = pos=(-5,0,0) rot=(0,0,1;0rad)
  Width = 10
FEATURE [Part::Cut] Cut573  label="Cut862"
  Base = -> Cylinder685
  Placement = pos=(0,-4,0) rot=(0,0,1;0rad)
  Refine = true
  Tool = -> Box463
FEATURE [Part::Cylinder] Cylinder686  label="Cylinder1383"
  Angle = 360
  AttacherType = Attacher::AttachEngine3D
  Height = 4
  Radius = 1.5
FEATURE [Part::Box] Box464
  AttacherType = Attacher::AttachEngine3D
  Height = 10
  Length = 10
  Placement = pos=(-5,0,0) rot=(0,0,1;0rad)
  Width = 10
FEATURE [Part::Cut] Cut574  label="Cut863"
  Base = -> Cylinder686
  Placement = pos=(12,-4,0) rot=(0,0,1;0rad)
  Refine = true
  Tool = -> Box464
FEATURE [Part::Cylinder] Cylinder687  label="Cylinder1384"
  Angle = 360
  AttacherType = Attacher::AttachEngine3D
  Height = 4
  Radius = 1.5
FEATURE [Part::Box] Box465
  AttacherType = Attacher::AttachEngine3D
  Height = 10
  Length = 10
  Placement = pos=(-5,0,0) rot=(0,0,1;0rad)
  Width = 10
FEATURE [Part::Cut] Cut575  label="Cut864"
  Base = -> Cylinder687
  Placement = pos=(0,4,0) rot=(0,0,1;3.14159rad)
  Refine = true
  Tool = -> Box465
FEATURE [Part::Cylinder] Cylinder688  label="Cylinder1385"
  Angle = 360
  AttacherType = Attacher::AttachEngine3D
  Height = 4
  Radius = 1.5
FEATURE [Part::Box] Box466
  AttacherType = Attacher::AttachEngine3D
  Height = 10
  Length = 10
  Placement = pos=(-5,0,0) rot=(0,0,1;0rad)
  Width = 10
FEATURE [Part::Cut] Cut576  label="Cut865"
  Base = -> Cylinder688
  Placement = pos=(12,4,0) rot=(0,0,1;3.14159rad)
  Refine = true
  Tool = -> Box466
FEATURE [Part::MultiFuse] Fusion457
  Refine = true
  Shapes = -> [Fusion456,Cut576,Cut575,Cut574,Cut573]
FEATURE [Part::Cylinder] Cylinder689  label="Cylinder1386"
  Angle = 360
  AttacherType = Attacher::AttachEngine3D
  Height = 10
  Radius = 1.6
FEATURE [Part::Cylinder] Cylinder690  label="Cylinder1387"
  Angle = 360
  AttacherType = Attacher::AttachEngine3D
  Height = 10
  Placement = pos=(12,0,0) rot=(0,0,1;0rad)
  Radius = 1.6
FEATURE [Part::MultiFuse] Fusion458
  Refine = true
  Shapes = -> [Cylinder690,Cylinder689]
FEATURE [Part::Cut] Cut577  label="Cut866"
  Base = -> Fusion457
  Refine = true
  Tool = -> Fusion458
FEATURE [Part::Cylinder] Cylinder691  label="Cylinder1388"
  Angle = 360
  AttacherType = Attacher::AttachEngine3D
  Height = 7
  Placement = pos=(6,3.5,153) rot=(1,0,0;1.5708rad)
  Radius = 150
FEATURE [Part::Cut] Cut578  label="Cut867"
  Base = -> Cut577
  Refine = true
  Tool = -> Cylinder691
FEATURE [Part::Box] Box467
  AttacherType = Attacher::AttachEngine3D
  Height = 3
  Length = 6
  Placement = pos=(3,-3.5,1) rot=(0,0,1;0rad)
  Width = 7
FEATURE [Part::Cut] Cut579  label="Cut868"
  Base = -> Cut578
  Refine = true
  Tool = -> Box467
FEATURE [Part::Box] Box468
  AttacherType = Attacher::AttachEngine3D
  Height = 1.5
  Length = 26
  Placement = pos=(-6,-6,0) rot=(0,0,1;0rad)
  Width = 13
FEATURE [Part::Cut] Cut580  label="Cut869"
  Base = -> Cut579
  Placement = pos=(0,0,-1.5) rot=(0,0,1;0rad)
  Refine = true
  Tool = -> Box468
FEATURE [Part::Box] Box469
  AttacherType = Attacher::AttachEngine3D
  Height = 1
  Length = 8
  Placement = pos=(2,-4,0) rot=(0,0,1;0rad)
  Width = 8
FEATURE [Part::MultiFuse] Fusion459  label="leafspring-spacer-front-right"
  Placement = pos=(92,124,-42.5) rot=(0,0,1;0rad)
  Refine = true
  Shapes = -> [Cut580,Box469]
FEATURE [Part::Box] Box021
  AttacherType = Attacher::AttachEngine3D
  Height = 1
  Length = 12
  Placement = pos=(0,-21.75,0) rot=(0,0,1;0rad)
  Width = 7.5
FEATURE [Part::Cylinder] Cylinder016
  Angle = 360
  AttacherType = Attacher::AttachEngine3D
  Height = 1
  Placement = pos=(12,-18,0) rot=(0,0,1;0rad)
  Radius = 4.75
FEATURE [Part::Cylinder] Cylinder017
  Angle = 360
  AttacherType = Attacher::AttachEngine3D
  Height = 1
  Placement = pos=(0,-18,0) rot=(0,0,1;0rad)
  Radius = 4.75
FEATURE [Part::Box] Box022
  AttacherType = Attacher::AttachEngine3D
  Height = 300
  Length = 317
  Placement = pos=(-150,-22,0) rot=(0,0,1;0rad)
  Width = 10
FEATURE [Part::Cylinder] Cylinder018
  Angle = 360
  AttacherType = Attacher::AttachEngine3D
  Height = 7.5
  Placement = pos=(6,-14.25,49.2) rot=(1,0,0;1.5708rad)
  Radius = 50
FEATURE [Part::Cut] Cut018
  Base = -> Cylinder018
  Refine = true
  Tool = -> Box022
FEATURE [Part::MultiFuse] Fusion014
  Refine = true
  Shapes = -> [Box021,Cut018,Cylinder017,Cylinder016]
FEATURE [Part::Cylinder] Cylinder019
  Angle = 360
  AttacherType = Attacher::AttachEngine3D
  Height = 7.5
  Placement = pos=(6,-14.25,49.2) rot=(1,0,0;1.5708rad)
  Radius = 51
FEATURE [Part::Cylinder] Cylinder020
  Angle = 360
  AttacherType = Attacher::AttachEngine3D
  Height = 7.5
  Placement = pos=(6,-14.25,49.2) rot=(1,0,0;1.5708rad)
  Radius = 50
FEATURE [Part::Cut] Cut019
  Base = -> Cylinder019
  Refine = true
  Tool = -> Cylinder020
FEATURE [Part::Cut] Cut020
  Base = -> Fusion014
  Refine = true
  Tool = -> Cut019
FEATURE [Part::Cylinder] Cylinder021
  Angle = 360
  AttacherType = Attacher::AttachEngine3D
  Height = 10
  Placement = pos=(12,-18,-9.2) rot=(0,0,1;0rad)
  Radius = 1.6
FEATURE [Part::Cylinder] Cylinder022
  Angle = 360
  AttacherType = Attacher::AttachEngine3D
  Height = 10
  Placement = pos=(0,-18,-9.2) rot=(0,0,1;0rad)
  Radius = 1.6
FEATURE [Part::MultiFuse] Fusion015
  Placement = pos=(0,0,5) rot=(0,0,1;0rad)
  Refine = true
  Shapes = -> [Cylinder021,Cylinder022]
FEATURE [Part::Cut] Cut021  label="leafspring-spacer-upper-front-left"
  Base = -> Cut020
  Placement = pos=(92,63,-38) rot=(0,0,1;0rad)
  Refine = true
  Tool = -> Fusion015
FEATURE [Part::Cylinder] Cylinder698  label="Cylinder1389"
  Angle = 360
  AttacherType = Attacher::AttachEngine3D
  Height = 3.5
  Placement = pos=(498.5,53.5,-13.5) rot=(1,0,0;1.5708rad)
  Radius = 4
FEATURE [Part::Cylinder] Cylinder699  label="Cylinder1390"
  Angle = 360
  AttacherType = Attacher::AttachEngine3D
  Height = 1.75
  Placement = pos=(498.5,51.75,-13.5) rot=(1,0,0;1.5708rad)
  Radius = 2.1
FEATURE [Part::Cylinder] Cylinder700  label="Cylinder1391"
  Angle = 360
  AttacherType = Attacher::AttachEngine3D
  Height = 3.5
  Placement = pos=(498.5,53.5,-13.5) rot=(1,0,0;1.5708rad)
  Radius = 1.5
FEATURE [Part::MultiFuse] Fusion465
  Refine = true
  Shapes = -> [Cylinder699,Cylinder700]
FEATURE [Part::Cut] Cut582  label="Cut870"
  Base = -> Cylinder698
  Refine = true
  Tool = -> Fusion465
FEATURE [Part::Cylinder] Cylinder701  label="Cylinder1392"
  Angle = 360
  AttacherType = Attacher::AttachEngine3D
  Height = 6.75
  Placement = pos=(498.5,48.87,-13.5) rot=(1,0,0;1.5708rad)
  Radius = 4
FEATURE [Part::Cylinder] Cylinder702  label="Cylinder1393"
  Angle = 360
  AttacherType = Attacher::AttachEngine3D
  Height = 6.75
  Placement = pos=(498.5,48.87,-13.5) rot=(1,0,0;1.5708rad)
  Radius = 2.1
FEATURE [Part::Cut] Cut583  label="leafspring-bisquit-mount-spacer-left"
  Base = -> Cylinder701
  Placement = pos=(5,0,3) rot=(0,0,1;0rad)
  Refine = true
  Tool = -> Cylinder702
FEATURE [Part::Cylinder] Cylinder706  label="Cylinder1394"
  Angle = 360
  AttacherType = Attacher::AttachEngine3D
  Height = 15
  Placement = pos=(399.5,54,-13) rot=(1,0,0;1.5708rad)
  Radius = 1.25
FEATURE [Part::Cylinder] Cylinder707  label="Cylinder1395"
  Angle = 360
  AttacherType = Attacher::AttachEngine3D
  Height = 15
  Placement = pos=(498.5,54,-13.5) rot=(1,0,0;1.5708rad)
  Radius = 1.25
FEATURE [Part::Cylinder] Cylinder708  label="Cylinder1365"
  Angle = 360
  AttacherType = Attacher::AttachEngine3D
  Height = 15
  Placement = pos=(391.5,54,-13) rot=(1,0,0;1.5708rad)
  Radius = 1.25
FEATURE [Part::Cylinder] Cylinder709  label="Cylinder1366"
  Angle = 360
  AttacherType = Attacher::AttachEngine3D
  Height = 15
  Placement = pos=(399.5,54,-13) rot=(1,0,0;1.5708rad)
  Radius = 1.25
FEATURE [Part::Cylinder] Cylinder710  label="Cylinder1367"
  Angle = 360
  AttacherType = Attacher::AttachEngine3D
  Height = 15
  Placement = pos=(498.5,54,-13.5) rot=(1,0,0;1.5708rad)
  Radius = 1.25
FEATURE [Part::Cylinder] Cylinder711  label="Cylinder842"
  Angle = 360
  AttacherType = Attacher::AttachEngine3D
  Height = 15
  Placement = pos=(391.5,54,-13) rot=(1,0,0;1.5708rad)
  Radius = 1.25
FEATURE [Part::MultiFuse] Fusion468
  Refine = true
  Shapes = -> [Cylinder710,Cylinder709,Cylinder711]
FEATURE [Part::Box] Box476  label="Cube678"
  AttacherType = Attacher::AttachEngine3D
  Height = 20
  Length = 120
  Placement = pos=(383.5,49.5,-21) rot=(0,0,1;0rad)
  Width = 4
FEATURE [Part::Cut] Cut585  label="Cut871"
  Base = -> Box476
  Refine = true
  Tool = -> Fusion468
FEATURE [Part::Mirroring] Part__Mirroring093  label="Cut850 (Mirror #70)"
  Base = (0,0,0)
  Normal = (0,0,1)
  Placement = pos=(0,0,-22) rot=(0,0,1;0rad)
  Source = -> Cut585
FEATURE [Part::MultiFuse] Fusion469
  Refine = true
  Shapes = -> [Cylinder707,Cylinder706,Cylinder708]
FEATURE [Part::Cut] Cut586  label="Cut872"
  Base = -> Part__Mirroring093
  Refine = true
  Tool = -> Fusion469
FEATURE [Part::Box] Box477  label="Cube679"
  AttacherType = Attacher::AttachEngine3D
  Height = 3
  Length = 120
  Placement = pos=(383.5,49.5,-1) rot=(0,0,1;0rad)
  Width = 11
FEATURE [Part::Box] Box478  label="Cube680"
  AttacherType = Attacher::AttachEngine3D
  Height = 3
  Length = 120
  Placement = pos=(383.5,49.5,-24) rot=(0,0,1;0rad)
  Width = 11
FEATURE [Part::MultiFuse] Fusion470  label="leafspring-mounts-HOLES"
  Placement = pos=(0,0,3) rot=(0,0,1;0rad)
  Refine = true
  Shapes = -> [Cut586,Box478,Box477]
FEATURE [Part::Cylinder] Cylinder713  label="Cylinder843"
  Angle = 360
  AttacherType = Attacher::AttachEngine3D
  Height = 2
  Placement = pos=(493.5,53.5,-11) rot=(1,0,0;1.5708rad)
  Radius = 3.1
FEATURE [Part::Cut] Cut587  label="leafspring-bisquit-mount-left"
  Base = -> Cut582
  Placement = pos=(5,0,3) rot=(0,0,1;0rad)
  Refine = true
  Tool = -> Cylinder713
FEATURE [Part::Cylinder] Cylinder714  label="Cylinder844"
  Angle = 360
  AttacherType = Attacher::AttachEngine3D
  Height = 3.5
  Placement = pos=(498.5,53.5,-13.5) rot=(1,0,0;1.5708rad)
  Radius = 4
FEATURE [Part::Cylinder] Cylinder715  label="Cylinder845"
  Angle = 360
  AttacherType = Attacher::AttachEngine3D
  Height = 3.5
  Placement = pos=(498.5,53.5,-13.5) rot=(1,0,0;1.5708rad)
  Radius = 1.5
FEATURE [Part::Cylinder] Cylinder716  label="Cylinder846"
  Angle = 360
  AttacherType = Attacher::AttachEngine3D
  Height = 1.75
  Placement = pos=(498.5,51.75,-13.5) rot=(1,0,0;1.5708rad)
  Radius = 2.1
FEATURE [Part::Cylinder] Cylinder717  label="Cylinder847"
  Angle = 360
  AttacherType = Attacher::AttachEngine3D
  Height = 2
  Placement = pos=(493.5,53.5,-11) rot=(1,0,0;1.5708rad)
  Radius = 3.1
FEATURE [Part::MultiFuse] Fusion471
  Refine = true
  Shapes = -> [Cylinder716,Cylinder715]
FEATURE [Part::Cut] Cut589  label="Cut873"
  Base = -> Cylinder714
  Refine = true
  Tool = -> Fusion471
FEATURE [Part::Cut] Cut588  label="leafspring-bisquit-mount-left001"
  Base = -> Cut589
  Refine = true
  Tool = -> Cylinder717
FEATURE [Part::Mirroring] Part__Mirroring094  label="leafspring-bisquit-mount-right"
  Base = (0,0,0)
  Normal = (0,1,0)
  Placement = pos=(5,170,3) rot=(0,0,1;0rad)
  Source = -> Cut588
FEATURE [Part::Cylinder] Cylinder718  label="Cylinder848"
  Angle = 360
  AttacherType = Attacher::AttachEngine3D
  Height = 6.75
  Placement = pos=(498.5,48.87,-13.5) rot=(1,0,0;1.5708rad)
  Radius = 4
FEATURE [Part::Cylinder] Cylinder719  label="Cylinder849"
  Angle = 360
  AttacherType = Attacher::AttachEngine3D
  Height = 6.75
  Placement = pos=(498.5,48.87,-13.5) rot=(1,0,0;1.5708rad)
  Radius = 2.1
FEATURE [Part::Cut] Cut590  label="leafspring-bisquit-mount-spacer-right"
  Base = -> Cylinder718
  Placement = pos=(5,79,3) rot=(0,0,1;0rad)
  Refine = true
  Tool = -> Cylinder719
FEATURE [Part::Cylinder] Cylinder726  label="Cylinder850"
  Angle = 360
  AttacherType = Attacher::AttachEngine3D
  Height = 15
  Placement = pos=(395.5,54,-28) rot=(1,0,0;1.5708rad)
  Radius = 2.1
FEATURE [Part::Box] Box482  label="Cube684"
  AttacherType = Attacher::AttachEngine3D
  Height = 12
  Length = 12
  Placement = pos=(389.5,39.75,-32) rot=(0,0,1;0rad)
  Width = 13.75
FEATURE [Part::Box] Box483  label="Cube685"
  AttacherType = Attacher::AttachEngine3D
  Height = 8
  Length = 12
  Placement = pos=(389.5,41.75,-32) rot=(0,0,1;0rad)
  Width = 7.5
FEATURE [Part::Cut] Cut594  label="Cut874"
  Base = -> Box482
  Refine = true
  Tool = -> Box483
FEATURE [Part::Box] Box484  label="Cube686"
  AttacherType = Attacher::AttachEngine3D
  Height = 10
  Length = 16
  Placement = pos=(387.5,49.75,-20) rot=(0,0,1;0rad)
  Width = 3.75
FEATURE [Part::Cylinder] Cylinder727  label="Cylinder851"
  Angle = 360
  AttacherType = Attacher::AttachEngine3D
  Height = 15
  Placement = pos=(391.5,54,-15) rot=(1,0,0;1.5708rad)
  Radius = 1.6
FEATURE [Part::Cylinder] Cylinder728  label="Cylinder852"
  Angle = 360
  AttacherType = Attacher::AttachEngine3D
  Height = 15
  Placement = pos=(399.5,54,-15) rot=(1,0,0;1.5708rad)
  Radius = 1.6
FEATURE [Part::MultiFuse] Fusion475
  Refine = true
  Shapes = -> [Box484,Cut594]
FEATURE [Part::Fillet] Fillet334
  Base = -> Fusion475
  Edges = 3 edges r=3: [Edge6,Edge7,Edge16]
FEATURE [Part::Fillet] Fillet335
  Base = -> Fillet334
  Edges = 4 edges r=4: [Edge29,Edge32,Edge40,Edge43]
FEATURE [Part::Chamfer] Chamfer081
  Base = -> Fillet335
  Edges = 2 edges r=1.99: [Edge21,Edge44]
FEATURE [Part::Cylinder] Cylinder729  label="Cylinder853"
  Angle = 360
  AttacherType = Attacher::AttachEngine3D
  Height = 2
  Placement = pos=(391.5,49.75,-15) rot=(1,0,0;1.5708rad)
  Radius = 3.1
FEATURE [Part::Cylinder] Cylinder730  label="Cylinder854"
  Angle = 360
  AttacherType = Attacher::AttachEngine3D
  Height = 2
  Placement = pos=(399.5,49.75,-15) rot=(1,0,0;1.5708rad)
  Radius = 3.1
FEATURE [Part::MultiFuse] Fusion476
  Refine = true
  Shapes = -> [Cylinder729,Cylinder730,Cylinder726,Cylinder728,Cylinder727]
FEATURE [Part::Cut] Cut593  label="leafspring-mount-front-left-OLD"
  Base = -> Chamfer081
  Placement = pos=(-350,0,5) rot=(0,0,1;0rad)
  Refine = true
  Tool = -> Fusion476
FEATURE [Part::Box] Box491  label="Cube693"
  AttacherType = Attacher::AttachEngine3D
  Height = 21
  Length = 25
  Placement = pos=(128,50.5,-21.5) rot=(0,0,1;0rad)
  Width = 3
FEATURE [Part::Box] Box492  label="Cube694"
  AttacherType = Attacher::AttachEngine3D
  Height = 3
  Length = 25
  Placement = pos=(128,50.5,-24.5) rot=(0,0,1;0rad)
  Width = 10
FEATURE [Part::Box] Box493  label="Cube695"
  AttacherType = Attacher::AttachEngine3D
  Height = 3
  Length = 25
  Placement = pos=(128,50.5,-0.5) rot=(0,0,1;0rad)
  Width = 10
FEATURE [Part::MultiFuse] Fusion493
  Refine = true
  Shapes = -> [Box491,Box493,Box492]
FEATURE [Part::Cylinder] Cylinder759  label="Cylinder862"
  Angle = 360
  AttacherType = Attacher::AttachEngine3D
  Height = 15
  Placement = pos=(148.5,58.5,-13.5) rot=(1,0,0;1.5708rad)
  Radius = 1.25
FEATURE [Part::Cylinder] Cylinder760  label="Cylinder863"
  Angle = 360
  AttacherType = Attacher::AttachEngine3D
  Height = 15
  Placement = pos=(136,60.5,-12) rot=(1,0,0;1.5708rad)
  Radius = 1.25
FEATURE [Part::Cylinder] Cylinder763  label="Cylinder870"
  Angle = 360
  AttacherType = Attacher::AttachEngine3D
  Height = 15
  Placement = pos=(132.5,58.5,-13.5) rot=(1,0,0;1.5708rad)
  Radius = 1.25
FEATURE [Part::Cylinder] Cylinder764  label="Cylinder871"
  Angle = 360
  AttacherType = Attacher::AttachEngine3D
  Height = 15
  Placement = pos=(145,60.5,-12) rot=(1,0,0;1.5708rad)
  Radius = 1.25
FEATURE [Part::MultiFuse] Fusion497
  Refine = true
  Shapes = -> [Cylinder759,Cylinder760,Cylinder763,Cylinder764]
FEATURE [Part::Cut] Cut605  label="wing-supports-HOLES"
  Base = -> Fusion493
  Placement = pos=(0,0,3) rot=(0,0,1;0rad)
  Refine = true
  Tool = -> Fusion497
FEATURE [Part::Cylinder] Cylinder765  label="Cylinder925"
  Angle = 360
  AttacherType = Attacher::AttachEngine3D
  Height = 28
  Placement = pos=(348.5,42,-34) rot=(0,0,1;0rad)
  Radius = 11
FEATURE [Part::Cylinder] Cylinder766  label="Cylinder893"
  Angle = 360
  AttacherType = Attacher::AttachEngine3D
  Height = 28
  Placement = pos=(348.5,42,-34) rot=(0,0,1;0rad)
  Radius = 11
FEATURE [Part::MultiFuse] Fusion498
  Refine = true
FEATURE [Part::Cut] Cut607
  Refine = true
FEATURE [Part::Fillet] Fillet344  label="central-axle-susp-left_baloon"
  Base = -> Cylinder766
  Edges = 2 edges r=4: [Edge1,Edge3]
  Placement = pos=(0,0,-1) rot=(0,0,1;0rad)
FEATURE [Part::Cut] Cut610  label="Cut880"
  Base = -> Cut607
  Refine = true
FEATURE [Part::MultiFuse] Fusion500  label="central-axle"
  Refine = true
  Shapes = -> [Cut610,Fusion498]
FEATURE [Part::Fillet] Fillet346  label="central-axle-susp-right_baloon"
  Base = -> Cylinder765
  Edges = 2 edges r=4: [Edge1,Edge3]
  Placement = pos=(0,86,0) rot=(0,0,1;0rad)
FEATURE [Part::Box] Box494  label="Cube696"
  AttacherType = Attacher::AttachEngine3D
  Height = 17
  Length = 25
  Placement = pos=(128,45.5,-18) rot=(0,0,1;0rad)
  Width = 8
FEATURE [Part::Cylinder] Cylinder768  label="Cylinder1368"
  Angle = 360
  AttacherType = Attacher::AttachEngine3D
  Height = 24.5
  Placement = pos=(144,53.5,-6) rot=(1,0,0;1.5708rad)
  Radius = 3
FEATURE [Part::Cylinder] Cylinder769  label="Cylinder1251"
  Angle = 360
  AttacherType = Attacher::AttachEngine3D
  Height = 18
  Placement = pos=(131,51,-5) rot=(1,0,0;0.785398rad)
  Radius = 3
FEATURE [Part::Feature] Face040
  shape: bbox 7.785 x 2e-07 x 7.712 mm, 1 faces, 0 solids (baked)
FEATURE [Part::Feature] Face041
  shape: bbox 7.318 x 4.987 x 4.987 mm, 1 faces, 0 solids (baked)
FEATURE [Part::Loft] Loft016
  Closed = false
  MaxDegree = 5
  Ruled = true
  Sections = -> [Face040,Face041]
  Solid = true
FEATURE [Part::Cylinder] Cylinder770  label="Cylinder1396"
  Angle = 360
  AttacherType = Attacher::AttachEngine3D
  Height = 3
  Placement = pos=(131,31,12) rot=(1,0,0;1.5708rad)
  Radius = 3
FEATURE [Part::MultiFuse] Fusion501
  Placement = pos=(0,1,0) rot=(0,0,1;0rad)
  Refine = true
  Shapes = -> [Loft016,Cylinder770]
FEATURE [Part::Cylinder] Cylinder771  label="Cylinder974"
  Angle = 360
  AttacherType = Attacher::AttachEngine3D
  Height = 5
  Placement = pos=(131,33,12) rot=(1,0,0;1.5708rad)
  Radius = 1.6
FEATURE [Part::Cylinder] Cylinder772  label="Cylinder1397"
  Angle = 360
  AttacherType = Attacher::AttachEngine3D
  Height = 25
  Placement = pos=(144,53,-6) rot=(1,0,0;1.5708rad)
  Radius = 1.6
FEATURE [Part::MultiFuse] Fusion502
  Placement = pos=(0,1,0) rot=(0,0,1;0rad)
  Refine = true
  Shapes = -> [Cylinder771,Cylinder772]
FEATURE [Part::Cylinder] Cylinder773  label="Cylinder1398"
  Angle = 360
  AttacherType = Attacher::AttachEngine3D
  Height = 15
  Placement = pos=(132,61.5,-16) rot=(1,0,0;1.5708rad)
  Radius = 1.6
FEATURE [Part::Cylinder] Cylinder774  label="Cylinder1399"
  Angle = 360
  AttacherType = Attacher::AttachEngine3D
  Height = 2.5
  Placement = pos=(132,49,-16) rot=(1,0,0;1.5708rad)
  Radius = 3
FEATURE [Part::MultiFuse] Fusion503
  Placement = pos=(4,-1.5,4) rot=(0,0,1;0rad)
  Refine = true
  Shapes = -> [Cylinder773,Cylinder774]
FEATURE [Part::Box] Box495  label="Cube697"
  AttacherType = Attacher::AttachEngine3D
  Height = 9.5
  Length = 10
  Placement = pos=(143,45.5,-18) rot=(0,0,1;0rad)
  Width = 5
FEATURE [Part::Fillet] Fillet350
  Base = -> Box495
  Edges = 1 edges r=4: [Edge2]
FEATURE [Part::Cylinder] Cylinder775  label="Cylinder1400"
  Angle = 360
  AttacherType = Attacher::AttachEngine3D
  Height = 3.5
  Placement = pos=(148.5,53.5,-13.5) rot=(1,0,0;1.5708rad)
  Radius = 3
FEATURE [Part::Cylinder] Cylinder776  label="Cylinder1401"
  Angle = 360
  AttacherType = Attacher::AttachEngine3D
  Height = 1.75
  Placement = pos=(498.5,51.75,-13.5) rot=(1,0,0;1.5708rad)
  Radius = 2.1
FEATURE [Part::Cylinder] Cylinder777  label="Cylinder1402"
  Angle = 360
  AttacherType = Attacher::AttachEngine3D
  Height = 3.5
  Placement = pos=(498.5,53.5,-13.5) rot=(1,0,0;1.5708rad)
  Radius = 1.5
FEATURE [Part::MultiFuse] Fusion504
  Placement = pos=(-350,0,0) rot=(0,0,1;0rad)
  Refine = true
  Shapes = -> [Cylinder776,Cylinder777]
FEATURE [Part::Cut] Cut611  label="Cut882"
  Base = -> Box494
  Refine = true
  Tool = -> Fillet350
FEATURE [Part::MultiFuse] Fusion505
  Refine = true
  Shapes = -> [Cut611,Cylinder775]
FEATURE [Part::Cut] Cut612  label="Cut883"
  Base = -> Fusion505
  Refine = true
  Tool = -> Fusion504
FEATURE [Part::Cylinder] Cylinder779  label="Cylinder1403"
  Angle = 360
  AttacherType = Attacher::AttachEngine3D
  Height = 23
  Placement = pos=(131,52,-6) rot=(1,0,0;0.785398rad)
  Radius = 3
FEATURE [Part::Cylinder] Cylinder780  label="Cylinder981"
  Angle = 360
  AttacherType = Attacher::AttachEngine3D
  Height = 18
  Placement = pos=(131,52,-6) rot=(1,0,0;0.785398rad)
  Radius = 3
FEATURE [Part::Cut] Cut613
  Base = -> Cylinder779
  Refine = true
  Tool = -> Cylinder780
FEATURE [Part::MultiFuse] Fusion506
  Refine = true
  Shapes = -> [Cylinder769,Cut613]
FEATURE [Part::MultiFuse] Fusion507
  Refine = true
  Shapes = -> [Fusion506,Cylinder768,Fusion501,Cut612]
FEATURE [Part::Cut] Cut614
  Base = -> Fusion507
  Refine = true
  Tool = -> Fusion502
FEATURE [Part::Cut] Cut604  label="wing-support-left_"
  Base = -> Cut614
  Placement = pos=(0,0,3) rot=(0,0,1;0rad)
  Refine = true
  Tool = -> Fusion503
FEATURE [Part::Box] Box496  label="Cube698"
  AttacherType = Attacher::AttachEngine3D
  Height = 17
  Length = 25
  Placement = pos=(128,45.5,-18) rot=(0,0,1;0rad)
  Width = 8
FEATURE [Part::Cylinder] Cylinder761  label="Cylinder864"
  Angle = 360
  AttacherType = Attacher::AttachEngine3D
  Height = 24.5
  Placement = pos=(144,53.5,-6) rot=(1,0,0;1.5708rad)
  Radius = 3
FEATURE [Part::Cylinder] Cylinder762  label="Cylinder865"
  Angle = 360
  AttacherType = Attacher::AttachEngine3D
  Height = 18
  Placement = pos=(131,51,-5) rot=(1,0,0;0.785398rad)
  Radius = 3
FEATURE [Part::Feature] Face042
  shape: bbox 7.785 x 2e-07 x 7.712 mm, 1 faces, 0 solids (baked)
FEATURE [Part::Feature] Face043
  shape: bbox 7.318 x 4.987 x 4.987 mm, 1 faces, 0 solids (baked)
FEATURE [Part::Loft] Loft017
  Closed = false
  MaxDegree = 5
  Ruled = true
  Sections = -> [Face042,Face043]
  Solid = true
FEATURE [Part::Cylinder] Cylinder781  label="Cylinder866"
  Angle = 360
  AttacherType = Attacher::AttachEngine3D
  Height = 3
  Placement = pos=(131,31,12) rot=(1,0,0;1.5708rad)
  Radius = 3
FEATURE [Part::MultiFuse] Fusion494
  Placement = pos=(0,1,0) rot=(0,0,1;0rad)
  Refine = true
  Shapes = -> [Loft017,Cylinder781]
FEATURE [Part::Cylinder] Cylinder782  label="Cylinder867"
  Angle = 360
  AttacherType = Attacher::AttachEngine3D
  Height = 5
  Placement = pos=(131,33,12) rot=(1,0,0;1.5708rad)
  Radius = 1.6
FEATURE [Part::Cylinder] Cylinder783  label="Cylinder868"
  Angle = 360
  AttacherType = Attacher::AttachEngine3D
  Height = 25
  Placement = pos=(144,53,-6) rot=(1,0,0;1.5708rad)
  Radius = 1.6
FEATURE [Part::MultiFuse] Fusion495
  Placement = pos=(0,1,0) rot=(0,0,1;0rad)
  Refine = true
  Shapes = -> [Cylinder782,Cylinder783]
FEATURE [Part::Cylinder] Cylinder784  label="Cylinder869"
  Angle = 360
  AttacherType = Attacher::AttachEngine3D
  Height = 15
  Placement = pos=(132,61.5,-16) rot=(1,0,0;1.5708rad)
  Radius = 1.6
FEATURE [Part::Cylinder] Cylinder785  label="Cylinder1404"
  Angle = 360
  AttacherType = Attacher::AttachEngine3D
  Height = 2.5
  Placement = pos=(132,49,-16) rot=(1,0,0;1.5708rad)
  Radius = 3
FEATURE [Part::MultiFuse] Fusion496
  Placement = pos=(4,-1.5,4) rot=(0,0,1;0rad)
  Refine = true
  Shapes = -> [Cylinder784,Cylinder785]
FEATURE [Part::Box] Box497  label="Cube699"
  AttacherType = Attacher::AttachEngine3D
  Height = 9.5
  Length = 10
  Placement = pos=(143,45.5,-18) rot=(0,0,1;0rad)
  Width = 5
FEATURE [Part::Fillet] Fillet351
  Base = -> Box497
  Edges = 1 edges r=4: [Edge2]
FEATURE [Part::Cylinder] Cylinder786  label="Cylinder1405"
  Angle = 360
  AttacherType = Attacher::AttachEngine3D
  Height = 3.5
  Placement = pos=(148.5,53.5,-13.5) rot=(1,0,0;1.5708rad)
  Radius = 3
FEATURE [Part::Cylinder] Cylinder787  label="Cylinder872"
  Angle = 360
  AttacherType = Attacher::AttachEngine3D
  Height = 1.75
  Placement = pos=(498.5,51.75,-13.5) rot=(1,0,0;1.5708rad)
  Radius = 2.1
FEATURE [Part::Cylinder] Cylinder788  label="Cylinder873"
  Angle = 360
  AttacherType = Attacher::AttachEngine3D
  Height = 3.5
  Placement = pos=(498.5,53.5,-13.5) rot=(1,0,0;1.5708rad)
  Radius = 1.5
FEATURE [Part::MultiFuse] Fusion508
  Placement = pos=(-350,0,0) rot=(0,0,1;0rad)
  Refine = true
  Shapes = -> [Cylinder787,Cylinder788]
FEATURE [Part::Cut] Cut615  label="Cut885"
  Base = -> Box496
  Refine = true
  Tool = -> Fillet351
FEATURE [Part::MultiFuse] Fusion509
  Refine = true
  Shapes = -> [Cut615,Cylinder786]
FEATURE [Part::Cut] Cut616  label="Cut886"
  Base = -> Fusion509
  Refine = true
  Tool = -> Fusion508
FEATURE [Part::Cylinder] Cylinder789  label="Cylinder874"
  Angle = 360
  AttacherType = Attacher::AttachEngine3D
  Height = 23
  Placement = pos=(131,52,-6) rot=(1,0,0;0.785398rad)
  Radius = 3
FEATURE [Part::Cylinder] Cylinder790  label="Cylinder875"
  Angle = 360
  AttacherType = Attacher::AttachEngine3D
  Height = 18
  Placement = pos=(131,52,-6) rot=(1,0,0;0.785398rad)
  Radius = 3
FEATURE [Part::Cut] Cut617
  Base = -> Cylinder789
  Refine = true
  Tool = -> Cylinder790
FEATURE [Part::MultiFuse] Fusion510
  Refine = true
  Shapes = -> [Cylinder762,Cut617]
FEATURE [Part::MultiFuse] Fusion511
  Refine = true
  Shapes = -> [Fusion510,Cylinder761,Fusion494,Cut616]
FEATURE [Part::Cut] Cut618
  Base = -> Fusion511
  Refine = true
  Tool = -> Fusion495
FEATURE [Part::Cut] Cut619
  Base = -> Cut618
  Refine = true
  Tool = -> Fusion496
FEATURE [Part::Mirroring] Part__Mirroring098  label="wing-support-right_"
  Base = (0,0,0)
  Normal = (0,1,0)
  Placement = pos=(0,170,3) rot=(0,0,1;0rad)
  Source = -> Cut619
FEATURE [Part::Cylinder] Cylinder791  label="Cylinder1406"
  Angle = 360
  AttacherType = Attacher::AttachEngine3D
  Height = 13
  Placement = pos=(348.5,42,-34) rot=(0,0,1;0rad)
  Radius = 11
FEATURE [Part::Fillet] Fillet352  label="central-axle-susp-left_baloon-compressed"
  Base = -> Cylinder791
  Edges = 2 edges r=4: [Edge1,Edge3]
  Placement = pos=(0,0,14) rot=(0,0,1;0rad)
FEATURE [Part::Cylinder] Cylinder792  label="Cylinder1407"
  Angle = 360
  AttacherType = Attacher::AttachEngine3D
  Height = 13
  Placement = pos=(348.5,42,-34) rot=(0,0,1;0rad)
  Radius = 11
FEATURE [Part::Fillet] Fillet353  label="central-axle-susp-right_baloon-compressed"
  Base = -> Cylinder792
  Edges = 2 edges r=4: [Edge1,Edge3]
  Placement = pos=(0,86,14) rot=(0,0,1;0rad)
FEATURE [Part::Box] Box498  label="Cube700"
  AttacherType = Attacher::AttachEngine3D
  Height = 16
  Length = 16
  Placement = pos=(90,1,-59) rot=(0,0,1;0rad)
  Width = 168
FEATURE [Part::Cylinder] Cylinder793  label="Cylinder1408"
  Angle = 360
  AttacherType = Attacher::AttachEngine3D
  Height = 16
  Placement = pos=(90,85,-51) rot=(0,1,0;1.5708rad)
  Radius = 20
FEATURE [Part::Sphere] Sphere
  Angle1 = -90
  Angle2 = 90
  Angle3 = 360
  AttacherType = Attacher::AttachEngine3D
  Placement = pos=(98,85,-51) rot=(0,0,1;0rad)
  Radius = 20
FEATURE [Part::Cylinder] Cylinder794  label="Cylinder1409"
  Angle = 360
  AttacherType = Attacher::AttachEngine3D
  Height = 28
  Placement = pos=(98,85,-51) rot=(0,1,0;1.5708rad)
  Radius = 8.5
FEATURE [Part::MultiFuse] Fusion512  label="front-axle"
  Refine = true
  Shapes = -> [Box498,Sphere,Cylinder794,Cylinder793]
FEATURE [Part::Box] Box499  label="Cube701"
  AttacherType = Attacher::AttachEngine3D
  Height = 16
  Length = 16
  Placement = pos=(90,24,-59) rot=(0,0,1;0rad)
  Width = 122
FEATURE [Part::Cylinder] Cylinder795  label="Cylinder1410"
  Angle = 360
  AttacherType = Attacher::AttachEngine3D
  Height = 16
  Placement = pos=(90,85,-51) rot=(0,1,0;1.5708rad)
  Radius = 20
FEATURE [Part::Sphere] Sphere001
  Angle1 = -90
  Angle2 = 90
  Angle3 = 360
  AttacherType = Attacher::AttachEngine3D
  Placement = pos=(98,85,-51) rot=(0,0,1;0rad)
  Radius = 20
FEATURE [Part::Cylinder] Cylinder796  label="Cylinder1411"
  Angle = 360
  AttacherType = Attacher::AttachEngine3D
  Height = 28
  Placement = pos=(70,85,-51) rot=(0,1,0;1.5708rad)
  Radius = 8.5
FEATURE [Part::MultiFuse] Fusion513  label="rear-axle"
  Placement = pos=(355,0,0) rot=(0,0,1;0rad)
  Refine = true
  Shapes = -> [Box499,Sphere001,Cylinder796,Cylinder795]
FEATURE [Part::Cut] Cut014047  label="diff-box-rear-01"
  Placement = pos=(0,0,-1) rot=(0,0,1;0rad)
  Refine = true
FEATURE [Part::Fillet] Fillet354  label="diff-box-front-01"
  Edges = 1 edges r=1.99: [Edge305]
FEATURE [Part::Cylinder] Cylinder088
  Angle = 360
  AttacherType = Attacher::AttachEngine3D
  Height = 43.5
  Placement = pos=(20.75,0,-18.5) rot=(0,0,1;0rad)
  Radius = 2.5
FEATURE [Part::Cylinder] Cylinder087
  Angle = 360
  AttacherType = Attacher::AttachEngine3D
  Height = 54
  Placement = pos=(0,0,-23.5) rot=(0,0,1;0rad)
  Radius = 2.5
FEATURE [Part::Cut] Cut014020  label="diff-box-mount-left"
  Base = -> Fillet013
  Placement = pos=(0,0,-1) rot=(0,0,1;0rad)
  Refine = true
  Tool = -> Fusion056
FEATURE [Part::Mirroring] Part__Mirroring001  label="diff-box-mount-right"
  Base = (0,0,0)
  Normal = (0,1,0)
  Placement = pos=(0,0,-1) rot=(0,0,1;0rad)
FEATURE [Part::MultiFuse] Fusion514  label="transfer-case"
  Placement = pos=(250,85,-27.5) rot=(0,-1,0;1.5708rad)
  Refine = true
  Shapes = -> [Cut014047,Fillet354,Cylinder087,Cylinder088,Cut014020,Part__Mirroring001]
FEATURE [Part::Fillet] Fillet356  label="central-axle-left-lower-bar"
  Base = -> Fillet
  Edges = 6 edges r=0.75: [Edge10,Edge11,Edge12,Edge13,Edge24,Edge25]
  Placement = pos=(30.1998,4,99.6027) rot=(0,1,0;0.340339rad)
FEATURE [Part::Fillet] Fillet365  label="central-axle-right-lower-bar"
  Edges = 6 edges r=0.75: [Edge10,Edge11,Edge12,Edge13,Edge24,Edge25]
  Placement = pos=(30.1998,68,99.6027) rot=(0,1,0;0.340339rad)
FEATURE [Part::Cut] Cut014060  label="central-axle-left-baloon-support"
  Refine = true
FEATURE [Part::Cut] Cut014061  label="central-axle-left-upper-bar-support"
  Refine = true
FEATURE [Part::Cut] Cut014074  label="central-axle-left-upper-bar"
  Placement = pos=(30.3862,0,84.3621) rot=(0,1,0;0.340339rad)
  Refine = true
FEATURE [Part::Mirroring] Part__Mirroring099  label="central-axle-right-upper-bar"
  Base = (0,0,0)
  Normal = (0,1,0)
  Placement = pos=(0,170,0) rot=(0,0,1;0rad)
FEATURE [Part::Cut] Cut014085  label="central-axle-left-upper-bar-support-internal"
  Refine = true
FEATURE [Part::Cut] Cut014089  label="central-axle-left-lower-bar-support-external"
  Refine = true
FEATURE [Part::Cut] Cut014090  label="central-axle-left-lower-bar-support-internal"
  Refine = true
FEATURE [Part::Mirroring] Part__Mirroring100  label="central-axle-right-baloon-support"
  Base = (0,0,0)
  Normal = (0,1,0)
  Placement = pos=(0,170,0) rot=(0,0,1;0rad)
FEATURE [Part::Mirroring] Part__Mirroring101  label="central-axle-right-upper-bar-support"
  Base = (0,0,0)
  Normal = (0,1,0)
  Placement = pos=(0,170,0) rot=(0,0,1;0rad)
FEATURE [Part::Mirroring] Part__Mirroring102  label="central-axle-right-upper-bar-support-internal"
  Base = (0,0,0)
  Normal = (0,1,0)
  Placement = pos=(0,170,0) rot=(0,0,1;0rad)
FEATURE [Part::Mirroring] Part__Mirroring103  label="central-axle-right-lower-bar-support-external"
  Base = (0,0,0)
  Normal = (0,1,0)
  Placement = pos=(0,170,0) rot=(0,0,1;0rad)
FEATURE [Part::Mirroring] Part__Mirroring104  label="central-axle-right-lower-bar-support-internal"
  Base = (0,0,0)
  Normal = (0,1,0)
  Placement = pos=(0,170,0) rot=(0,0,1;0rad)
FEATURE [Part::Mirroring] Part__Mirroring105  label="leafspring-mount-front-right"
  Base = (0,0,0)
  Normal = (0,1,0)
  Placement = pos=(0,170,0) rot=(0,0,1;0rad)
  Source = -> Cut593
FEATURE [Part::MultiFuse] Fusion563  label="leafspring-mount-front-left-int-servo"
  Placement = pos=(0,0,3) rot=(0,0,1;0rad)
  Refine = true
  Shapes = -> [Fillet356]
FEATURE [Part::Chamfer] Chamfer104  label="front-axle-steering-arm-int-servo"
  Edges = 20 edges r=0.5: [Edge10,Edge12,Edge19,Edge20,Edge21,Edge22,Edge23,Edge24,Edge25,Edge26,Edge27,Edge31,Edge33,Edge34,Edge35,Edge36,Edge37,Edge38,Edge39,Edge40]
  Placement = pos=(0,0,3) rot=(0,0,1;0rad)
FEATURE [Part::Cylinder] Cylinder889  label="front-steering-arm"
  Angle = 360
  AttacherType = Attacher::AttachEngine3D
  Height = 63
  Placement = pos=(37,35.5,-30) rot=(-0.074596,0.994785,0.069562;1.5062rad)
  Radius = 1.5
FEATURE [Part::Cylinder] Cylinder930  label="servo-shaft"
  Angle = 360
  AttacherType = Attacher::AttachEngine3D
  Height = 31.25
  Placement = pos=(37,60,-8) rot=(1,0,0;1.5708rad)
  Radius = 2.5
FEATURE [Part::Cut] Cut688  label="servo-shaft-coupler"
  Placement = pos=(37,58.75,-14.35) rot=(1,0,0;1.5708rad)
  Refine = true
FEATURE [Part::MultiFuse] Fusion588  label="steering-servo"
  Placement = pos=(1,0,3) rot=(0,0,1;0rad)
  Refine = true
FEATURE [Part::Cut] Cut694  label="steering-servo-front-mount"
  Placement = pos=(0,0,3) rot=(0,0,1;0rad)
  Refine = true
FEATURE [Part::Fillet] Fillet357  label="steering-servo-rear-mount"
  Edges = 4 edges r=3: [Edge11,Edge13,Edge21,Edge23]
  Placement = pos=(1,0,3) rot=(0,0,1;0rad)
FEATURE [Part::Cut] Cut697  label="cross-member-front_"
  Placement = pos=(0,0,3) rot=(0,0,1;0rad)
  Refine = true
FEATURE [Part::Fillet] Fillet366  label="central-axle-left_lower-bar"
  Base = -> Fillet
  Edges = 6 edges r=0.75: [Edge10,Edge11,Edge12,Edge13,Edge24,Edge25]
  Placement = pos=(30.1998,4,99.6027) rot=(0,1,0;0.340339rad)
FEATURE [Part::MultiFuse] Fusion536  label="rear-prop-shaft"
  Placement = pos=(5,0,3) rot=(0,0,1;0rad)
  Refine = true
FEATURE [Part::Cylinder] Cylinder292
  Angle = 360
  AttacherType = Attacher::AttachEngine3D
  Height = 47
  Placement = pos=(166,0,-44) rot=(0,0,1;0rad)
  Radius = 14
FEATURE [Part::Fillet] Fillet333
  Base = -> Cylinder292
  Edges = 2 edges r=7: [Edge1,Edge3]
FEATURE [Part::Box] Box509  label="Cube711"
  AttacherType = Attacher::AttachEngine3D
  Height = 10
  Length = 32
  Placement = pos=(151,-16,2) rot=(0,0,1;0rad)
  Width = 32
FEATURE [Part::Box] Box510  label="Cube712"
  AttacherType = Attacher::AttachEngine3D
  Height = 10
  Length = 32
  Placement = pos=(151,-16,-53) rot=(0,0,1;0rad)
  Width = 32
FEATURE [Part::MultiFuse] Fusion596
  Refine = true
  Shapes = -> [Box510,Box509]
FEATURE [Part::Cut] Cut014102  label="Cut014242"
  Base = -> Fillet333
  Placement = pos=(7,31,0) rot=(0,0,1;0rad)
  Refine = true
  Tool = -> Fusion596
FEATURE [Part::Feature] Face046
  Placement = pos=(0,0,-2) rot=(0,0,1;0rad)
  shape: bbox 22.75 x 20.11 x 2e-07 mm, 1 faces, 0 solids (baked)
FEATURE [Part::Box] Box511  label="Cube713"
  AttacherType = Attacher::AttachEngine3D
  Height = 11
  Length = 10
  Placement = pos=(154,24,-10) rot=(0,0,1;0rad)
  Width = 14
FEATURE [Part::Fillet] Fillet369
  Base = -> Box511
  Edges = 4 edges r=4: [Edge9,Edge10,Edge11,Edge12]
  Placement = pos=(12.7075,4e-15,52.068) rot=(0,1,0;0.349066rad)
FEATURE [Part::Feature] Face047
  shape: bbox 15.41 x 11.89 x 2e-07 mm, 1 faces, 0 solids (baked)
FEATURE [Part::Feature] Face048
  shape: bbox 6.072 x 6.626 x 3.506 mm, 1 faces, 0 solids (baked)
FEATURE [Part::Loft] Loft013
  Closed = false
  MaxDegree = 5
  Placement = pos=(-0.5,0,0) rot=(0,0,1;0rad)
  Ruled = false
  Sections = -> [Face047,Face048]
  Solid = true
FEATURE [Part::Feature] Face049
  shape: bbox 4.139 x 15.4 x 11.37 mm, 1 faces, 0 solids (baked)
FEATURE [Part::Loft] Loft014
  Closed = false
  MaxDegree = 5
  Ruled = false
  Sections = -> [Face046,Face049]
  Solid = true
FEATURE [Part::MultiFuse] Fusion597
  Refine = true
  Shapes = -> [Fillet369,Cut014102,Loft014]
FEATURE [Part::Cut] Cut014103  label="Cut014375"
  Base = -> Fusion597
  Refine = true
  Tool = -> Loft013
FEATURE [Part::Cylinder] Cylinder293
  Angle = 360
  AttacherType = Attacher::AttachEngine3D
  Height = 39
  Placement = pos=(166,0,-40) rot=(0,0,1;0rad)
  Radius = 12
FEATURE [Part::Chamfer] Chamfer106
  Base = -> Cylinder293
  Edges = 2 edges r=7: [Edge1,Edge3]
  Placement = pos=(7,31,0) rot=(0,0,1;0rad)
FEATURE [Part::Cut] Cut014104  label="air-intake-lower-02"
  Base = -> Cut014103
  Placement = pos=(0.5,0,0) rot=(0,0,1;0rad)
  Refine = true
  Tool = -> Chamfer106
FEATURE [Part::Cylinder] Cylinder938  label="Cylinder1412"
  Angle = 360
  AttacherType = Attacher::AttachEngine3D
  Height = 10
  Placement = pos=(171,45,-2) rot=(0.994721,0.05438,0.087027;2.02933rad)
  Radius = 6
FEATURE [Part::Cylinder] Cylinder939  label="Cylinder1413"
  Angle = 360
  AttacherType = Attacher::AttachEngine3D
  Height = 23
  Placement = pos=(163,51,7) rot=(0,-1,0;1.36136rad)
  Radius = 6
FEATURE [Part::Cylinder] Cylinder940  label="Cylinder1414"
  Angle = 360
  AttacherType = Attacher::AttachEngine3D
  Height = 9
  Placement = pos=(167.5,31,-20) rot=(0,0,1;0rad)
  Radius = 14.1
FEATURE [Part::Cylinder] Cylinder941  label="Cylinder1415"
  Angle = 360
  AttacherType = Attacher::AttachEngine3D
  Height = 9
  Placement = pos=(167.5,31,-20) rot=(0,0,1;0rad)
  Radius = 15.1
FEATURE [Part::Cut] Cut014105  label="air-box-holder_001"
  Base = -> Cylinder941
  Placement = pos=(6,0,1) rot=(0,0,1;0rad)
  Refine = true
  Tool = -> Cylinder940
FEATURE [Part::Feature] Face050
  shape: bbox 3.676 x 13.23 x 17.3 mm, 1 faces, 0 solids (baked)
FEATURE [Part::Feature] Face051
  shape: bbox 17.79 x 7.863 x 12.24 mm, 1 faces, 0 solids (baked)
FEATURE [Part::Loft] Loft019
  Closed = false
  MaxDegree = 5
  Ruled = false
  Sections = -> [Face050,Face051]
  Solid = true
FEATURE [Part::MultiFuse] Fusion598
  Refine = true
  Shapes = -> [Cylinder939,Cylinder938,Loft019]
FEATURE [Part::Cylinder] Cylinder943  label="Cylinder1416"
  Angle = 360
  AttacherType = Attacher::AttachEngine3D
  Height = 15
  Placement = pos=(167.5,31,2) rot=(0,0,1;0rad)
  Radius = 13
FEATURE [Part::Cylinder] Cylinder944  label="Cylinder1417"
  Angle = 360
  AttacherType = Attacher::AttachEngine3D
  Height = 30
  Placement = pos=(167.5,31,-28) rot=(0,0,1;0rad)
  Radius = 14.1
FEATURE [Part::Fillet] Fillet370
  Base = -> Cylinder944
  Edges = 1 edges r=7: [Edge1]
  Placement = pos=(0,0,1) rot=(0,0,1;0rad)
FEATURE [Part::Cut] Cut014106  label="Cut014376"
  Base = -> Fillet370
  Placement = pos=(6,0,3) rot=(0,0,1;0rad)
  Refine = true
  Tool = -> Cylinder943
FEATURE [Part::Box] Box512  label="Cube714"
  AttacherType = Attacher::AttachEngine3D
  Height = 15
  Length = 10
  Placement = pos=(167,41.5,-19) rot=(0,0,1;0rad)
  Width = 12
FEATURE [Part::Cylinder] Cylinder945  label="Cylinder996"
  Angle = 360
  AttacherType = Attacher::AttachEngine3D
  Height = 15
  Placement = pos=(170.5,58,-9) rot=(1,0,0;1.5708rad)
  Radius = 1.6
FEATURE [Part::Cylinder] Cylinder946  label="Cylinder997"
  Angle = 360
  AttacherType = Attacher::AttachEngine3D
  Height = 5
  Placement = pos=(170.5,47,-9) rot=(1,0,0;1.5708rad)
  Radius = 3.2
FEATURE [Part::MultiFuse] Fusion599
  Placement = pos=(1,0,1) rot=(0,0,1;0rad)
  Refine = true
  Shapes = -> [Cylinder945,Cylinder946]
FEATURE [Part::Box] Box513  label="Cube715"
  AttacherType = Attacher::AttachEngine3D
  Height = 9.5
  Length = 1.5
  Placement = pos=(175.5,43.5,-19) rot=(0,0,1;0rad)
  Width = 13
FEATURE [Part::Box] Box514  label="Cube716"
  AttacherType = Attacher::AttachEngine3D
  Height = 9
  Length = 2
  Placement = pos=(177,45,-19) rot=(0,0,1;0rad)
  Width = 8
FEATURE [Part::Cylinder] Cylinder947  label="Cylinder998"
  Angle = 360
  AttacherType = Attacher::AttachEngine3D
  Height = 15
  Placement = pos=(165,49,-14.5) rot=(0,1,0;1.5708rad)
  Radius = 1
FEATURE [Part::Cylinder] Cylinder948  label="Cylinder1418"
  Angle = 360
  AttacherType = Attacher::AttachEngine3D
  Height = 1
  Placement = pos=(178,49,-14.5) rot=(0,1,0;1.5708rad)
  Radius = 2.5
FEATURE [Part::Box] Box515  label="Cube717"
  AttacherType = Attacher::AttachEngine3D
  Height = 3
  Length = 10
  Placement = pos=(166,44.5,-19) rot=(0,0,1;0rad)
  Width = 12
FEATURE [Part::Box] Box516  label="Cube718"
  AttacherType = Attacher::AttachEngine3D
  Height = 4
  Length = 10
  Placement = pos=(166,53.5,-18) rot=(0,0,1;0rad)
  Width = 4
FEATURE [Part::Fillet] Fillet371
  Base = -> Box516
  Edges = 1 edges r=3: [Edge9]
FEATURE [Part::Cut] Cut014108
  Base = -> Box515
  Placement = pos=(1,0,0) rot=(0,0,1;0rad)
  Refine = true
  Tool = -> Fillet371
FEATURE [Part::Cylinder] Cylinder942  label="Cylinder1419"
  Angle = 360
  AttacherType = Attacher::AttachEngine3D
  Height = 23
  Placement = pos=(163,51,10) rot=(0,-1,0;1.36136rad)
  Radius = 2.6
FEATURE [Part::Chamfer] Chamfer107
  Base = -> Fusion598
  Edges = 4 edges r=2.49: [Edge3,Edge4,Edge5,Edge8]
  Placement = pos=(0,0,3) rot=(0,0,1;0rad)
FEATURE [Part::Cylinder] Cylinder949  label="Cylinder1420"
  Angle = 360
  AttacherType = Attacher::AttachEngine3D
  Height = 18
  Placement = pos=(163,51,10) rot=(0,-1,0;1.36136rad)
  Radius = 2.6
FEATURE [Part::Cut] Cut014109  label="Cut014377"
  Base = -> Cylinder942
  Refine = true
  Tool = -> Cylinder949
FEATURE [Part::Cut] Cut014110  label="Cut014230"
  Base = -> Chamfer107
  Placement = pos=(0,0,-1.5) rot=(0,0,1;0rad)
  Refine = true
  Tool = -> Cut014109
FEATURE [Part::MultiFuse] Fusion601
  Refine = true
  Shapes = -> [Box512,Cut014105,Cut014108,Cut014110]
FEATURE [Part::MultiFuse] Fusion603
  Refine = true
  Shapes = -> [Cylinder948,Cylinder947]
FEATURE [Part::Cut] Cut014111
  Base = -> Fusion601
  Refine = true
  Tool = -> Cut014106
FEATURE [Part::Cut] Cut014112
  Base = -> Cut014111
  Refine = true
  Tool = -> Box513
FEATURE [Part::MultiFuse] Fusion604
  Refine = true
  Shapes = -> [Cut014112,Box514]
FEATURE [Part::Cut] Cut014113
  Base = -> Fusion604
  Refine = true
  Tool = -> Fusion599
FEATURE [Part::Cut] Cut014114
  Base = -> Cut014113
  Refine = true
  Tool = -> Fusion603
FEATURE [Part::Chamfer] Chamfer108  label="air-box-holder_"
  Base = -> Cut014114
  Edges = 1 edges r=1.49: [Edge70]
FEATURE [Part::Box] Box520  label="battery"
  AttacherType = Attacher::AttachEngine3D
  Height = 17
  Length = 72
  Placement = pos=(199,126.5,-56) rot=(0,0,1;0rad)
  Width = 34
FEATURE [Part::Box] Box517  label="Cube719"
  AttacherType = Attacher::AttachEngine3D
  Height = 49
  Length = 0.5
  Placement = pos=(195,122,-50.5) rot=(0,0,1;0rad)
  Width = 51
FEATURE [Part::Fillet] Fillet372
  Base = -> Box517
  Edges = 4 edges r=6: [Edge9,Edge10,Edge11,Edge12]
FEATURE [Part::Cylinder] Cylinder950  label="Cylinder1421"
  Angle = 360
  AttacherType = Attacher::AttachEngine3D
  Height = 2
  Placement = pos=(235,162,0) rot=(0,0,1;0rad)
  Radius = 6
FEATURE [Part::Cylinder] Cylinder951  label="Cylinder1422"
  Angle = 360
  AttacherType = Attacher::AttachEngine3D
  Height = 3
  Placement = pos=(235,162,-1) rot=(0,0,1;0rad)
  Radius = 5
FEATURE [Part::MultiFuse] Fusion605
  Refine = true
  Shapes = -> [Cylinder950,Cylinder951]
FEATURE [Part::Fillet] Fillet373
  Base = -> Fusion605
  Edges = 2 edges r=0.5: [Edge1,Edge3]
FEATURE [Part::Chamfer] Chamfer109
  Base = -> Fillet373
  Edges = 1 edges r=0.49: [Edge8]
FEATURE [Part::Box] Box518  label="Cube720"
  AttacherType = Attacher::AttachEngine3D
  Height = 50
  Length = 80
  Placement = pos=(195,121.5,-51) rot=(0,0,1;0rad)
  Width = 52
FEATURE [Part::Fillet] Fillet374
  Base = -> Box518
  Edges = 4 edges r=6: [Edge9,Edge10,Edge11,Edge12]
FEATURE [Part::Box] Box519  label="Cube721"
  AttacherType = Attacher::AttachEngine3D
  Height = 49
  Length = 0.5
  Placement = pos=(195,122,-50.5) rot=(0,0,1;0rad)
  Width = 51
FEATURE [Part::Fillet] Fillet375
  Base = -> Box519
  Edges = 4 edges r=6: [Edge9,Edge10,Edge11,Edge12]
  Placement = pos=(79.5,0,0) rot=(0,0,1;0rad)
FEATURE [Part::MultiFuse] Fusion606
  Refine = true
  Shapes = -> [Chamfer109,Fillet374]
FEATURE [Part::MultiFuse] Fusion607
  Refine = true
  Shapes = -> [Fillet375,Fillet372]
FEATURE [Part::Cut] Cut014115  label="Cut014173"
  Base = -> Fusion606
  Refine = true
  Tool = -> Fusion607
FEATURE [Part::Chamfer] Chamfer110
  Base = -> Cut014115
  Edges = 2 edges r=0.49: [Edge59,Edge78]
FEATURE [Part::Fillet] Fillet376  label="_tank-00"
  Base = -> Chamfer110
  Edges = 2 edges r=0.49: [Edge15,Edge48]
FEATURE [Part::Box] Box523  label="Cube724"
  AttacherType = Attacher::AttachEngine3D
  Height = 5
  Length = 8
  Placement = pos=(199,116.5,-53) rot=(0,0,1;0rad)
  Width = 55
FEATURE [Part::Box] Box527  label="Cube728"
  AttacherType = Attacher::AttachEngine3D
  Height = 4
  Length = 5.5
  Placement = pos=(200.25,165.5,-52) rot=(0,0,1;0rad)
  Width = 6
FEATURE [Part::Box] Box529  label="Cube730"
  AttacherType = Attacher::AttachEngine3D
  Height = 52
  Length = 5
  Placement = pos=(201,120.5,-48) rot=(0,0,1;0rad)
  Width = 54
FEATURE [Part::Box] Box530  label="Cube731"
  AttacherType = Attacher::AttachEngine3D
  Height = 50
  Length = 5
  Placement = pos=(201,121.5,-48) rot=(0,0,1;0rad)
  Width = 52
FEATURE [Part::Box] Box531  label="Cube732"
  AttacherType = Attacher::AttachEngine3D
  Height = 50
  Length = 5
  Placement = pos=(201,117.5,-50) rot=(0,0,1;0rad)
  Width = 51
FEATURE [Part::Fillet] Fillet377
  Base = -> Box530
  Edges = 4 edges r=6: [Edge9,Edge10,Edge11,Edge12]
FEATURE [Part::Fillet] Fillet378
  Base = -> Box529
  Edges = 4 edges r=7: [Edge9,Edge10,Edge11,Edge12]
  Placement = pos=(0,0,-1) rot=(0,0,1;0rad)
FEATURE [Part::Cylinder] Cylinder952  label="Cylinder1423"
  Angle = 360
  AttacherType = Attacher::AttachEngine3D
  Height = 5
  Placement = pos=(201,169,-50) rot=(0,1,0;1.5708rad)
  Radius = 2
FEATURE [Part::Cylinder] Cylinder953  label="Cylinder1424"
  Angle = 360
  AttacherType = Attacher::AttachEngine3D
  Height = 5
  Placement = pos=(201,169,-50) rot=(0,1,0;1.5708rad)
  Radius = 1.1
FEATURE [Part::Cylinder] Cylinder954  label="Cylinder1425"
  Angle = 360
  AttacherType = Attacher::AttachEngine3D
  Height = 8
  Placement = pos=(199,169,-50) rot=(0,1,0;1.5708rad)
  Radius = 1
FEATURE [Part::Box] Box533  label="Cube734"
  AttacherType = Attacher::AttachEngine3D
  Height = 2.5
  Length = 5
  Placement = pos=(201,116.5,0) rot=(0,0,1;0rad)
  Width = 10
FEATURE [Part::Box] Box539  label="Cube740"
  AttacherType = Attacher::AttachEngine3D
  Height = 50
  Length = 8
  Placement = pos=(199,116.5,-48) rot=(0,0,1;0rad)
  Width = 5
FEATURE [Part::Box] Box540  label="Cube741"
  AttacherType = Attacher::AttachEngine3D
  Height = 2.5
  Length = 5.5
  Placement = pos=(200.25,116.5,-0.5) rot=(0,0,1;0rad)
  Width = 5
FEATURE [Part::Cylinder] Cylinder962  label="Cylinder1426"
  Angle = 360
  AttacherType = Attacher::AttachEngine3D
  Height = 10
  Placement = pos=(203,119,-6.5) rot=(0,0,1;0rad)
  Radius = 1
FEATURE [Part::Cylinder] Cylinder963  label="Cylinder1427"
  Angle = 360
  AttacherType = Attacher::AttachEngine3D
  Height = 10
  Placement = pos=(203.5,119,-7.5) rot=(0,0,1;0rad)
  Radius = 1.2
FEATURE [Part::Box] Box541  label="Cube742"
  AttacherType = Attacher::AttachEngine3D
  Height = 44
  Length = 74
  Placement = pos=(198,124.5,-48) rot=(0,0,1;0rad)
  Width = 46
FEATURE [Part::Cylinder] Cylinder964  label="Cylinder1428"
  Angle = 360
  AttacherType = Attacher::AttachEngine3D
  Height = 15
  Placement = pos=(203,123,-8) rot=(1,0,0;1.5708rad)
  Radius = 1.6
FEATURE [Part::Cylinder] Cylinder965  label="Cylinder1429"
  Angle = 360
  AttacherType = Attacher::AttachEngine3D
  Height = 15
  Placement = pos=(267,123,-8) rot=(1,0,0;1.5708rad)
  Radius = 1.6
FEATURE [Part::Cylinder] Cylinder966  label="Cylinder1430"
  Angle = 360
  AttacherType = Attacher::AttachEngine3D
  Height = 2
  Placement = pos=(203,123,-8) rot=(1,0,0;1.5708rad)
  Radius = 3.1
FEATURE [Part::Cylinder] Cylinder967  label="Cylinder1431"
  Angle = 360
  AttacherType = Attacher::AttachEngine3D
  Height = 2
  Placement = pos=(267,123,-8) rot=(1,0,0;1.5708rad)
  Radius = 3.1
FEATURE [Part::MultiFuse] Fusion624
  Placement = pos=(0,2.5,0) rot=(0,0,1;0rad)
  Refine = true
  Shapes = -> [Cylinder964,Cylinder966,Cylinder967,Cylinder965]
FEATURE [Part::Box] Box554  label="Cube755"
  AttacherType = Attacher::AttachEngine3D
  Height = 15
  Length = 10
  Placement = pos=(210,118.5,-33) rot=(0,0,1;0rad)
  Width = 5
FEATURE [Part::Fillet] Fillet388
  Base = -> Box554
  Edges = 4 edges r=3: [Edge2,Edge4,Edge6,Edge8]
  Placement = pos=(0,1,0) rot=(0,0,1;0rad)
FEATURE [Part::Box] Box558  label="Cube759"
  AttacherType = Attacher::AttachEngine3D
  Height = 44
  Length = 80
  Placement = pos=(195,121.5,-52) rot=(0,0,1;0rad)
  Width = 52
FEATURE [Part::Box] Box559  label="Cube760"
  AttacherType = Attacher::AttachEngine3D
  Height = 10
  Length = 80
  Placement = pos=(195,121.5,-8) rot=(0,0,1;0rad)
  Width = 52
FEATURE [Part::Fillet] Fillet389
  Base = -> Box541
  Edges = 4 edges r=4: [Edge9,Edge10,Edge11,Edge12]
FEATURE [Part::Cut] Cut014116  label="tank-lower"
  Base = -> Fillet376
  Refine = true
  Tool = -> Fillet389
FEATURE [Part::Box] Box560  label="Cube761"
  AttacherType = Attacher::AttachEngine3D
  Height = 49
  Length = 0.5
  Placement = pos=(195,122,-50.5) rot=(0,0,1;0rad)
  Width = 51
FEATURE [Part::Fillet] Fillet390
  Base = -> Box560
  Edges = 4 edges r=6: [Edge9,Edge10,Edge11,Edge12]
FEATURE [Part::Cylinder] Cylinder971  label="Cylinder1432"
  Angle = 360
  AttacherType = Attacher::AttachEngine3D
  Height = 2
  Placement = pos=(235,162,0) rot=(0,0,1;0rad)
  Radius = 6
FEATURE [Part::Cylinder] Cylinder972  label="Cylinder1433"
  Angle = 360
  AttacherType = Attacher::AttachEngine3D
  Height = 3
  Placement = pos=(235,162,-1) rot=(0,0,1;0rad)
  Radius = 5
FEATURE [Part::MultiFuse] Fusion630
  Refine = true
  Shapes = -> [Cylinder971,Cylinder972]
FEATURE [Part::Fillet] Fillet391
  Base = -> Fusion630
  Edges = 2 edges r=0.5: [Edge1,Edge3]
FEATURE [Part::Chamfer] Chamfer117
  Base = -> Fillet391
  Edges = 1 edges r=0.49: [Edge8]
FEATURE [Part::Box] Box561  label="Cube762"
  AttacherType = Attacher::AttachEngine3D
  Height = 50
  Length = 80
  Placement = pos=(195,121.5,-51) rot=(0,0,1;0rad)
  Width = 52
FEATURE [Part::Fillet] Fillet392
  Base = -> Box561
  Edges = 4 edges r=6: [Edge9,Edge10,Edge11,Edge12]
FEATURE [Part::Box] Box562  label="Cube763"
  AttacherType = Attacher::AttachEngine3D
  Height = 49
  Length = 0.5
  Placement = pos=(195,122,-50.5) rot=(0,0,1;0rad)
  Width = 51
FEATURE [Part::Fillet] Fillet393
  Base = -> Box562
  Edges = 4 edges r=6: [Edge9,Edge10,Edge11,Edge12]
  Placement = pos=(79.5,0,0) rot=(0,0,1;0rad)
FEATURE [Part::MultiFuse] Fusion631
  Refine = true
  Shapes = -> [Chamfer117,Fillet392]
FEATURE [Part::MultiFuse] Fusion632
  Refine = true
  Shapes = -> [Fillet393,Fillet390]
FEATURE [Part::Cut] Cut014136  label="Cut014168"
  Base = -> Fusion631
  Refine = true
  Tool = -> Fusion632
FEATURE [Part::Chamfer] Chamfer118
  Base = -> Cut014136
  Edges = 2 edges r=0.49: [Edge59,Edge78]
FEATURE [Part::Fillet] Fillet394  label="_tank-001"
  Base = -> Chamfer118
  Edges = 2 edges r=0.49: [Edge15,Edge48]
FEATURE [Part::Box] Box563  label="Cube764"
  AttacherType = Attacher::AttachEngine3D
  Height = 44
  Length = 74
  Placement = pos=(198,124.5,-48) rot=(0,0,1;0rad)
  Width = 46
FEATURE [Part::Fillet] Fillet395
  Base = -> Box563
  Edges = 4 edges r=4: [Edge9,Edge10,Edge11,Edge12]
FEATURE [Part::Cut] Cut014137  label="tank_upper"
  Base = -> Fillet394
  Refine = true
  Tool = -> Fillet395
FEATURE [Part::Cut] Cut014138  label="Cut014174"
  Base = -> Cut014137
  Placement = pos=(0,0,3) rot=(0,0,1;0rad)
  Refine = true
  Tool = -> Box558
FEATURE [Part::Cut] Cut014139  label="Cut014231"
  Base = -> Cut014116
  Placement = pos=(0,0,3) rot=(0,0,1;0rad)
  Refine = true
  Tool = -> Box559
FEATURE [Part::Cut] Cut014140  label="Cut014232"
  Base = -> Cut014139
  Refine = true
  Tool = -> Fillet388
FEATURE [Part::Box] Box564  label="Cube765"
  AttacherType = Attacher::AttachEngine3D
  Height = 2
  Length = 76
  Placement = pos=(197,123.5,-5) rot=(0,0,1;0rad)
  Width = 48
FEATURE [Part::Box] Box565  label="Cube766"
  AttacherType = Attacher::AttachEngine3D
  Height = 2
  Length = 74
  Placement = pos=(198,124.5,-5) rot=(0,0,1;0rad)
  Width = 46
FEATURE [Part::Cut] Cut014141  label="Cut014233"
  Base = -> Box564
  Refine = true
  Tool = -> Box565
FEATURE [Part::Box] Box566  label="Cube767"
  AttacherType = Attacher::AttachEngine3D
  Height = 2
  Length = 77
  Placement = pos=(196.5,123,-5) rot=(0,0,1;0rad)
  Width = 49
FEATURE [Part::Box] Box567  label="Cube768"
  AttacherType = Attacher::AttachEngine3D
  Height = 2
  Length = 72
  Placement = pos=(199,125.5,-5) rot=(0,0,1;0rad)
  Width = 44
FEATURE [Part::Cut] Cut014142  label="Cut014246"
  Base = -> Box566
  Refine = true
  Tool = -> Box567
FEATURE [Part::Fillet] Fillet396
  Base = -> Cut014142
  Edges = 4 edges r=2.5: [Edge1,Edge3,Edge6,Edge15]
FEATURE [Part::Fillet] Fillet397
  Base = -> Cut014141
  Edges = 4 edges r=2: [Edge1,Edge3,Edge6,Edge15]
FEATURE [Part::MultiFuse] Fusion633  label="_tank-lower-03"
  Refine = true
  Shapes = -> [Cut014140,Fillet397]
FEATURE [Part::Cut] Cut014143  label="fuel-tank-upper"
  Base = -> Cut014138
  Refine = true
  Tool = -> Fillet396
FEATURE [Part::Cylinder] Cylinder973  label="Cylinder1434"
  Angle = 360
  AttacherType = Attacher::AttachEngine3D
  Height = 15
  Placement = pos=(203,123,-8) rot=(1,0,0;1.5708rad)
  Radius = 1.6
FEATURE [Part::Cut] Cut014148  label="_tank-lower-04"
  Base = -> Fusion633
  Refine = true
  Tool = -> Fusion624
FEATURE [Part::Cylinder] Cylinder975  label="Cylinder1435"
  Angle = 360
  AttacherType = Attacher::AttachEngine3D
  Height = 15
  Placement = pos=(203,132,-59) rot=(0,0,1;0rad)
  Radius = 1.2
FEATURE [Part::Cylinder] Cylinder976  label="Cylinder1436"
  Angle = 360
  AttacherType = Attacher::AttachEngine3D
  Height = 15
  Placement = pos=(203,163,-59) rot=(0,0,1;0rad)
  Radius = 1.2
FEATURE [Part::Cylinder] Cylinder977  label="Cylinder1437"
  Angle = 360
  AttacherType = Attacher::AttachEngine3D
  Height = 15
  Placement = pos=(267,163,-59) rot=(0,0,1;0rad)
  Radius = 1.2
FEATURE [Part::Cylinder] Cylinder978  label="Cylinder1438"
  Angle = 360
  AttacherType = Attacher::AttachEngine3D
  Height = 15
  Placement = pos=(267,132,-59) rot=(0,0,1;0rad)
  Radius = 1.2
FEATURE [Part::MultiFuse] Fusion637
  Refine = true
  Shapes = -> [Cylinder975,Cylinder978,Cylinder976,Cylinder977]
FEATURE [Part::Cylinder] Cylinder979  label="Cylinder1439"
  Angle = 360
  AttacherType = Attacher::AttachEngine3D
  Height = 15
  Placement = pos=(203,132,-59) rot=(0,0,1;0rad)
  Radius = 0.9
FEATURE [Part::Cylinder] Cylinder980  label="Cylinder1440"
  Angle = 360
  AttacherType = Attacher::AttachEngine3D
  Height = 15
  Placement = pos=(203,163,-59) rot=(0,0,1;0rad)
  Radius = 0.9
FEATURE [Part::Cut] Cut014149  label="_tank-lower-05"
  Base = -> Cut014148
  Refine = true
  Tool = -> Fusion637
FEATURE [Part::Cylinder] Cylinder983  label="Cylinder1441"
  Angle = 360
  AttacherType = Attacher::AttachEngine3D
  Height = 15
  Placement = pos=(203,123,-8) rot=(1,0,0;1.5708rad)
  Radius = 3
FEATURE [Part::Cylinder] Cylinder984  label="Cylinder1442"
  Angle = 360
  AttacherType = Attacher::AttachEngine3D
  Height = 15
  Placement = pos=(267,123,-8) rot=(1,0,0;1.5708rad)
  Radius = 3
FEATURE [Part::MultiFuse] Fusion640
  Placement = pos=(0,54,6) rot=(0,0,1;0rad)
  Refine = true
  Shapes = -> [Cylinder983,Cylinder984]
FEATURE [Part::Cut] Cut014152  label="fuel-tank-lower"
  Base = -> Cut014149
  Refine = true
  Tool = -> Fusion640
FEATURE [Part::Cut] Cut014157  label="Cut014247"
  Base = -> Box523
  Refine = true
  Tool = -> Box527
FEATURE [Part::Cut] Cut014158  label="Cut014378"
  Base = -> Box539
  Refine = true
  Tool = -> Box540
FEATURE [Part::MultiFuse] Fusion643
  Refine = true
  Shapes = -> [Cylinder962,Cylinder954,Cylinder979,Cylinder980,Cylinder973]
FEATURE [Part::MultiFuse] Fusion644
  Refine = true
  Shapes = -> [Cut014157,Cut014158]
FEATURE [Part::Cut] Cut014159  label="Cut014379"
  Base = -> Fusion644
  Refine = true
  Tool = -> Fusion643
FEATURE [Part::Fillet] Fillet404
  Base = -> Cut014159
  Edges = 1 edges r=8: [Edge3]
FEATURE [Part::Fillet] Fillet405  label="fuel-tank-holder-front"
  Base = -> Fillet404
  Edges = 1 edges r=5: [Edge40]
FEATURE [Part::Box] Box570  label="Cube771"
  AttacherType = Attacher::AttachEngine3D
  Height = 5
  Length = 8
  Placement = pos=(199,116.5,-53) rot=(0,0,1;0rad)
  Width = 55
FEATURE [Part::Box] Box571  label="Cube772"
  AttacherType = Attacher::AttachEngine3D
  Height = 4
  Length = 5.5
  Placement = pos=(200.25,165.5,-52) rot=(0,0,1;0rad)
  Width = 6
FEATURE [Part::Cylinder] Cylinder985  label="Cylinder1443"
  Angle = 360
  AttacherType = Attacher::AttachEngine3D
  Height = 8
  Placement = pos=(199,169,-50) rot=(0,1,0;1.5708rad)
  Radius = 1
FEATURE [Part::Box] Box572  label="Cube773"
  AttacherType = Attacher::AttachEngine3D
  Height = 50
  Length = 8
  Placement = pos=(199,116.5,-48) rot=(0,0,1;0rad)
  Width = 5
FEATURE [Part::Box] Box573  label="Cube774"
  AttacherType = Attacher::AttachEngine3D
  Height = 2.5
  Length = 5.5
  Placement = pos=(200.25,116.5,-0.5) rot=(0,0,1;0rad)
  Width = 5
FEATURE [Part::Cylinder] Cylinder986  label="Cylinder1444"
  Angle = 360
  AttacherType = Attacher::AttachEngine3D
  Height = 10
  Placement = pos=(203,119,-6.5) rot=(0,0,1;0rad)
  Radius = 1
FEATURE [Part::Cylinder] Cylinder987  label="Cylinder1445"
  Angle = 360
  AttacherType = Attacher::AttachEngine3D
  Height = 15
  Placement = pos=(203,123,-8) rot=(1,0,0;1.5708rad)
  Radius = 1.6
FEATURE [Part::Cylinder] Cylinder988  label="Cylinder1446"
  Angle = 360
  AttacherType = Attacher::AttachEngine3D
  Height = 15
  Placement = pos=(203,132,-59) rot=(0,0,1;0rad)
  Radius = 0.9
FEATURE [Part::Cylinder] Cylinder989  label="Cylinder1447"
  Angle = 360
  AttacherType = Attacher::AttachEngine3D
  Height = 15
  Placement = pos=(203,163,-59) rot=(0,0,1;0rad)
  Radius = 0.9
FEATURE [Part::Cut] Cut014160  label="Cut014380"
  Base = -> Box570
  Refine = true
  Tool = -> Box571
FEATURE [Part::Cut] Cut014161  label="Cut014314"
  Base = -> Box572
  Refine = true
  Tool = -> Box573
FEATURE [Part::MultiFuse] Fusion645
  Refine = true
  Shapes = -> [Cylinder986,Cylinder985,Cylinder988,Cylinder989,Cylinder987]
FEATURE [Part::MultiFuse] Fusion646
  Refine = true
  Shapes = -> [Cut014160,Cut014161]
FEATURE [Part::Cut] Cut014162  label="Cut014381"
  Base = -> Fusion646
  Refine = true
  Tool = -> Fusion645
FEATURE [Part::Fillet] Fillet406
  Base = -> Cut014162
  Edges = 1 edges r=8: [Edge3]
FEATURE [Part::Fillet] Fillet407  label="fuel-tank-holder-rear"
  Base = -> Fillet406
  Edges = 1 edges r=5: [Edge40]
  Placement = pos=(64,0,0) rot=(0,0,1;0rad)
FEATURE [Part::Cut] Cut014163  label="Cut014382"
  Base = -> Fillet378
  Refine = true
  Tool = -> Box531
FEATURE [Part::MultiFuse] Fusion647
  Refine = true
  Shapes = -> [Cut014163,Box533,Cylinder952]
FEATURE [Part::Cut] Cut014164
  Base = -> Fusion647
  Placement = pos=(-0.5,0,0) rot=(0,0,1;0rad)
  Refine = true
  Tool = -> Fillet377
FEATURE [Part::MultiFuse] Fusion648
  Placement = pos=(-0.5,0,0) rot=(0,0,1;0rad)
  Refine = true
  Shapes = -> [Cylinder953,Cylinder963]
FEATURE [Part::Cut] Cut014169
  Base = -> Cut014164
  Refine = true
  Tool = -> Fusion648
FEATURE [Part::Chamfer] Chamfer119  label="fuel-tank-lace-front"
  Base = -> Cut014169
  Edges = 1 edges r=0.145: [Edge4]
FEATURE [Part::Box] Box574  label="Cube775"
  AttacherType = Attacher::AttachEngine3D
  Height = 52
  Length = 5
  Placement = pos=(201,120.5,-48) rot=(0,0,1;0rad)
  Width = 54
FEATURE [Part::Box] Box575  label="Cube776"
  AttacherType = Attacher::AttachEngine3D
  Height = 50
  Length = 5
  Placement = pos=(201,121.5,-48) rot=(0,0,1;0rad)
  Width = 52
FEATURE [Part::Box] Box576  label="Cube777"
  AttacherType = Attacher::AttachEngine3D
  Height = 50
  Length = 5
  Placement = pos=(201,117.5,-50) rot=(0,0,1;0rad)
  Width = 51
FEATURE [Part::Fillet] Fillet408
  Base = -> Box575
  Edges = 4 edges r=6: [Edge9,Edge10,Edge11,Edge12]
FEATURE [Part::Fillet] Fillet409
  Base = -> Box574
  Edges = 4 edges r=7: [Edge9,Edge10,Edge11,Edge12]
  Placement = pos=(0,0,-1) rot=(0,0,1;0rad)
FEATURE [Part::Cylinder] Cylinder990  label="Cylinder1448"
  Angle = 360
  AttacherType = Attacher::AttachEngine3D
  Height = 5
  Placement = pos=(201,169,-50) rot=(0,1,0;1.5708rad)
  Radius = 2
FEATURE [Part::Cylinder] Cylinder991  label="Cylinder1449"
  Angle = 360
  AttacherType = Attacher::AttachEngine3D
  Height = 5
  Placement = pos=(201,169,-50) rot=(0,1,0;1.5708rad)
  Radius = 1.1
FEATURE [Part::Box] Box577  label="Cube778"
  AttacherType = Attacher::AttachEngine3D
  Height = 2.5
  Length = 5
  Placement = pos=(201,116.5,0) rot=(0,0,1;0rad)
  Width = 10
FEATURE [Part::Cylinder] Cylinder992  label="Cylinder1450"
  Angle = 360
  AttacherType = Attacher::AttachEngine3D
  Height = 10
  Placement = pos=(203.5,119,-7.5) rot=(0,0,1;0rad)
  Radius = 1.2
FEATURE [Part::Cut] Cut014170  label="Cut014383"
  Base = -> Fillet409
  Refine = true
  Tool = -> Box576
FEATURE [Part::MultiFuse] Fusion649
  Refine = true
  Shapes = -> [Cut014170,Box577,Cylinder990]
FEATURE [Part::Cut] Cut014171
  Base = -> Fusion649
  Placement = pos=(-0.5,0,0) rot=(0,0,1;0rad)
  Refine = true
  Tool = -> Fillet408
FEATURE [Part::MultiFuse] Fusion650
  Placement = pos=(-0.5,0,0) rot=(0,0,1;0rad)
  Refine = true
  Shapes = -> [Cylinder991,Cylinder992]
FEATURE [Part::Cut] Cut014172
  Base = -> Cut014171
  Refine = true
  Tool = -> Fusion650
FEATURE [Part::Chamfer] Chamfer120  label="fuel-tank-lace-rear"
  Base = -> Cut014172
  Edges = 1 edges r=0.145: [Edge4]
  Placement = pos=(64,0,0) rot=(0,0,1;0rad)
FEATURE [Part::Box] Box578  label="Cube081"
  AttacherType = Attacher::AttachEngine3D
  Height = 22
  Length = 45
  Placement = pos=(200,8.5,-20) rot=(0,0,1;0rad)
  Width = 45
FEATURE [Part::Box] Box579  label="Cube082"
  AttacherType = Attacher::AttachEngine3D
  Height = 20
  Length = 42
  Placement = pos=(201.5,8.5,-18) rot=(0,0,1;0rad)
  Width = 41
FEATURE [Part::Box] Box581  label="Cube090"
  AttacherType = Attacher::AttachEngine3D
  Height = 5
  Length = 45
  Placement = pos=(200,8.5,-20) rot=(0,0,1;0rad)
  Width = 1.5
FEATURE [Part::Cylinder] Cylinder993  label="Cylinder1451"
  Angle = 360
  AttacherType = Attacher::AttachEngine3D
  Height = 65
  Placement = pos=(190,51.5,0) rot=(0,1,0;1.5708rad)
  Radius = 0.55
FEATURE [Part::Cylinder] Cylinder994  label="Cylinder1452"
  Angle = 360
  AttacherType = Attacher::AttachEngine3D
  Height = 10
  Placement = pos=(261,1,10) rot=(1,0,0;1.5708rad)
  Radius = 1.6
FEATURE [Part::Cylinder] Cylinder995  label="Cylinder1453"
  Angle = 360
  AttacherType = Attacher::AttachEngine3D
  Height = 10
  Placement = pos=(294,1,10) rot=(1,0,0;1.5708rad)
  Radius = 1.6
FEATURE [Part::MultiFuse] Fusion653
  Placement = pos=(-55,55,-18) rot=(0,0,1;0rad)
  Refine = true
  Shapes = -> [Cylinder994,Cylinder995]
FEATURE [Part::Box] Box587  label="Cube092"
  AttacherType = Attacher::AttachEngine3D
  Height = 22.5
  Length = 48
  Placement = pos=(198.5,7,-19) rot=(0,0,1;0rad)
  Width = 45.5
FEATURE [Part::Cut] Cut014175  label="Cut014384"
  Base = -> Box578
  Refine = true
  Tool = -> Box579
FEATURE [Part::MultiFuse] Fusion656
  Refine = true
  Shapes = -> [Cut014175,Box581]
FEATURE [Part::MultiFuse] Fusion657
  Refine = true
  Shapes = -> [Fusion653,Cylinder993]
FEATURE [Part::Cut] Cut014176  label="Cut014385"
  Base = -> Fusion656
  Refine = true
  Tool = -> Fusion657
FEATURE [Part::Fillet] Fillet410
  Base = -> Cut014176
  Edges = 2 edges r=8: [Edge3,Edge7]
FEATURE [Part::Cylinder] Cylinder999  label="Cylinder1454"
  Angle = 360
  AttacherType = Attacher::AttachEngine3D
  Height = 65
  Placement = pos=(190,51.5,0) rot=(0,1,0;1.5708rad)
  Radius = 0.55
FEATURE [Part::Box] Box588  label="Cube779"
  AttacherType = Attacher::AttachEngine3D
  Height = 22.5
  Length = 46
  Placement = pos=(199.5,8,-20) rot=(0,0,1;0rad)
  Width = 46.5
FEATURE [Part::Fillet] Fillet411
  Base = -> Box588
  Edges = 1 edges r=8: [Edge10]
FEATURE [Part::Cut] Cut014177  label="Cut014386"
  Base = -> Box587
  Refine = true
  Tool = -> Fillet411
FEATURE [Part::Fillet] Fillet412
  Base = -> Cut014177
  Edges = 1 edges r=9: [Edge7]
FEATURE [Part::Box] Box589  label="Cube780"
  AttacherType = Attacher::AttachEngine3D
  Height = 22.5
  Length = 48
  Placement = pos=(198.5,10,-22) rot=(0,0,1;0rad)
  Width = 45.5
FEATURE [Part::Fillet] Fillet413
  Base = -> Box589
  Edges = 1 edges r=8: [Edge10]
FEATURE [Part::Cut] Cut014178  label="Cut014387"
  Base = -> Fillet412
  Refine = true
  Tool = -> Fillet413
FEATURE [Part::Chamfer] Chamfer121
  Base = -> Cut014178
  Edges = 2 edges r=2: [Edge24,Edge29]
FEATURE [Part::Cylinder] Cylinder1000  label="Cylinder1455"
  Angle = 360
  AttacherType = Attacher::AttachEngine3D
  Height = 1
  Placement = pos=(245.5,51.5,0) rot=(0,1,0;1.5708rad)
  Radius = 2
FEATURE [Part::Fillet] Fillet414
  Base = -> Fillet410
  Edges = 1 edges r=3: [Edge3]
FEATURE [Part::Cylinder] Cylinder1001  label="Cylinder1456"
  Angle = 360
  AttacherType = Attacher::AttachEngine3D
  Height = 1
  Placement = pos=(198.5,51.5,0) rot=(0,1,0;1.5708rad)
  Radius = 2
FEATURE [Part::MultiFuse] Fusion658
  Refine = true
  Shapes = -> [Cylinder1000,Cylinder1001,Chamfer121]
FEATURE [Part::Chamfer] Chamfer122
  Base = -> Fusion658
  Edges = 2 edges r=0.75: [Edge22,Edge25]
FEATURE [Part::Cut] Cut014179  label="battery-box-cover"
  Base = -> Chamfer122
  Placement = pos=(3.45,0,0) rot=(0,0,1;0rad)
  Refine = true
  Tool = -> Cylinder999
FEATURE [Part::Cylinder] Cylinder1002  label="Cylinder1457"
  Angle = 360
  AttacherType = Attacher::AttachEngine3D
  Height = 15
  Placement = pos=(198.5,48,-8) rot=(1,0,0;1.5708rad)
  Radius = 2
FEATURE [Part::Cylinder] Cylinder1003  label="Cylinder1458"
  Angle = 360
  AttacherType = Attacher::AttachEngine3D
  Height = 15
  Placement = pos=(198.5,30,-8) rot=(1,0,0;1.5708rad)
  Radius = 2
FEATURE [Part::MultiFuse] Fusion659
  Refine = true
  Shapes = -> [Cylinder1002,Cylinder1003]
FEATURE [Part::Fillet] Fillet415
  Base = -> Fusion659
  Edges = 4 edges r=2: [Edge1,Edge3,Edge4,Edge6]
FEATURE [Part::Cylinder] Cylinder1004  label="Cylinder1459"
  Angle = 360
  AttacherType = Attacher::AttachEngine3D
  Height = 15
  Placement = pos=(198.5,48,-8) rot=(1,0,0;1.5708rad)
  Radius = 2
FEATURE [Part::Cylinder] Cylinder1005  label="Cylinder1460"
  Angle = 360
  AttacherType = Attacher::AttachEngine3D
  Height = 15
  Placement = pos=(198.5,30,-8) rot=(1,0,0;1.5708rad)
  Radius = 2
FEATURE [Part::MultiFuse] Fusion660
  Refine = true
  Shapes = -> [Cylinder1004,Cylinder1005]
FEATURE [Part::Fillet] Fillet416
  Base = -> Fusion660
  Edges = 4 edges r=2: [Edge1,Edge3,Edge4,Edge6]
  Placement = pos=(48,0,0) rot=(0,0,1;0rad)
FEATURE [Part::MultiFuse] Fusion661
  Placement = pos=(0,0,-2) rot=(0,0,1;0rad)
  Refine = true
  Shapes = -> [Fillet415,Fillet416]
FEATURE [Part::Cylinder] Cylinder1006  label="Cylinder1461"
  Angle = 360
  AttacherType = Attacher::AttachEngine3D
  Height = 50
  Placement = pos=(198,36,-31) rot=(0,1,0;1.5708rad)
  Radius = 11
FEATURE [Part::Cone] Cone018
  Angle = 360
  AttacherType = Attacher::AttachEngine3D
  Height = 3
  Placement = pos=(195,36,-31) rot=(0,1,0;1.5708rad)
  Radius1 = 4
  Radius2 = 11
FEATURE [Part::Cone] Cone019
  Angle = 360
  AttacherType = Attacher::AttachEngine3D
  Height = 3
  Placement = pos=(248,36,-31) rot=(0,1,0;1.5708rad)
  Radius1 = 11
  Radius2 = 4
FEATURE [Part::MultiFuse] Fusion662
  Refine = true
  Shapes = -> [Cylinder1006,Cone019,Cone018]
FEATURE [Part::Fillet] Fillet417
  Base = -> Fusion662
  Edges = 2 edges r=2: [Edge3,Edge5]
FEATURE [Part::Fillet] Fillet418
  Base = -> Fillet417
  Edges = 2 edges r=3: [Edge3,Edge11]
  Placement = pos=(0,7,0) rot=(0,0,1;0rad)
FEATURE [Part::Cylinder] Cylinder1007  label="Cylinder1462"
  Angle = 360
  AttacherType = Attacher::AttachEngine3D
  Height = 50
  Placement = pos=(198,36,-31) rot=(0,1,0;1.5708rad)
  Radius = 11
FEATURE [Part::Cone] Cone020
  Angle = 360
  AttacherType = Attacher::AttachEngine3D
  Height = 3
  Placement = pos=(195,36,-31) rot=(0,1,0;1.5708rad)
  Radius1 = 4
  Radius2 = 11
FEATURE [Part::Cone] Cone021
  Angle = 360
  AttacherType = Attacher::AttachEngine3D
  Height = 3
  Placement = pos=(248,36,-31) rot=(0,1,0;1.5708rad)
  Radius1 = 11
  Radius2 = 4
FEATURE [Part::MultiFuse] Fusion663
  Refine = true
  Shapes = -> [Cylinder1007,Cone021,Cone020]
FEATURE [Part::Fillet] Fillet419
  Base = -> Fusion663
  Edges = 2 edges r=2: [Edge3,Edge5]
FEATURE [Part::Fillet] Fillet420
  Base = -> Fillet419
  Edges = 2 edges r=3: [Edge3,Edge11]
  Placement = pos=(0,-17,0) rot=(0,0,1;0rad)
FEATURE [Part::Box] Box591  label="Cube782"
  AttacherType = Attacher::AttachEngine3D
  Height = 24
  Length = 4
  Placement = pos=(201.5,7,-43) rot=(0,0,1;0rad)
  Width = 48
FEATURE [Part::Box] Box592  label="Cube783"
  AttacherType = Attacher::AttachEngine3D
  Height = 22
  Length = 4
  Placement = pos=(201.5,8,-42) rot=(0,0,1;0rad)
  Width = 46
FEATURE [Part::Box] Box593  label="Cube784"
  AttacherType = Attacher::AttachEngine3D
  Height = 1
  Length = 4
  Placement = pos=(201.5,7,-20) rot=(0,0,1;0rad)
  Width = 48
FEATURE [Part::Fillet] Fillet421
  Base = -> Box592
  Edges = 4 edges r=10.99: [Edge9,Edge10,Edge11,Edge12]
FEATURE [Part::Fillet] Fillet422
  Base = -> Box591
  Edges = 4 edges r=11.99: [Edge9,Edge10,Edge11,Edge12]
FEATURE [Part::MultiFuse] Fusion664
  Refine = true
  Shapes = -> [Fillet421,Box593]
FEATURE [Part::Cut] Cut014181  label="Cut014388"
  Base = -> Fillet422
  Refine = true
  Tool = -> Fusion664
FEATURE [Part::Box] Box594  label="Cube785"
  AttacherType = Attacher::AttachEngine3D
  Height = 24
  Length = 4
  Placement = pos=(201.5,7,-43) rot=(0,0,1;0rad)
  Width = 48
FEATURE [Part::Box] Box595  label="Cube786"
  AttacherType = Attacher::AttachEngine3D
  Height = 22
  Length = 4
  Placement = pos=(201.5,8,-42) rot=(0,0,1;0rad)
  Width = 46
FEATURE [Part::Box] Box596  label="Cube787"
  AttacherType = Attacher::AttachEngine3D
  Height = 1
  Length = 4
  Placement = pos=(201.5,7,-20) rot=(0,0,1;0rad)
  Width = 48
FEATURE [Part::Fillet] Fillet423
  Base = -> Box595
  Edges = 4 edges r=10.99: [Edge9,Edge10,Edge11,Edge12]
FEATURE [Part::Fillet] Fillet424
  Base = -> Box594
  Edges = 4 edges r=11.99: [Edge9,Edge10,Edge11,Edge12]
FEATURE [Part::MultiFuse] Fusion665
  Refine = true
  Shapes = -> [Fillet423,Box596]
FEATURE [Part::Cut] Cut014182  label="Cut014389"
  Base = -> Fillet424
  Placement = pos=(38,0,0) rot=(0,0,1;0rad)
  Refine = true
  Tool = -> Fusion665
FEATURE [Part::Cylinder] Cylinder1008  label="Cylinder1463"
  Angle = 360
  AttacherType = Attacher::AttachEngine3D
  Height = 15
  Placement = pos=(203.5,45.5,-30) rot=(0,0,1;0rad)
  Radius = 1.2
FEATURE [Part::Cylinder] Cylinder1009  label="Cylinder1464"
  Angle = 360
  AttacherType = Attacher::AttachEngine3D
  Height = 15
  Placement = pos=(203.5,16.5,-30) rot=(0,0,1;0rad)
  Radius = 1.2
FEATURE [Part::Cylinder] Cylinder1010  label="Cylinder1465"
  Angle = 360
  AttacherType = Attacher::AttachEngine3D
  Height = 15
  Placement = pos=(241.5,45.5,-30) rot=(0,0,1;0rad)
  Radius = 1.2
FEATURE [Part::Cylinder] Cylinder1011  label="Cylinder1466"
  Angle = 360
  AttacherType = Attacher::AttachEngine3D
  Height = 15
  Placement = pos=(241.5,16.5,-30) rot=(0,0,1;0rad)
  Radius = 1.2
FEATURE [Part::MultiFuse] Fusion666
  Refine = true
  Shapes = -> [Cylinder1008,Cylinder1010,Cylinder1011,Cylinder1009]
FEATURE [Part::Cylinder] Cylinder1012  label="Cylinder1467"
  Angle = 360
  AttacherType = Attacher::AttachEngine3D
  Height = 15
  Placement = pos=(203.5,45.5,-30) rot=(0,0,1;0rad)
  Radius = 0.9
FEATURE [Part::Cylinder] Cylinder1013  label="Cylinder1468"
  Angle = 360
  AttacherType = Attacher::AttachEngine3D
  Height = 15
  Placement = pos=(203.5,16.5,-30) rot=(0,0,1;0rad)
  Radius = 0.9
FEATURE [Part::Cylinder] Cylinder1014  label="Cylinder1469"
  Angle = 360
  AttacherType = Attacher::AttachEngine3D
  Height = 15
  Placement = pos=(241.5,45.5,-30) rot=(0,0,1;0rad)
  Radius = 0.9
FEATURE [Part::Cylinder] Cylinder1015  label="Cylinder1470"
  Angle = 360
  AttacherType = Attacher::AttachEngine3D
  Height = 15
  Placement = pos=(241.5,16.5,-30) rot=(0,0,1;0rad)
  Radius = 0.9
FEATURE [Part::MultiFuse] Fusion667
  Refine = true
  Shapes = -> [Cylinder1012,Cylinder1014,Cylinder1015,Cylinder1013]
FEATURE [Part::MultiFuse] Fusion668
  Refine = true
  Shapes = -> [Fillet418,Fillet420,Cut014181,Cut014182]
FEATURE [Part::Cut] Cut014183  label="Cut014390"
  Base = -> Fusion668
  Refine = true
  Tool = -> Fusion667
FEATURE [Part::Cut] Cut014184  label="Cut014391"
  Base = -> Fillet414
  Refine = true
  Tool = -> Fusion661
FEATURE [Part::Cut] Cut014185  label="battery-box"
  Base = -> Cut014184
  Placement = pos=(3.5,0,0) rot=(0,0,1;0rad)
  Refine = true
  Tool = -> Fusion666
FEATURE [Part::Cylinder] Cylinder1016  label="Cylinder1471"
  Angle = 360
  AttacherType = Attacher::AttachEngine3D
  Height = 50
  Placement = pos=(198,43,-31) rot=(0,1,0;1.5708rad)
  Radius = 9
FEATURE [Part::Chamfer] Chamfer123
  Base = -> Cylinder1016
  Edges = 2 edges r=2: [Edge1,Edge3]
FEATURE [Part::Cylinder] Cylinder1017  label="Cylinder1472"
  Angle = 360
  AttacherType = Attacher::AttachEngine3D
  Height = 50
  Placement = pos=(198,43,-31) rot=(0,1,0;1.5708rad)
  Radius = 9
FEATURE [Part::Chamfer] Chamfer124
  Base = -> Cylinder1017
  Edges = 2 edges r=2: [Edge1,Edge3]
  Placement = pos=(0,-24,0) rot=(0,0,1;0rad)
FEATURE [Part::MultiFuse] Fusion669
  Refine = true
  Shapes = -> [Chamfer124,Chamfer123]
FEATURE [Part::Cut] Cut014186  label="air-tanks"
  Base = -> Cut014183
  Placement = pos=(3.5,0,0) rot=(0,0,1;0rad)
  Refine = true
  Tool = -> Fusion669
FEATURE [Part::Cylinder] Cylinder1018  label="rear-bumper"
  Angle = 360
  AttacherType = Attacher::AttachEngine3D
  Height = 180
  Placement = pos=(530,175,-50) rot=(1,0,0;1.5708rad)
  Radius = 5
FEATURE [Part::MultiFuse] Fusion670  label="front-prop-shaft"
  Placement = pos=(547,170,3) rot=(0,0,1;3.14159rad)
  Refine = true
FEATURE [Part::Box] Box632  label="Cube823"
  AttacherType = Attacher::AttachEngine3D
  Height = 30
  Length = 29
  Width = 13
FEATURE [Part::Box] Box633  label="Cube824"
  AttacherType = Attacher::AttachEngine3D
  Height = 4
  Length = 7
  Placement = pos=(-7,3.5,1) rot=(0,0,1;0rad)
  Width = 6
FEATURE [Part::Box] Box634  label="Cube825"
  AttacherType = Attacher::AttachEngine3D
  Height = 3.3
  Length = 40
  Placement = pos=(-5.5,0,19.5) rot=(0,0,1;0rad)
  Width = 13
FEATURE [Part::Cylinder] Cylinder958  label="Cylinder1473"
  Angle = 360
  AttacherType = Attacher::AttachEngine3D
  Height = 6
  Placement = pos=(6,6.5,30) rot=(0,0,1;0rad)
  Radius = 4
FEATURE [Part::Box] Box635  label="Cube826"
  AttacherType = Attacher::AttachEngine3D
  Height = 1.5
  Length = 28
  Placement = pos=(-8,3.5,34.5) rot=(0,0,1;0rad)
  Width = 6
FEATURE [Part::Fillet] Fillet425
  Base = -> Box635
  Edges = 4 edges r=2: [Edge1,Edge3,Edge5,Edge7]
FEATURE [Part::Cylinder] Cylinder959  label="Cylinder1474"
  Angle = 360
  AttacherType = Attacher::AttachEngine3D
  Height = 10
  Radius = 1
FEATURE [Part::Cylinder] Cylinder960  label="Cylinder1475"
  Angle = 360
  AttacherType = Attacher::AttachEngine3D
  Height = 10
  Placement = pos=(35.3,0,0) rot=(0,0,1;0rad)
  Radius = 1
FEATURE [Part::MultiFuse] Fusion671
  Refine = true
  Shapes = -> [Box632,Fillet425,Box633,Box634,Cylinder958]
FEATURE [Part::MultiFuse] Fusion623
  Placement = pos=(-3.15,6.5,13) rot=(0,0,1;0rad)
  Refine = true
  Shapes = -> [Cylinder959,Cylinder960]
FEATURE [Part::Cylinder] Cylinder961  label="Cylinder1476"
  Angle = 360
  AttacherType = Attacher::AttachEngine3D
  Height = 10
  Placement = pos=(0,6.5,29) rot=(0,0,1;0rad)
  Radius = 1
FEATURE [Part::Cylinder] Cylinder1020  label="Cylinder1477"
  Angle = 360
  AttacherType = Attacher::AttachEngine3D
  Height = 10
  Placement = pos=(24,6.5,29) rot=(0,0,1;0rad)
  Radius = 1
FEATURE [Part::Cylinder] Cylinder1021  label="Cylinder1478"
  Angle = 360
  AttacherType = Attacher::AttachEngine3D
  Height = 10
  Placement = pos=(0,6.5,29) rot=(0,0,1;0rad)
  Radius = 1
FEATURE [Part::Cylinder] Cylinder1022  label="Cylinder1479"
  Angle = 360
  AttacherType = Attacher::AttachEngine3D
  Height = 10
  Placement = pos=(19,6.5,29) rot=(0,0,1;0rad)
  Radius = 1
FEATURE [Part::Cylinder] Cylinder1023  label="Cylinder1480"
  Angle = 360
  AttacherType = Attacher::AttachEngine3D
  Height = 10
  Placement = pos=(0,6.5,29) rot=(0,0,1;0rad)
  Radius = 1
FEATURE [Part::Cylinder] Cylinder1024  label="Cylinder1481"
  Angle = 360
  AttacherType = Attacher::AttachEngine3D
  Height = 10
  Placement = pos=(14,6.5,29) rot=(0,0,1;0rad)
  Radius = 1
FEATURE [Part::MultiFuse] Fusion625
  Placement = pos=(-6,0,2) rot=(0,0,1;0rad)
  Refine = true
  Shapes = -> [Cylinder961,Cylinder1020]
FEATURE [Part::MultiFuse] Fusion626
  Placement = pos=(-3.5,0,2) rot=(0,0,1;0rad)
  Refine = true
  Shapes = -> [Cylinder1021,Cylinder1022]
FEATURE [Part::MultiFuse] Fusion627
  Placement = pos=(-1,0,2) rot=(0,0,1;0rad)
  Refine = true
  Shapes = -> [Cylinder1023,Cylinder1024]
FEATURE [Part::MultiFuse] Fusion628
  Refine = true
  Shapes = -> [Fusion623,Fusion626,Fusion625,Fusion627]
FEATURE [Part::Cut] Cut014188  label="hitec-hs85bb"
  Base = -> Fusion671
  Placement = pos=(185,65,2) rot=(0,1,0;3.14159rad)
  Refine = true
  Tool = -> Fusion628
FEATURE [Part::Cylinder] Cylinder982  label="Cylinder1482"
  Angle = 360
  AttacherType = Attacher::AttachEngine3D
  Height = 15
  Placement = pos=(370,72.5,-22.85) rot=(0,1,0;1.5708rad)
  Radius = 1
FEATURE [Part::Cylinder] Cylinder1025  label="Cylinder1483"
  Angle = 360
  AttacherType = Attacher::AttachEngine3D
  Height = 15
  Placement = pos=(370,72.5,-58.15) rot=(0,1,0;1.5708rad)
  Radius = 1
FEATURE [Part::MultiFuse] Fusion672
  Placement = pos=(-1,0,3) rot=(0,0,1;0rad)
  Refine = true
  Shapes = -> [Cylinder1025,Cylinder982]
FEATURE [Part::Box] Box649  label="Cube840"
  AttacherType = Attacher::AttachEngine3D
  Height = 6
  Length = 10
  Placement = pos=(372.5,66,-22.5) rot=(0,0,1;0rad)
  Width = 13
FEATURE [Part::Box] Box650  label="Cube841"
  AttacherType = Attacher::AttachEngine3D
  Height = 6
  Length = 10
  Placement = pos=(372.5,66,-58.5) rot=(0,0,1;0rad)
  Width = 13
FEATURE [Part::MultiFuse] Fusion673
  Refine = true
  Shapes = -> [Box649,Box650]
FEATURE [Part::Cut] Cut014119  label="hitec-hs85bb-mount001"
  Base = -> Fusion673
  Placement = pos=(208,0,366) rot=(0,1,0;1.5708rad)
  Refine = true
  Tool = -> Fusion672
FEATURE [Part::Box] Box651  label="Cube842"
  AttacherType = Attacher::AttachEngine3D
  Height = 17
  Length = 32
  Placement = pos=(154.5,56,-16.5) rot=(0,0,1;0rad)
  Width = 10
FEATURE [Part::Fillet] Fillet426
  Base = -> Box651
  Edges = 2 edges r=3: [Edge9,Edge10]
FEATURE [Part::Cylinder] Cylinder1027  label="Cylinder1484"
  Angle = 360
  AttacherType = Attacher::AttachEngine3D
  Height = 12
  Placement = pos=(159.5,67,-8) rot=(1,0,0;1.5708rad)
  Radius = 1.25
FEATURE [Part::Box] Box652  label="Cube843"
  AttacherType = Attacher::AttachEngine3D
  Height = 10
  Length = 42
  Placement = pos=(149.5,61,-16.5) rot=(0,0,1;0rad)
  Width = 5
FEATURE [Part::MultiFuse] Fusion674
  Refine = true
  Shapes = -> [Box652,Fillet426,Cut014119]
FEATURE [Part::Cylinder] Cylinder1028  label="Cylinder1485"
  Angle = 360
  AttacherType = Attacher::AttachEngine3D
  Height = 15
  Placement = pos=(370,72.5,-22.85) rot=(0,1,0;1.5708rad)
  Radius = 1
FEATURE [Part::Cylinder] Cylinder1029  label="Cylinder1486"
  Angle = 360
  AttacherType = Attacher::AttachEngine3D
  Height = 15
  Placement = pos=(370,72.5,-58.15) rot=(0,1,0;1.5708rad)
  Radius = 1
FEATURE [Part::MultiFuse] Fusion675
  Placement = pos=(-1,0,3) rot=(0,0,1;0rad)
  Refine = true
  Shapes = -> [Cylinder1029,Cylinder1028]
FEATURE [Part::Box] Box653  label="Cube844"
  AttacherType = Attacher::AttachEngine3D
  Height = 6
  Length = 10
  Placement = pos=(372.5,66,-22.5) rot=(0,0,1;0rad)
  Width = 13
FEATURE [Part::Box] Box654  label="Cube845"
  AttacherType = Attacher::AttachEngine3D
  Height = 6
  Length = 10
  Placement = pos=(372.5,66,-58.5) rot=(0,0,1;0rad)
  Width = 13
FEATURE [Part::MultiFuse] Fusion676
  Refine = true
  Shapes = -> [Box653,Box654]
FEATURE [Part::Cut] Cut014189  label="hitec-hs85bb-mount"
  Base = -> Fusion676
  Placement = pos=(208,0,366) rot=(0,1,0;1.5708rad)
  Refine = true
  Tool = -> Fusion675
FEATURE [Part::Cylinder] Cylinder1030  label="Cylinder1487"
  Angle = 360
  AttacherType = Attacher::AttachEngine3D
  Height = 12
  Placement = pos=(181.5,67,-8) rot=(1,0,0;1.5708rad)
  Radius = 1.25
FEATURE [Part::Box] Box655  label="Cube846"
  AttacherType = Attacher::AttachEngine3D
  Height = 4
  Length = 10
  Placement = pos=(165.5,55,-10) rot=(0,0,1;0rad)
  Width = 5
FEATURE [Part::Fillet] Fillet427
  Base = -> Box655
  Edges = 6 edges r=1.99: [Edge2,Edge4,Edge6,Edge8,Edge11,Edge12]
FEATURE [Part::MultiFuse] Fusion677
  Refine = true
  Shapes = -> [Cylinder1027,Cylinder1030]
FEATURE [Part::Cut] Cut014190  label="Cut014392"
  Base = -> Fusion674
  Refine = true
  Tool = -> Fillet427
FEATURE [Part::Cut] Cut014191  label="transfer-case-lock-servo-mount"
  Base = -> Cut014190
  Placement = pos=(0,-1,0) rot=(0,0,1;0rad)
  Refine = true
  Tool = -> Fusion677
FEATURE [Part::Cylinder] Cylinder1031  label="Cylinder1488"
  Angle = 360
  AttacherType = Attacher::AttachEngine3D
  Height = 12
  Placement = pos=(159.5,67,-8) rot=(1,0,0;1.5708rad)
  Radius = 1.25
FEATURE [Part::Cylinder] Cylinder1032  label="Cylinder1489"
  Angle = 360
  AttacherType = Attacher::AttachEngine3D
  Height = 12
  Placement = pos=(181.5,67,-8) rot=(1,0,0;1.5708rad)
  Radius = 1.25
FEATURE [Part::MultiFuse] Fusion678
  Placement = pos=(0,-7,0) rot=(0,0,1;0rad)
  Refine = true
  Shapes = -> [Cylinder1031,Cylinder1032]
FEATURE [Part::Box] Box656  label="Cube847"
  AttacherType = Attacher::AttachEngine3D
  Height = 21
  Length = 27
  Placement = pos=(128,50.5,-21.5) rot=(0,0,1;0rad)
  Width = 3
FEATURE [Part::Box] Box657  label="Cube848"
  AttacherType = Attacher::AttachEngine3D
  Height = 3
  Length = 27
  Placement = pos=(128,50.5,-24.5) rot=(0,0,1;0rad)
  Width = 10
FEATURE [Part::Box] Box658  label="Cube849"
  AttacherType = Attacher::AttachEngine3D
  Height = 3
  Length = 27
  Placement = pos=(128,50.5,-0.5) rot=(0,0,1;0rad)
  Width = 10
FEATURE [Part::MultiFuse] Fusion679
  Placement = pos=(29,0,3) rot=(0,0,1;0rad)
  Refine = true
  Shapes = -> [Box656,Box658,Box657]
FEATURE [Part::Cut] Cut014192  label="transfer-case-lock-servo-mount-HOLES"
  Base = -> Fusion679
  Refine = true
  Tool = -> Fusion678
FEATURE [Part::Cylinder] Cylinder1033  label="Cylinder1490"
  Angle = 360
  AttacherType = Attacher::AttachEngine3D
  Height = 39.5
  Placement = pos=(0,0,23) rot=(0,1,0;1.5708rad)
  Radius = 13
FEATURE [Part::Cylinder] Cylinder1034  label="Cylinder1491"
  Angle = 360
  AttacherType = Attacher::AttachEngine3D
  Height = 39.5
  Placement = pos=(0,0,0) rot=(0,1,0;1.5708rad)
  Radius = 19.5
FEATURE [Part::Cylinder] Cylinder798  label="main-motor"
  Angle = 360
  AttacherType = Attacher::AttachEngine3D
  Height = 50
  Placement = pos=(31,89,23) rot=(0,1,0;1.5708rad)
  Radius = 18
FEATURE [Part::MultiFuse] Fusion248002002  label="gearbox002"
  Placement = pos=(89,84.9373,3.51066) rot=(1,0,0;0.706858rad)
  Refine = true
  Shapes = -> [Cylinder1033,Cylinder1034]
FEATURE [Part::Box] Box659  label="Cube850"
  AttacherType = Attacher::AttachEngine3D
  Height = 41
  Length = 47.5
  Placement = pos=(81,65,-17) rot=(0,0,1;0rad)
  Width = 40
FEATURE [Part::Cylinder] Cylinder801  label="main-motor001"
  Angle = 360
  AttacherType = Attacher::AttachEngine3D
  Height = 18
  Placement = pos=(81,89,21) rot=(0,1,0;1.5708rad)
  Radius = 18
FEATURE [Part::Cylinder] Cylinder802  label="Cylinder1492"
  Angle = 360
  AttacherType = Attacher::AttachEngine3D
  Height = 47.5
  Placement = pos=(81,70,21) rot=(0,1,0;1.5708rad)
  Radius = 17.5
FEATURE [Part::Feature] Fillet007001  label="selector"
  Placement = pos=(119.5,85,5.5) rot=(0.181732,-0.966409,-0.181732;1.60496rad)
  shape: bbox 10 x 30 x 28.57 mm, 21 faces (baked)
FEATURE [Part::Box] Box660  label="Cube851"
  AttacherType = Attacher::AttachEngine3D
  Height = 22
  Length = 47.5
  Placement = pos=(81,105,2) rot=(0,0,1;0rad)
  Width = 7
FEATURE [Part::MultiFuse] Fusion591
  Refine = true
  Shapes = -> [Box660,Cylinder802,Box659,Cylinder801]
FEATURE [Part::Cylinder] Cylinder805  label="Cylinder1493"
  Angle = 360
  AttacherType = Attacher::AttachEngine3D
  Height = 10
  Placement = pos=(89,70,21) rot=(0,1,0;1.5708rad)
  Radius = 16.5
FEATURE [Part::MultiFuse] Fusion592
  Refine = true
  Shapes = -> [Fusion248002002,Cylinder805]
FEATURE [Part::Cut] Cut014193  label="Cut014393"
  Base = -> Fusion591
  Refine = true
  Tool = -> Fusion592
FEATURE [Part::Chamfer] Chamfer125
  Base = -> Cut014193
  Edges = 1 edges r=3.49: [Edge39]
FEATURE [Part::Fillet] Fillet007002
  Base = -> Chamfer125
  Edges = 1 edges r=3: [Edge25]
FEATURE [Part::Fillet] Fillet007003
  Base = -> Fillet007002
  Edges = 2 edges r=6: [Edge13,Edge18]
FEATURE [Part::Box] Box500  label="Cube702"
  AttacherType = Attacher::AttachEngine3D
  Height = 20
  Length = 60
  Placement = pos=(81,53.25,-18) rot=(0,0,1;0rad)
  Width = 63.5
FEATURE [Part::Feature] Face052
  shape: bbox 2.621e-05 x 37.61 x 40.07 mm, 1 faces, 0 solids (baked)
FEATURE [Part::Extrusion] Extrude013
  Base = -> Face052
  Dir = (60,0,0)
  DirMode = 0
  FaceMakerClass = Part::FaceMakerExtrusion
  LengthFwd = 0
  LengthRev = 0
  Placement = pos=(-30.4,1.43133,-5.60163) rot=(1,0,0;0.069813rad)
  Solid = false
  Symmetric = false
FEATURE [Part::Cylinder] Cylinder806  label="Cylinder1494"
  Angle = 360
  AttacherType = Attacher::AttachEngine3D
  Height = 60
  Placement = pos=(81,106.419,11.8645) rot=(0.034878,0.998783,0.034878;1.57201rad)
  Radius = 3.1
FEATURE [Part::Cut] Cut014049
  Base = -> Fillet007003
  Refine = true
  Tool = -> Extrude013
FEATURE [Part::Cut] Cut014050
  Base = -> Cut014049
  Refine = true
  Tool = -> Cylinder806
FEATURE [Part::Cylinder] Cylinder807  label="Cylinder000"
  Angle = 360
  AttacherType = Attacher::AttachEngine3D
  Height = 50
  Placement = pos=(45,89,21) rot=(0,1,0;1.5708rad)
  Radius = 7
FEATURE [Part::Cut] Cut014051
  Base = -> Cut014050
  Refine = true
  Tool = -> Cylinder807
FEATURE [Part::Chamfer] Chamfer126
  Base = -> Cut014051
  Edges = 1 edges r=5.2: [Edge52]
FEATURE [Part::Cylinder] Cylinder808  label="Cylinder1495"
  Angle = 360
  AttacherType = Attacher::AttachEngine3D
  Height = 50
  Placement = pos=(56,89,33.5) rot=(0,1,0;1.5708rad)
  Radius = 1.6
FEATURE [Part::Cylinder] Cylinder809  label="Cylinder958"
  Angle = 360
  AttacherType = Attacher::AttachEngine3D
  Height = 50
  Placement = pos=(56,89,8.5) rot=(0,1,0;1.5708rad)
  Radius = 1.6
FEATURE [Part::MultiFuse] Fusion593
  Placement = pos=(0,14.7618,74.3919) rot=(-1,0,0;0.855211rad)
  Refine = true
  Shapes = -> [Cylinder808,Cylinder809]
FEATURE [Part::Cylinder] Cylinder810  label="Cylinder959"
  Angle = 360
  AttacherType = Attacher::AttachEngine3D
  Height = 15
  Placement = pos=(56,89,33.5) rot=(0,1,0;1.5708rad)
  Radius = 3.1
FEATURE [Part::Cylinder] Cylinder811  label="Cylinder960"
  Angle = 360
  AttacherType = Attacher::AttachEngine3D
  Height = 15
  Placement = pos=(56,89,8.5) rot=(0,1,0;1.5708rad)
  Radius = 3.1
FEATURE [Part::MultiFuse] Fusion594
  Placement = pos=(28,14.7618,74.3919) rot=(-1,0,0;0.855211rad)
  Refine = true
  Shapes = -> [Cylinder810,Cylinder811]
FEATURE [Part::MultiFuse] Fusion595
  Refine = true
  Shapes = -> [Fusion593,Fusion594]
FEATURE [Part::Cut] Cut014052
  Base = -> Chamfer126
  Refine = true
  Tool = -> Fusion595
FEATURE [Part::Cylinder] Cylinder812  label="Cylinder1496"
  Angle = 360
  AttacherType = Attacher::AttachEngine3D
  Height = 60
  Placement = pos=(81,85,3.5) rot=(0,1,0;1.5708rad)
  Radius = 5.6
FEATURE [Part::Cylinder] Cylinder813  label="Cylinder1497"
  Angle = 360
  AttacherType = Attacher::AttachEngine3D
  Height = 60
  Placement = pos=(81,70,21) rot=(0,1,0;1.5708rad)
  Radius = 5.6
FEATURE [Part::MultiFuse] Fusion248002003  label="Fusion248002197"
  Placement = pos=(4,0,0) rot=(0,0,1;0rad)
  Refine = true
  Shapes = -> [Cylinder812,Cylinder813]
FEATURE [Part::Cylinder] Cylinder814  label="Cylinder1498"
  Angle = 360
  AttacherType = Attacher::AttachEngine3D
  Height = 60
  Placement = pos=(81,85,3.5) rot=(0,1,0;1.5708rad)
  Radius = 4
FEATURE [Part::Cylinder] Cylinder815  label="Cylinder1499"
  Angle = 360
  AttacherType = Attacher::AttachEngine3D
  Height = 60
  Placement = pos=(81,70,21) rot=(0,1,0;1.5708rad)
  Radius = 4
FEATURE [Part::MultiFuse] Fusion248002004
  Refine = true
  Shapes = -> [Cylinder814,Cylinder815]
FEATURE [Part::MultiFuse] Fusion248002005
  Refine = true
  Shapes = -> [Fusion248002003,Fusion248002004]
FEATURE [Part::Cut] Cut014053
  Base = -> Cut014052
  Refine = true
  Tool = -> Fusion248002005
FEATURE [Part::Cylinder] Cylinder816  label="Cylinder1500"
  Angle = 360
  AttacherType = Attacher::AttachEngine3D
  Height = 20
  Placement = pos=(81,69,-13) rot=(0,1,0;1.5708rad)
  Radius = 1.25
FEATURE [Part::Cylinder] Cylinder817  label="Cylinder1501"
  Angle = 360
  AttacherType = Attacher::AttachEngine3D
  Height = 20
  Placement = pos=(81,101,-13) rot=(0,1,0;1.5708rad)
  Radius = 1.25
FEATURE [Part::Cylinder] Cylinder818  label="Cylinder1502"
  Angle = 360
  AttacherType = Attacher::AttachEngine3D
  Height = 20
  Placement = pos=(81,101,21) rot=(0,1,0;1.5708rad)
  Radius = 1.25
FEATURE [Part::Cylinder] Cylinder819  label="Cylinder1503"
  Angle = 360
  AttacherType = Attacher::AttachEngine3D
  Height = 20
  Placement = pos=(81,70,36) rot=(0,1,0;1.5708rad)
  Radius = 1.25
FEATURE [Part::Cylinder] Cylinder820  label="Cylinder1504"
  Angle = 360
  AttacherType = Attacher::AttachEngine3D
  Height = 20
  Placement = pos=(81,56,26) rot=(0,1,0;1.5708rad)
  Radius = 1.25
FEATURE [Part::Cylinder] Cylinder821  label="Cylinder1505"
  Angle = 360
  AttacherType = Attacher::AttachEngine3D
  Height = 20
  Placement = pos=(81,62,8) rot=(0,1,0;1.5708rad)
  Radius = 1.25
FEATURE [Part::MultiFuse] Fusion248002006
  Placement = pos=(28,0,0) rot=(0,0,1;0rad)
  Refine = true
  Shapes = -> [Cylinder816,Cylinder820,Cylinder821,Cylinder817,Cylinder818,Cylinder819]
FEATURE [Part::Cut] Cut014054
  Base = -> Cut014053
  Placement = pos=(0,0,2) rot=(0,0,1;0rad)
  Refine = true
  Tool = -> Fusion248002006
FEATURE [Part::Box] Box501  label="Cube703"
  AttacherType = Attacher::AttachEngine3D
  Height = 22
  Length = 44
  Placement = pos=(81,51,-15) rot=(0,0,1;0rad)
  Width = 14
FEATURE [Part::Fillet] Fillet007004
  Base = -> Box500
  Edges = 2 edges r=3: [Edge10,Edge12]
FEATURE [Part::Box] Box502  label="Cube704"
  AttacherType = Attacher::AttachEngine3D
  Height = 22
  Length = 44
  Placement = pos=(81,105,-15) rot=(0,0,1;0rad)
  Width = 14
FEATURE [Part::Cylinder] Cylinder822  label="Cylinder961"
  Angle = 360
  AttacherType = Attacher::AttachEngine3D
  Height = 5
  Placement = pos=(120,125,-8) rot=(1,0,0;1.5708rad)
  Radius = 1.6
FEATURE [Part::Cylinder] Cylinder823  label="Cylinder962"
  Angle = 360
  AttacherType = Attacher::AttachEngine3D
  Height = 5
  Placement = pos=(86,125,-8) rot=(1,0,0;1.5708rad)
  Radius = 1.6
FEATURE [Part::MultiFuse] Fusion248002007
  Placement = pos=(0,-5,0) rot=(0,0,1;0rad)
  Refine = true
  Shapes = -> [Cylinder823,Cylinder822]
FEATURE [Part::Cylinder] Cylinder824  label="Cylinder963"
  Angle = 360
  AttacherType = Attacher::AttachEngine3D
  Height = 5
  Placement = pos=(120,125,-8) rot=(1,0,0;1.5708rad)
  Radius = 1.6
FEATURE [Part::Cylinder] Cylinder825  label="Cylinder964"
  Angle = 360
  AttacherType = Attacher::AttachEngine3D
  Height = 5
  Placement = pos=(86,125,-8) rot=(1,0,0;1.5708rad)
  Radius = 1.6
FEATURE [Part::MultiFuse] Fusion248002008
  Placement = pos=(0,-70,0) rot=(0,0,1;0rad)
  Refine = true
  Shapes = -> [Cylinder825,Cylinder824]
FEATURE [Part::MultiFuse] Fusion248002009
  Refine = true
  Shapes = -> [Fusion248002007,Fusion248002008]
FEATURE [Part::Feature] Face044
  shape: bbox 2e-07 x 80.32 x 83.91 mm, 1 faces, 0 solids (baked)
FEATURE [Part::Extrusion] Extrude014
  Base = -> Face044
  Dir = (5,0,0)
  DirMode = 0
  FaceMakerClass = Part::FaceMakerExtrusion
  LengthFwd = 0
  LengthRev = 0
  Solid = false
  Symmetric = false
FEATURE [Part::Cylinder] Cylinder826
  Angle = 360
  AttacherType = Attacher::AttachEngine3D
  Height = 60
  Placement = pos=(81,85,3.5) rot=(0,1,0;1.5708rad)
  Radius = 4
FEATURE [Part::Cylinder] Cylinder827
  Angle = 360
  AttacherType = Attacher::AttachEngine3D
  Height = 60
  Placement = pos=(81,70,21) rot=(0,1,0;1.5708rad)
  Radius = 4
FEATURE [Part::MultiFuse] Fusion248002010
  Refine = true
  Shapes = -> [Cylinder826,Cylinder827]
FEATURE [Part::Cylinder] Cylinder828
  Angle = 360
  AttacherType = Attacher::AttachEngine3D
  Height = 60
  Placement = pos=(81,85,3.5) rot=(0,1,0;1.5708rad)
  Radius = 5.6
FEATURE [Part::Cylinder] Cylinder829
  Angle = 360
  AttacherType = Attacher::AttachEngine3D
  Height = 60
  Placement = pos=(81,70,21) rot=(0,1,0;1.5708rad)
  Radius = 5.6
FEATURE [Part::MultiFuse] Fusion248002011
  Placement = pos=(-8.5,0,0) rot=(0,0,1;0rad)
  Refine = true
  Shapes = -> [Cylinder828,Cylinder829]
FEATURE [Part::MultiFuse] Fusion608
  Refine = true
  Shapes = -> [Fusion248002011,Fusion248002010]
FEATURE [Part::Cut] Cut014057
  Base = -> Extrude014
  Refine = true
  Tool = -> Fusion608
FEATURE [Part::Cylinder] Cylinder830
  Angle = 360
  AttacherType = Attacher::AttachEngine3D
  Height = 60
  Placement = pos=(81,106.419,11.8645) rot=(0.034878,0.998783,0.034878;1.57201rad)
  Radius = 3.1
FEATURE [Part::Cut] Cut014058
  Base = -> Cut014057
  Refine = true
  Tool = -> Cylinder830
FEATURE [Part::Cylinder] Cylinder831
  Angle = 360
  AttacherType = Attacher::AttachEngine3D
  Height = 20
  Placement = pos=(81,69,-13) rot=(0,1,0;1.5708rad)
  Radius = 1.6
FEATURE [Part::Cylinder] Cylinder832  label="Cylinder1506"
  Angle = 360
  AttacherType = Attacher::AttachEngine3D
  Height = 20
  Placement = pos=(81,101,-13) rot=(0,1,0;1.5708rad)
  Radius = 1.6
FEATURE [Part::Cylinder] Cylinder833  label="Cylinder1507"
  Angle = 360
  AttacherType = Attacher::AttachEngine3D
  Height = 20
  Placement = pos=(81,101,21) rot=(0,1,0;1.5708rad)
  Radius = 1.6
FEATURE [Part::Cylinder] Cylinder834  label="Cylinder1508"
  Angle = 360
  AttacherType = Attacher::AttachEngine3D
  Height = 20
  Placement = pos=(81,70,36) rot=(0,1,0;1.5708rad)
  Radius = 1.6
FEATURE [Part::Cylinder] Cylinder835  label="Cylinder1509"
  Angle = 360
  AttacherType = Attacher::AttachEngine3D
  Height = 20
  Placement = pos=(81,56,26) rot=(0,1,0;1.5708rad)
  Radius = 1.6
FEATURE [Part::Cylinder] Cylinder836  label="Cylinder1510"
  Angle = 360
  AttacherType = Attacher::AttachEngine3D
  Height = 20
  Placement = pos=(81,62,8) rot=(0,1,0;1.5708rad)
  Radius = 1.6
FEATURE [Part::MultiFuse] Fusion609
  Placement = pos=(40,0,2) rot=(0,0,1;0rad)
  Refine = true
  Shapes = -> [Cylinder831,Cylinder835,Cylinder836,Cylinder832,Cylinder833,Cylinder834]
FEATURE [Part::Box] Box504  label="Cube706"
  AttacherType = Attacher::AttachEngine3D
  Height = 10
  Length = 30
  Placement = pos=(81,111,5) rot=(0,0,1;0rad)
  Width = 5.5
FEATURE [Part::Chamfer] Chamfer127
  Base = -> Box502
  Edges = 1 edges r=2: [Edge10]
FEATURE [Part::MultiFuse] Fusion611
  Refine = true
  Shapes = -> [Box501,Chamfer127]
FEATURE [Part::Cut] Cut014194  label="Cut014394"
  Base = -> Fusion611
  Refine = true
  Tool = -> Fillet007004
FEATURE [Part::MultiFuse] Fusion612
  Refine = true
  Shapes = -> [Cut014054,Cut014194]
FEATURE [Part::Fillet] Fillet007005
  Base = -> Fusion612
  Edges = 1 edges r=4: [Edge94]
FEATURE [Part::Fillet] Fillet007006
  Base = -> Fillet007005
  Edges = 2 edges r=4: [Edge124,Edge131]
FEATURE [Part::Chamfer] Chamfer111
  Base = -> Fillet007006
  Edges = 1 edges r=3: [Edge58]
FEATURE [Part::Fillet] Fillet007007
  Base = -> Chamfer111
  Edges = 1 edges r=2: [Edge92]
FEATURE [Part::Fillet] Fillet007008
  Base = -> Cut014058
  Edges = 1 edges r=2: [Edge1]
FEATURE [Part::Fillet] Fillet007009
  Base = -> Fillet007008
  Edges = 1 edges r=3: [Edge41]
  Placement = pos=(0,0,2) rot=(0,0,1;0rad)
FEATURE [Part::Fillet] Fillet007010
  Base = -> Fillet007007
  Edges = 1 edges r=2.99: [Edge67]
FEATURE [Part::Cylinder] Cylinder837  label="Cylinder965"
  Angle = 360
  AttacherType = Attacher::AttachEngine3D
  Height = 10
  Placement = pos=(96,125,-8) rot=(1,0,0;1.5708rad)
  Radius = 1.25
FEATURE [Part::Cylinder] Cylinder838  label="Cylinder966"
  Angle = 360
  AttacherType = Attacher::AttachEngine3D
  Height = 10
  Placement = pos=(86,125,-8) rot=(1,0,0;1.5708rad)
  Radius = 1.25
FEATURE [Part::MultiFuse] Fusion613
  Placement = pos=(12,-3.5,20) rot=(0,0,1;0rad)
  Refine = true
  Shapes = -> [Cylinder838,Cylinder837]
FEATURE [Part::Cylinder] Cylinder839  label="Cylinder967"
  Angle = 360
  AttacherType = Attacher::AttachEngine3D
  Height = 8
  Placement = pos=(96,124,-8) rot=(1,0,0;1.5708rad)
  Radius = 1.25
FEATURE [Part::Cylinder] Cylinder840  label="Cylinder968"
  Angle = 360
  AttacherType = Attacher::AttachEngine3D
  Height = 8
  Placement = pos=(86,120.5,-8) rot=(1,0,0;1.5708rad)
  Radius = 1.25
FEATURE [Part::Box] Box505  label="Cube707"
  AttacherType = Attacher::AttachEngine3D
  Height = 10
  Length = 30
  Placement = pos=(95,53.5,5) rot=(0,0,1;0rad)
  Width = 7
FEATURE [Part::Chamfer] Chamfer112
  Base = -> Box505
  Edges = 1 edges r=6: [Edge12]
  Placement = pos=(-14,0,0) rot=(0,0,1;0rad)
FEATURE [Part::Fillet] Fillet007011
  Base = -> Box504
  Edges = 1 edges r=1: [Edge12]
FEATURE [Part::Fillet] Fillet007012
  Base = -> Chamfer112
  Edges = 1 edges r=0.99: [Edge7]
FEATURE [Part::MultiFuse] Fusion616
  Refine = true
  Shapes = -> [Fillet007010,Fillet007012,Fillet007011]
FEATURE [Part::MultiFuse] Fusion614
  Placement = pos=(12,-64,20) rot=(0,0,1;0rad)
  Refine = true
  Shapes = -> [Cylinder840,Cylinder839]
FEATURE [Part::MultiFuse] Fusion617
  Refine = true
  Shapes = -> [Fusion613,Fusion614]
FEATURE [Part::MultiFuse] Fusion618
  Refine = true
  Shapes = -> [Fusion248002009,Fusion617]
FEATURE [Part::Fillet] Fillet007013
  Base = -> Fusion616
  Edges = 2 edges r=6: [Edge81,Edge92]
FEATURE [Part::Box] Box506  label="Cube708"
  AttacherType = Attacher::AttachEngine3D
  Height = 2
  Length = 39.5
  Placement = pos=(89,104,2) rot=(1,0,0;1.0821rad)
  Width = 10
FEATURE [Part::Box] Box507  label="Cube709"
  AttacherType = Attacher::AttachEngine3D
  Height = 2
  Length = 39.5
  Placement = pos=(89,96,19) rot=(-1,0,0;0.314159rad)
  Width = 10
FEATURE [Part::MultiFuse] Fusion619
  Refine = true
  Shapes = -> [Box507,Box506]
FEATURE [Part::Cut] Cut014062
  Base = -> Fillet007013
  Refine = true
  Tool = -> Fusion619
FEATURE [Part::Cylinder] Cylinder841  label="Cylinder1511"
  Angle = 360
  AttacherType = Attacher::AttachEngine3D
  Height = 19
  Placement = pos=(89,70,23) rot=(0,1,0;1.5708rad)
  Radius = 16.5
FEATURE [Part::Chamfer] Chamfer113
  Base = -> Cylinder841
  Edges = 1 edges r=4: [Edge1]
FEATURE [Part::Box] Box508  label="Cube710"
  AttacherType = Attacher::AttachEngine3D
  Height = 32
  Length = 19
  Placement = pos=(89,70,7) rot=(0,0,1;0rad)
  Width = 32
FEATURE [Part::Chamfer] Chamfer114
  Base = -> Box508
  Edges = 2 edges r=4: [Edge6,Edge8]
  Placement = pos=(0,5.43898,58.5088) rot=(-1,0,0;0.820305rad)
FEATURE [Part::Chamfer] Chamfer115
  Base = -> Cut014062
  Edges = 1 edges r=5: [Edge65]
FEATURE [Part::MultiFuse] Fusion620
  Refine = true
  Shapes = -> [Chamfer113,Chamfer114]
FEATURE [Part::Cut] Cut014063
  Base = -> Chamfer115
  Refine = true
  Tool = -> Fusion620
FEATURE [Part::Cut] Cut014064  label="gearbox-front"
  Base = -> Cut014063
  Refine = true
  Tool = -> Fusion618
FEATURE [Part::Chamfer] Chamfer116
  Base = -> Fillet007009
  Edges = 1 edges r=5: [Edge35]
FEATURE [Part::Cut] Cut014065  label="gearbox-rear"
  Base = -> Chamfer116
  Refine = true
  Tool = -> Fusion609
FEATURE [Part::Cylinder] Cylinder1035  label="Cylinder1512"
  Angle = 360
  AttacherType = Attacher::AttachEngine3D
  Height = 170
  Placement = pos=(509,170,7) rot=(1,0,0;1.5708rad)
  Radius = 5
FEATURE [Part::Box] Box661  label="Cube852"
  AttacherType = Attacher::AttachEngine3D
  Height = 10
  Length = 10
  Placement = pos=(280,0,2) rot=(0,0,1;0rad)
  Width = 170
FEATURE [Part::Box] Box662  label="Cube853"
  AttacherType = Attacher::AttachEngine3D
  Height = 8
  Length = 10
  Placement = pos=(280,0,12) rot=(0,0,1;0rad)
  Width = 170
FEATURE [Part::Box] Box663  label="Cube854"
  AttacherType = Attacher::AttachEngine3D
  Height = 8
  Length = 10
  Placement = pos=(504,0,12) rot=(0,0,1;0rad)
  Width = 170
FEATURE [Part::Box] Box602  label="Cube791"
  AttacherType = Attacher::AttachEngine3D
  Height = 10
  Length = 224
  Placement = pos=(290,55,2) rot=(0,0,1;0rad)
  Width = 10
FEATURE [Part::Box] Box603  label="Cube792"
  AttacherType = Attacher::AttachEngine3D
  Height = 10
  Length = 224
  Placement = pos=(290,105,2) rot=(0,0,1;0rad)
  Width = 10
FEATURE [Part::Box] Box604  label="Cube793"
  AttacherType = Attacher::AttachEngine3D
  Height = 8
  Length = 300
  Placement = pos=(230,55,12) rot=(0,0,1;0rad)
  Width = 10
FEATURE [Part::Box] Box605  label="Cube794"
  AttacherType = Attacher::AttachEngine3D
  Height = 8
  Length = 300
  Placement = pos=(229,55,10) rot=(0,1,0;0.05236rad)
  Width = 10
FEATURE [Part::Box] Box606  label="Cube795"
  AttacherType = Attacher::AttachEngine3D
  Height = 8
  Length = 300
  Placement = pos=(230,55,10) rot=(0,1,0;0.05236rad)
  Width = 10
FEATURE [Part::Mirroring] Part__Mirroring106  label="Cube795 (Mirror #2)"
  Base = (0,0,0)
  Normal = (1,0,0)
  Placement = pos=(761,0,0) rot=(0,0,1;0rad)
  Source = -> Box606
FEATURE [Part::MultiFuse] Fusion248002012
  Refine = true
  Shapes = -> [Box605,Part__Mirroring106]
FEATURE [Part::Cut] Cut014195  label="Cut014395"
  Base = -> Box604
  Refine = true
  Tool = -> Fusion248002012
FEATURE [Part::Box] Box607  label="Cube796"
  AttacherType = Attacher::AttachEngine3D
  Height = 8
  Length = 10
  Placement = pos=(375,0,12) rot=(0,0,1;0rad)
  Width = 170
FEATURE [Part::Box] Box608  label="Cube797"
  AttacherType = Attacher::AttachEngine3D
  Height = 8
  Length = 10
  Placement = pos=(375,-1,10) rot=(-1,0,0;0.122173rad)
  Width = 170
FEATURE [Part::Box] Box609  label="Cube798"
  AttacherType = Attacher::AttachEngine3D
  Height = 8
  Length = 10
  Placement = pos=(375,-1,10) rot=(-1,0,0;0.122173rad)
  Width = 170
FEATURE [Part::Mirroring] Part__Mirroring107  label="Cube798 (Mirror #3)"
  Base = (0,0,0)
  Normal = (0,1,0)
  Placement = pos=(0,170,0) rot=(0,0,1;0rad)
  Source = -> Box609
FEATURE [Part::MultiFuse] Fusion232
  Refine = true
  Shapes = -> [Box608,Part__Mirroring107]
FEATURE [Part::Cut] Cut014196  label="Cut014396"
  Base = -> Box607
  Refine = true
  Tool = -> Fusion232
FEATURE [Part::Box] Box610  label="Cube799"
  AttacherType = Attacher::AttachEngine3D
  Height = 8
  Length = 300
  Placement = pos=(230,55,12) rot=(0,0,1;0rad)
  Width = 10
FEATURE [Part::Box] Box611  label="Cube800"
  AttacherType = Attacher::AttachEngine3D
  Height = 8
  Length = 300
  Placement = pos=(229,55,10) rot=(0,1,0;0.05236rad)
  Width = 10
FEATURE [Part::Box] Box612  label="Cube801"
  AttacherType = Attacher::AttachEngine3D
  Height = 8
  Length = 300
  Placement = pos=(230,55,10) rot=(0,1,0;0.05236rad)
  Width = 10
FEATURE [Part::Mirroring] Part__Mirroring108  label="Cube795 (Mirror #2)001"
  Base = (0,0,0)
  Normal = (1,0,0)
  Placement = pos=(761,0,0) rot=(0,0,1;0rad)
  Source = -> Box612
FEATURE [Part::MultiFuse] Fusion233
  Refine = true
  Shapes = -> [Box611,Part__Mirroring108]
FEATURE [Part::Cut] Cut014197  label="Cut014397"
  Base = -> Box610
  Placement = pos=(0,51,0) rot=(0,0,1;0rad)
  Refine = true
  Tool = -> Fusion233
FEATURE [Part::Box] Box112  label="Cube111"
  AttacherType = Attacher::AttachEngine3D
  Height = 45
  Length = 4
  Placement = pos=(-4,-44,16) rot=(0,0,1;0rad)
  Width = 168
FEATURE [Part::Box] Box113  label="Cube112"
  AttacherType = Attacher::AttachEngine3D
  Height = 33
  Length = 4
  Placement = pos=(-4,-40,22) rot=(0,0,1;0rad)
  Width = 160
FEATURE [Part::Cut] Cut014198  label="Cut014398"
  Base = -> Box112
  Refine = true
  Tool = -> Box113
FEATURE [Part::Box] Box117  label="Cube116"
  AttacherType = Attacher::AttachEngine3D
  Height = 7
  Length = 3
  Placement = pos=(-3,-40,35) rot=(0,0,1;0rad)
  Width = 160
FEATURE [Part::Chamfer] Chamfer128
  Base = -> Box117
  Edges = 2 edges r=1: [Edge2,Edge4]
  Placement = pos=(0,0,0.5) rot=(0,0,1;0rad)
FEATURE [Part::Cylinder] Cylinder283  label="Cylinder465"
  Angle = 360
  AttacherType = Attacher::AttachEngine3D
  Height = 3.8
  Placement = pos=(-1.5,135,55) rot=(1,0,0;1.5708rad)
  Radius = 0.9
FEATURE [Part::Cylinder] Cylinder284  label="Cylinder466"
  Angle = 360
  AttacherType = Attacher::AttachEngine3D
  Height = 3.8
  Placement = pos=(-1.5,135,25) rot=(1,0,0;1.5708rad)
  Radius = 0.9
FEATURE [Part::MultiFuse] Fusion248002013
  Placement = pos=(0,-11,0) rot=(0,0,1;0rad)
  Refine = true
  Shapes = -> [Cylinder283,Cylinder284]
FEATURE [Part::Cylinder] Cylinder285  label="Cylinder467"
  Angle = 360
  AttacherType = Attacher::AttachEngine3D
  Height = 3.8
  Placement = pos=(-1.5,135,25) rot=(1,0,0;1.5708rad)
  Radius = 0.9
FEATURE [Part::MultiFuse] Fusion162
  Placement = pos=(0,-175.2,0) rot=(0,0,1;0rad)
  Refine = true
  Shapes = -> [Cylinder285]
FEATURE [Part::MultiFuse] Fusion248002014  label="Fusion248002133"
  Placement = pos=(229,45,5) rot=(0,0,1;0rad)
  Refine = true
  Shapes = -> [Fusion162,Fusion248002013]
FEATURE [Part::Box] Box121  label="kipper-front-wall-frame-ALU"
  AttacherType = Attacher::AttachEngine3D
  Height = 45
  Length = 1
  Placement = pos=(229,1,21) rot=(0,0,1;0rad)
  Width = 168
FEATURE [Part::Cylinder] Cylinder1036  label="Cylinder472"
  Angle = 360
  AttacherType = Attacher::AttachEngine3D
  Height = 10
  Placement = pos=(227.5,111,16) rot=(0,0,1;0rad)
  Radius = 0.9
FEATURE [Part::Cylinder] Cylinder1037  label="Cylinder473"
  Angle = 360
  AttacherType = Attacher::AttachEngine3D
  Height = 10
  Placement = pos=(227.5,60,16) rot=(0,0,1;0rad)
  Radius = 0.9
FEATURE [Part::MultiFuse] Fusion170
  Refine = true
  Shapes = -> [Cylinder1037,Cylinder1036]
FEATURE [Part::Box] Box613  label="kipper-plane002"
  AttacherType = Attacher::AttachEngine3D
  Height = 1
  Length = 310
  Placement = pos=(225,-7,20) rot=(0,0,1;0rad)
  Width = 184
FEATURE [Part::Chamfer] Chamfer129
  Base = -> Cut014198
  Edges = 2 edges r=2: [Edge5,Edge7]
FEATURE [Part::Box] Box614  label="Cube802"
  AttacherType = Attacher::AttachEngine3D
  Height = 1
  Length = 1
  Placement = pos=(-1,-40,28.5) rot=(0,0,1;0rad)
  Width = 160
FEATURE [Part::Chamfer] Chamfer064
  Base = -> Box614
  Edges = 2 edges r=0.2: [Edge2,Edge4]
FEATURE [Part::Box] Box615  label="Cube803"
  AttacherType = Attacher::AttachEngine3D
  Height = 1
  Length = 1
  Placement = pos=(-1,-40,28.5) rot=(0,0,1;0rad)
  Width = 160
FEATURE [Part::Chamfer] Chamfer065
  Base = -> Box615
  Edges = 2 edges r=0.2: [Edge2,Edge4]
  Placement = pos=(0,0,20) rot=(0,0,1;0rad)
FEATURE [Part::MultiFuse] Fusion234
  Placement = pos=(229,45,5) rot=(0,0,1;0rad)
  Refine = true
  Shapes = -> [Chamfer128,Chamfer064,Chamfer129,Chamfer065]
FEATURE [Part::Cut] Cut014199  label="Cut014399"
  Base = -> Fusion234
  Refine = true
  Tool = -> Fusion248002014
FEATURE [Part::Box] Box111  label="Cube110"
  AttacherType = Attacher::AttachEngine3D
  Height = 50
  Length = 8
  Placement = pos=(-2,124,15) rot=(0,0,1;0rad)
  Width = 8
FEATURE [Part::Box] Box122  label="Cube121"
  AttacherType = Attacher::AttachEngine3D
  Height = 50
  Length = 8
  Placement = pos=(-2,-52,15) rot=(0,0,1;0rad)
  Width = 8
FEATURE [Part::MultiFuse] Fusion248002015
  Placement = pos=(227,45,6) rot=(0,0,1;0rad)
  Refine = true
  Shapes = -> [Box111,Box122]
FEATURE [Part::Box] Box616  label="Cube804"
  AttacherType = Attacher::AttachEngine3D
  Height = 50
  Length = 8
  Placement = pos=(-2,124,15) rot=(0,0,1;0rad)
  Width = 8
FEATURE [Part::Box] Box617  label="Cube805"
  AttacherType = Attacher::AttachEngine3D
  Height = 50
  Length = 8
  Placement = pos=(-2,-52,15) rot=(0,0,1;0rad)
  Width = 8
FEATURE [Part::MultiFuse] Fusion235
  Placement = pos=(529,45,6) rot=(0,0,1;0rad)
  Refine = true
  Shapes = -> [Box616,Box617]
FEATURE [Part::MultiFuse] Fusion236  label="kipper-walls-supports-ALU"
  Refine = true
  Shapes = -> [Fusion235,Fusion248002015]
FEATURE [Part::Cylinder] Cylinder1038  label="Cylinder1513"
  Angle = 360
  AttacherType = Attacher::AttachEngine3D
  Height = 10
  Placement = pos=(225,3,64) rot=(0,1,0;1.5708rad)
  Radius = 1
FEATURE [Part::Cylinder] Cylinder1039  label="Cylinder1514"
  Angle = 360
  AttacherType = Attacher::AttachEngine3D
  Height = 10
  Placement = pos=(225,3,23) rot=(0,1,0;1.5708rad)
  Radius = 1
FEATURE [Part::MultiFuse] Fusion237
  Placement = pos=(0,0.5,0) rot=(0,0,1;0rad)
  Refine = true
  Shapes = -> [Cylinder1039,Cylinder1038]
FEATURE [Part::Cylinder] Cylinder1040  label="Cylinder1515"
  Angle = 360
  AttacherType = Attacher::AttachEngine3D
  Height = 10
  Placement = pos=(225,3,64) rot=(0,1,0;1.5708rad)
  Radius = 1
FEATURE [Part::Cylinder] Cylinder1041  label="Cylinder1516"
  Angle = 360
  AttacherType = Attacher::AttachEngine3D
  Height = 10
  Placement = pos=(225,3,23) rot=(0,1,0;1.5708rad)
  Radius = 1
FEATURE [Part::MultiFuse] Fusion238
  Placement = pos=(0,163.5,0) rot=(0,0,1;0rad)
  Refine = true
  Shapes = -> [Cylinder1041,Cylinder1040]
FEATURE [Part::Cylinder] Cylinder1042  label="Cylinder1517"
  Angle = 360
  AttacherType = Attacher::AttachEngine3D
  Height = 10
  Placement = pos=(225,3,64) rot=(0,1,0;1.5708rad)
  Radius = 1
FEATURE [Part::Cylinder] Cylinder1043  label="Cylinder1518"
  Angle = 360
  AttacherType = Attacher::AttachEngine3D
  Height = 10
  Placement = pos=(225,3,23) rot=(0,1,0;1.5708rad)
  Radius = 1
FEATURE [Part::MultiFuse] Fusion239
  Placement = pos=(0,82,0) rot=(0,0,1;0rad)
  Refine = true
  Shapes = -> [Cylinder1043,Cylinder1042]
FEATURE [Part::MultiFuse] Fusion240
  Placement = pos=(0.5,0,0) rot=(0,0,1;0rad)
  Refine = true
  Shapes = -> [Fusion237,Fusion239,Fusion238]
FEATURE [Part::Cut] Cut014200  label="Cut014400"
  Base = -> Cut014199
  Refine = true
  Tool = -> Fusion170
FEATURE [Part::Cut] Cut014201  label="front-wall-frame_"
  Base = -> Cut014200
  Refine = true
  Tool = -> Fusion240
FEATURE [Part::Box] Box618  label="Cube806"
  AttacherType = Attacher::AttachEngine3D
  Height = 45
  Length = 4
  Placement = pos=(-4,-44,16) rot=(0,0,1;0rad)
  Width = 293
FEATURE [Part::Box] Box619  label="Cube807"
  AttacherType = Attacher::AttachEngine3D
  Height = 33
  Length = 4
  Placement = pos=(-4,-40,22) rot=(0,0,1;0rad)
  Width = 285
FEATURE [Part::Cut] Cut014202  label="Cut014401"
  Base = -> Box618
  Refine = true
  Tool = -> Box619
FEATURE [Part::Box] Box620  label="Cube808"
  AttacherType = Attacher::AttachEngine3D
  Height = 7
  Length = 3
  Placement = pos=(-3,-40,35) rot=(0,0,1;0rad)
  Width = 286
FEATURE [Part::Chamfer] Chamfer130
  Base = -> Box620
  Edges = 2 edges r=1: [Edge2,Edge4]
  Placement = pos=(0,0,0.5) rot=(0,0,1;0rad)
FEATURE [Part::Chamfer] Chamfer131
  Base = -> Cut014202
  Edges = 2 edges r=2: [Edge5,Edge7]
FEATURE [Part::Box] Box621  label="Cube809"
  AttacherType = Attacher::AttachEngine3D
  Height = 1
  Length = 1
  Placement = pos=(-1,-40,28.5) rot=(0,0,1;0rad)
  Width = 286
FEATURE [Part::Chamfer] Chamfer132
  Base = -> Box621
  Edges = 2 edges r=0.2: [Edge2,Edge4]
FEATURE [Part::Box] Box622  label="Cube810"
  AttacherType = Attacher::AttachEngine3D
  Height = 1
  Length = 1
  Placement = pos=(-1,-40,28.5) rot=(0,0,1;0rad)
  Width = 286
FEATURE [Part::Chamfer] Chamfer133
  Base = -> Box622
  Edges = 2 edges r=0.2: [Edge2,Edge4]
  Placement = pos=(0,0,20) rot=(0,0,1;0rad)
FEATURE [Part::MultiFuse] Fusion248002016
  Placement = pos=(482.5,-3,5) rot=(0,0,1;1.5708rad)
  Refine = true
  Shapes = -> [Chamfer130,Chamfer132,Chamfer131,Chamfer133]
FEATURE [Part::Box] Box623  label="kipper-side-left-wall-frame-ALU"
  AttacherType = Attacher::AttachEngine3D
  Height = 42
  Length = 1
  Placement = pos=(527,-3,24) rot=(0,0,1;1.5708rad)
  Width = 293
FEATURE [Part::Box] Box664  label="Cube157"
  AttacherType = Attacher::AttachEngine3D
  Height = 4
  Length = 4
  Placement = pos=(58,-53.5,14) rot=(0,0,1;0rad)
  Width = 1
FEATURE [Part::Box] Box665  label="Cube158"
  AttacherType = Attacher::AttachEngine3D
  Height = 4
  Length = 6
  Placement = pos=(57,-53,14) rot=(0,0,1;0rad)
  Width = 1
FEATURE [Part::Chamfer] Chamfer134
  Base = -> Box665
  Edges = 1 edges r=0.99: [Edge10]
FEATURE [Part::Fillet] Fillet020
  Base = -> Chamfer134
  Edges = 1 edges r=0.99: [Edge8]
FEATURE [Part::Cut] Cut014203  label="Cut014402"
  Base = -> Fillet020
  Placement = pos=(181,45,6) rot=(0,0,1;0rad)
  Refine = true
  Tool = -> Box664
FEATURE [Part::Box] Box666  label="Cube159"
  AttacherType = Attacher::AttachEngine3D
  Height = 4
  Length = 6
  Placement = pos=(57,-53,14) rot=(0,0,1;0rad)
  Width = 1
FEATURE [Part::Chamfer] Chamfer135
  Base = -> Box666
  Edges = 1 edges r=0.99: [Edge10]
FEATURE [Part::Fillet] Fillet021
  Base = -> Chamfer135
  Edges = 1 edges r=0.99: [Edge8]
FEATURE [Part::Box] Box667  label="Cube160"
  AttacherType = Attacher::AttachEngine3D
  Height = 4
  Length = 4
  Placement = pos=(58,-53.5,14) rot=(0,0,1;0rad)
  Width = 1
FEATURE [Part::Cut] Cut014204  label="Cut014403"
  Base = -> Fillet021
  Placement = pos=(320,45,6) rot=(0,0,1;0rad)
  Refine = true
  Tool = -> Box667
FEATURE [Part::Box] Box668  label="Cube161"
  AttacherType = Attacher::AttachEngine3D
  Height = 4
  Length = 6
  Placement = pos=(57,-53,14) rot=(0,0,1;0rad)
  Width = 1
FEATURE [Part::Chamfer] Chamfer136
  Base = -> Box668
  Edges = 1 edges r=0.99: [Edge10]
FEATURE [Part::Fillet] Fillet022
  Base = -> Chamfer136
  Edges = 1 edges r=0.99: [Edge8]
FEATURE [Part::Box] Box669  label="Cube162"
  AttacherType = Attacher::AttachEngine3D
  Height = 4
  Length = 4
  Placement = pos=(58,-53.5,14) rot=(0,0,1;0rad)
  Width = 1
FEATURE [Part::Cut] Cut014205  label="Cut014404"
  Base = -> Fillet022
  Placement = pos=(252,45,6) rot=(0,0,1;0rad)
  Refine = true
  Tool = -> Box669
FEATURE [Part::Box] Box670  label="Cube163"
  AttacherType = Attacher::AttachEngine3D
  Height = 4
  Length = 6
  Placement = pos=(57,-53,14) rot=(0,0,1;0rad)
  Width = 1
FEATURE [Part::Chamfer] Chamfer062
  Base = -> Box670
  Edges = 1 edges r=0.99: [Edge10]
FEATURE [Part::Fillet] Fillet023
  Base = -> Chamfer062
  Edges = 1 edges r=0.99: [Edge8]
FEATURE [Part::Box] Box671  label="Cube164"
  AttacherType = Attacher::AttachEngine3D
  Height = 4
  Length = 4
  Placement = pos=(58,-53.5,14) rot=(0,0,1;0rad)
  Width = 1
FEATURE [Part::Cut] Cut014206  label="Cut014405"
  Base = -> Fillet023
  Placement = pos=(391,45,6) rot=(0,0,1;0rad)
  Refine = true
  Tool = -> Box671
FEATURE [Part::Box] Box672  label="Cube165"
  AttacherType = Attacher::AttachEngine3D
  Height = 4
  Length = 6
  Placement = pos=(57,-53,14) rot=(0,0,1;0rad)
  Width = 1
FEATURE [Part::Chamfer] Chamfer063
  Base = -> Box672
  Edges = 1 edges r=0.99: [Edge10]
FEATURE [Part::Fillet] Fillet024
  Base = -> Chamfer063
  Edges = 1 edges r=0.99: [Edge8]
FEATURE [Part::Box] Box673  label="Cube166"
  AttacherType = Attacher::AttachEngine3D
  Height = 4
  Length = 4
  Placement = pos=(58,-53.5,14) rot=(0,0,1;0rad)
  Width = 1
FEATURE [Part::Cut] Cut014207  label="Cut014406"
  Base = -> Fillet024
  Placement = pos=(459,45,6) rot=(0,0,1;0rad)
  Refine = true
  Tool = -> Box673
FEATURE [Part::MultiFuse] Fusion248002017
  Refine = true
  Shapes = -> [Cut014203,Cut014204,Cut014206,Cut014205,Cut014207]
FEATURE [Part::MultiFuse] Fusion248002018
  Refine = true
  Shapes = -> [Fusion248002016,Fusion248002017]
FEATURE [Part::Box] Box624  label="Cube811"
  AttacherType = Attacher::AttachEngine3D
  Height = 45
  Length = 4
  Placement = pos=(-4,-44,16) rot=(0,0,1;0rad)
  Width = 167
FEATURE [Part::Box] Box625  label="Cube812"
  AttacherType = Attacher::AttachEngine3D
  Height = 33
  Length = 4
  Placement = pos=(-4,-40,22) rot=(0,0,1;0rad)
  Width = 159
FEATURE [Part::Cut] Cut014208  label="Cut014407"
  Base = -> Box624
  Refine = true
  Tool = -> Box625
FEATURE [Part::Box] Box626  label="Cube813"
  AttacherType = Attacher::AttachEngine3D
  Height = 7
  Length = 3
  Placement = pos=(-3,-40,35) rot=(0,0,1;0rad)
  Width = 160
FEATURE [Part::Chamfer] Chamfer137
  Base = -> Box626
  Edges = 2 edges r=1: [Edge2,Edge4]
  Placement = pos=(0,0,0.5) rot=(0,0,1;0rad)
FEATURE [Part::Cylinder] Cylinder1044  label="Cylinder1519"
  Angle = 360
  AttacherType = Attacher::AttachEngine3D
  Height = 5
  Placement = pos=(533,6,69) rot=(1,0,0;1.5708rad)
  Radius = 0.9
FEATURE [Part::Cylinder] Cylinder1026  label="Cylinder1520"
  Angle = 360
  AttacherType = Attacher::AttachEngine3D
  Height = 5
  Placement = pos=(533,168,69) rot=(1,0,0;1.5708rad)
  Radius = 0.9
FEATURE [Part::Chamfer] Chamfer138
  Base = -> Cut014208
  Edges = 2 edges r=2: [Edge5,Edge7]
FEATURE [Part::Box] Box627  label="Cube814"
  AttacherType = Attacher::AttachEngine3D
  Height = 1
  Length = 1
  Placement = pos=(-1,-40,28.5) rot=(0,0,1;0rad)
  Width = 160
FEATURE [Part::Chamfer] Chamfer139
  Base = -> Box627
  Edges = 2 edges r=0.2: [Edge2,Edge4]
FEATURE [Part::Box] Box628  label="Cube815"
  AttacherType = Attacher::AttachEngine3D
  Height = 1
  Length = 1
  Placement = pos=(-1,-40,28.5) rot=(0,0,1;0rad)
  Width = 160
FEATURE [Part::Chamfer] Chamfer140
  Base = -> Box628
  Edges = 2 edges r=0.2: [Edge2,Edge4]
  Placement = pos=(0,0,20) rot=(0,0,1;0rad)
FEATURE [Part::MultiFuse] Fusion248002019
  Placement = pos=(229,45,5) rot=(0,0,1;0rad)
  Refine = true
  Shapes = -> [Chamfer137,Chamfer139,Chamfer138,Chamfer140]
FEATURE [Part::Cylinder] Cylinder1045  label="Cylinder1521"
  Angle = 360
  AttacherType = Attacher::AttachEngine3D
  Height = 10
  Placement = pos=(225,3,64) rot=(0,1,0;1.5708rad)
  Radius = 1
FEATURE [Part::Cylinder] Cylinder1046  label="Cylinder1522"
  Angle = 360
  AttacherType = Attacher::AttachEngine3D
  Height = 10
  Placement = pos=(225,3,25) rot=(0,1,0;1.5708rad)
  Radius = 1
FEATURE [Part::MultiFuse] Fusion248002020
  Refine = true
  Shapes = -> [Cylinder1046,Cylinder1045]
FEATURE [Part::Cylinder] Cylinder1047  label="Cylinder1523"
  Angle = 360
  AttacherType = Attacher::AttachEngine3D
  Height = 10
  Placement = pos=(225,3,64) rot=(0,1,0;1.5708rad)
  Radius = 1
FEATURE [Part::Cylinder] Cylinder1048  label="Cylinder1524"
  Angle = 360
  AttacherType = Attacher::AttachEngine3D
  Height = 10
  Placement = pos=(225,3,25) rot=(0,1,0;1.5708rad)
  Radius = 1
FEATURE [Part::MultiFuse] Fusion248002021
  Placement = pos=(0,164,0) rot=(0,0,1;0rad)
  Refine = true
  Shapes = -> [Cylinder1048,Cylinder1047]
FEATURE [Part::Cylinder] Cylinder1049  label="Cylinder1525"
  Angle = 360
  AttacherType = Attacher::AttachEngine3D
  Height = 10
  Placement = pos=(225,3,64) rot=(0,1,0;1.5708rad)
  Radius = 1
FEATURE [Part::Cylinder] Cylinder1050  label="Cylinder1526"
  Angle = 360
  AttacherType = Attacher::AttachEngine3D
  Height = 10
  Placement = pos=(224,3,25) rot=(0,1,0;1.5708rad)
  Radius = 1
FEATURE [Part::MultiFuse] Fusion248002022
  Placement = pos=(0,82,0) rot=(0,0,1;0rad)
  Refine = true
  Shapes = -> [Cylinder1050,Cylinder1049]
FEATURE [Part::MultiFuse] Fusion248002023
  Placement = pos=(299.5,0,0) rot=(0,0,1;0rad)
  Refine = true
  Shapes = -> [Fusion248002020,Fusion248002022,Fusion248002021]
FEATURE [Part::MultiFuse] Fusion248002024
  Refine = true
  Shapes = -> [Cylinder1044,Cylinder1026]
FEATURE [Part::Mirroring] Part__Mirroring109  label="Fusion251 (Mirror #5)"
  Base = (0,0,0)
  Normal = (1,0,0)
  Placement = pos=(760,0,0) rot=(0,0,1;0rad)
  Source = -> Fusion248002019
FEATURE [Part::Chamfer] Chamfer141
  Base = -> Part__Mirroring109
  Edges = 1 edges r=3: [Edge63]
FEATURE [Part::Cut] Cut014209  label="Cut014408"
  Base = -> Chamfer141
  Refine = true
  Tool = -> Fusion248002023
FEATURE [Part::Chamfer] Chamfer075
  Base = -> Fusion248002018
  Edges = 1 edges r=3: [Edge35]
FEATURE [Part::Box] Box114  label="Cube113"
  AttacherType = Attacher::AttachEngine3D
  Height = 41
  Length = 6
  Placement = pos=(223,25,21) rot=(0,0,1;0rad)
  Width = 3
FEATURE [Part::Chamfer] Chamfer076
  Base = -> Box114
  Edges = 1 edges: [Edge2 r1=8 r2=3]
FEATURE [Part::Box] Box629  label="Cube816"
  AttacherType = Attacher::AttachEngine3D
  Height = 41
  Length = 6
  Placement = pos=(223,25,21) rot=(0,0,1;0rad)
  Width = 3
FEATURE [Part::Chamfer] Chamfer077
  Base = -> Box629
  Edges = 1 edges: [Edge2 r1=8 r2=3]
  Placement = pos=(0,117,0) rot=(0,0,1;0rad)
FEATURE [Part::Box] Box630  label="Cube817"
  AttacherType = Attacher::AttachEngine3D
  Height = 41
  Length = 6
  Placement = pos=(223,25,21) rot=(0,0,1;0rad)
  Width = 3
FEATURE [Part::Chamfer] Chamfer078
  Base = -> Box630
  Edges = 1 edges: [Edge2 r1=8 r2=3]
  Placement = pos=(0,59,0) rot=(0,0,1;0rad)
FEATURE [Part::MultiFuse] Fusion248002025  label="kipper-front-wall-frame"
  Refine = true
  Shapes = -> [Cut014201,Chamfer076,Chamfer077,Chamfer078]
FEATURE [Part::Box] Box674  label="Cube820"
  AttacherType = Attacher::AttachEngine3D
  Height = 5
  Length = 4
  Placement = pos=(531,1,66) rot=(0,0,1;0rad)
  Width = 10
FEATURE [Part::Chamfer] Chamfer142
  Base = -> Box674
  Edges = 1 edges r=4.999: [Edge12]
FEATURE [Part::Box] Box675  label="Cube821"
  AttacherType = Attacher::AttachEngine3D
  Height = 5
  Length = 4
  Placement = pos=(531,159,66) rot=(0,0,1;0rad)
  Width = 10
FEATURE [Part::Chamfer] Chamfer143
  Base = -> Box675
  Edges = 1 edges r=4.999: [Edge10]
  Placement = pos=(0,-1,0) rot=(0,0,1;0rad)
FEATURE [Part::MultiFuse] Fusion248002026
  Refine = true
  Shapes = -> [Cut014209,Chamfer142,Chamfer143]
FEATURE [Part::Cut] Cut014210  label="Cut014409"
  Base = -> Fusion248002026
  Placement = pos=(0,0.5,0) rot=(0,0,1;0rad)
  Refine = true
  Tool = -> Fusion248002024
FEATURE [Part::Box] Box676  label="kipper-rear-wall-frame-ALU"
  AttacherType = Attacher::AttachEngine3D
  Height = 42
  Length = 1
  Placement = pos=(530,1,24) rot=(0,0,1;0rad)
  Width = 168
FEATURE [Part::Box] Box636  label="Cube822"
  AttacherType = Attacher::AttachEngine3D
  Height = 4
  Length = 4
  Placement = pos=(58,-53.5,14) rot=(0,0,1;0rad)
  Width = 1
FEATURE [Part::Box] Box637  label="Cube855"
  AttacherType = Attacher::AttachEngine3D
  Height = 4
  Length = 6
  Placement = pos=(57,-53,14) rot=(0,0,1;0rad)
  Width = 1
FEATURE [Part::Chamfer] Chamfer144
  Base = -> Box637
  Edges = 1 edges r=0.99: [Edge10]
FEATURE [Part::Fillet] Fillet270
  Base = -> Chamfer144
  Edges = 1 edges r=0.99: [Edge8]
FEATURE [Part::Cut] Cut014211  label="Cut014410"
  Base = -> Fillet270
  Placement = pos=(483,74,6) rot=(0,0,1;1.5708rad)
  Refine = true
  Tool = -> Box636
FEATURE [Part::Box] Box638  label="Cube856"
  AttacherType = Attacher::AttachEngine3D
  Height = 4
  Length = 4
  Placement = pos=(58,-53.5,14) rot=(0,0,1;0rad)
  Width = 1
FEATURE [Part::Box] Box639  label="Cube857"
  AttacherType = Attacher::AttachEngine3D
  Height = 4
  Length = 6
  Placement = pos=(57,-53,14) rot=(0,0,1;0rad)
  Width = 1
FEATURE [Part::Chamfer] Chamfer082
  Base = -> Box639
  Edges = 1 edges r=0.99: [Edge10]
FEATURE [Part::Fillet] Fillet271
  Base = -> Chamfer082
  Edges = 1 edges r=0.99: [Edge8]
FEATURE [Part::Cut] Cut014212  label="Cut014411"
  Base = -> Fillet271
  Placement = pos=(483,-23,6) rot=(0,0,1;1.5708rad)
  Refine = true
  Tool = -> Box638
FEATURE [Part::MultiFuse] Fusion248002027  label="kipper-rear-wall-frame"
  Refine = true
  Shapes = -> [Cut014210,Cut014211,Cut014212]
FEATURE [Part::Cylinder] Cylinder1051  label="Cylinder1527"
  Angle = 360
  AttacherType = Attacher::AttachEngine3D
  Height = 10
  Placement = pos=(235.5,3.5,64) rot=(1,0,0;1.5708rad)
  Radius = 1
FEATURE [Part::Cylinder] Cylinder1052  label="Cylinder1528"
  Angle = 360
  AttacherType = Attacher::AttachEngine3D
  Height = 10
  Placement = pos=(235.5,3.5,25) rot=(1,0,0;1.5708rad)
  Radius = 1
FEATURE [Part::MultiFuse] Fusion248002028
  Refine = true
  Shapes = -> [Cylinder1052,Cylinder1051]
FEATURE [Part::Cylinder] Cylinder1053  label="Cylinder1529"
  Angle = 360
  AttacherType = Attacher::AttachEngine3D
  Height = 10
  Placement = pos=(235.5,3.5,64) rot=(1,0,0;1.5708rad)
  Radius = 1
FEATURE [Part::Cylinder] Cylinder1054  label="Cylinder1530"
  Angle = 360
  AttacherType = Attacher::AttachEngine3D
  Height = 10
  Placement = pos=(235.5,4.25,25) rot=(1,0,0;1.5708rad)
  Radius = 1
FEATURE [Part::MultiFuse] Fusion248002029
  Placement = pos=(72,0,0) rot=(0,0,1;0rad)
  Refine = true
  Shapes = -> [Cylinder1054,Cylinder1053]
FEATURE [Part::Cylinder] Cylinder1055  label="Cylinder1531"
  Angle = 360
  AttacherType = Attacher::AttachEngine3D
  Height = 10
  Placement = pos=(235.5,3.5,64) rot=(1,0,0;1.5708rad)
  Radius = 1
FEATURE [Part::Cylinder] Cylinder1056  label="Cylinder1532"
  Angle = 360
  AttacherType = Attacher::AttachEngine3D
  Height = 10
  Placement = pos=(235.5,4.25,25) rot=(1,0,0;1.5708rad)
  Radius = 1
FEATURE [Part::MultiFuse] Fusion248002030
  Placement = pos=(144,0,0) rot=(0,0,1;0rad)
  Refine = true
  Shapes = -> [Cylinder1056,Cylinder1055]
FEATURE [Part::Cylinder] Cylinder1057  label="Cylinder1533"
  Angle = 360
  AttacherType = Attacher::AttachEngine3D
  Height = 10
  Placement = pos=(235.5,3.5,64) rot=(1,0,0;1.5708rad)
  Radius = 1
FEATURE [Part::Cylinder] Cylinder1058  label="Cylinder1534"
  Angle = 360
  AttacherType = Attacher::AttachEngine3D
  Height = 10
  Placement = pos=(235.5,3.5,25) rot=(1,0,0;1.5708rad)
  Radius = 1
FEATURE [Part::MultiFuse] Fusion248002031
  Placement = pos=(217,0,0) rot=(0,0,1;0rad)
  Refine = true
  Shapes = -> [Cylinder1058,Cylinder1057]
FEATURE [Part::Cylinder] Cylinder1059  label="Cylinder1535"
  Angle = 360
  AttacherType = Attacher::AttachEngine3D
  Height = 10
  Placement = pos=(235.5,3.5,64) rot=(1,0,0;1.5708rad)
  Radius = 1
FEATURE [Part::Cylinder] Cylinder1060  label="Cylinder1536"
  Angle = 360
  AttacherType = Attacher::AttachEngine3D
  Height = 10
  Placement = pos=(235.5,4.25,25) rot=(1,0,0;1.5708rad)
  Radius = 1
FEATURE [Part::MultiFuse] Fusion248002032
  Placement = pos=(289,0,0) rot=(0,0,1;0rad)
  Refine = true
  Shapes = -> [Cylinder1060,Cylinder1059]
FEATURE [Part::MultiFuse] Fusion248002033
  Refine = true
  Shapes = -> [Fusion248002028,Fusion248002029,Fusion248002032,Fusion248002030,Fusion248002031]
FEATURE [Part::Box] Box640  label="Cube858"
  AttacherType = Attacher::AttachEngine3D
  Height = 5
  Length = 4
  Placement = pos=(531,1,66) rot=(0,0,1;0rad)
  Width = 10
FEATURE [Part::Chamfer] Chamfer083
  Base = -> Box640
  Edges = 1 edges r=4.999: [Edge12]
  Placement = pos=(232.5,528,0) rot=(0,0,-1;1.5708rad)
FEATURE [Part::Box] Box641  label="Cube827"
  AttacherType = Attacher::AttachEngine3D
  Height = 5
  Length = 4
  Placement = pos=(531,159,66) rot=(0,0,1;0rad)
  Width = 10
FEATURE [Part::Chamfer] Chamfer084
  Base = -> Box641
  Edges = 1 edges r=4.999: [Edge10]
  Placement = pos=(357.5,528,0) rot=(0,0,-1;1.5708rad)
FEATURE [Part::Cylinder] Cylinder1061  label="Cylinder1537"
  Angle = 360
  AttacherType = Attacher::AttachEngine3D
  Height = 5
  Placement = pos=(233.5,-5,68.5) rot=(0,1,0;1.5708rad)
  Radius = 1
FEATURE [Part::Cylinder] Cylinder1062  label="Cylinder1538"
  Angle = 360
  AttacherType = Attacher::AttachEngine3D
  Height = 5
  Placement = pos=(521.5,-5,68.5) rot=(0,1,0;1.5708rad)
  Radius = 1
FEATURE [Part::MultiFuse] Fusion248002034
  Refine = true
  Shapes = -> [Cylinder1061,Cylinder1062]
FEATURE [Part::MultiFuse] Fusion248002035
  Refine = true
  Shapes = -> [Chamfer075,Chamfer084,Chamfer083]
FEATURE [Part::Cut] Cut014213  label="Cut014412"
  Base = -> Fusion248002035
  Refine = true
  Tool = -> Fusion248002034
FEATURE [Part::Cut] Cut014214  label="kipper-side-left-wall-frame"
  Base = -> Cut014213
  Refine = true
  Tool = -> Fusion248002033
FEATURE [Part::Box] Box642  label="Cube828"
  AttacherType = Attacher::AttachEngine3D
  Height = 45
  Length = 4
  Placement = pos=(-4,-44,16) rot=(0,0,1;0rad)
  Width = 293
FEATURE [Part::Box] Box643  label="Cube829"
  AttacherType = Attacher::AttachEngine3D
  Height = 33
  Length = 4
  Placement = pos=(-4,-40,22) rot=(0,0,1;0rad)
  Width = 285
FEATURE [Part::Cut] Cut014215  label="Cut014413"
  Base = -> Box642
  Refine = true
  Tool = -> Box643
FEATURE [Part::Box] Box644  label="Cube830"
  AttacherType = Attacher::AttachEngine3D
  Height = 7
  Length = 3
  Placement = pos=(-3,-40,35) rot=(0,0,1;0rad)
  Width = 286
FEATURE [Part::Chamfer] Chamfer085
  Base = -> Box644
  Edges = 2 edges r=1: [Edge2,Edge4]
  Placement = pos=(0,0,0.5) rot=(0,0,1;0rad)
FEATURE [Part::Chamfer] Chamfer086
  Base = -> Cut014215
  Edges = 2 edges r=2: [Edge5,Edge7]
FEATURE [Part::Box] Box645  label="Cube831"
  AttacherType = Attacher::AttachEngine3D
  Height = 1
  Length = 1
  Placement = pos=(-1,-40,28.5) rot=(0,0,1;0rad)
  Width = 286
FEATURE [Part::Chamfer] Chamfer087
  Base = -> Box645
  Edges = 2 edges r=0.2: [Edge2,Edge4]
FEATURE [Part::Box] Box646  label="Cube832"
  AttacherType = Attacher::AttachEngine3D
  Height = 1
  Length = 1
  Placement = pos=(-1,-40,28.5) rot=(0,0,1;0rad)
  Width = 286
FEATURE [Part::Chamfer] Chamfer088
  Base = -> Box646
  Edges = 2 edges r=0.2: [Edge2,Edge4]
  Placement = pos=(0,0,20) rot=(0,0,1;0rad)
FEATURE [Part::MultiFuse] Fusion248002036
  Placement = pos=(482.5,-3,5) rot=(0,0,1;1.5708rad)
  Refine = true
  Shapes = -> [Chamfer085,Chamfer087,Chamfer086,Chamfer088]
FEATURE [Part::Box] Box647  label="Cube833"
  AttacherType = Attacher::AttachEngine3D
  Height = 4
  Length = 4
  Placement = pos=(58,-53.5,14) rot=(0,0,1;0rad)
  Width = 1
FEATURE [Part::Box] Box648  label="Cube834"
  AttacherType = Attacher::AttachEngine3D
  Height = 4
  Length = 6
  Placement = pos=(57,-53,14) rot=(0,0,1;0rad)
  Width = 1
FEATURE [Part::Chamfer] Chamfer089
  Base = -> Box648
  Edges = 1 edges r=0.99: [Edge10]
FEATURE [Part::Fillet] Fillet272
  Base = -> Chamfer089
  Edges = 1 edges r=0.99: [Edge8]
FEATURE [Part::Cut] Cut014216  label="Cut014414"
  Base = -> Fillet272
  Placement = pos=(181,45,6) rot=(0,0,1;0rad)
  Refine = true
  Tool = -> Box647
FEATURE [Part::Box] Box677  label="Cube835"
  AttacherType = Attacher::AttachEngine3D
  Height = 4
  Length = 6
  Placement = pos=(57,-53,14) rot=(0,0,1;0rad)
  Width = 1
FEATURE [Part::Chamfer] Chamfer090
  Base = -> Box677
  Edges = 1 edges r=0.99: [Edge10]
FEATURE [Part::Fillet] Fillet007014
  Base = -> Chamfer090
  Edges = 1 edges r=0.99: [Edge8]
FEATURE [Part::Box] Box678  label="Cube836"
  AttacherType = Attacher::AttachEngine3D
  Height = 4
  Length = 4
  Placement = pos=(58,-53.5,14) rot=(0,0,1;0rad)
  Width = 1
FEATURE [Part::Cut] Cut014217  label="Cut014415"
  Base = -> Fillet007014
  Placement = pos=(320,45,6) rot=(0,0,1;0rad)
  Refine = true
  Tool = -> Box678
FEATURE [Part::Box] Box679  label="Cube837"
  AttacherType = Attacher::AttachEngine3D
  Height = 4
  Length = 6
  Placement = pos=(57,-53,14) rot=(0,0,1;0rad)
  Width = 1
FEATURE [Part::Chamfer] Chamfer091
  Base = -> Box679
  Edges = 1 edges r=0.99: [Edge10]
FEATURE [Part::Fillet] Fillet007015
  Base = -> Chamfer091
  Edges = 1 edges r=0.99: [Edge8]
FEATURE [Part::Box] Box680  label="Cube838"
  AttacherType = Attacher::AttachEngine3D
  Height = 4
  Length = 4
  Placement = pos=(58,-53.5,14) rot=(0,0,1;0rad)
  Width = 1
FEATURE [Part::Cut] Cut014218  label="Cut014416"
  Base = -> Fillet007015
  Placement = pos=(252,45,6) rot=(0,0,1;0rad)
  Refine = true
  Tool = -> Box680
FEATURE [Part::Box] Box681  label="Cube839"
  AttacherType = Attacher::AttachEngine3D
  Height = 4
  Length = 6
  Placement = pos=(57,-53,14) rot=(0,0,1;0rad)
  Width = 1
FEATURE [Part::Chamfer] Chamfer092
  Base = -> Box681
  Edges = 1 edges r=0.99: [Edge10]
FEATURE [Part::Fillet] Fillet007016
  Base = -> Chamfer092
  Edges = 1 edges r=0.99: [Edge8]
FEATURE [Part::Box] Box682  label="Cube859"
  AttacherType = Attacher::AttachEngine3D
  Height = 4
  Length = 4
  Placement = pos=(58,-53.5,14) rot=(0,0,1;0rad)
  Width = 1
FEATURE [Part::Cut] Cut014219  label="Cut014417"
  Base = -> Fillet007016
  Placement = pos=(391,45,6) rot=(0,0,1;0rad)
  Refine = true
  Tool = -> Box682
FEATURE [Part::Box] Box683  label="Cube860"
  AttacherType = Attacher::AttachEngine3D
  Height = 4
  Length = 6
  Placement = pos=(57,-53,14) rot=(0,0,1;0rad)
  Width = 1
FEATURE [Part::Chamfer] Chamfer093
  Base = -> Box683
  Edges = 1 edges r=0.99: [Edge10]
FEATURE [Part::Fillet] Fillet007017
  Base = -> Chamfer093
  Edges = 1 edges r=0.99: [Edge8]
FEATURE [Part::Box] Box684  label="Cube861"
  AttacherType = Attacher::AttachEngine3D
  Height = 4
  Length = 4
  Placement = pos=(58,-53.5,14) rot=(0,0,1;0rad)
  Width = 1
FEATURE [Part::Cut] Cut014220  label="Cut014418"
  Base = -> Fillet007017
  Placement = pos=(459,45,6) rot=(0,0,1;0rad)
  Refine = true
  Tool = -> Box684
FEATURE [Part::MultiFuse] Fusion248002037
  Refine = true
  Shapes = -> [Cut014216,Cut014217,Cut014219,Cut014218,Cut014220]
FEATURE [Part::MultiFuse] Fusion248002038
  Refine = true
  Shapes = -> [Fusion248002036,Fusion248002037]
FEATURE [Part::Chamfer] Chamfer094
  Base = -> Fusion248002038
  Edges = 1 edges r=3: [Edge35]
FEATURE [Part::Cylinder] Cylinder1063  label="Cylinder1539"
  Angle = 360
  AttacherType = Attacher::AttachEngine3D
  Height = 10
  Placement = pos=(235.5,3.5,64) rot=(1,0,0;1.5708rad)
  Radius = 1
FEATURE [Part::Cylinder] Cylinder1064  label="Cylinder1540"
  Angle = 360
  AttacherType = Attacher::AttachEngine3D
  Height = 10
  Placement = pos=(235.5,3.5,25) rot=(1,0,0;1.5708rad)
  Radius = 1
FEATURE [Part::MultiFuse] Fusion248002039
  Refine = true
  Shapes = -> [Cylinder1064,Cylinder1063]
FEATURE [Part::Cylinder] Cylinder1065  label="Cylinder1541"
  Angle = 360
  AttacherType = Attacher::AttachEngine3D
  Height = 10
  Placement = pos=(235.5,3.5,64) rot=(1,0,0;1.5708rad)
  Radius = 1
FEATURE [Part::Cylinder] Cylinder1066  label="Cylinder1542"
  Angle = 360
  AttacherType = Attacher::AttachEngine3D
  Height = 10
  Placement = pos=(235.5,4.25,25) rot=(1,0,0;1.5708rad)
  Radius = 1
FEATURE [Part::MultiFuse] Fusion248002040
  Placement = pos=(72,0,0) rot=(0,0,1;0rad)
  Refine = true
  Shapes = -> [Cylinder1066,Cylinder1065]
FEATURE [Part::Cylinder] Cylinder1067  label="Cylinder1543"
  Angle = 360
  AttacherType = Attacher::AttachEngine3D
  Height = 10
  Placement = pos=(235.5,3.5,64) rot=(1,0,0;1.5708rad)
  Radius = 1
FEATURE [Part::Cylinder] Cylinder1068  label="Cylinder1544"
  Angle = 360
  AttacherType = Attacher::AttachEngine3D
  Height = 10
  Placement = pos=(235.5,4.25,25) rot=(1,0,0;1.5708rad)
  Radius = 1
FEATURE [Part::MultiFuse] Fusion248002041
  Placement = pos=(144,0,0) rot=(0,0,1;0rad)
  Refine = true
  Shapes = -> [Cylinder1068,Cylinder1067]
FEATURE [Part::Cylinder] Cylinder1069  label="Cylinder1545"
  Angle = 360
  AttacherType = Attacher::AttachEngine3D
  Height = 10
  Placement = pos=(235.5,3.5,64) rot=(1,0,0;1.5708rad)
  Radius = 1
FEATURE [Part::Cylinder] Cylinder1070  label="Cylinder1546"
  Angle = 360
  AttacherType = Attacher::AttachEngine3D
  Height = 10
  Placement = pos=(235.5,3.5,25) rot=(1,0,0;1.5708rad)
  Radius = 1
FEATURE [Part::MultiFuse] Fusion248002042
  Placement = pos=(217,0,0) rot=(0,0,1;0rad)
  Refine = true
  Shapes = -> [Cylinder1070,Cylinder1069]
FEATURE [Part::Cylinder] Cylinder1071  label="Cylinder1547"
  Angle = 360
  AttacherType = Attacher::AttachEngine3D
  Height = 10
  Placement = pos=(235.5,3.5,64) rot=(1,0,0;1.5708rad)
  Radius = 1
FEATURE [Part::Cylinder] Cylinder1072  label="Cylinder1548"
  Angle = 360
  AttacherType = Attacher::AttachEngine3D
  Height = 10
  Placement = pos=(235.5,4.25,25) rot=(1,0,0;1.5708rad)
  Radius = 1
FEATURE [Part::MultiFuse] Fusion248002043
  Placement = pos=(289,0,0) rot=(0,0,1;0rad)
  Refine = true
  Shapes = -> [Cylinder1072,Cylinder1071]
FEATURE [Part::MultiFuse] Fusion248002044
  Refine = true
  Shapes = -> [Fusion248002039,Fusion248002040,Fusion248002043,Fusion248002041,Fusion248002042]
FEATURE [Part::Box] Box685  label="Cube862"
  AttacherType = Attacher::AttachEngine3D
  Height = 5
  Length = 4
  Placement = pos=(531,1,66) rot=(0,0,1;0rad)
  Width = 10
FEATURE [Part::Chamfer] Chamfer095
  Base = -> Box685
  Edges = 1 edges r=4.999: [Edge12]
  Placement = pos=(232.5,528,0) rot=(0,0,-1;1.5708rad)
FEATURE [Part::Box] Box686  label="Cube863"
  AttacherType = Attacher::AttachEngine3D
  Height = 5
  Length = 4
  Placement = pos=(531,159,66) rot=(0,0,1;0rad)
  Width = 10
FEATURE [Part::Chamfer] Chamfer096
  Base = -> Box686
  Edges = 1 edges r=4.999: [Edge10]
  Placement = pos=(357.5,528,0) rot=(0,0,-1;1.5708rad)
FEATURE [Part::Cylinder] Cylinder1073  label="Cylinder1549"
  Angle = 360
  AttacherType = Attacher::AttachEngine3D
  Height = 5
  Placement = pos=(233.5,-5,68.5) rot=(0,1,0;1.5708rad)
  Radius = 1
FEATURE [Part::Cylinder] Cylinder1074  label="Cylinder1550"
  Angle = 360
  AttacherType = Attacher::AttachEngine3D
  Height = 5
  Placement = pos=(521.5,-5,68.5) rot=(0,1,0;1.5708rad)
  Radius = 1
FEATURE [Part::MultiFuse] Fusion248002045
  Refine = true
  Shapes = -> [Cylinder1073,Cylinder1074]
FEATURE [Part::MultiFuse] Fusion248002046
  Refine = true
  Shapes = -> [Chamfer094,Chamfer096,Chamfer095]
FEATURE [Part::Cut] Cut014221  label="Cut014419"
  Base = -> Fusion248002046
  Refine = true
  Tool = -> Fusion248002045
FEATURE [Part::Cut] Cut014222  label="side-left-wall-frame001"
  Base = -> Cut014221
  Refine = true
  Tool = -> Fusion248002044
FEATURE [Part::Mirroring] Part__Mirroring110  label="kipper-side-right-wall-frame"
  Base = (0,0,0)
  Normal = (0,1,0)
  Placement = pos=(0,170,0) rot=(0,0,1;0rad)
  Source = -> Cut014222
FEATURE [Part::Box] Box687  label="kipper-side-right-wall-frame-ALU"
  AttacherType = Attacher::AttachEngine3D
  Height = 42
  Length = 1
  Placement = pos=(527,172,24) rot=(0,0,1;1.5708rad)
  Width = 293
FEATURE [Part::MultiFuse] Fusion248002047  label="kipper-frame"
  Refine = true
  Shapes = -> [Cut014197,Cut014196,Cut014195,Box663,Box662]
FEATURE [Part::MultiFuse] Fusion248002048
  Refine = true
  Shapes = -> [Box603,Cylinder1035,Box661,Box602]
FEATURE [Part::Fillet] Fillet007018  label="kipper-frame-ALU"
  Base = -> Fusion248002048
  Edges = 2 edges r=5: [Edge39,Edge45]
FEATURE [App::DocumentObjectGroup] Group002  label="kipper"
  Group = -> [Box121,Box613,Fusion236,Box623,Fusion248002025,Box676,Fusion248002027,Cut014214,Part__Mirroring110,Box687,Fusion248002047,Fillet007018]
FEATURE [App::DocumentObjectGroup] Group003  label="fuel-tank"
  Group = -> [Cut014143,Cut014152,Fillet405,Fillet407,Chamfer119,Chamfer120,Box520]
FEATURE [App::DocumentObjectGroup] Group005  label="front-steering-servo"
  Group = -> [Chamfer104,Cylinder889,Cylinder930,Cut688,Fusion588,Cut694,Fillet357]
FEATURE [App::DocumentObjectGroup] Group006  label="gearbox"
  Group = -> [Cylinder798,Fillet007001,Cut014064,Cut014065]
FEATURE [App::DocumentObjectGroup] Group007  label="suspensions"
  Group = -> [Fusion091,Fusion432,Fusion439,Fusion440,Fusion443,Fusion446,Cut568,Part__Mirroring092,Fusion008,Fusion459,Cut021,Cut583,Cut587,Part__Mirroring094,Cut590,Fusion563,Part__Mirroring105]
FEATURE [App::DocumentObjectGroup] Group008  label="battery-box-air-tanks"
  Group = -> [Cut014179,Cut014185,Cut014186]
FEATURE [Part::Cylinder] Cylinder1075  label="Cylinder1551"
  Angle = 360
  AttacherType = Attacher::AttachEngine3D
  Height = 11.5
  Placement = pos=(133,85,5.5) rot=(0,1,0;1.5708rad)
  Radius = 5.5
FEATURE [Part::Cylinder] Cylinder1076  label="Cylinder1552"
  Angle = 360
  AttacherType = Attacher::AttachEngine3D
  Height = 11.5
  Placement = pos=(218,85,-6.75) rot=(0,1,0;1.5708rad)
  Radius = 5.5
FEATURE [Part::Cylinder] Cylinder1077  label="Cylinder1553"
  Angle = 360
  AttacherType = Attacher::AttachEngine3D
  Height = 74
  Placement = pos=(144.5,85,5.5) rot=(0,1,0;1.7366rad)
  Radius = 2.5
FEATURE [Part::MultiFuse] Fusion248002049  label="gearbox-prop-shaft"
  Refine = true
  Shapes = -> [Cylinder1075,Cylinder1077,Cylinder1076]
FEATURE [Part::Cylinder] Cylinder1078  label="Cylinder1554"
  Angle = 360
  AttacherType = Attacher::AttachEngine3D
  Height = 47
  Placement = pos=(166,0,-44) rot=(0,0,1;0rad)
  Radius = 14
FEATURE [Part::Fillet] Fillet007019
  Base = -> Cylinder1078
  Edges = 2 edges r=7: [Edge1,Edge3]
FEATURE [Part::Box] Box688  label="Cube864"
  AttacherType = Attacher::AttachEngine3D
  Height = 10
  Length = 32
  Placement = pos=(151,-16,2) rot=(0,0,1;0rad)
  Width = 32
FEATURE [Part::Box] Box689  label="Cube865"
  AttacherType = Attacher::AttachEngine3D
  Height = 10
  Length = 32
  Placement = pos=(151,-16,-53) rot=(0,0,1;0rad)
  Width = 32
FEATURE [Part::MultiFuse] Fusion248002050  label="Fusion248002144"
  Refine = true
  Shapes = -> [Box689,Box688]
FEATURE [Part::Cut] Cut014223  label="Cut014420"
  Base = -> Fillet007019
  Placement = pos=(7.5,31,0) rot=(0,0,1;0rad)
  Refine = true
  Tool = -> Fusion248002050
FEATURE [Part::Feature] Face053
  Placement = pos=(0.5,0,1) rot=(0,0,1;0rad)
  shape: bbox 22.75 x 20.11 x 2e-07 mm, 1 faces, 0 solids (baked)
FEATURE [Part::Box] Box690  label="Cube866"
  AttacherType = Attacher::AttachEngine3D
  Height = 11
  Length = 10
  Placement = pos=(154,24,-10) rot=(0,0,1;0rad)
  Width = 14
FEATURE [Part::Fillet] Fillet007020
  Base = -> Box690
  Edges = 4 edges r=4: [Edge9,Edge10,Edge11,Edge12]
  Placement = pos=(12.7075,0,55.068) rot=(0,1,0;0.349066rad)
FEATURE [Part::Feature] Face054
  shape: bbox 15.41 x 11.89 x 2e-07 mm, 1 faces, 0 solids (baked)
FEATURE [Part::Feature] Face055
  shape: bbox 6.072 x 6.626 x 3.506 mm, 1 faces, 0 solids (baked)
FEATURE [Part::Loft] Loft020
  Closed = false
  MaxDegree = 5
  Placement = pos=(0,0,3) rot=(0,0,1;0rad)
  Ruled = false
  Sections = -> [Face054,Face055]
  Solid = true
FEATURE [Part::Cylinder] Cylinder1079  label="Cylinder1555"
  Angle = 360
  AttacherType = Attacher::AttachEngine3D
  Height = 39
  Placement = pos=(166,0,-40) rot=(0,0,1;0rad)
  Radius = 12
FEATURE [Part::Chamfer] Chamfer145
  Base = -> Cylinder1079
  Edges = 2 edges r=7: [Edge1,Edge3]
  Placement = pos=(7.5,31,0) rot=(0,0,1;0rad)
FEATURE [Part::Feature] Face056
  shape: bbox 4.139 x 15.4 x 11.37 mm, 1 faces, 0 solids (baked)
FEATURE [Part::Loft] Loft021
  Closed = false
  MaxDegree = 5
  Ruled = false
  Sections = -> [Face056,Face053]
  Solid = true
FEATURE [Part::MultiFuse] Fusion248002051  label="Fusion248002055"
  Refine = true
  Shapes = -> [Loft021,Fillet007020]
FEATURE [Part::Cut] Cut014224  label="Cut014421"
  Base = -> Fusion248002051
  Refine = true
  Tool = -> Loft020
FEATURE [Part::Cylinder] Cylinder1080  label="Cylinder1556"
  Angle = 360
  AttacherType = Attacher::AttachEngine3D
  Height = 10
  Placement = pos=(171,45,-2) rot=(0.994721,0.05438,0.087027;2.02933rad)
  Radius = 6
FEATURE [Part::Cylinder] Cylinder1081  label="Cylinder1557"
  Angle = 360
  AttacherType = Attacher::AttachEngine3D
  Height = 23
  Placement = pos=(163,51,7) rot=(0,-1,0;1.36136rad)
  Radius = 6
FEATURE [Part::Cylinder] Cylinder1082  label="Cylinder1558"
  Angle = 360
  AttacherType = Attacher::AttachEngine3D
  Height = 9
  Placement = pos=(167.5,31,-20) rot=(0,0,1;0rad)
  Radius = 14.1
FEATURE [Part::Cylinder] Cylinder1083  label="Cylinder1559"
  Angle = 360
  AttacherType = Attacher::AttachEngine3D
  Height = 9
  Placement = pos=(167.5,31,-20) rot=(0,0,1;0rad)
  Radius = 15.1
FEATURE [Part::Cut] Cut014225  label="air-box-holder_002"
  Base = -> Cylinder1083
  Placement = pos=(6,0,1) rot=(0,0,1;0rad)
  Refine = true
  Tool = -> Cylinder1082
FEATURE [Part::Feature] Face057
  shape: bbox 3.676 x 13.23 x 17.3 mm, 1 faces, 0 solids (baked)
FEATURE [Part::Feature] Face058
  shape: bbox 17.79 x 7.863 x 12.24 mm, 1 faces, 0 solids (baked)
FEATURE [Part::Loft] Loft022
  Closed = false
  MaxDegree = 5
  Ruled = false
  Sections = -> [Face057,Face058]
  Solid = true
FEATURE [Part::MultiFuse] Fusion248002053
  Refine = true
  Shapes = -> [Cylinder1081,Cylinder1080,Loft022]
FEATURE [Part::Cylinder] Cylinder1084  label="Cylinder1560"
  Angle = 360
  AttacherType = Attacher::AttachEngine3D
  Height = 15
  Placement = pos=(167.5,31,2) rot=(0,0,1;0rad)
  Radius = 13
FEATURE [Part::Cylinder] Cylinder1085  label="Cylinder1561"
  Angle = 360
  AttacherType = Attacher::AttachEngine3D
  Height = 30
  Placement = pos=(167.5,31,-28) rot=(0,0,1;0rad)
  Radius = 14.1
FEATURE [Part::Fillet] Fillet007021
  Base = -> Cylinder1085
  Edges = 1 edges r=7: [Edge1]
  Placement = pos=(0,0,1) rot=(0,0,1;0rad)
FEATURE [Part::Cut] Cut014226  label="Cut014422"
  Base = -> Fillet007021
  Placement = pos=(6,0,0) rot=(0,0,1;0rad)
  Refine = true
  Tool = -> Cylinder1084
FEATURE [Part::Box] Box691  label="Cube867"
  AttacherType = Attacher::AttachEngine3D
  Height = 15
  Length = 10
  Placement = pos=(167,41.5,-19) rot=(0,0,1;0rad)
  Width = 12
FEATURE [Part::Cylinder] Cylinder1086  label="Cylinder1562"
  Angle = 360
  AttacherType = Attacher::AttachEngine3D
  Height = 15
  Placement = pos=(170.5,58,-9) rot=(1,0,0;1.5708rad)
  Radius = 1.6
FEATURE [Part::Cylinder] Cylinder1087  label="Cylinder1563"
  Angle = 360
  AttacherType = Attacher::AttachEngine3D
  Height = 5
  Placement = pos=(170.5,47,-9) rot=(1,0,0;1.5708rad)
  Radius = 3.2
FEATURE [Part::MultiFuse] Fusion248002054  label="Fusion248002251"
  Placement = pos=(1,0,1) rot=(0,0,1;0rad)
  Refine = true
  Shapes = -> [Cylinder1086,Cylinder1087]
FEATURE [Part::Box] Box692  label="Cube868"
  AttacherType = Attacher::AttachEngine3D
  Height = 9.5
  Length = 1.5
  Placement = pos=(175.5,43.5,-19) rot=(0,0,1;0rad)
  Width = 13
FEATURE [Part::Box] Box693  label="Cube869"
  AttacherType = Attacher::AttachEngine3D
  Height = 9
  Length = 2
  Placement = pos=(177,45,-19) rot=(0,0,1;0rad)
  Width = 8
FEATURE [Part::Cylinder] Cylinder1088  label="Cylinder1564"
  Angle = 360
  AttacherType = Attacher::AttachEngine3D
  Height = 15
  Placement = pos=(165,49,-14.5) rot=(0,1,0;1.5708rad)
  Radius = 1
FEATURE [Part::Cylinder] Cylinder1089  label="Cylinder1565"
  Angle = 360
  AttacherType = Attacher::AttachEngine3D
  Height = 1
  Placement = pos=(178,49,-14.5) rot=(0,1,0;1.5708rad)
  Radius = 2.5
FEATURE [Part::Box] Box694  label="Cube870"
  AttacherType = Attacher::AttachEngine3D
  Height = 3
  Length = 10
  Placement = pos=(166,44.5,-19) rot=(0,0,1;0rad)
  Width = 12
FEATURE [Part::Box] Box695  label="Cube871"
  AttacherType = Attacher::AttachEngine3D
  Height = 4
  Length = 10
  Placement = pos=(166,53.5,-18) rot=(0,0,1;0rad)
  Width = 4
FEATURE [Part::Fillet] Fillet007022
  Base = -> Box695
  Edges = 1 edges r=3: [Edge9]
FEATURE [Part::Cut] Cut014227  label="Cut014423"
  Base = -> Box694
  Placement = pos=(1,0,0) rot=(0,0,1;0rad)
  Refine = true
  Tool = -> Fillet007022
FEATURE [Part::Cylinder] Cylinder1090  label="Cylinder1566"
  Angle = 360
  AttacherType = Attacher::AttachEngine3D
  Height = 23
  Placement = pos=(163,51,10) rot=(0,-1,0;1.36136rad)
  Radius = 2.6
FEATURE [Part::Chamfer] Chamfer146
  Base = -> Fusion248002053
  Edges = 4 edges r=2.49: [Edge3,Edge4,Edge5,Edge8]
  Placement = pos=(0,0,3) rot=(0,0,1;0rad)
FEATURE [Part::Cylinder] Cylinder1091  label="Cylinder1567"
  Angle = 360
  AttacherType = Attacher::AttachEngine3D
  Height = 18
  Placement = pos=(163,51,10) rot=(0,-1,0;1.36136rad)
  Radius = 2.6
FEATURE [Part::Cut] Cut014228  label="Cut014424"
  Base = -> Cylinder1090
  Refine = true
  Tool = -> Cylinder1091
FEATURE [Part::Cut] Cut014229  label="Cut014425"
  Base = -> Chamfer146
  Placement = pos=(0,0,-3.5) rot=(0,0,1;0rad)
  Refine = true
  Tool = -> Cut014228
FEATURE [Part::MultiFuse] Fusion248002056
  Refine = true
  Shapes = -> [Cylinder1089,Cylinder1088]
FEATURE [Part::MultiFuse] Fusion248002058
  Refine = true
  Shapes = -> [Cut014223,Cut014224]
FEATURE [Part::Cut] Cut014234  label="air-intake-lower-03"
  Base = -> Fusion248002058
  Refine = true
  Tool = -> Chamfer145
FEATURE [Part::MultiFuse] Fusion248002059
  Refine = true
  Shapes = -> [Cut014229,Box691,Cut014227,Cut014225]
FEATURE [Part::Cut] Cut014235  label="Cut014426"
  Base = -> Fusion248002059
  Refine = true
  Tool = -> Cut014226
FEATURE [Part::Cut] Cut014236  label="Cut014427"
  Base = -> Cut014235
  Refine = true
  Tool = -> Box692
FEATURE [Part::MultiFuse] Fusion248002060  label="Fusion248002252"
  Refine = true
  Shapes = -> [Cut014236,Box693]
FEATURE [Part::Cut] Cut014237  label="Cut014428"
  Base = -> Fusion248002060
  Refine = true
  Tool = -> Fusion248002054
FEATURE [Part::Cut] Cut014238  label="Cut014429"
  Base = -> Cut014237
  Refine = true
  Tool = -> Fusion248002056
FEATURE [Part::Chamfer] Chamfer147  label="air-box-holder-01"
  Base = -> Cut014238
  Edges = 1 edges r=1.499: [Edge70]
FEATURE [Part::Box] Box696  label="Cube872"
  AttacherType = Attacher::AttachEngine3D
  Height = 30
  Length = 29
  Width = 13
FEATURE [Part::Box] Box697  label="Cube873"
  AttacherType = Attacher::AttachEngine3D
  Height = 4
  Length = 7
  Placement = pos=(-7,3.5,1) rot=(0,0,1;0rad)
  Width = 6
FEATURE [Part::Box] Box698  label="Cube874"
  AttacherType = Attacher::AttachEngine3D
  Height = 3.3
  Length = 40
  Placement = pos=(-5.5,0,19.5) rot=(0,0,1;0rad)
  Width = 13
FEATURE [Part::Cylinder] Cylinder1092  label="Cylinder1568"
  Angle = 360
  AttacherType = Attacher::AttachEngine3D
  Height = 6
  Placement = pos=(6,6.5,30) rot=(0,0,1;0rad)
  Radius = 4
FEATURE [Part::Box] Box699  label="Cube875"
  AttacherType = Attacher::AttachEngine3D
  Height = 1.5
  Length = 28
  Placement = pos=(-8,3.5,34.5) rot=(0,0,1;0rad)
  Width = 6
FEATURE [Part::Fillet] Fillet007023
  Base = -> Box699
  Edges = 4 edges r=2: [Edge1,Edge3,Edge5,Edge7]
FEATURE [Part::Cylinder] Cylinder1093  label="Cylinder1569"
  Angle = 360
  AttacherType = Attacher::AttachEngine3D
  Height = 10
  Radius = 1
FEATURE [Part::Cylinder] Cylinder1094  label="Cylinder1570"
  Angle = 360
  AttacherType = Attacher::AttachEngine3D
  Height = 10
  Placement = pos=(35.3,0,0) rot=(0,0,1;0rad)
  Radius = 1
FEATURE [Part::MultiFuse] Fusion248002061  label="Fusion248002253"
  Refine = true
  Shapes = -> [Box696,Fillet007023,Box697,Box698,Cylinder1092]
FEATURE [Part::MultiFuse] Fusion248002062  label="Fusion248002254"
  Placement = pos=(-3.15,6.5,13) rot=(0,0,1;0rad)
  Refine = true
  Shapes = -> [Cylinder1093,Cylinder1094]
FEATURE [Part::Cylinder] Cylinder1095  label="Cylinder1571"
  Angle = 360
  AttacherType = Attacher::AttachEngine3D
  Height = 10
  Placement = pos=(0,6.5,29) rot=(0,0,1;0rad)
  Radius = 1
FEATURE [Part::Cylinder] Cylinder1096  label="Cylinder1572"
  Angle = 360
  AttacherType = Attacher::AttachEngine3D
  Height = 10
  Placement = pos=(24,6.5,29) rot=(0,0,1;0rad)
  Radius = 1
FEATURE [Part::Cylinder] Cylinder1097  label="Cylinder1573"
  Angle = 360
  AttacherType = Attacher::AttachEngine3D
  Height = 10
  Placement = pos=(0,6.5,29) rot=(0,0,1;0rad)
  Radius = 1
FEATURE [Part::Cylinder] Cylinder1098  label="Cylinder1574"
  Angle = 360
  AttacherType = Attacher::AttachEngine3D
  Height = 10
  Placement = pos=(19,6.5,29) rot=(0,0,1;0rad)
  Radius = 1
FEATURE [Part::Cylinder] Cylinder1099  label="Cylinder1575"
  Angle = 360
  AttacherType = Attacher::AttachEngine3D
  Height = 10
  Placement = pos=(0,6.5,29) rot=(0,0,1;0rad)
  Radius = 1
FEATURE [Part::Cylinder] Cylinder1100  label="Cylinder1576"
  Angle = 360
  AttacherType = Attacher::AttachEngine3D
  Height = 10
  Placement = pos=(14,6.5,29) rot=(0,0,1;0rad)
  Radius = 1
FEATURE [Part::MultiFuse] Fusion248002063  label="Fusion248002255"
  Placement = pos=(-6,0,2) rot=(0,0,1;0rad)
  Refine = true
  Shapes = -> [Cylinder1095,Cylinder1096]
FEATURE [Part::MultiFuse] Fusion248002064  label="Fusion248002256"
  Placement = pos=(-3.5,0,2) rot=(0,0,1;0rad)
  Refine = true
  Shapes = -> [Cylinder1097,Cylinder1098]
FEATURE [Part::MultiFuse] Fusion248002065  label="Fusion248002257"
  Placement = pos=(-1,0,2) rot=(0,0,1;0rad)
  Refine = true
  Shapes = -> [Cylinder1099,Cylinder1100]
FEATURE [Part::MultiFuse] Fusion248002066
  Refine = true
  Shapes = -> [Fusion248002062,Fusion248002064,Fusion248002063,Fusion248002065]
FEATURE [Part::Cut] Cut014239  label="hitec-hs85bb001"
  Base = -> Fusion248002061
  Placement = pos=(239,41.5,1.5) rot=(0.707107,-0.707107,0;3.14159rad)
  Refine = true
  Tool = -> Fusion248002066
FEATURE [Part::Box] Box700  label="Cube876"
  AttacherType = Attacher::AttachEngine3D
  Height = 30
  Length = 29
  Width = 13
FEATURE [Part::Box] Box701  label="Cube877"
  AttacherType = Attacher::AttachEngine3D
  Height = 4
  Length = 7
  Placement = pos=(-7,3.5,1) rot=(0,0,1;0rad)
  Width = 6
FEATURE [Part::Box] Box702  label="Cube878"
  AttacherType = Attacher::AttachEngine3D
  Height = 3.3
  Length = 40
  Placement = pos=(-5.5,0,19.5) rot=(0,0,1;0rad)
  Width = 13
FEATURE [Part::Cylinder] Cylinder1101  label="Cylinder1577"
  Angle = 360
  AttacherType = Attacher::AttachEngine3D
  Height = 6
  Placement = pos=(6,6.5,30) rot=(0,0,1;0rad)
  Radius = 4
FEATURE [Part::Box] Box703  label="Cube879"
  AttacherType = Attacher::AttachEngine3D
  Height = 1.5
  Length = 28
  Placement = pos=(-8,3.5,34.5) rot=(0,0,1;0rad)
  Width = 6
FEATURE [Part::Fillet] Fillet007024
  Base = -> Box703
  Edges = 4 edges r=2: [Edge1,Edge3,Edge5,Edge7]
FEATURE [Part::Cylinder] Cylinder1102  label="Cylinder1578"
  Angle = 360
  AttacherType = Attacher::AttachEngine3D
  Height = 10
  Radius = 1
FEATURE [Part::Cylinder] Cylinder1103  label="Cylinder1579"
  Angle = 360
  AttacherType = Attacher::AttachEngine3D
  Height = 10
  Placement = pos=(35.3,0,0) rot=(0,0,1;0rad)
  Radius = 1
FEATURE [Part::MultiFuse] Fusion248002067  label="Fusion248002258"
  Refine = true
  Shapes = -> [Box700,Fillet007024,Box701,Box702,Cylinder1101]
FEATURE [Part::MultiFuse] Fusion248002068  label="Fusion248002259"
  Placement = pos=(-3.15,6.5,13) rot=(0,0,1;0rad)
  Refine = true
  Shapes = -> [Cylinder1102,Cylinder1103]
FEATURE [Part::Cylinder] Cylinder1104  label="Cylinder1580"
  Angle = 360
  AttacherType = Attacher::AttachEngine3D
  Height = 10
  Placement = pos=(0,6.5,29) rot=(0,0,1;0rad)
  Radius = 1
FEATURE [Part::Cylinder] Cylinder1105  label="Cylinder1581"
  Angle = 360
  AttacherType = Attacher::AttachEngine3D
  Height = 10
  Placement = pos=(24,6.5,29) rot=(0,0,1;0rad)
  Radius = 1
FEATURE [Part::Cylinder] Cylinder1106  label="Cylinder1582"
  Angle = 360
  AttacherType = Attacher::AttachEngine3D
  Height = 10
  Placement = pos=(0,6.5,29) rot=(0,0,1;0rad)
  Radius = 1
FEATURE [Part::Cylinder] Cylinder1107  label="Cylinder1583"
  Angle = 360
  AttacherType = Attacher::AttachEngine3D
  Height = 10
  Placement = pos=(19,6.5,29) rot=(0,0,1;0rad)
  Radius = 1
FEATURE [Part::Cylinder] Cylinder1108  label="Cylinder1584"
  Angle = 360
  AttacherType = Attacher::AttachEngine3D
  Height = 10
  Placement = pos=(0,6.5,29) rot=(0,0,1;0rad)
  Radius = 1
FEATURE [Part::Cylinder] Cylinder1109  label="Cylinder1585"
  Angle = 360
  AttacherType = Attacher::AttachEngine3D
  Height = 10
  Placement = pos=(14,6.5,29) rot=(0,0,1;0rad)
  Radius = 1
FEATURE [Part::MultiFuse] Fusion248002069  label="Fusion248002260"
  Placement = pos=(-6,0,2) rot=(0,0,1;0rad)
  Refine = true
  Shapes = -> [Cylinder1104,Cylinder1105]
FEATURE [Part::MultiFuse] Fusion248002070  label="Fusion248002261"
  Placement = pos=(-3.5,0,2) rot=(0,0,1;0rad)
  Refine = true
  Shapes = -> [Cylinder1106,Cylinder1107]
FEATURE [Part::MultiFuse] Fusion248002071  label="Fusion248002262"
  Placement = pos=(-1,0,2) rot=(0,0,1;0rad)
  Refine = true
  Shapes = -> [Cylinder1108,Cylinder1109]
FEATURE [Part::MultiFuse] Fusion248002072  label="Fusion248002083"
  Refine = true
  Shapes = -> [Fusion248002068,Fusion248002070,Fusion248002069,Fusion248002071]
FEATURE [Part::Cut] Cut014240  label="hitec-hs85bb002"
  Base = -> Fusion248002067
  Placement = pos=(219,41.5,1.5) rot=(0.707107,-0.707107,0;3.14159rad)
  Refine = true
  Tool = -> Fusion248002072
FEATURE [Part::Box] Box704  label="Cube880"
  AttacherType = Attacher::AttachEngine3D
  Height = 24
  Length = 45
  Placement = pos=(200,6.5,-22) rot=(0,0,1;0rad)
  Width = 47
FEATURE [Part::Box] Box705  label="Cube881"
  AttacherType = Attacher::AttachEngine3D
  Height = 20
  Length = 42
  Placement = pos=(201.5,6.5,-18) rot=(0,0,1;0rad)
  Width = 43
FEATURE [Part::Box] Box706  label="Cube882"
  AttacherType = Attacher::AttachEngine3D
  Height = 5
  Length = 45
  Placement = pos=(200,6.5,-20) rot=(0,0,1;0rad)
  Width = 1.5
FEATURE [Part::Cylinder] Cylinder1110  label="Cylinder1586"
  Angle = 360
  AttacherType = Attacher::AttachEngine3D
  Height = 65
  Placement = pos=(190,51.5,0) rot=(0,1,0;1.5708rad)
  Radius = 0.55
FEATURE [Part::Cylinder] Cylinder1111  label="Cylinder1587"
  Angle = 360
  AttacherType = Attacher::AttachEngine3D
  Height = 10
  Placement = pos=(261,1,10) rot=(1,0,0;1.5708rad)
  Radius = 1.6
FEATURE [Part::Cylinder] Cylinder1112  label="Cylinder1588"
  Angle = 360
  AttacherType = Attacher::AttachEngine3D
  Height = 10
  Placement = pos=(294,1,10) rot=(1,0,0;1.5708rad)
  Radius = 1.6
FEATURE [Part::MultiFuse] Fusion248002073  label="Fusion248002263"
  Placement = pos=(-55,55,-18) rot=(0,0,1;0rad)
  Refine = true
  Shapes = -> [Cylinder1111,Cylinder1112]
FEATURE [Part::Cut] Cut014241  label="Cut014430"
  Base = -> Box704
  Refine = true
  Tool = -> Box705
FEATURE [Part::MultiFuse] Fusion248002074  label="Fusion248002243"
  Placement = pos=(0,-1,0) rot=(0,0,1;0rad)
  Refine = true
  Shapes = -> [Cut014241,Box706]
FEATURE [Part::MultiFuse] Fusion248002075  label="Fusion248002264"
  Placement = pos=(0,-1,0) rot=(0,0,1;0rad)
  Refine = true
  Shapes = -> [Fusion248002073,Cylinder1110]
FEATURE [Part::Cylinder] Cylinder1113  label="Cylinder1589"
  Angle = 360
  AttacherType = Attacher::AttachEngine3D
  Height = 15
  Placement = pos=(198.5,48,-8) rot=(1,0,0;1.5708rad)
  Radius = 2
FEATURE [Part::Cylinder] Cylinder1114  label="Cylinder1590"
  Angle = 360
  AttacherType = Attacher::AttachEngine3D
  Height = 15
  Placement = pos=(198.5,30,-8) rot=(1,0,0;1.5708rad)
  Radius = 2
FEATURE [Part::MultiFuse] Fusion248002076  label="Fusion248002167"
  Refine = true
  Shapes = -> [Cylinder1113,Cylinder1114]
FEATURE [Part::Fillet] Fillet007027
  Base = -> Fusion248002076
  Edges = 4 edges r=2: [Edge1,Edge3,Edge4,Edge6]
FEATURE [Part::Cylinder] Cylinder1115  label="Cylinder1591"
  Angle = 360
  AttacherType = Attacher::AttachEngine3D
  Height = 15
  Placement = pos=(198.5,48,-8) rot=(1,0,0;1.5708rad)
  Radius = 2
FEATURE [Part::Cylinder] Cylinder1116  label="Cylinder1592"
  Angle = 360
  AttacherType = Attacher::AttachEngine3D
  Height = 15
  Placement = pos=(198.5,30,-8) rot=(1,0,0;1.5708rad)
  Radius = 2
FEATURE [Part::MultiFuse] Fusion248002077
  Refine = true
  Shapes = -> [Cylinder1115,Cylinder1116]
FEATURE [Part::Fillet] Fillet007028
  Base = -> Fusion248002077
  Edges = 4 edges r=2: [Edge1,Edge3,Edge4,Edge6]
  Placement = pos=(48,0,0) rot=(0,0,1;0rad)
FEATURE [Part::MultiFuse] Fusion248002078  label="Fusion248002265"
  Placement = pos=(0,-3,-2) rot=(0,0,1;0rad)
  Refine = true
  Shapes = -> [Fillet007027,Fillet007028]
FEATURE [Part::Cylinder] Cylinder1119  label="Cylinder1593"
  Angle = 360
  AttacherType = Attacher::AttachEngine3D
  Height = 15
  Placement = pos=(212.5,44.65,-24) rot=(0,0,1;0rad)
  Radius = 1
FEATURE [Part::Cylinder] Cylinder1120  label="Cylinder1594"
  Angle = 360
  AttacherType = Attacher::AttachEngine3D
  Height = 15
  Placement = pos=(212.5,9.35,-24) rot=(0,0,1;0rad)
  Radius = 1
FEATURE [Part::Cylinder] Cylinder1121  label="Cylinder1595"
  Angle = 360
  AttacherType = Attacher::AttachEngine3D
  Height = 15
  Placement = pos=(232.5,44.65,-24) rot=(0,0,1;0rad)
  Radius = 1
FEATURE [Part::Cylinder] Cylinder1122  label="Cylinder1596"
  Angle = 360
  AttacherType = Attacher::AttachEngine3D
  Height = 15
  Placement = pos=(232.5,9.35,-24) rot=(0,0,1;0rad)
  Radius = 1
FEATURE [Part::Box] Box713  label="Cube889"
  AttacherType = Attacher::AttachEngine3D
  Height = 6.5
  Length = 43
  Placement = pos=(201,42,-18) rot=(0,0,1;0rad)
  Width = 7
FEATURE [Part::Box] Box714  label="Cube890"
  AttacherType = Attacher::AttachEngine3D
  Height = 21
  Length = 45
  Placement = pos=(200,52.5,-22) rot=(0,0,1;0rad)
  Width = 1
FEATURE [Part::MultiFuse] Fusion248002087
  Refine = true
  Shapes = -> [Fusion248002074,Box714]
FEATURE [Part::Cut] Cut014249  label="Cut014431"
  Base = -> Fusion248002087
  Refine = true
  Tool = -> Fusion248002075
FEATURE [Part::Cut] Cut014250  label="Cut014432"
  Base = -> Cut014249
  Refine = true
  Tool = -> Fusion248002078
FEATURE [Part::Cylinder] Cylinder1129  label="Cylinder1597"
  Angle = 360
  AttacherType = Attacher::AttachEngine3D
  Height = 2.5
  Placement = pos=(261,1,10) rot=(1,0,0;1.5708rad)
  Radius = 3.1
FEATURE [Part::Cylinder] Cylinder1130  label="Cylinder1598"
  Angle = 360
  AttacherType = Attacher::AttachEngine3D
  Height = 2.5
  Placement = pos=(294,1,10) rot=(1,0,0;1.5708rad)
  Radius = 3.1
FEATURE [Part::MultiFuse] Fusion248002088  label="Fusion248002266"
  Placement = pos=(-55,50,-18) rot=(0,0,1;0rad)
  Refine = true
  Shapes = -> [Cylinder1129,Cylinder1130]
FEATURE [Part::Cut] Cut014251  label="Cut014433"
  Base = -> Cut014250
  Refine = true
  Tool = -> Fusion248002088
FEATURE [Part::Box] Box715  label="Cube891"
  AttacherType = Attacher::AttachEngine3D
  Height = 7
  Length = 27
  Placement = pos=(209,48.5,-6) rot=(0,0,1;0rad)
  Width = 2
FEATURE [Part::Fillet] Fillet007037
  Base = -> Box715
  Edges = 2 edges r=1.99: [Edge11,Edge12]
FEATURE [Part::Cut] Cut014252  label="Cut014434"
  Base = -> Cut014251
  Refine = true
  Tool = -> Fillet007037
FEATURE [Part::Box] Box716  label="Cube892"
  AttacherType = Attacher::AttachEngine3D
  Height = 6.5
  Length = 43
  Placement = pos=(201,7,-18) rot=(0,0,1;0rad)
  Width = 5
FEATURE [Part::Box] Box717  label="Cube893"
  AttacherType = Attacher::AttachEngine3D
  Height = 6
  Length = 14
  Placement = pos=(205.5,7,-24) rot=(0,0,1;0rad)
  Width = 41
FEATURE [Part::Box] Box718  label="Cube894"
  AttacherType = Attacher::AttachEngine3D
  Height = 6
  Length = 14
  Placement = pos=(225.5,7,-24) rot=(0,0,1;0rad)
  Width = 41
FEATURE [Part::MultiFuse] Fusion248002089
  Placement = pos=(0,-0.5,0) rot=(0,0,1;0rad)
  Refine = true
  Shapes = -> [Box718,Box717]
FEATURE [Part::Cut] Cut014253  label="Cut014435"
  Base = -> Cut014252
  Refine = true
  Tool = -> Fusion248002089
FEATURE [Part::MultiFuse] Fusion248002090
  Refine = true
  Shapes = -> [Box716,Box713,Cut014253]
FEATURE [Part::MultiFuse] Fusion248002091
  Refine = true
  Shapes = -> [Cylinder1119,Cylinder1120,Cylinder1121,Cylinder1122]
FEATURE [Part::Cut] Cut014254  label="Cut014436"
  Base = -> Fusion248002090
  Refine = true
  Tool = -> Fusion248002091
FEATURE [Part::Box] Box719  label="Cube895"
  AttacherType = Attacher::AttachEngine3D
  Height = 22.5
  Length = 48
  Placement = pos=(198.5,4,-19) rot=(0,0,1;0rad)
  Width = 47.5
FEATURE [Part::Cylinder] Cylinder1131  label="Cylinder1599"
  Angle = 360
  AttacherType = Attacher::AttachEngine3D
  Height = 65
  Placement = pos=(190,50.5,0) rot=(0,1,0;1.5708rad)
  Radius = 0.55
FEATURE [Part::Box] Box720  label="Cube896"
  AttacherType = Attacher::AttachEngine3D
  Height = 22.5
  Length = 46
  Placement = pos=(199.5,5,-20) rot=(0,0,1;0rad)
  Width = 48.5
FEATURE [Part::Fillet] Fillet007038
  Base = -> Box720
  Edges = 1 edges r=8: [Edge10]
FEATURE [Part::Cut] Cut014255  label="Cut014437"
  Base = -> Box719
  Refine = true
  Tool = -> Fillet007038
FEATURE [Part::Fillet] Fillet007039
  Base = -> Cut014255
  Edges = 1 edges r=9: [Edge7]
FEATURE [Part::Box] Box721  label="Cube897"
  AttacherType = Attacher::AttachEngine3D
  Height = 22.5
  Length = 48
  Placement = pos=(198.5,10,-22) rot=(0,0,1;0rad)
  Width = 45.5
FEATURE [Part::Fillet] Fillet007040
  Base = -> Box721
  Edges = 1 edges r=8: [Edge10]
FEATURE [Part::Cut] Cut014256  label="Cut014438"
  Base = -> Fillet007039
  Refine = true
  Tool = -> Fillet007040
FEATURE [Part::Chamfer] Chamfer150
  Base = -> Cut014256
  Edges = 2 edges r=2: [Edge24,Edge29]
FEATURE [Part::Cylinder] Cylinder1132  label="Cylinder1600"
  Angle = 360
  AttacherType = Attacher::AttachEngine3D
  Height = 1
  Placement = pos=(245.5,50.5,0) rot=(0,1,0;1.5708rad)
  Radius = 2
FEATURE [Part::Cylinder] Cylinder1133  label="Cylinder1601"
  Angle = 360
  AttacherType = Attacher::AttachEngine3D
  Height = 1
  Placement = pos=(198.5,50.5,0) rot=(0,1,0;1.5708rad)
  Radius = 2
FEATURE [Part::MultiFuse] Fusion248002092
  Refine = true
  Shapes = -> [Cylinder1132,Cylinder1133,Chamfer150]
FEATURE [Part::Chamfer] Chamfer151
  Base = -> Fusion248002092
  Edges = 2 edges r=0.75: [Edge22,Edge25]
FEATURE [Part::Cut] Cut014257  label="battery-box-cover-01"
  Base = -> Chamfer151
  Refine = true
  Tool = -> Cylinder1131
FEATURE [Part::Cylinder] Cylinder1134  label="Cylinder1602"
  Angle = 360
  AttacherType = Attacher::AttachEngine3D
  Height = 15
  Placement = pos=(203.5,45.5,-30) rot=(0,0,1;0rad)
  Radius = 1.2
FEATURE [Part::Cylinder] Cylinder1135  label="Cylinder1603"
  Angle = 360
  AttacherType = Attacher::AttachEngine3D
  Height = 15
  Placement = pos=(203.5,16.5,-30) rot=(0,0,1;0rad)
  Radius = 1.2
FEATURE [Part::Cylinder] Cylinder1136  label="Cylinder1604"
  Angle = 360
  AttacherType = Attacher::AttachEngine3D
  Height = 15
  Placement = pos=(241.5,45.5,-30) rot=(0,0,1;0rad)
  Radius = 1.2
FEATURE [Part::Cylinder] Cylinder1137  label="Cylinder1605"
  Angle = 360
  AttacherType = Attacher::AttachEngine3D
  Height = 15
  Placement = pos=(241.5,16.5,-30) rot=(0,0,1;0rad)
  Radius = 1.2
FEATURE [Part::MultiFuse] Fusion248002093
  Placement = pos=(0,-1,6) rot=(0,0,1;0rad)
  Refine = true
  Shapes = -> [Cylinder1134,Cylinder1136,Cylinder1137,Cylinder1135]
FEATURE [Part::Box] Box722  label="Cube898"
  AttacherType = Attacher::AttachEngine3D
  Height = 6.5
  Length = 14
  Placement = pos=(205.5,7,-22) rot=(0,0,1;0rad)
  Width = 42
FEATURE [Part::Box] Box728
  AttacherType = Attacher::AttachEngine3D
  Height = 33
  Length = 15
  Placement = pos=(529,56,-59) rot=(0,-1,0;0.959931rad)
  Width = 8
FEATURE [Part::Cylinder] Cylinder1146  label="rear-bumper001"
  Angle = 360
  AttacherType = Attacher::AttachEngine3D
  Height = 180
  Placement = pos=(530,175,-50) rot=(1,0,0;1.5708rad)
  Radius = 5
FEATURE [Part::Box] Box729
  AttacherType = Attacher::AttachEngine3D
  Height = 25
  Length = 25
  Placement = pos=(493.5,55,-43) rot=(0,0,1;0rad)
  Width = 10
FEATURE [Part::Box] Box730
  AttacherType = Attacher::AttachEngine3D
  Height = 8
  Length = 10
  Placement = pos=(512.5,56,-35) rot=(0,0,1;0rad)
  Width = 8
FEATURE [Part::Chamfer] Chamfer153
  Base = -> Box729
  Edges = 1 edges: [Edge6 r1=15 r2=5]
FEATURE [Part::Chamfer] Chamfer154
  Base = -> Chamfer153
  Edges = 1 edges: [Edge11 r1=10 r2=15]
FEATURE [Part::Cut] Cut014259  label="Cut014439"
  Base = -> Chamfer154
  Refine = true
  Tool = -> Box730
FEATURE [Part::Chamfer] Chamfer155
  Base = -> Box728
  Edges = 1 edges r=5: [Edge8]
FEATURE [Part::Cut] Cut014260  label="Cut014440"
  Base = -> Chamfer155
  Refine = true
  Tool = -> Cylinder1146
FEATURE [Part::Fillet] Fillet007042
  Base = -> Cut014260
  Edges = 2 edges r=0.75: [Edge10,Edge17]
FEATURE [Part::Fillet] Fillet007043
  Base = -> Fillet007042
  Edges = 1 edges r=3: [Edge11]
FEATURE [Part::Fillet] Fillet007044
  Base = -> Cut014259
  Edges = 5 edges r=3: [Edge8,Edge9,Edge10,Edge12,Edge16]
FEATURE [Part::Box] Box731
  AttacherType = Attacher::AttachEngine3D
  Height = 25
  Length = 2
  Placement = pos=(529,56,-42) rot=(0,-1,0;0.959931rad)
  Width = 9
FEATURE [Part::Cut] Cut014261  label="Cut014441"
  Base = -> Fillet007043
  Refine = true
  Tool = -> Box731
FEATURE [Part::Fillet] Fillet007045
  Base = -> Cut014261
  Edges = 2 edges r=0.5: [Edge23,Edge26]
FEATURE [Part::MultiFuse] Fusion248002095  label="Fusion248002267"
  Refine = true
  Shapes = -> [Fillet007044,Fillet007045]
FEATURE [Part::Cylinder] Cylinder1147  label="rear-bumper002"
  Angle = 360
  AttacherType = Attacher::AttachEngine3D
  Height = 1
  Placement = pos=(508,56,-36) rot=(1,0,0;1.5708rad)
  Radius = 2
FEATURE [Part::Cylinder] Cylinder1148  label="rear-bumper003"
  Angle = 360
  AttacherType = Attacher::AttachEngine3D
  Height = 30
  Placement = pos=(498,60,-43) rot=(0,0,1;0rad)
  Radius = 1.6
FEATURE [Part::Cylinder] Cylinder1149  label="rear-bumper004"
  Angle = 360
  AttacherType = Attacher::AttachEngine3D
  Height = 16
  Placement = pos=(498,60,-43) rot=(0,0,1;0rad)
  Radius = 3.2
FEATURE [Part::Cylinder] Cylinder1150  label="rear-bumper005"
  Angle = 360
  AttacherType = Attacher::AttachEngine3D
  Height = 1
  Placement = pos=(508,65,-36) rot=(1,0,0;1.5708rad)
  Radius = 2
FEATURE [Part::MultiFuse] Fusion248002097  label="Fusion248002268"
  Refine = true
  Shapes = -> [Cylinder1150,Cylinder1147]
FEATURE [Part::Cut] Cut014262  label="Cut014442"
  Base = -> Fusion248002095
  Refine = true
  Tool = -> Fusion248002097
FEATURE [Part::Box] Box732
  AttacherType = Attacher::AttachEngine3D
  Height = 33
  Length = 15
  Placement = pos=(529,56,-59) rot=(0,-1,0;0.959931rad)
  Width = 8
FEATURE [Part::Cylinder] Cylinder1151  label="rear-bumper006"
  Angle = 360
  AttacherType = Attacher::AttachEngine3D
  Height = 180
  Placement = pos=(530,175,-50) rot=(1,0,0;1.5708rad)
  Radius = 5
FEATURE [Part::Box] Box733
  AttacherType = Attacher::AttachEngine3D
  Height = 25
  Length = 25
  Placement = pos=(493.5,55,-43) rot=(0,0,1;0rad)
  Width = 10
FEATURE [Part::Box] Box734
  AttacherType = Attacher::AttachEngine3D
  Height = 8
  Length = 10
  Placement = pos=(512.5,56,-35) rot=(0,0,1;0rad)
  Width = 8
FEATURE [Part::Chamfer] Chamfer156
  Base = -> Box733
  Edges = 1 edges: [Edge6 r1=15 r2=5]
FEATURE [Part::Chamfer] Chamfer157
  Base = -> Chamfer156
  Edges = 1 edges: [Edge11 r1=10 r2=15]
FEATURE [Part::Cut] Cut014264  label="Cut014443"
  Base = -> Chamfer157
  Refine = true
  Tool = -> Box734
FEATURE [Part::Chamfer] Chamfer158
  Base = -> Box732
  Edges = 1 edges r=5: [Edge8]
FEATURE [Part::Cut] Cut014265  label="Cut014444"
  Base = -> Chamfer158
  Refine = true
  Tool = -> Cylinder1151
FEATURE [Part::Fillet] Fillet007046
  Base = -> Cut014265
  Edges = 2 edges r=0.75: [Edge10,Edge17]
FEATURE [Part::Fillet] Fillet007047
  Base = -> Fillet007046
  Edges = 1 edges r=3: [Edge11]
FEATURE [Part::Fillet] Fillet007048
  Base = -> Cut014264
  Edges = 5 edges r=3: [Edge8,Edge9,Edge10,Edge12,Edge16]
FEATURE [Part::Box] Box735
  AttacherType = Attacher::AttachEngine3D
  Height = 25
  Length = 2
  Placement = pos=(529,56,-42) rot=(0,-1,0;0.959931rad)
  Width = 9
FEATURE [Part::Cut] Cut014266  label="Cut014445"
  Base = -> Fillet007047
  Refine = true
  Tool = -> Box735
FEATURE [Part::Fillet] Fillet007049
  Base = -> Cut014266
  Edges = 2 edges r=0.5: [Edge23,Edge26]
FEATURE [Part::MultiFuse] Fusion248002098  label="Fusion248002269"
  Refine = true
  Shapes = -> [Fillet007048,Fillet007049]
FEATURE [Part::Cylinder] Cylinder1152  label="rear-bumper007"
  Angle = 360
  AttacherType = Attacher::AttachEngine3D
  Height = 1
  Placement = pos=(508,56,-36) rot=(1,0,0;1.5708rad)
  Radius = 2
FEATURE [Part::Cylinder] Cylinder1155  label="rear-bumper010"
  Angle = 360
  AttacherType = Attacher::AttachEngine3D
  Height = 1
  Placement = pos=(508,65,-36) rot=(1,0,0;1.5708rad)
  Radius = 2
FEATURE [Part::MultiFuse] Fusion248002100  label="Fusion248002270"
  Refine = true
  Shapes = -> [Cylinder1155,Cylinder1152]
FEATURE [Part::Cut] Cut014267  label="Cut014446"
  Base = -> Fusion248002098
  Refine = true
  Tool = -> Fusion248002100
FEATURE [Part::Cylinder] Cylinder1156  label="Cylinder1115"
  Angle = 360
  AttacherType = Attacher::AttachEngine3D
  Height = 10
  Placement = pos=(3,60,10) rot=(1,0,0;1.5708rad)
  Radius = 1.2
FEATURE [Part::Cylinder] Cylinder1157  label="Cylinder1116"
  Angle = 360
  AttacherType = Attacher::AttachEngine3D
  Height = 10
  Placement = pos=(3,10,10) rot=(1,0,0;1.5708rad)
  Radius = 1.2
FEATURE [Part::Box] Box736  label="Cube751"
  AttacherType = Attacher::AttachEngine3D
  Height = 17
  Length = 16
  Placement = pos=(-2,0,1.5) rot=(0,0,1;0rad)
  Width = 60
FEATURE [Part::Box] Box737  label="Cube752"
  AttacherType = Attacher::AttachEngine3D
  Height = 25.5
  Length = 10
  Placement = pos=(-12,0,-5) rot=(0,0,1;0rad)
  Width = 63
FEATURE [Part::Cylinder] Cylinder1158  label="Cylinder1117"
  Angle = 360
  AttacherType = Attacher::AttachEngine3D
  Height = 11
  Placement = pos=(-2,66.5,4) rot=(0,1,0;1.5708rad)
  Radius = 1.25
FEATURE [Part::Cylinder] Cylinder955  label="Cylinder1118"
  Angle = 360
  AttacherType = Attacher::AttachEngine3D
  Height = 11
  Placement = pos=(-2,13.5,4) rot=(0,1,0;1.5708rad)
  Radius = 1.25
FEATURE [Part::Cylinder] Cylinder956  label="Cylinder1119"
  Angle = 360
  AttacherType = Attacher::AttachEngine3D
  Height = 15
  Placement = pos=(-2,57,20) rot=(0,1,0;1.5708rad)
  Radius = 1.25
FEATURE [Part::Cylinder] Cylinder957  label="Cylinder1120"
  Angle = 360
  AttacherType = Attacher::AttachEngine3D
  Height = 15
  Placement = pos=(-2,23,20) rot=(0,1,0;1.5708rad)
  Radius = 1.25
FEATURE [Part::MultiFuse] Fusion248002101  label="Fusion248002271"
  Placement = pos=(-10,-10,1) rot=(0,0,1;0rad)
  Refine = true
  Shapes = -> [Cylinder1158,Cylinder957,Cylinder955,Cylinder956]
FEATURE [Part::Fillet] Fillet358
  Base = -> Box737
  Edges = 4 edges r=3: [Edge9,Edge10,Edge11,Edge12]
  Placement = pos=(25.5,53.5,-16.5) rot=(0,0,1;0rad)
FEATURE [Part::Fillet] Fillet359
  Base = -> Box736
  Edges = 4 edges r=3: [Edge9,Edge10,Edge11,Edge12]
  Placement = pos=(25.5,55,-21) rot=(0,0,1;0rad)
FEATURE [Part::MultiFuse] Fusion600
  Placement = pos=(0,0,2) rot=(0,0,1;0rad)
  Refine = true
  Shapes = -> [Cylinder1156,Cylinder1157]
FEATURE [Part::MultiFuse] Fusion248002102  label="Fusion248002272"
  Placement = pos=(25.5,55,-23) rot=(0,0,1;0rad)
  Refine = true
  Shapes = -> [Fusion248002101,Fusion600]
FEATURE [Part::Box] Box738  label="Cube753"
  AttacherType = Attacher::AttachEngine3D
  Height = 26
  Length = 41
  Placement = pos=(19.5,64.5,-21.5) rot=(0,0,1;0rad)
  Width = 41
FEATURE [Part::Cylinder] Cylinder1159  label="Cylinder1121"
  Angle = 360
  AttacherType = Attacher::AttachEngine3D
  Height = 11
  Placement = pos=(37,64.5,-11) rot=(1,0,0;1.5708rad)
  Radius = 6
FEATURE [Part::Cylinder] Cylinder1160  label="Cylinder1122"
  Angle = 360
  AttacherType = Attacher::AttachEngine3D
  Height = 10
  Placement = pos=(13.5,83,-11) rot=(0,1,0;1.5708rad)
  Radius = 1.6
FEATURE [Part::Cylinder] Cylinder1161  label="Cylinder1123"
  Angle = 360
  AttacherType = Attacher::AttachEngine3D
  Height = 10
  Placement = pos=(13.5,91,-11) rot=(0,1,0;1.5708rad)
  Radius = 1.6
FEATURE [Part::Cylinder] Cylinder1162  label="Cylinder1124"
  Angle = 360
  AttacherType = Attacher::AttachEngine3D
  Height = 2.5
  Placement = pos=(13.5,91,-11) rot=(0,1,0;1.5708rad)
  Radius = 3.1
FEATURE [Part::Cylinder] Cylinder1163  label="Cylinder1125"
  Angle = 360
  AttacherType = Attacher::AttachEngine3D
  Height = 2.5
  Placement = pos=(13.5,83,-11) rot=(0,1,0;1.5708rad)
  Radius = 3.1
FEATURE [Part::Cylinder] Cylinder1164  label="Cylinder1126"
  Angle = 360
  AttacherType = Attacher::AttachEngine3D
  Height = 5
  Placement = pos=(37,64.5,-11) rot=(1,0,0;1.5708rad)
  Radius = 7
FEATURE [Part::MultiFuse] Fusion248002103  label="Fusion248002273"
  Refine = true
  Shapes = -> [Cylinder1162,Cylinder1160,Cylinder1161,Cylinder1163]
FEATURE [Part::Box] Box739  label="Cube754"
  AttacherType = Attacher::AttachEngine3D
  Height = 17
  Length = 10
  Placement = pos=(37,55,-19.5) rot=(0,0,1;0rad)
  Width = 10
FEATURE [Part::MultiFuse] Fusion248002104  label="Fusion248002274"
  Refine = true
  Shapes = -> [Box739,Box738,Cylinder1159,Cylinder1164]
FEATURE [Part::MultiFuse] Fusion248002105  label="Fusion248002275"
  Refine = true
  Shapes = -> [Fillet359,Fillet358]
FEATURE [Part::Cut] Cut698  label="Cut014447"
  Base = -> Fusion248002105
  Refine = true
  Tool = -> Fusion248002102
FEATURE [Part::Cut] Cut699  label="Cut014448"
  Base = -> Cut698
  Refine = true
  Tool = -> Fusion248002104
FEATURE [Part::Cut] Cut700  label="cross-member-front"
  Base = -> Cut699
  Placement = pos=(0,0,3) rot=(0,0,1;0rad)
  Refine = true
  Tool = -> Fusion248002103
FEATURE [Part::Box] Box740  label="Cube902"
  AttacherType = Attacher::AttachEngine3D
  Height = 20
  Length = 25
  Placement = pos=(128,45.5,-18) rot=(0,0,1;0rad)
  Width = 8
FEATURE [Part::Cylinder] Cylinder1165  label="Cylinder1606"
  Angle = 360
  AttacherType = Attacher::AttachEngine3D
  Height = 24.5
  Placement = pos=(144,53.5,2) rot=(1,0,0;1.5708rad)
  Radius = 3
FEATURE [Part::Cylinder] Cylinder1166  label="Cylinder1607"
  Angle = 360
  AttacherType = Attacher::AttachEngine3D
  Height = 18
  Placement = pos=(131,51,-5) rot=(1,0,0;0.785398rad)
  Radius = 3
FEATURE [Part::Feature] Face059
  shape: bbox 7.785 x 2e-07 x 7.712 mm, 1 faces, 0 solids (baked)
FEATURE [Part::Feature] Face060
  shape: bbox 7.318 x 4.987 x 4.987 mm, 1 faces, 0 solids (baked)
FEATURE [Part::Loft] Loft023
  Closed = false
  MaxDegree = 5
  Ruled = true
  Sections = -> [Face059,Face060]
  Solid = true
FEATURE [Part::Cylinder] Cylinder1167  label="Cylinder1608"
  Angle = 360
  AttacherType = Attacher::AttachEngine3D
  Height = 3
  Placement = pos=(131,31,12) rot=(1,0,0;1.5708rad)
  Radius = 3
FEATURE [Part::MultiFuse] Fusion248002106  label="Fusion248002276"
  Placement = pos=(0,1,8) rot=(0,0,1;0rad)
  Refine = true
  Shapes = -> [Loft023,Cylinder1167]
FEATURE [Part::Cylinder] Cylinder1168  label="Cylinder1609"
  Angle = 360
  AttacherType = Attacher::AttachEngine3D
  Height = 5
  Placement = pos=(131,33,12) rot=(1,0,0;1.5708rad)
  Radius = 1.6
FEATURE [Part::Cylinder] Cylinder1169  label="Cylinder1610"
  Angle = 360
  AttacherType = Attacher::AttachEngine3D
  Height = 25
  Placement = pos=(144,53,-6) rot=(1,0,0;1.5708rad)
  Radius = 1.6
FEATURE [Part::MultiFuse] Fusion248002107  label="Fusion248002277"
  Placement = pos=(0,1,8) rot=(0,0,1;0rad)
  Refine = true
  Shapes = -> [Cylinder1168,Cylinder1169]
FEATURE [Part::Cylinder] Cylinder1170  label="Cylinder1611"
  Angle = 360
  AttacherType = Attacher::AttachEngine3D
  Height = 15
  Placement = pos=(132,61.5,-16) rot=(1,0,0;1.5708rad)
  Radius = 1.6
FEATURE [Part::Cylinder] Cylinder1171  label="Cylinder1612"
  Angle = 360
  AttacherType = Attacher::AttachEngine3D
  Height = 2.5
  Placement = pos=(132,49,-16) rot=(1,0,0;1.5708rad)
  Radius = 3
FEATURE [Part::MultiFuse] Fusion248002108  label="Fusion248002278"
  Placement = pos=(4,-1.5,7) rot=(0,0,1;0rad)
  Refine = true
  Shapes = -> [Cylinder1170,Cylinder1171]
FEATURE [Part::Box] Box741  label="Cube903"
  AttacherType = Attacher::AttachEngine3D
  Height = 9.5
  Length = 10
  Placement = pos=(143,45.5,-18) rot=(0,0,1;0rad)
  Width = 5
FEATURE [Part::Fillet] Fillet007050
  Base = -> Box741
  Edges = 1 edges r=4: [Edge2]
FEATURE [Part::Cylinder] Cylinder1172  label="Cylinder1613"
  Angle = 360
  AttacherType = Attacher::AttachEngine3D
  Height = 3.5
  Placement = pos=(148.5,53.5,-13.5) rot=(1,0,0;1.5708rad)
  Radius = 3
FEATURE [Part::Cylinder] Cylinder1173  label="Cylinder1614"
  Angle = 360
  AttacherType = Attacher::AttachEngine3D
  Height = 1.75
  Placement = pos=(498.5,51.75,-13.5) rot=(1,0,0;1.5708rad)
  Radius = 2.1
FEATURE [Part::Cylinder] Cylinder1174  label="Cylinder1615"
  Angle = 360
  AttacherType = Attacher::AttachEngine3D
  Height = 3.5
  Placement = pos=(498.5,53.5,-13.5) rot=(1,0,0;1.5708rad)
  Radius = 1.5
FEATURE [Part::MultiFuse] Fusion248002109  label="Fusion248002279"
  Placement = pos=(-350,0,0) rot=(0,0,1;0rad)
  Refine = true
  Shapes = -> [Cylinder1173,Cylinder1174]
FEATURE [Part::Cut] Cut014269  label="Cut014449"
  Base = -> Box740
  Refine = true
  Tool = -> Fillet007050
FEATURE [Part::MultiFuse] Fusion248002110  label="Fusion248002280"
  Refine = true
  Shapes = -> [Cut014269,Cylinder1172]
FEATURE [Part::Cut] Cut014270  label="Cut014450"
  Base = -> Fusion248002110
  Placement = pos=(0,0,3) rot=(0,0,1;0rad)
  Refine = true
  Tool = -> Fusion248002109
FEATURE [Part::Cylinder] Cylinder1175  label="Cylinder1616"
  Angle = 360
  AttacherType = Attacher::AttachEngine3D
  Height = 23
  Placement = pos=(131,52,-6) rot=(1,0,0;0.785398rad)
  Radius = 3
FEATURE [Part::Cylinder] Cylinder1176  label="Cylinder1617"
  Angle = 360
  AttacherType = Attacher::AttachEngine3D
  Height = 18
  Placement = pos=(131,52,-6) rot=(1,0,0;0.785398rad)
  Radius = 3
FEATURE [Part::Cut] Cut014271  label="Cut014451"
  Base = -> Cylinder1175
  Refine = true
  Tool = -> Cylinder1176
FEATURE [Part::MultiFuse] Fusion248002111  label="Fusion248002281"
  Placement = pos=(0,0,8) rot=(0,0,1;0rad)
  Refine = true
  Shapes = -> [Cylinder1166,Cut014271]
FEATURE [Part::MultiFuse] Fusion248002112  label="Fusion248002282"
  Refine = true
  Shapes = -> [Fusion248002111,Fusion248002106]
FEATURE [Part::MultiFuse] Fusion248002113  label="Fusion248002283"
  Refine = true
  Shapes = -> [Cut014270,Fusion248002112,Cylinder1165]
FEATURE [Part::Cut] Cut014272  label="Cut014452"
  Base = -> Fusion248002113
  Refine = true
  Tool = -> Fusion248002107
FEATURE [Part::Cut] Cut014273  label="Cut014453"
  Base = -> Cut014272
  Refine = true
  Tool = -> Fusion248002108
FEATURE [Part::Cylinder] Cylinder1189  label="Cylinder1618"
  Angle = 360
  AttacherType = Attacher::AttachEngine3D
  Height = 10
  Placement = pos=(171,45,-2) rot=(0.994721,0.05438,0.087027;2.02933rad)
  Radius = 6
FEATURE [Part::Cylinder] Cylinder1190  label="Cylinder1619"
  Angle = 360
  AttacherType = Attacher::AttachEngine3D
  Height = 23
  Placement = pos=(163,51,7) rot=(0,-1,0;1.36136rad)
  Radius = 6
FEATURE [Part::Cylinder] Cylinder1191  label="Cylinder1620"
  Angle = 360
  AttacherType = Attacher::AttachEngine3D
  Height = 9
  Placement = pos=(167.5,31,-20) rot=(0,0,1;0rad)
  Radius = 14.1
FEATURE [Part::Cylinder] Cylinder1192  label="Cylinder1621"
  Angle = 360
  AttacherType = Attacher::AttachEngine3D
  Height = 9
  Placement = pos=(167.5,31,-20) rot=(0,0,1;0rad)
  Radius = 15.1
FEATURE [Part::Cut] Cut014279  label="air-box-holder_003"
  Base = -> Cylinder1192
  Placement = pos=(6,0,1) rot=(0,0,1;0rad)
  Refine = true
  Tool = -> Cylinder1191
FEATURE [Part::Feature] Face063
  shape: bbox 3.676 x 13.23 x 17.3 mm, 1 faces, 0 solids (baked)
FEATURE [Part::Feature] Face064
  shape: bbox 17.79 x 7.863 x 12.24 mm, 1 faces, 0 solids (baked)
FEATURE [Part::Loft] Loft025
  Closed = false
  MaxDegree = 5
  Ruled = false
  Sections = -> [Face063,Face064]
  Solid = true
FEATURE [Part::MultiFuse] Fusion248002122  label="Fusion248002284"
  Refine = true
  Shapes = -> [Cylinder1190,Cylinder1189,Loft025]
FEATURE [Part::Cylinder] Cylinder1193  label="Cylinder1622"
  Angle = 360
  AttacherType = Attacher::AttachEngine3D
  Height = 15
  Placement = pos=(167.5,31,2) rot=(0,0,1;0rad)
  Radius = 13
FEATURE [Part::Cylinder] Cylinder1194  label="Cylinder1623"
  Angle = 360
  AttacherType = Attacher::AttachEngine3D
  Height = 30
  Placement = pos=(167.5,31,-28) rot=(0,0,1;0rad)
  Radius = 14.1
FEATURE [Part::Fillet] Fillet007052
  Base = -> Cylinder1194
  Edges = 1 edges r=7: [Edge1]
  Placement = pos=(0,0,1) rot=(0,0,1;0rad)
FEATURE [Part::Cut] Cut014280  label="Cut014454"
  Base = -> Fillet007052
  Placement = pos=(6,0,0.5) rot=(0,0,1;0rad)
  Refine = true
  Tool = -> Cylinder1193
FEATURE [Part::Box] Box744  label="Cube906"
  AttacherType = Attacher::AttachEngine3D
  Height = 15
  Length = 10
  Placement = pos=(167,41.5,-19) rot=(0,0,1;0rad)
  Width = 12
FEATURE [Part::Cylinder] Cylinder1195  label="Cylinder1624"
  Angle = 360
  AttacherType = Attacher::AttachEngine3D
  Height = 15
  Placement = pos=(170.5,58,-9) rot=(1,0,0;1.5708rad)
  Radius = 1.6
FEATURE [Part::Cylinder] Cylinder1196  label="Cylinder1625"
  Angle = 360
  AttacherType = Attacher::AttachEngine3D
  Height = 5
  Placement = pos=(170.5,47,-9) rot=(1,0,0;1.5708rad)
  Radius = 3.2
FEATURE [Part::MultiFuse] Fusion248002123  label="Fusion248002285"
  Placement = pos=(1,0,1) rot=(0,0,1;0rad)
  Refine = true
  Shapes = -> [Cylinder1195,Cylinder1196]
FEATURE [Part::Box] Box745  label="Cube907"
  AttacherType = Attacher::AttachEngine3D
  Height = 9.5
  Length = 1.5
  Placement = pos=(175.5,43.5,-19) rot=(0,0,1;0rad)
  Width = 13
FEATURE [Part::Box] Box746  label="Cube908"
  AttacherType = Attacher::AttachEngine3D
  Height = 9
  Length = 2
  Placement = pos=(177,45,-19) rot=(0,0,1;0rad)
  Width = 8
FEATURE [Part::Cylinder] Cylinder1197  label="Cylinder1626"
  Angle = 360
  AttacherType = Attacher::AttachEngine3D
  Height = 15
  Placement = pos=(165,49,-14.5) rot=(0,1,0;1.5708rad)
  Radius = 1
FEATURE [Part::Cylinder] Cylinder1198  label="Cylinder1627"
  Angle = 360
  AttacherType = Attacher::AttachEngine3D
  Height = 1
  Placement = pos=(178,49,-14.5) rot=(0,1,0;1.5708rad)
  Radius = 2.5
FEATURE [Part::Box] Box747  label="Cube909"
  AttacherType = Attacher::AttachEngine3D
  Height = 3
  Length = 10
  Placement = pos=(166,44.5,-19) rot=(0,0,1;0rad)
  Width = 12
FEATURE [Part::Box] Box748  label="Cube910"
  AttacherType = Attacher::AttachEngine3D
  Height = 4
  Length = 10
  Placement = pos=(166,53.5,-18) rot=(0,0,1;0rad)
  Width = 4
FEATURE [Part::Fillet] Fillet007053
  Base = -> Box748
  Edges = 1 edges r=3: [Edge9]
FEATURE [Part::Cut] Cut014281  label="Cut014455"
  Base = -> Box747
  Placement = pos=(1,0,0) rot=(0,0,1;0rad)
  Refine = true
  Tool = -> Fillet007053
FEATURE [Part::Cylinder] Cylinder1199  label="Cylinder1628"
  Angle = 360
  AttacherType = Attacher::AttachEngine3D
  Height = 23
  Placement = pos=(163,51,10) rot=(0,-1,0;1.36136rad)
  Radius = 2.6
FEATURE [Part::Chamfer] Chamfer161
  Base = -> Fusion248002122
  Edges = 4 edges r=2.49: [Edge3,Edge4,Edge5,Edge8]
  Placement = pos=(0,0,3) rot=(0,0,1;0rad)
FEATURE [Part::Cylinder] Cylinder1200  label="Cylinder1629"
  Angle = 360
  AttacherType = Attacher::AttachEngine3D
  Height = 18
  Placement = pos=(163,51,10) rot=(0,-1,0;1.36136rad)
  Radius = 2.6
FEATURE [Part::Cut] Cut014282  label="Cut014456"
  Base = -> Cylinder1199
  Refine = true
  Tool = -> Cylinder1200
FEATURE [Part::MultiFuse] Fusion248002124
  Refine = true
  Shapes = -> [Cylinder1198,Cylinder1197]
FEATURE [Part::Cut] Cut014283  label="Cut014457"
  Base = -> Chamfer161
  Placement = pos=(0,0,-2.5) rot=(0,0,1;0rad)
  Refine = true
  Tool = -> Cut014282
FEATURE [Part::MultiFuse] Fusion248002125
  Refine = true
  Shapes = -> [Cut014283,Cut014279]
FEATURE [Part::MultiFuse] Fusion248002126  label="Fusion248002286"
  Refine = true
  Shapes = -> [Fusion248002125,Cut014281]
FEATURE [Part::MultiFuse] Fusion248002127  label="Fusion248002287"
  Refine = true
  Shapes = -> [Fusion248002126,Box744]
FEATURE [Part::Cut] Cut014284  label="Cut014458"
  Base = -> Fusion248002127
  Refine = true
  Tool = -> Cut014280
FEATURE [Part::Cut] Cut014285  label="Cut014459"
  Base = -> Cut014284
  Refine = true
  Tool = -> Box745
FEATURE [Part::MultiFuse] Fusion248002128  label="Fusion248002288"
  Refine = true
  Shapes = -> [Cut014285,Box746]
FEATURE [Part::Cut] Cut014286  label="Cut014460"
  Base = -> Fusion248002128
  Refine = true
  Tool = -> Fusion248002123
FEATURE [Part::Cut] Cut014287  label="Cut014461"
  Base = -> Cut014286
  Refine = true
  Tool = -> Fusion248002124
FEATURE [Part::Chamfer] Chamfer162  label="air-box-holder"
  Base = -> Cut014287
  Edges = 1 edges r=1.49: [Edge71]
FEATURE [Part::Cylinder] Cylinder1201  label="Cylinder1630"
  Angle = 360
  AttacherType = Attacher::AttachEngine3D
  Height = 47
  Placement = pos=(166,0,-44) rot=(0,0,1;0rad)
  Radius = 14
FEATURE [Part::Fillet] Fillet007054
  Base = -> Cylinder1201
  Edges = 2 edges r=7: [Edge1,Edge3]
FEATURE [Part::Box] Box749  label="Cube911"
  AttacherType = Attacher::AttachEngine3D
  Height = 10
  Length = 32
  Placement = pos=(151,-16,2) rot=(0,0,1;0rad)
  Width = 32
FEATURE [Part::Box] Box750  label="Cube912"
  AttacherType = Attacher::AttachEngine3D
  Height = 10
  Length = 32
  Placement = pos=(151,-16,-53) rot=(0,0,1;0rad)
  Width = 32
FEATURE [Part::MultiFuse] Fusion248002129  label="Fusion248002289"
  Refine = true
  Shapes = -> [Box750,Box749]
FEATURE [Part::Cut] Cut014288  label="Cut014462"
  Base = -> Fillet007054
  Placement = pos=(7.5,31,0) rot=(0,0,1;0rad)
  Refine = true
  Tool = -> Fusion248002129
FEATURE [Part::Feature] Face065
  Placement = pos=(0.5,0,6) rot=(0,0,1;0rad)
  shape: bbox 22.75 x 20.11 x 2e-07 mm, 1 faces, 0 solids (baked)
FEATURE [Part::Box] Box751  label="Cube913"
  AttacherType = Attacher::AttachEngine3D
  Height = 8
  Length = 10
  Placement = pos=(156,24,-8) rot=(0,0,1;0rad)
  Width = 14
FEATURE [Part::Fillet] Fillet007055
  Base = -> Box751
  Edges = 4 edges r=3.5: [Edge9,Edge10,Edge11,Edge12]
  Placement = pos=(13.7075,0,55.068) rot=(0,1,0;0.349066rad)
FEATURE [Part::Feature] Face066
  shape: bbox 15.41 x 11.89 x 2e-07 mm, 1 faces, 0 solids (baked)
FEATURE [Part::Feature] Face067
  shape: bbox 6.072 x 6.626 x 3.506 mm, 1 faces, 0 solids (baked)
FEATURE [Part::Loft] Loft026
  Closed = false
  MaxDegree = 5
  Placement = pos=(0,0,8) rot=(0,0,1;0rad)
  Ruled = false
  Sections = -> [Face066,Face067]
  Solid = true
FEATURE [Part::Cylinder] Cylinder1202  label="Cylinder1631"
  Angle = 360
  AttacherType = Attacher::AttachEngine3D
  Height = 39
  Placement = pos=(166,0,-40) rot=(0,0,1;0rad)
  Radius = 12
FEATURE [Part::Chamfer] Chamfer163
  Base = -> Cylinder1202
  Edges = 2 edges r=7: [Edge1,Edge3]
  Placement = pos=(7.5,31,0) rot=(0,0,1;0rad)
FEATURE [Part::Feature] Face068
  shape: bbox 3.01 x 15.4 x 8.269 mm, 1 faces, 0 solids (baked)
FEATURE [Part::Loft] Loft027
  Closed = false
  MaxDegree = 5
  Ruled = false
  Sections = -> [Face068,Face065]
  Solid = true
FEATURE [Part::MultiFuse] Fusion248002130
  Refine = true
  Shapes = -> [Fillet007055,Loft027]
FEATURE [Part::Cut] Cut014289
  Base = -> Fusion248002130
  Refine = true
  Tool = -> Loft026
FEATURE [Part::MultiFuse] Fusion248002131  label="Fusion248002290"
  Refine = true
  Shapes = -> [Cut014288,Cut014289]
FEATURE [Part::Cut] Cut014290  label="air-intake-lower"
  Base = -> Fusion248002131
  Refine = true
  Tool = -> Chamfer163
FEATURE [Part::Box] Box752  label="Cube914"
  AttacherType = Attacher::AttachEngine3D
  Height = 6.5
  Length = 14
  Placement = pos=(225.5,7,-22) rot=(0,0,1;0rad)
  Width = 42
FEATURE [Part::MultiFuse] Fusion248002132  label="Fusion248002291"
  Placement = pos=(0,-1,0) rot=(0,0,1;0rad)
  Refine = true
  Shapes = -> [Box752,Box722]
FEATURE [Part::Cylinder] Cylinder1203  label="Cylinder1632"
  Angle = 360
  AttacherType = Attacher::AttachEngine3D
  Height = 50
  Placement = pos=(198,36,-31) rot=(0,1,0;1.5708rad)
  Radius = 11
FEATURE [Part::Cone] Cone026
  Angle = 360
  AttacherType = Attacher::AttachEngine3D
  Height = 3
  Placement = pos=(195,36,-31) rot=(0,1,0;1.5708rad)
  Radius1 = 4
  Radius2 = 11
FEATURE [Part::Cone] Cone027
  Angle = 360
  AttacherType = Attacher::AttachEngine3D
  Height = 3
  Placement = pos=(248,36,-31) rot=(0,1,0;1.5708rad)
  Radius1 = 11
  Radius2 = 4
FEATURE [Part::MultiFuse] Fusion248002134  label="Fusion248002292"
  Refine = true
  Shapes = -> [Cylinder1203,Cone027,Cone026]
FEATURE [Part::Fillet] Fillet007056
  Base = -> Fusion248002134
  Edges = 2 edges r=2: [Edge3,Edge5]
FEATURE [Part::Fillet] Fillet007057
  Base = -> Fillet007056
  Edges = 2 edges r=3: [Edge3,Edge11]
  Placement = pos=(0,7,0) rot=(0,0,1;0rad)
FEATURE [Part::Cylinder] Cylinder1204  label="Cylinder1633"
  Angle = 360
  AttacherType = Attacher::AttachEngine3D
  Height = 50
  Placement = pos=(198,36,-31) rot=(0,1,0;1.5708rad)
  Radius = 11
FEATURE [Part::Cone] Cone028
  Angle = 360
  AttacherType = Attacher::AttachEngine3D
  Height = 3
  Placement = pos=(195,36,-31) rot=(0,1,0;1.5708rad)
  Radius1 = 4
  Radius2 = 11
FEATURE [Part::Cone] Cone029
  Angle = 360
  AttacherType = Attacher::AttachEngine3D
  Height = 3
  Placement = pos=(248,36,-31) rot=(0,1,0;1.5708rad)
  Radius1 = 11
  Radius2 = 4
FEATURE [Part::MultiFuse] Fusion248002135  label="Fusion248002293"
  Refine = true
  Shapes = -> [Cylinder1204,Cone029,Cone028]
FEATURE [Part::Fillet] Fillet007058
  Base = -> Fusion248002135
  Edges = 2 edges r=2: [Edge3,Edge5]
FEATURE [Part::Fillet] Fillet007059
  Base = -> Fillet007058
  Edges = 2 edges r=3: [Edge3,Edge11]
  Placement = pos=(0,-17,0) rot=(0,0,1;0rad)
FEATURE [Part::Box] Box754  label="Cube916"
  AttacherType = Attacher::AttachEngine3D
  Height = 24
  Length = 4
  Placement = pos=(201.5,7,-43) rot=(0,0,1;0rad)
  Width = 48
FEATURE [Part::Box] Box755  label="Cube917"
  AttacherType = Attacher::AttachEngine3D
  Height = 22
  Length = 4
  Placement = pos=(201.5,8,-42) rot=(0,0,1;0rad)
  Width = 46
FEATURE [Part::Box] Box756  label="Cube918"
  AttacherType = Attacher::AttachEngine3D
  Height = 1
  Length = 4
  Placement = pos=(201.5,7,-20) rot=(0,0,1;0rad)
  Width = 48
FEATURE [Part::Fillet] Fillet007060
  Base = -> Box755
  Edges = 4 edges r=10.99: [Edge9,Edge10,Edge11,Edge12]
FEATURE [Part::Fillet] Fillet007061
  Base = -> Box754
  Edges = 4 edges r=11.99: [Edge9,Edge10,Edge11,Edge12]
FEATURE [Part::MultiFuse] Fusion248002136  label="Fusion248002294"
  Refine = true
  Shapes = -> [Fillet007060,Box756]
FEATURE [Part::Cut] Cut014293  label="Cut014463"
  Base = -> Fillet007061
  Refine = true
  Tool = -> Fusion248002136
FEATURE [Part::Box] Box757  label="Cube919"
  AttacherType = Attacher::AttachEngine3D
  Height = 24
  Length = 4
  Placement = pos=(201.5,7,-43) rot=(0,0,1;0rad)
  Width = 48
FEATURE [Part::Box] Box758  label="Cube920"
  AttacherType = Attacher::AttachEngine3D
  Height = 22
  Length = 4
  Placement = pos=(201.5,8,-42) rot=(0,0,1;0rad)
  Width = 46
FEATURE [Part::Box] Box759  label="Cube921"
  AttacherType = Attacher::AttachEngine3D
  Height = 1
  Length = 4
  Placement = pos=(201.5,7,-20) rot=(0,0,1;0rad)
  Width = 48
FEATURE [Part::Fillet] Fillet007062
  Base = -> Box758
  Edges = 4 edges r=10.99: [Edge9,Edge10,Edge11,Edge12]
FEATURE [Part::Fillet] Fillet007063
  Base = -> Box757
  Edges = 4 edges r=11.99: [Edge9,Edge10,Edge11,Edge12]
FEATURE [Part::MultiFuse] Fusion248002137  label="Fusion248002295"
  Refine = true
  Shapes = -> [Fillet007062,Box759]
FEATURE [Part::Cut] Cut014294  label="Cut014464"
  Base = -> Fillet007063
  Placement = pos=(38,0,0) rot=(0,0,1;0rad)
  Refine = true
  Tool = -> Fusion248002137
FEATURE [Part::MultiFuse] Fusion248002139  label="Fusion248002296"
  Placement = pos=(0,-4,-2) rot=(0,0,1;0rad)
  Refine = true
  Shapes = -> [Fillet007057,Fillet007059,Cut014293,Cut014294]
FEATURE [Part::Cylinder] Cylinder1216  label="Cylinder1634"
  Angle = 360
  AttacherType = Attacher::AttachEngine3D
  Height = 45
  Placement = pos=(820,-4.5,-59) rot=(1,0,0;1.5708rad)
  Radius = 50
FEATURE [Part::Cylinder] Cylinder1217  label="Cylinder1635"
  Angle = 80
  AttacherType = Attacher::AttachEngine3D
  Height = 45
  Placement = pos=(820,-4.5,-57) rot=(1,0,0;1.5708rad)
  Radius = 50
FEATURE [Part::Cylinder] Cylinder1218  label="Cylinder1636"
  Angle = 60
  AttacherType = Attacher::AttachEngine3D
  Height = 45
  Placement = pos=(820,-4.5,-57) rot=(1,0,0;1.5708rad)
  Radius = 52
FEATURE [Part::Cut] Cut014299  label="Cut014465"
  Base = -> Cylinder1218
  Refine = true
  Tool = -> Cylinder1217
FEATURE [Part::Cut] Cut014300  label="Cut014466"
  Base = -> Cut014299
  Refine = true
  Tool = -> Cylinder1216
FEATURE [Part::Cylinder] Cylinder1219  label="Cylinder1637"
  Angle = 360
  AttacherType = Attacher::AttachEngine3D
  Height = 4
  Placement = pos=(862,-14.5,-23) rot=(1,0,0;1.5708rad)
  Radius = 2.5
FEATURE [Part::Cylinder] Cylinder1220  label="Cylinder1638"
  Angle = 360
  AttacherType = Attacher::AttachEngine3D
  Height = 52
  Placement = pos=(308.5,45.5,-1.5) rot=(1,0,0;1.5708rad)
  Radius = 1.6
FEATURE [Part::Cylinder] Cylinder1221  label="Cylinder1639"
  Angle = 360
  AttacherType = Attacher::AttachEngine3D
  Height = 4
  Placement = pos=(862,-38.5,-23) rot=(1,0,0;1.5708rad)
  Radius = 2.5
FEATURE [Part::MultiFuse] Fusion248002148  label="Fusion248002297"
  Placement = pos=(901.763,45.5,-627.29) rot=(0,1,0;3.92699rad)
  Refine = true
  Shapes = -> [Cylinder1221,Cylinder1219]
FEATURE [Part::Fillet] Fillet007066
  Base = -> Cut014300
  Edges = 1 edges r=1.5: [Edge1]
FEATURE [Part::Mirroring] Part__Mirroring113  label="Fillet007066 (Mirror #87)"
  Base = (0,0,0)
  Normal = (1,0,0)
  Placement = pos=(1166,45.5,17) rot=(0,0,1;0rad)
  Source = -> Fillet007066
FEATURE [Part::Cylinder] Cylinder1222  label="Cylinder1640"
  Angle = 360
  AttacherType = Attacher::AttachEngine3D
  Height = 10
  Placement = pos=(304,41,-15) rot=(1,0,0;1.5708rad)
  Radius = 2.5
FEATURE [Part::Cylinder] Cylinder1223  label="Cylinder1641"
  Angle = 360
  AttacherType = Attacher::AttachEngine3D
  Height = 10
  Placement = pos=(304,41,-15) rot=(1,0,0;1.5708rad)
  Radius = 1.6
FEATURE [Part::MultiFuse] Fusion248002149  label="Fusion248002298"
  Refine = true
  Shapes = -> [Fusion248002148,Cylinder1222,Part__Mirroring113]
FEATURE [Part::MultiFuse] Fusion248002150  label="Fusion248002299"
  Refine = true
  Shapes = -> [Cylinder1223,Cylinder1220]
FEATURE [Part::Cut] Cut014301  label="Cut014467"
  Base = -> Fusion248002149
  Placement = pos=(0,-3,0) rot=(0,0,1;0rad)
  Refine = true
  Tool = -> Fusion248002150
FEATURE [Part::Chamfer] Chamfer165
  Base = -> Cut014273
  Edges = 1 edges r=7: [Edge12]
FEATURE [Part::Fillet] Fillet007067  label="wing-support-left"
  Base = -> Chamfer165
  Edges = 1 edges r=3: [Edge15]
FEATURE [Part::Box] Box764  label="Cube926"
  AttacherType = Attacher::AttachEngine3D
  Height = 20
  Length = 25
  Placement = pos=(128,45.5,-18) rot=(0,0,1;0rad)
  Width = 8
FEATURE [Part::Cylinder] Cylinder1224  label="Cylinder1642"
  Angle = 360
  AttacherType = Attacher::AttachEngine3D
  Height = 24.5
  Placement = pos=(144,53.5,2) rot=(1,0,0;1.5708rad)
  Radius = 3
FEATURE [Part::Cylinder] Cylinder1225  label="Cylinder1643"
  Angle = 360
  AttacherType = Attacher::AttachEngine3D
  Height = 18
  Placement = pos=(131,51,-5) rot=(1,0,0;0.785398rad)
  Radius = 3
FEATURE [Part::Feature] Face069
  shape: bbox 7.785 x 2e-07 x 7.712 mm, 1 faces, 0 solids (baked)
FEATURE [Part::Feature] Face070
  shape: bbox 7.318 x 4.987 x 4.987 mm, 1 faces, 0 solids (baked)
FEATURE [Part::Loft] Loft028
  Closed = false
  MaxDegree = 5
  Ruled = true
  Sections = -> [Face069,Face070]
  Solid = true
FEATURE [Part::Cylinder] Cylinder1226  label="Cylinder1644"
  Angle = 360
  AttacherType = Attacher::AttachEngine3D
  Height = 3
  Placement = pos=(131,31,12) rot=(1,0,0;1.5708rad)
  Radius = 3
FEATURE [Part::MultiFuse] Fusion248002151  label="Fusion248002300"
  Placement = pos=(0,1,8) rot=(0,0,1;0rad)
  Refine = true
  Shapes = -> [Loft028,Cylinder1226]
FEATURE [Part::Cylinder] Cylinder1227  label="Cylinder1645"
  Angle = 360
  AttacherType = Attacher::AttachEngine3D
  Height = 5
  Placement = pos=(131,33,12) rot=(1,0,0;1.5708rad)
  Radius = 1.6
FEATURE [Part::Cylinder] Cylinder1228  label="Cylinder1646"
  Angle = 360
  AttacherType = Attacher::AttachEngine3D
  Height = 25
  Placement = pos=(144,53,-6) rot=(1,0,0;1.5708rad)
  Radius = 1.6
FEATURE [Part::MultiFuse] Fusion248002152  label="Fusion248002301"
  Placement = pos=(0,1,8) rot=(0,0,1;0rad)
  Refine = true
  Shapes = -> [Cylinder1227,Cylinder1228]
FEATURE [Part::Cylinder] Cylinder1229  label="Cylinder1647"
  Angle = 360
  AttacherType = Attacher::AttachEngine3D
  Height = 15
  Placement = pos=(132,61.5,-16) rot=(1,0,0;1.5708rad)
  Radius = 1.6
FEATURE [Part::Cylinder] Cylinder1230  label="Cylinder1648"
  Angle = 360
  AttacherType = Attacher::AttachEngine3D
  Height = 2.5
  Placement = pos=(132,49,-16) rot=(1,0,0;1.5708rad)
  Radius = 3
FEATURE [Part::MultiFuse] Fusion248002153  label="Fusion248002302"
  Placement = pos=(4,-1.5,7) rot=(0,0,1;0rad)
  Refine = true
  Shapes = -> [Cylinder1229,Cylinder1230]
FEATURE [Part::Box] Box765  label="Cube927"
  AttacherType = Attacher::AttachEngine3D
  Height = 9.5
  Length = 10
  Placement = pos=(143,45.5,-18) rot=(0,0,1;0rad)
  Width = 5
FEATURE [Part::Fillet] Fillet007068
  Base = -> Box765
  Edges = 1 edges r=4: [Edge2]
FEATURE [Part::Cylinder] Cylinder1231  label="Cylinder1649"
  Angle = 360
  AttacherType = Attacher::AttachEngine3D
  Height = 3.5
  Placement = pos=(148.5,53.5,-13.5) rot=(1,0,0;1.5708rad)
  Radius = 3
FEATURE [Part::Cylinder] Cylinder1232  label="Cylinder1650"
  Angle = 360
  AttacherType = Attacher::AttachEngine3D
  Height = 1.75
  Placement = pos=(498.5,51.75,-13.5) rot=(1,0,0;1.5708rad)
  Radius = 2.1
FEATURE [Part::Cylinder] Cylinder1233  label="Cylinder1651"
  Angle = 360
  AttacherType = Attacher::AttachEngine3D
  Height = 3.5
  Placement = pos=(498.5,53.5,-13.5) rot=(1,0,0;1.5708rad)
  Radius = 1.5
FEATURE [Part::MultiFuse] Fusion248002154  label="Fusion248002303"
  Placement = pos=(-350,0,0) rot=(0,0,1;0rad)
  Refine = true
  Shapes = -> [Cylinder1232,Cylinder1233]
FEATURE [Part::Cut] Cut014302  label="Cut014468"
  Base = -> Box764
  Refine = true
  Tool = -> Fillet007068
FEATURE [Part::MultiFuse] Fusion248002155  label="Fusion248002304"
  Refine = true
  Shapes = -> [Cut014302,Cylinder1231]
FEATURE [Part::Cut] Cut014303  label="Cut014469"
  Base = -> Fusion248002155
  Placement = pos=(0,0,3) rot=(0,0,1;0rad)
  Refine = true
  Tool = -> Fusion248002154
FEATURE [Part::Cylinder] Cylinder1234  label="Cylinder1652"
  Angle = 360
  AttacherType = Attacher::AttachEngine3D
  Height = 23
  Placement = pos=(131,52,-6) rot=(1,0,0;0.785398rad)
  Radius = 3
FEATURE [Part::Cylinder] Cylinder1235  label="Cylinder1653"
  Angle = 360
  AttacherType = Attacher::AttachEngine3D
  Height = 18
  Placement = pos=(131,52,-6) rot=(1,0,0;0.785398rad)
  Radius = 3
FEATURE [Part::Cut] Cut014304  label="Cut014470"
  Base = -> Cylinder1234
  Refine = true
  Tool = -> Cylinder1235
FEATURE [Part::MultiFuse] Fusion248002156  label="Fusion248002305"
  Placement = pos=(0,0,8) rot=(0,0,1;0rad)
  Refine = true
  Shapes = -> [Cylinder1225,Cut014304]
FEATURE [Part::MultiFuse] Fusion248002157  label="Fusion248002306"
  Refine = true
  Shapes = -> [Fusion248002156,Fusion248002151]
FEATURE [Part::MultiFuse] Fusion248002158  label="Fusion248002307"
  Refine = true
  Shapes = -> [Cut014303,Fusion248002157,Cylinder1224]
FEATURE [Part::Cut] Cut014305  label="Cut014471"
  Base = -> Fusion248002158
  Refine = true
  Tool = -> Fusion248002152
FEATURE [Part::Cut] Cut014306  label="Cut014472"
  Base = -> Cut014305
  Refine = true
  Tool = -> Fusion248002153
FEATURE [Part::Chamfer] Chamfer166
  Base = -> Cut014306
  Edges = 1 edges r=7: [Edge12]
FEATURE [Part::Fillet] Fillet007069  label="wing-support-left-lifted001"
  Base = -> Chamfer166
  Edges = 1 edges r=3: [Edge15]
FEATURE [Part::Mirroring] Part__Mirroring114  label="wing-support-right"
  Base = (0,0,0)
  Normal = (0,1,0)
  Placement = pos=(0,170,0) rot=(0,0,1;0rad)
  Source = -> Fillet007069
FEATURE [Part::Box] Box766  label="Cube928"
  AttacherType = Attacher::AttachEngine3D
  Height = 17
  Length = 10
  Placement = pos=(-2,0,1.5) rot=(0,0,1;0rad)
  Width = 60
FEATURE [Part::Fillet] Fillet007070
  Base = -> Box766
  Edges = 4 edges r=3: [Edge9,Edge10,Edge11,Edge12]
  Placement = pos=(485.5,55,-23) rot=(0,0,1;0rad)
FEATURE [Part::Box] Box767  label="Cube929"
  AttacherType = Attacher::AttachEngine3D
  Height = 10
  Length = 10
  Placement = pos=(483.5,63,-7.5) rot=(0,0,1;0rad)
  Width = 44
FEATURE [Part::Cut] Cut014307  label="Cut014473"
  Base = -> Fillet007070
  Refine = true
  Tool = -> Box767
FEATURE [Part::Cylinder] Cylinder1236  label="Cylinder1654"
  Angle = 360
  AttacherType = Attacher::AttachEngine3D
  Height = 10
  Placement = pos=(3,60,10) rot=(1,0,0;1.5708rad)
  Radius = 1.2
FEATURE [Part::Cylinder] Cylinder1237  label="Cylinder1655"
  Angle = 360
  AttacherType = Attacher::AttachEngine3D
  Height = 10
  Placement = pos=(3,10,10) rot=(1,0,0;1.5708rad)
  Radius = 1.2
FEATURE [Part::MultiFuse] Fusion248002159  label="Fusion248002308"
  Placement = pos=(485.5,55,-23) rot=(0,0,1;0rad)
  Refine = true
  Shapes = -> [Cylinder1236,Cylinder1237]
FEATURE [Part::Chamfer] Chamfer167
  Base = -> Cut014307
  Edges = 2 edges r=2.99: [Edge18,Edge25]
FEATURE [Part::Cut] Cut014308  label="Cut014474"
  Base = -> Chamfer167
  Placement = pos=(18,0,5) rot=(0,0,1;0rad)
  Refine = true
  Tool = -> Fusion248002159
FEATURE [Part::Cylinder] Cylinder1238  label="Cylinder1656"
  Angle = 360
  AttacherType = Attacher::AttachEngine3D
  Height = 10
  Placement = pos=(483.5,85,-14.5) rot=(0,1,0;1.5708rad)
  Radius = 2.6
FEATURE [Part::Cylinder] Cylinder1239  label="Cylinder1657"
  Angle = 360
  AttacherType = Attacher::AttachEngine3D
  Height = 10
  Placement = pos=(483.5,79,-10.5) rot=(0,1,0;1.5708rad)
  Radius = 1.2
FEATURE [Part::Cylinder] Cylinder1240  label="Cylinder1658"
  Angle = 360
  AttacherType = Attacher::AttachEngine3D
  Height = 10
  Placement = pos=(483.5,91,-10.5) rot=(0,1,0;1.5708rad)
  Radius = 1.2
FEATURE [Part::Cylinder] Cylinder1241  label="Cylinder1659"
  Angle = 360
  AttacherType = Attacher::AttachEngine3D
  Height = 10
  Placement = pos=(483.5,79,-18.5) rot=(0,1,0;1.5708rad)
  Radius = 1.2
FEATURE [Part::Cylinder] Cylinder1242  label="Cylinder1660"
  Angle = 360
  AttacherType = Attacher::AttachEngine3D
  Height = 10
  Placement = pos=(483.5,91,-18.5) rot=(0,1,0;1.5708rad)
  Radius = 1.2
FEATURE [Part::MultiFuse] Fusion248002160  label="Fusion248002309"
  Placement = pos=(18,0,5) rot=(0,0,1;0rad)
  Refine = true
  Shapes = -> [Cylinder1238,Cylinder1242,Cylinder1239,Cylinder1240,Cylinder1241]
FEATURE [Part::Cut] Cut014309  label="Cut014475"
  Base = -> Cut014308
  Placement = pos=(0.5,0,0) rot=(0,0,1;0rad)
  Refine = true
  Tool = -> Fusion248002160
FEATURE [Part::Box] Box768  label="Cube930"
  AttacherType = Attacher::AttachEngine3D
  Height = 10
  Length = 2
  Placement = pos=(512,55,-16.5) rot=(0,0,1;0rad)
  Width = 8
FEATURE [Part::Fillet] Fillet007071
  Base = -> Box768
  Edges = 1 edges r=3: [Edge9]
FEATURE [Part::Box] Box769  label="Cube931"
  AttacherType = Attacher::AttachEngine3D
  Height = 10
  Length = 5
  Placement = pos=(514,8,-16.5) rot=(0,0,1;0rad)
  Width = 55
FEATURE [Part::Box] Box770  label="Cube932"
  AttacherType = Attacher::AttachEngine3D
  Height = 27
  Length = 2
  Placement = pos=(509,-7,-25) rot=(0,0,1;0rad)
  Width = 43.5
FEATURE [Part::Chamfer] Chamfer168
  Base = -> Cut014301
  Edges = 6 edges r=3: [Edge14,Edge15,Edge21,Edge23,Edge25,Edge27]
FEATURE [Part::Cylinder] Cylinder1243  label="Cylinder1661"
  Angle = 360
  AttacherType = Attacher::AttachEngine3D
  Height = 10
  Placement = pos=(503,0,0) rot=(0,1,0;1.5708rad)
  Radius = 1.1
FEATURE [Part::Cylinder] Cylinder1244  label="Cylinder1662"
  Angle = 360
  AttacherType = Attacher::AttachEngine3D
  Height = 10
  Placement = pos=(503,28,0) rot=(0,1,0;1.5708rad)
  Radius = 1.1
FEATURE [Part::MultiFuse] Fusion248002161  label="Fusion248002310"
  Placement = pos=(0,1.5,-20) rot=(0,0,1;0rad)
  Refine = true
  Shapes = -> [Cylinder1244,Cylinder1243]
FEATURE [Part::Cylinder] Cylinder1245  label="Cylinder1663"
  Angle = 360
  AttacherType = Attacher::AttachEngine3D
  Height = 10
  Placement = pos=(503,0,0) rot=(0,1,0;1.5708rad)
  Radius = 0.9
FEATURE [Part::Cylinder] Cylinder1246  label="Cylinder1664"
  Angle = 360
  AttacherType = Attacher::AttachEngine3D
  Height = 10
  Placement = pos=(503,28,0) rot=(0,1,0;1.5708rad)
  Radius = 0.9
FEATURE [Part::MultiFuse] Fusion248002162  label="Fusion248002311"
  Placement = pos=(0,1.5,-20) rot=(0,0,1;0rad)
  Refine = true
  Shapes = -> [Cylinder1246,Cylinder1245]
FEATURE [Part::Box] Box771  label="Cube933"
  AttacherType = Attacher::AttachEngine3D
  Height = 6
  Length = 1
  Placement = pos=(507,-6,-23) rot=(0,0,1;0rad)
  Width = 42
FEATURE [Part::Box] Box772  label="wing-rear-left-RUBBER"
  AttacherType = Attacher::AttachEngine3D
  Height = 40
  Length = 1
  Placement = pos=(508,-5.5,-62) rot=(0,0,1;0rad)
  Width = 45
FEATURE [Part::MultiFuse] Fusion248002163  label="Fusion248002312"
  Refine = true
  Shapes = -> [Fillet007071,Box769]
FEATURE [Part::Box] Box773  label="Cube935"
  AttacherType = Attacher::AttachEngine3D
  Height = 8
  Length = 3
  Placement = pos=(511,8,-16.5) rot=(0,0,1;0rad)
  Width = 25
FEATURE [Part::Cylinder] Cylinder1247  label="Cylinder1665"
  Angle = 360
  AttacherType = Attacher::AttachEngine3D
  Height = 2
  Placement = pos=(504,0,0) rot=(0,1,0;1.5708rad)
  Radius = 2.5
FEATURE [Part::Cylinder] Cylinder1248  label="Cylinder1666"
  Angle = 360
  AttacherType = Attacher::AttachEngine3D
  Height = 2
  Placement = pos=(504,28,0) rot=(0,1,0;1.5708rad)
  Radius = 2.5
FEATURE [Part::MultiFuse] Fusion248002164  label="Fusion248002313"
  Placement = pos=(2,1.5,-20) rot=(0,0,1;0rad)
  Refine = true
  Shapes = -> [Cylinder1248,Cylinder1247]
FEATURE [Part::MultiFuse] Fusion248002165  label="Fusion248002314"
  Refine = true
  Shapes = -> [Fusion248002164,Box771]
FEATURE [Part::Cut] Cut014310  label="wing-rear-left-flap-retainer"
  Base = -> Fusion248002165
  Placement = pos=(0,1.5,-5) rot=(0,0,1;0rad)
  Refine = true
  Tool = -> Fusion248002162
FEATURE [Part::Cut] Cut014311  label="Cut014476"
  Base = -> Box770
  Refine = true
  Tool = -> Fusion248002161
FEATURE [Part::Cylinder] Cylinder1249  label="Cylinder1667"
  Angle = 360
  AttacherType = Attacher::AttachEngine3D
  Height = 2
  Placement = pos=(503,0,0) rot=(0,1,0;1.5708rad)
  Radius = 2.2
FEATURE [Part::Cylinder] Cylinder1250  label="Cylinder1668"
  Angle = 360
  AttacherType = Attacher::AttachEngine3D
  Height = 2
  Placement = pos=(503,28,0) rot=(0,1,0;1.5708rad)
  Radius = 2.2
FEATURE [Part::MultiFuse] Fusion248002166  label="Fusion248002315"
  Placement = pos=(15,1.5,-20) rot=(0,0,1;0rad)
  Refine = true
  Shapes = -> [Cylinder1250,Cylinder1249]
FEATURE [Part::Chamfer] Chamfer169
  Base = -> Fusion248002166
  Edges = 2 edges r=1.99: [Edge3,Edge6]
  Placement = pos=(-9,0,0) rot=(0,0,1;0rad)
FEATURE [Part::Cut] Cut014312  label="Cut014477"
  Base = -> Cut014311
  Refine = true
  Tool = -> Chamfer169
FEATURE [Part::Fillet] Fillet007072
  Base = -> Cut014312
  Edges = 1 edges r=1.5: [Edge11]
FEATURE [Part::Chamfer] Chamfer170
  Base = -> Fillet007072
  Edges = 1 edges r=1.9: [Edge7]
  Placement = pos=(0,1.5,-5) rot=(0,0,1;0rad)
FEATURE [Part::Cylinder] Cylinder1252  label="Cylinder1669"
  Angle = 360
  AttacherType = Attacher::AttachEngine3D
  Height = 10
  Placement = pos=(503,28,0) rot=(0,1,0;1.5708rad)
  Radius = 1.1
FEATURE [Part::Cylinder] Cylinder1253  label="Cylinder1670"
  Angle = 360
  AttacherType = Attacher::AttachEngine3D
  Height = 2
  Placement = pos=(511,28,0) rot=(0,1,0;1.5708rad)
  Radius = 2.2
FEATURE [Part::Chamfer] Chamfer171
  Base = -> Cylinder1253
  Edges = 1 edges r=1.99: [Edge3]
FEATURE [Part::MultiFuse] Fusion248002168  label="Fusion248002316"
  Placement = pos=(6,-16,-11.5) rot=(0,0,1;0rad)
  Refine = true
  Shapes = -> [Cylinder1252,Chamfer171]
FEATURE [Part::Cylinder] Cylinder1254  label="Cylinder1671"
  Angle = 360
  AttacherType = Attacher::AttachEngine3D
  Height = 10
  Placement = pos=(509,29,-11.5) rot=(0,1,0;1.5708rad)
  Radius = 0.9
FEATURE [Part::Cylinder] Cylinder1255  label="Cylinder1672"
  Angle = 360
  AttacherType = Attacher::AttachEngine3D
  Height = 10
  Placement = pos=(503,28,0) rot=(0,1,0;1.5708rad)
  Radius = 1.1
FEATURE [Part::Cylinder] Cylinder1256  label="Cylinder1673"
  Angle = 360
  AttacherType = Attacher::AttachEngine3D
  Height = 2
  Placement = pos=(511,28,0) rot=(0,1,0;1.5708rad)
  Radius = 2.2
FEATURE [Part::Chamfer] Chamfer172
  Base = -> Cylinder1256
  Edges = 1 edges r=1.99: [Edge3]
FEATURE [Part::MultiFuse] Fusion248002169  label="Fusion248002317"
  Placement = pos=(6,1,-11.5) rot=(0,0,1;0rad)
  Refine = true
  Shapes = -> [Cylinder1255,Chamfer172]
FEATURE [Part::Cylinder] Cylinder1257  label="Cylinder1674"
  Angle = 360
  AttacherType = Attacher::AttachEngine3D
  Height = 10
  Placement = pos=(509,12,-11.5) rot=(0,1,0;1.5708rad)
  Radius = 0.9
FEATURE [Part::MultiFuse] Fusion248002170  label="Fusion248002318"
  Placement = pos=(0,0,-2) rot=(0,0,1;0rad)
  Refine = true
  Shapes = -> [Cylinder1257,Cylinder1254]
FEATURE [Part::MultiFuse] Fusion248002171  label="Fusion248002319"
  Placement = pos=(0,0,-2) rot=(0,0,1;0rad)
  Refine = true
  Shapes = -> [Fusion248002168,Fusion248002169]
FEATURE [Part::Cut] Cut014313  label="Cut014478"
  Base = -> Fusion248002163
  Refine = true
  Tool = -> Fusion248002171
FEATURE [Part::Cylinder] Cylinder1258  label="Cylinder1675"
  Angle = 360
  AttacherType = Attacher::AttachEngine3D
  Height = 10
  Placement = pos=(509,22,-11.5) rot=(0,1,0;1.5708rad)
  Radius = 0.9
FEATURE [Part::Cylinder] Cylinder1259  label="Cylinder1676"
  Angle = 360
  AttacherType = Attacher::AttachEngine3D
  Height = 10
  Placement = pos=(509,12,-11.5) rot=(0,1,0;1.5708rad)
  Radius = 0.9
FEATURE [Part::MultiFuse] Fusion248002172  label="Fusion248002320"
  Placement = pos=(0,3.5,-2) rot=(0,0,1;0rad)
  Refine = true
  Shapes = -> [Cylinder1259,Cylinder1258]
FEATURE [Part::Cut] Cut014315  label="Cut014479"
  Base = -> Cut014313
  Refine = true
  Tool = -> Fusion248002172
FEATURE [Part::Box] Box774  label="Cube936"
  AttacherType = Attacher::AttachEngine3D
  Height = 4
  Length = 4
  Placement = pos=(514,9,-11.5) rot=(0,0,1;0rad)
  Width = 50
FEATURE [Part::Cut] Cut014316  label="Cut014480"
  Base = -> Cut014315
  Refine = true
  Tool = -> Box774
FEATURE [Part::Cylinder] Cylinder1260  label="Cylinder1677"
  Angle = 360
  AttacherType = Attacher::AttachEngine3D
  Height = 10
  Placement = pos=(509,61,-10.5) rot=(0,1,0;1.5708rad)
  Radius = 0.9
FEATURE [Part::Box] Box775  label="Cube937"
  AttacherType = Attacher::AttachEngine3D
  Height = 5
  Length = 8
  Placement = pos=(510,55,-12.5) rot=(0,0,1;0rad)
  Width = 4
FEATURE [Part::Cut] Cut014317  label="Cut014481"
  Base = -> Cut014316
  Refine = true
  Tool = -> Box775
FEATURE [Part::Cylinder] Cylinder1261  label="Cylinder1678"
  Angle = 360
  AttacherType = Attacher::AttachEngine3D
  Height = 10
  Placement = pos=(509,58,-14.5) rot=(0,1,0;1.5708rad)
  Radius = 0.9
FEATURE [Part::MultiFuse] Fusion248002173  label="Fusion248002321"
  Placement = pos=(-1,0,0) rot=(0,0,1;0rad)
  Refine = true
  Shapes = -> [Cylinder1261,Cylinder1260]
FEATURE [Part::Cut] Cut014318  label="Cut014482"
  Base = -> Cut014317
  Refine = true
  Tool = -> Fusion248002173
FEATURE [Part::Cylinder] Cylinder1262  label="Cylinder1679"
  Angle = 360
  AttacherType = Attacher::AttachEngine3D
  Height = 10
  Placement = pos=(509,61,-10.5) rot=(0,1,0;1.5708rad)
  Radius = 1.1
FEATURE [Part::Cylinder] Cylinder1263  label="Cylinder1680"
  Angle = 360
  AttacherType = Attacher::AttachEngine3D
  Height = 10
  Placement = pos=(509,58,-14.5) rot=(0,1,0;1.5708rad)
  Radius = 1.1
FEATURE [Part::MultiFuse] Fusion248002174  label="Fusion248002322"
  Placement = pos=(-7,0,0) rot=(0,0,1;0rad)
  Refine = true
  Shapes = -> [Cylinder1263,Cylinder1262]
FEATURE [Part::Cylinder] Cylinder1264  label="Cylinder1681"
  Angle = 360
  AttacherType = Attacher::AttachEngine3D
  Height = 10
  Placement = pos=(509,64,-14.5) rot=(0,1,0;1.5708rad)
  Radius = 1.1
FEATURE [Part::Cylinder] Cylinder1265  label="Cylinder1682"
  Angle = 360
  AttacherType = Attacher::AttachEngine3D
  Height = 10
  Placement = pos=(509,61,-10.5) rot=(0,1,0;1.5708rad)
  Radius = 1.1
FEATURE [Part::MultiFuse] Fusion248002175  label="Fusion248002323"
  Placement = pos=(-7,48,0) rot=(0,0,1;0rad)
  Refine = true
  Shapes = -> [Cylinder1264,Cylinder1265]
FEATURE [Part::MultiFuse] Fusion248002176  label="Fusion248002324"
  Refine = true
  Shapes = -> [Fusion248002175,Fusion248002174]
FEATURE [Part::Cut] Cut014319  label="Cut014483"
  Base = -> Cut014309
  Refine = true
  Tool = -> Fusion248002176
FEATURE [Part::Box] Box776  label="Cube938"
  AttacherType = Attacher::AttachEngine3D
  Height = 4
  Length = 8
  Placement = pos=(511,19,-11.5) rot=(0,0,1;0rad)
  Width = 4
FEATURE [Part::Cut] Cut014320  label="Cut014484"
  Base = -> Cut014318
  Refine = true
  Tool = -> Box776
FEATURE [Part::Box] Box777  label="Cube939"
  AttacherType = Attacher::AttachEngine3D
  Height = 3
  Length = 10
  Placement = pos=(502,55,-11.5) rot=(0,0,1;0rad)
  Width = 4
FEATURE [Part::Box] Box778  label="Cube940"
  AttacherType = Attacher::AttachEngine3D
  Height = 3
  Length = 10
  Placement = pos=(502,111,-11.5) rot=(0,0,1;0rad)
  Width = 4
FEATURE [Part::MultiFuse] Fusion248002177  label="Fusion248002325"
  Placement = pos=(0,0,-1) rot=(0,0,1;0rad)
  Refine = true
  Shapes = -> [Box777,Box778]
FEATURE [Part::Fillet] Fillet007073
  Base = -> Fusion248002177
  Edges = 4 edges r=1: [Edge9,Edge10,Edge23,Edge24]
FEATURE [Part::Cut] Cut014321  label="cross-member-rear"
  Base = -> Cut014319
  Refine = true
  Tool = -> Fillet007073
FEATURE [Part::Fillet] Fillet007074
  Base = -> Cut014320
  Edges = 4 edges r=0.5: [Edge1,Edge3,Edge8,Edge21]
FEATURE [Part::Chamfer] Chamfer173  label="wing-rear-left-support"
  Base = -> Fillet007074
  Edges = 1 edges: [Edge64 r1=5 r2=0.99]
FEATURE [Part::Cylinder] Cylinder1266  label="Cylinder1683"
  Angle = 360
  AttacherType = Attacher::AttachEngine3D
  Height = 10
  Placement = pos=(503,0,0) rot=(0,1,0;1.5708rad)
  Radius = 0.9
FEATURE [Part::Cylinder] Cylinder1267  label="Cylinder1684"
  Angle = 360
  AttacherType = Attacher::AttachEngine3D
  Height = 10
  Placement = pos=(503,28,0) rot=(0,1,0;1.5708rad)
  Radius = 0.9
FEATURE [Part::MultiFuse] Fusion248002179  label="Fusion248002326"
  Placement = pos=(0,1.5,-20) rot=(0,0,1;0rad)
  Refine = true
  Shapes = -> [Cylinder1267,Cylinder1266]
FEATURE [Part::Box] Box779  label="Cube941"
  AttacherType = Attacher::AttachEngine3D
  Height = 6
  Length = 1
  Placement = pos=(507,-5,-23) rot=(0,0,1;0rad)
  Width = 42
FEATURE [Part::Cylinder] Cylinder1268  label="Cylinder1685"
  Angle = 360
  AttacherType = Attacher::AttachEngine3D
  Height = 2
  Placement = pos=(504,0,0) rot=(0,1,0;1.5708rad)
  Radius = 2.5
FEATURE [Part::Cylinder] Cylinder1269  label="Cylinder1686"
  Angle = 360
  AttacherType = Attacher::AttachEngine3D
  Height = 2
  Placement = pos=(504,28,0) rot=(0,1,0;1.5708rad)
  Radius = 2.5
FEATURE [Part::MultiFuse] Fusion248002180  label="Fusion248002327"
  Placement = pos=(2,1.5,-20) rot=(0,0,1;0rad)
  Refine = true
  Shapes = -> [Cylinder1269,Cylinder1268]
FEATURE [Part::MultiFuse] Fusion248002181  label="Fusion248002328"
  Refine = true
  Shapes = -> [Fusion248002180,Box779]
FEATURE [Part::Cut] Cut014323  label="wing-rear-right-flap-retainer"
  Base = -> Fusion248002181
  Placement = pos=(0,137.5,-5) rot=(0,0,1;0rad)
  Refine = true
  Tool = -> Fusion248002179
FEATURE [Part::Box] Box780  label="Cube942"
  AttacherType = Attacher::AttachEngine3D
  Height = 10
  Length = 2
  Placement = pos=(512,55,-16.5) rot=(0,0,1;0rad)
  Width = 8
FEATURE [Part::Fillet] Fillet007075
  Base = -> Box780
  Edges = 1 edges r=3: [Edge9]
FEATURE [Part::Box] Box781  label="Cube943"
  AttacherType = Attacher::AttachEngine3D
  Height = 10
  Length = 5
  Placement = pos=(514,8,-16.5) rot=(0,0,1;0rad)
  Width = 55
FEATURE [Part::MultiFuse] Fusion248002182  label="Fusion248002329"
  Refine = true
  Shapes = -> [Fillet007075,Box781]
FEATURE [Part::Cylinder] Cylinder1270  label="Cylinder1687"
  Angle = 360
  AttacherType = Attacher::AttachEngine3D
  Height = 10
  Placement = pos=(503,28,0) rot=(0,1,0;1.5708rad)
  Radius = 1.1
FEATURE [Part::Cylinder] Cylinder1271  label="Cylinder1688"
  Angle = 360
  AttacherType = Attacher::AttachEngine3D
  Height = 2
  Placement = pos=(511,28,0) rot=(0,1,0;1.5708rad)
  Radius = 2.2
FEATURE [Part::Chamfer] Chamfer174
  Base = -> Cylinder1271
  Edges = 1 edges r=1.99: [Edge3]
FEATURE [Part::MultiFuse] Fusion248002183  label="Fusion248002330"
  Placement = pos=(6,-16,-11.5) rot=(0,0,1;0rad)
  Refine = true
  Shapes = -> [Cylinder1270,Chamfer174]
FEATURE [Part::Cylinder] Cylinder1272  label="Cylinder1689"
  Angle = 360
  AttacherType = Attacher::AttachEngine3D
  Height = 10
  Placement = pos=(503,28,0) rot=(0,1,0;1.5708rad)
  Radius = 1.1
FEATURE [Part::Cylinder] Cylinder1273  label="Cylinder1690"
  Angle = 360
  AttacherType = Attacher::AttachEngine3D
  Height = 2
  Placement = pos=(511,28,0) rot=(0,1,0;1.5708rad)
  Radius = 2.2
FEATURE [Part::Chamfer] Chamfer175
  Base = -> Cylinder1273
  Edges = 1 edges r=1.99: [Edge3]
FEATURE [Part::MultiFuse] Fusion248002184  label="Fusion248002331"
  Placement = pos=(6,1,-11.5) rot=(0,0,1;0rad)
  Refine = true
  Shapes = -> [Cylinder1272,Chamfer175]
FEATURE [Part::MultiFuse] Fusion248002185  label="Fusion248002332"
  Placement = pos=(0,0,-2) rot=(0,0,1;0rad)
  Refine = true
  Shapes = -> [Fusion248002183,Fusion248002184]
FEATURE [Part::Cut] Cut014324  label="Cut014485"
  Base = -> Fusion248002182
  Refine = true
  Tool = -> Fusion248002185
FEATURE [Part::Cylinder] Cylinder1274  label="Cylinder1691"
  Angle = 360
  AttacherType = Attacher::AttachEngine3D
  Height = 10
  Placement = pos=(509,22,-11.5) rot=(0,1,0;1.5708rad)
  Radius = 0.9
FEATURE [Part::Cylinder] Cylinder1275  label="Cylinder1692"
  Angle = 360
  AttacherType = Attacher::AttachEngine3D
  Height = 10
  Placement = pos=(509,12,-11.5) rot=(0,1,0;1.5708rad)
  Radius = 0.9
FEATURE [Part::MultiFuse] Fusion248002186  label="Fusion248002333"
  Placement = pos=(0,3.5,-2) rot=(0,0,1;0rad)
  Refine = true
  Shapes = -> [Cylinder1275,Cylinder1274]
FEATURE [Part::Cut] Cut014325  label="Cut014486"
  Base = -> Cut014324
  Refine = true
  Tool = -> Fusion248002186
FEATURE [Part::Box] Box782  label="Cube944"
  AttacherType = Attacher::AttachEngine3D
  Height = 4
  Length = 4
  Placement = pos=(514,9,-11.5) rot=(0,0,1;0rad)
  Width = 50
FEATURE [Part::Cut] Cut014326  label="Cut014487"
  Base = -> Cut014325
  Refine = true
  Tool = -> Box782
FEATURE [Part::Cylinder] Cylinder1276  label="Cylinder1693"
  Angle = 360
  AttacherType = Attacher::AttachEngine3D
  Height = 10
  Placement = pos=(509,61,-10.5) rot=(0,1,0;1.5708rad)
  Radius = 0.9
FEATURE [Part::Box] Box783  label="Cube945"
  AttacherType = Attacher::AttachEngine3D
  Height = 5
  Length = 8
  Placement = pos=(510,55,-12.5) rot=(0,0,1;0rad)
  Width = 4
FEATURE [Part::Cut] Cut014327  label="Cut014488"
  Base = -> Cut014326
  Refine = true
  Tool = -> Box783
FEATURE [Part::Cylinder] Cylinder1277  label="Cylinder1694"
  Angle = 360
  AttacherType = Attacher::AttachEngine3D
  Height = 10
  Placement = pos=(509,58,-14.5) rot=(0,1,0;1.5708rad)
  Radius = 0.9
FEATURE [Part::MultiFuse] Fusion248002187  label="Fusion248002334"
  Placement = pos=(-1,0,0) rot=(0,0,1;0rad)
  Refine = true
  Shapes = -> [Cylinder1277,Cylinder1276]
FEATURE [Part::Cut] Cut014328  label="Cut014489"
  Base = -> Cut014327
  Refine = true
  Tool = -> Fusion248002187
FEATURE [Part::Box] Box784  label="Cube946"
  AttacherType = Attacher::AttachEngine3D
  Height = 4
  Length = 8
  Placement = pos=(511,19,-11.5) rot=(0,0,1;0rad)
  Width = 4
FEATURE [Part::Cut] Cut014329  label="Cut014490"
  Base = -> Cut014328
  Refine = true
  Tool = -> Box784
FEATURE [Part::Fillet] Fillet007076
  Base = -> Cut014329
  Edges = 4 edges r=0.5: [Edge1,Edge3,Edge8,Edge21]
FEATURE [Part::Chamfer] Chamfer176  label="wing-rear-left-support001"
  Base = -> Fillet007076
  Edges = 1 edges: [Edge64 r1=5 r2=0.99]
FEATURE [Part::Mirroring] Part__Mirroring115  label="wing-rear-right-support"
  Base = (0,0,0)
  Normal = (0,1,0)
  Placement = pos=(0,170,0) rot=(0,0,1;0rad)
  Source = -> Chamfer176
FEATURE [Part::Box] Box785  label="Cube947"
  AttacherType = Attacher::AttachEngine3D
  Height = 27
  Length = 2
  Placement = pos=(509,-7,-25) rot=(0,0,1;0rad)
  Width = 43.5
FEATURE [Part::Cylinder] Cylinder1278  label="Cylinder1695"
  Angle = 360
  AttacherType = Attacher::AttachEngine3D
  Height = 10
  Placement = pos=(503,0,0) rot=(0,1,0;1.5708rad)
  Radius = 1.1
FEATURE [Part::Cylinder] Cylinder1279  label="Cylinder1696"
  Angle = 360
  AttacherType = Attacher::AttachEngine3D
  Height = 10
  Placement = pos=(503,28,0) rot=(0,1,0;1.5708rad)
  Radius = 1.1
FEATURE [Part::MultiFuse] Fusion248002188  label="Fusion248002335"
  Placement = pos=(0,1.5,-20) rot=(0,0,1;0rad)
  Refine = true
  Shapes = -> [Cylinder1279,Cylinder1278]
FEATURE [Part::Box] Box786  label="Cube948"
  AttacherType = Attacher::AttachEngine3D
  Height = 8
  Length = 3
  Placement = pos=(511,8,-16.5) rot=(0,0,1;0rad)
  Width = 25
FEATURE [Part::Cut] Cut014330  label="Cut014491"
  Base = -> Box785
  Refine = true
  Tool = -> Fusion248002188
FEATURE [Part::Cylinder] Cylinder1280  label="Cylinder1697"
  Angle = 360
  AttacherType = Attacher::AttachEngine3D
  Height = 2
  Placement = pos=(503,0,0) rot=(0,1,0;1.5708rad)
  Radius = 2.2
FEATURE [Part::Cylinder] Cylinder1281  label="Cylinder1698"
  Angle = 360
  AttacherType = Attacher::AttachEngine3D
  Height = 2
  Placement = pos=(503,28,0) rot=(0,1,0;1.5708rad)
  Radius = 2.2
FEATURE [Part::MultiFuse] Fusion248002189  label="Fusion248002336"
  Placement = pos=(15,1.5,-20) rot=(0,0,1;0rad)
  Refine = true
  Shapes = -> [Cylinder1281,Cylinder1280]
FEATURE [Part::Chamfer] Chamfer177
  Base = -> Fusion248002189
  Edges = 2 edges r=1.99: [Edge3,Edge6]
  Placement = pos=(-9,0,0) rot=(0,0,1;0rad)
FEATURE [Part::Cut] Cut014331  label="Cut014492"
  Base = -> Cut014330
  Refine = true
  Tool = -> Chamfer177
FEATURE [Part::Fillet] Fillet007077
  Base = -> Cut014331
  Edges = 1 edges r=1.5: [Edge11]
FEATURE [Part::Chamfer] Chamfer178
  Base = -> Fillet007077
  Edges = 1 edges r=1.9: [Edge7]
  Placement = pos=(0,1.5,-5) rot=(0,0,1;0rad)
FEATURE [Part::Cylinder] Cylinder1282  label="Cylinder1699"
  Angle = 360
  AttacherType = Attacher::AttachEngine3D
  Height = 10
  Placement = pos=(509,29,-11.5) rot=(0,1,0;1.5708rad)
  Radius = 0.9
FEATURE [Part::Cylinder] Cylinder1283  label="Cylinder1700"
  Angle = 360
  AttacherType = Attacher::AttachEngine3D
  Height = 10
  Placement = pos=(509,12,-11.5) rot=(0,1,0;1.5708rad)
  Radius = 0.9
FEATURE [Part::MultiFuse] Fusion248002190  label="Fusion248002337"
  Placement = pos=(0,0,-2) rot=(0,0,1;0rad)
  Refine = true
  Shapes = -> [Cylinder1283,Cylinder1282]
FEATURE [Part::MultiFuse] Fusion248002191  label="Fusion248002338"
  Refine = true
  Shapes = -> [Box786,Chamfer178]
FEATURE [Part::Cut] Cut014332  label="wing-rear-left-rigid-flap001"
  Base = -> Fusion248002191
  Refine = true
  Tool = -> Fusion248002190
FEATURE [Part::Mirroring] Part__Mirroring116  label="wing-rear-right-rigid-flap"
  Base = (0,0,0)
  Normal = (0,1,0)
  Placement = pos=(0,170,0) rot=(0,0,1;0rad)
  Source = -> Cut014332
FEATURE [Part::Box] Box787  label="wing-rear-right-RUBBER"
  AttacherType = Attacher::AttachEngine3D
  Height = 40
  Length = 1
  Placement = pos=(508,130.5,-62) rot=(0,0,1;0rad)
  Width = 45
FEATURE [Part::MultiFuse] Fusion248002192  label="Fusion248002339"
  Refine = true
  Shapes = -> [Box773,Chamfer170]
FEATURE [Part::Cut] Cut014333  label="wing-rear-left-rigid-flap"
  Base = -> Fusion248002192
  Refine = true
  Tool = -> Fusion248002170
FEATURE [Part::Cylinder] Cylinder1284  label="Cylinder1701"
  Angle = 360
  AttacherType = Attacher::AttachEngine3D
  Height = 22
  Placement = pos=(384,85,5) rot=(0,1,0;1.5708rad)
  Radius = 18.7
FEATURE [Part::Cylinder] Cylinder1285  label="Cylinder1702"
  Angle = 360
  AttacherType = Attacher::AttachEngine3D
  Height = 31
  Placement = pos=(353,85,5) rot=(0,1,0;1.5708rad)
  Radius = 17.5
FEATURE [Part::Cylinder] Cylinder1286  label="Cylinder1703"
  Angle = 360
  AttacherType = Attacher::AttachEngine3D
  Height = 6
  Placement = pos=(406,85,12) rot=(0,1,0;1.5708rad)
  Radius = 7
FEATURE [Part::Cylinder] Cylinder1287  label="Cylinder1704"
  Angle = 360
  AttacherType = Attacher::AttachEngine3D
  Height = 170
  Placement = pos=(412,85,12) rot=(0,1,0;1.5708rad)
  Radius = 4
FEATURE [Part::MultiFuse] Fusion394  label="kipper-spindle-motor"
  Placement = pos=(853.089,170,27.8722) rot=(-0.043619,0,0.999048;3.14159rad)
  Refine = true
  Shapes = -> [Cylinder1286,Cylinder1287,Cylinder1284,Cylinder1285]
FEATURE [Part::Cylinder] Cylinder1209  label="Cylinder1705"
  Angle = 360
  AttacherType = Attacher::AttachEngine3D
  Height = 170
  Placement = pos=(293,170,18) rot=(1,0,0;1.5708rad)
  Radius = 1
FEATURE [App::DocumentObjectGroup] Group016  label="normal"
  Group = -> [Part__Mirroring099,Part__Mirroring100,Part__Mirroring101,Cut014074,Cut014061,Fillet365,Cut014060,Fillet366,Fillet346,Fillet344,Fusion500]
FEATURE [Part::Mirroring] Part__Mirroring117  label="central-axle-right-upper-bar001"
  Base = (0,0,0)
  Normal = (0,1,0)
  Placement = pos=(12.7373,170,-100.115) rot=(0,-1,0;0.331613rad)
FEATURE [Part::MultiFuse] Fusion248002193  label="central-axle001"
  Placement = pos=(2.5,0,15) rot=(0,0,1;0rad)
  Refine = true
FEATURE [Part::Cut] Cut014334  label="central-axle-left-baloon-support001"
  Placement = pos=(2.5,0,15) rot=(0,0,1;0rad)
  Refine = true
FEATURE [Part::Cut] Cut014335  label="central-axle-left-upper-bar001"
  Placement = pos=(14.0024,0,-10.4562) rot=(0,1,0;0.008727rad)
  Refine = true
FEATURE [Part::Mirroring] Part__Mirroring118  label="central-axle-right-baloon-support001"
  Base = (0,0,0)
  Normal = (0,1,0)
  Placement = pos=(2.5,170,15) rot=(0,0,1;0rad)
FEATURE [Part::Mirroring] Part__Mirroring119  label="central-axle-right-upper-bar-support001"
  Base = (0,0,0)
  Normal = (0,1,0)
  Placement = pos=(2.5,170,15) rot=(0,0,1;0rad)
FEATURE [Part::Fillet] Fillet007078  label="central-axle-left_lower-bar001"
  Edges = 6 edges r=0.75: [Edge10,Edge11,Edge12,Edge13,Edge24,Edge25]
  Placement = pos=(-2.12729,4,7.5764) rot=(0,1,0;0.008727rad)
FEATURE [Part::Fillet] Fillet007079  label="central-axle-right-lower-bar001"
  Edges = 6 edges r=0.75: [Edge10,Edge11,Edge12,Edge13,Edge24,Edge25]
  Placement = pos=(-2.12729,68,7.5764) rot=(0,1,0;0.008727rad)
FEATURE [Part::Cut] Cut014336  label="central-axle-left-upper-bar-support001"
  Placement = pos=(2.5,0,15) rot=(0,0,1;0rad)
  Refine = true
FEATURE [App::DocumentObjectGroup] Group015  label="lifted"
  Group = -> [Fillet353,Fillet352,Part__Mirroring117,Fusion248002193,Cut014334,Cut014335,Part__Mirroring118,Part__Mirroring119,Fillet007078,Fillet007079,Cut014336]
FEATURE [App::DocumentObjectGroup] Group004  label="central-axle-suspension"
  Group = -> [Cut014085,Cut014089,Cut014090,Part__Mirroring102,Part__Mirroring103,Part__Mirroring104,Group015,Group016]
FEATURE [Part::Box] Box788  label="Cube949"
  AttacherType = Attacher::AttachEngine3D
  Height = 2
  Length = 20
  Placement = pos=(493.5,55,-20) rot=(0,0,1;0rad)
  Width = 60
FEATURE [Part::Box] Box789  label="Cube950"
  AttacherType = Attacher::AttachEngine3D
  Height = 3.4
  Length = 20
  Placement = pos=(493.5,65,-20) rot=(0,0,1;0rad)
  Width = 40
FEATURE [Part::MultiFuse] Fusion248002194  label="Fusion248002340"
  Refine = true
  Shapes = -> [Box788,Box789]
FEATURE [Part::Cylinder] Cylinder1288  label="Cylinder1706"
  Angle = 360
  AttacherType = Attacher::AttachEngine3D
  Height = 10
  Placement = pos=(499,110,-21) rot=(0,0,1;0rad)
  Radius = 1.25
FEATURE [Part::Cylinder] Cylinder1289  label="Cylinder1707"
  Angle = 360
  AttacherType = Attacher::AttachEngine3D
  Height = 10
  Placement = pos=(499,60,-21) rot=(0,0,1;0rad)
  Radius = 1.25
FEATURE [Part::MultiFuse] Fusion248002195  label="Fusion248002341"
  Refine = true
  Shapes = -> [Cylinder1288,Cylinder1289]
FEATURE [Part::Cut] Cut014337  label="rear-bumper-holder-HOLES"
  Base = -> Fusion248002194
  Refine = true
  Tool = -> Fusion248002195
FEATURE [App::DocumentObjectGroup] Group012  label="Tools"
  Group = -> [Cut605,Fusion470,Cut014337]
FEATURE [Part::Cylinder] Cylinder1290  label="Cylinder1708"
  Angle = 360
  AttacherType = Attacher::AttachEngine3D
  Height = 15
  Placement = pos=(209.5,30,-8) rot=(-1,0,0;1.5708rad)
  Radius = 1.6
FEATURE [Part::Cylinder] Cylinder1291  label="Cylinder1709"
  Angle = 360
  AttacherType = Attacher::AttachEngine3D
  Height = 15
  Placement = pos=(242.5,30,-8) rot=(-1,0,0;1.5708rad)
  Radius = 1.6
FEATURE [Part::MultiFuse] Fusion248002196  label="Fusion248002342"
  Placement = pos=(0,22,0) rot=(0,0,1;0rad)
  Refine = true
  Shapes = -> [Cylinder1291,Cylinder1290]
FEATURE [Part::Cylinder] Cylinder1292  label="Cylinder1710"
  Angle = 360
  AttacherType = Attacher::AttachEngine3D
  Height = 6
  Placement = pos=(220.5,72.37,-21.47) rot=(0,1,0;1.5708rad)
  Radius = 3
FEATURE [Part::Cylinder] Cylinder1293  label="Cylinder1711"
  Angle = 360
  AttacherType = Attacher::AttachEngine3D
  Height = 12
  Placement = pos=(208.5,72.37,-21.47) rot=(0,1,0;1.5708rad)
  Radius = 1.5
FEATURE [Part::Cylinder] Cylinder1294  label="Cylinder1712"
  Angle = 360
  AttacherType = Attacher::AttachEngine3D
  Height = 1
  Placement = pos=(225.5,72.37,-21.47) rot=(0,1,0;1.5708rad)
  Radius = 5
FEATURE [Part::Cylinder] Cylinder1295  label="Cylinder1713"
  Angle = 360
  AttacherType = Attacher::AttachEngine3D
  Height = 4
  Placement = pos=(208.5,72.37,-21.47) rot=(0,1,0;1.5708rad)
  Radius = 4
FEATURE [Part::Fillet] Fillet007080
  Base = -> Cut014254
  Edges = 2 edges r=8: [Edge53,Edge57]
FEATURE [Part::Cut] Cut014338  label="Cut014493"
  Base = -> Fillet007080
  Refine = true
  Tool = -> Fusion248002093
FEATURE [Part::Cut] Cut014339  label="battery-box-01_"
  Base = -> Cut014338
  Refine = true
  Tool = -> Fusion248002132
FEATURE [App::DocumentObjectGroup] Group017  label="front"
  Group = -> [Cut700]
FEATURE [App::DocumentObjectGroup] Group019  label="others"
  Group = -> [Chamfer162,Cut014290,Fillet007067,Part__Mirroring114]
FEATURE [Part::Box] Box790  label="Cube951"
  AttacherType = Attacher::AttachEngine3D
  Height = 30
  Length = 29
  Width = 13
FEATURE [Part::Box] Box791  label="Cube952"
  AttacherType = Attacher::AttachEngine3D
  Height = 4
  Length = 7
  Placement = pos=(-7,3.5,1) rot=(0,0,1;0rad)
  Width = 6
FEATURE [Part::Box] Box792  label="Cube953"
  AttacherType = Attacher::AttachEngine3D
  Height = 3.3
  Length = 40
  Placement = pos=(-5.5,0,19.5) rot=(0,0,1;0rad)
  Width = 13
FEATURE [Part::Cylinder] Cylinder1296  label="Cylinder1714"
  Angle = 360
  AttacherType = Attacher::AttachEngine3D
  Height = 6
  Placement = pos=(6,6.5,30) rot=(0,0,1;0rad)
  Radius = 4
FEATURE [Part::Box] Box793  label="Cube954"
  AttacherType = Attacher::AttachEngine3D
  Height = 1.5
  Length = 14
  Placement = pos=(-8,3.5,34.5) rot=(0,0,1;0rad)
  Width = 6
FEATURE [Part::Fillet] Fillet007081
  Base = -> Box793
  Edges = 4 edges r=2: [Edge1,Edge3,Edge5,Edge7]
FEATURE [Part::Cylinder] Cylinder1297  label="Cylinder1715"
  Angle = 360
  AttacherType = Attacher::AttachEngine3D
  Height = 10
  Radius = 1
FEATURE [Part::Cylinder] Cylinder1298  label="Cylinder1716"
  Angle = 360
  AttacherType = Attacher::AttachEngine3D
  Height = 10
  Placement = pos=(35.3,0,0) rot=(0,0,1;0rad)
  Radius = 1
FEATURE [Part::MultiFuse] Fusion248002198  label="Fusion248002343"
  Placement = pos=(-3.15,6.5,13) rot=(0,0,1;0rad)
  Refine = true
  Shapes = -> [Cylinder1297,Cylinder1298]
FEATURE [Part::Cylinder] Cylinder1305  label="Cylinder1717"
  Angle = 360
  AttacherType = Attacher::AttachEngine3D
  Height = 10
  Placement = pos=(-6,6.5,31) rot=(0,0,1;0rad)
  Radius = 1
FEATURE [Part::Cylinder] Cylinder1306  label="Cylinder1718"
  Angle = 360
  AttacherType = Attacher::AttachEngine3D
  Height = 10
  Placement = pos=(-3.5,6.5,31) rot=(0,0,1;0rad)
  Radius = 1
FEATURE [Part::Cylinder] Cylinder1307  label="Cylinder1719"
  Angle = 360
  AttacherType = Attacher::AttachEngine3D
  Height = 10
  Placement = pos=(-1,6.5,31) rot=(0,0,1;0rad)
  Radius = 1
FEATURE [Part::MultiFuse] Fusion248002199  label="Fusion248002344"
  Refine = true
  Shapes = -> [Cylinder1305,Cylinder1306,Cylinder1307]
FEATURE [Part::Cut] Cut014340  label="Cut014494"
  Base = -> Fillet007081
  Refine = true
  Tool = -> Fusion248002199
FEATURE [Part::MultiFuse] Fusion248002200  label="Fusion248002345"
  Placement = pos=(12.5,0.5,0) rot=(0,0,1;1.5708rad)
  Refine = true
  Shapes = -> [Cut014340,Cylinder1296]
FEATURE [Part::MultiFuse] Fusion248002201  label="Fusion248002346"
  Refine = true
  Shapes = -> [Box790,Box792,Box791]
FEATURE [Part::Cut] Cut014341  label="Cut014495"
  Base = -> Fusion248002201
  Refine = true
  Tool = -> Fusion248002198
FEATURE [Part::MultiFuse] Fusion248002202  label="hitec-hs85bb-90deg-001"
  Placement = pos=(219,41.5,2.5) rot=(0.707107,-0.707107,0;3.14159rad)
  Refine = true
  Shapes = -> [Cut014341,Fusion248002200]
FEATURE [Part::Box] Box794  label="Cube955"
  AttacherType = Attacher::AttachEngine3D
  Height = 30
  Length = 29
  Width = 13
FEATURE [Part::Box] Box795  label="Cube956"
  AttacherType = Attacher::AttachEngine3D
  Height = 4
  Length = 7
  Placement = pos=(-7,3.5,1) rot=(0,0,1;0rad)
  Width = 6
FEATURE [Part::Box] Box796  label="Cube957"
  AttacherType = Attacher::AttachEngine3D
  Height = 3.3
  Length = 40
  Placement = pos=(-5.5,0,19.5) rot=(0,0,1;0rad)
  Width = 13
FEATURE [Part::Cylinder] Cylinder1308  label="Cylinder1720"
  Angle = 360
  AttacherType = Attacher::AttachEngine3D
  Height = 6
  Placement = pos=(6,6.5,30) rot=(0,0,1;0rad)
  Radius = 4
FEATURE [Part::Box] Box797  label="Cube958"
  AttacherType = Attacher::AttachEngine3D
  Height = 1.5
  Length = 14
  Placement = pos=(-8,3.5,34.5) rot=(0,0,1;0rad)
  Width = 6
FEATURE [Part::Fillet] Fillet007082
  Base = -> Box797
  Edges = 4 edges r=2: [Edge1,Edge3,Edge5,Edge7]
FEATURE [Part::Cylinder] Cylinder1309  label="Cylinder1721"
  Angle = 360
  AttacherType = Attacher::AttachEngine3D
  Height = 10
  Radius = 1
FEATURE [Part::Cylinder] Cylinder1310  label="Cylinder1722"
  Angle = 360
  AttacherType = Attacher::AttachEngine3D
  Height = 10
  Placement = pos=(35.3,0,0) rot=(0,0,1;0rad)
  Radius = 1
FEATURE [Part::MultiFuse] Fusion248002203  label="Fusion248002347"
  Placement = pos=(-3.15,6.5,13) rot=(0,0,1;0rad)
  Refine = true
  Shapes = -> [Cylinder1309,Cylinder1310]
FEATURE [Part::Cylinder] Cylinder1311  label="Cylinder1723"
  Angle = 360
  AttacherType = Attacher::AttachEngine3D
  Height = 10
  Placement = pos=(-6,6.5,31) rot=(0,0,1;0rad)
  Radius = 1
FEATURE [Part::Cylinder] Cylinder1312  label="Cylinder1724"
  Angle = 360
  AttacherType = Attacher::AttachEngine3D
  Height = 10
  Placement = pos=(-3.5,6.5,31) rot=(0,0,1;0rad)
  Radius = 1
FEATURE [Part::Cylinder] Cylinder1313  label="Cylinder1725"
  Angle = 360
  AttacherType = Attacher::AttachEngine3D
  Height = 10
  Placement = pos=(-1,6.5,31) rot=(0,0,1;0rad)
  Radius = 1
FEATURE [Part::MultiFuse] Fusion248002204  label="Fusion248002348"
  Refine = true
  Shapes = -> [Cylinder1311,Cylinder1312,Cylinder1313]
FEATURE [Part::Cut] Cut014342  label="Cut014496"
  Base = -> Fillet007082
  Refine = true
  Tool = -> Fusion248002204
FEATURE [Part::MultiFuse] Fusion248002205  label="Fusion248002349"
  Placement = pos=(12.5,0.5,0) rot=(0,0,1;1.5708rad)
  Refine = true
  Shapes = -> [Cut014342,Cylinder1308]
FEATURE [Part::MultiFuse] Fusion248002206  label="Fusion248002350"
  Refine = true
  Shapes = -> [Box794,Box796,Box795]
FEATURE [Part::Cut] Cut014343  label="Cut014497"
  Base = -> Fusion248002206
  Refine = true
  Tool = -> Fusion248002203
FEATURE [Part::MultiFuse] Fusion248002207  label="hitec-hs85bb-90deg-002"
  Placement = pos=(226,12.5,2.5) rot=(0.707107,0.707107,0;3.14159rad)
  Refine = true
  Shapes = -> [Cut014343,Fusion248002205]
FEATURE [Part::MultiFuse] Fusion248002208  label="transfer-case-selector-arm"
  Refine = true
  Shapes = -> [Cylinder1292,Cylinder1293,Cylinder1294,Cylinder1295]
FEATURE [App::DocumentObjectGroup] Group013  label="transmission"
  Group = -> [Fusion512,Fusion513,Fusion536,Fusion670,Fusion514,Fusion248002049,Group006,Fusion248002208,Fusion248002196]
FEATURE [Part::Box] Box798  label="Cube959"
  AttacherType = Attacher::AttachEngine3D
  Height = 12
  Length = 34
  Placement = pos=(205.5,33.5,-36) rot=(0,0,1;0rad)
  Width = 11
FEATURE [Part::Cylinder] Cylinder1314  label="Cylinder1726"
  Angle = 360
  AttacherType = Attacher::AttachEngine3D
  Height = 3
  Placement = pos=(212.5,9.5,-23) rot=(0,0,1;0rad)
  Radius = 2
FEATURE [Part::Cylinder] Cylinder1315  label="Cylinder1727"
  Angle = 360
  AttacherType = Attacher::AttachEngine3D
  Height = 3
  Placement = pos=(232.5,9.5,-23) rot=(0,0,1;0rad)
  Radius = 2
FEATURE [Part::Cylinder] Cylinder1316  label="Cylinder1728"
  Angle = 360
  AttacherType = Attacher::AttachEngine3D
  Height = 3
  Placement = pos=(212.5,44.5,-23) rot=(0,0,1;0rad)
  Radius = 2
FEATURE [Part::Cylinder] Cylinder1317  label="Cylinder1729"
  Angle = 360
  AttacherType = Attacher::AttachEngine3D
  Height = 3
  Placement = pos=(232.5,44.5,-23) rot=(0,0,1;0rad)
  Radius = 2
FEATURE [Part::MultiFuse] Fusion248002209  label="hitec-hs85bb-90deg-screws"
  Refine = true
  Shapes = -> [Cylinder1314,Cylinder1315,Cylinder1317,Cylinder1316]
FEATURE [Part::Box] Box799  label="Cube960"
  AttacherType = Attacher::AttachEngine3D
  Height = 12
  Length = 45
  Placement = pos=(200,33.5,-36) rot=(0,0,1;0rad)
  Width = 20
FEATURE [Part::Cut] Cut014344  label="Cut014498"
  Base = -> Box799
  Placement = pos=(0,0,2) rot=(0,0,1;0rad)
  Refine = true
  Tool = -> Box798
FEATURE [Part::Cylinder] Cylinder1318  label="Cylinder1730"
  Angle = 360
  AttacherType = Attacher::AttachEngine3D
  Height = 20
  Placement = pos=(203.5,44.5,-42) rot=(0,0,1;0rad)
  Radius = 1.6
FEATURE [Part::Cylinder] Cylinder1319  label="Cylinder1731"
  Angle = 360
  AttacherType = Attacher::AttachEngine3D
  Height = 20
  Placement = pos=(241.5,44.5,-42) rot=(0,0,1;0rad)
  Radius = 1.6
FEATURE [Part::Box] Box800  label="Cube961"
  AttacherType = Attacher::AttachEngine3D
  Height = 2
  Length = 34
  Placement = pos=(205.5,37,-24) rot=(0,0,1;0rad)
  Width = 11
FEATURE [Part::Cut] Cut014345  label="Cut014499"
  Base = -> Cut014344
  Refine = true
  Tool = -> Box800
FEATURE [Part::Cylinder] Cylinder1320  label="Cylinder1732"
  Angle = 360
  AttacherType = Attacher::AttachEngine3D
  Height = 7
  Placement = pos=(203.5,44.5,-42) rot=(1,0,0;1.5708rad)
  Radius = 1.1
FEATURE [Part::MultiFuse] Fusion248002210  label="Fusion248002351"
  Refine = true
  Shapes = -> [Cylinder1318,Cylinder1319]
FEATURE [Part::Cut] Cut014346  label="Cut014500"
  Base = -> Cut014345
  Refine = true
  Tool = -> Fusion248002210
FEATURE [Part::Cylinder] Cylinder1321  label="Cylinder1733"
  Angle = 360
  AttacherType = Attacher::AttachEngine3D
  Height = 7
  Placement = pos=(203.5,42.5,-42) rot=(1,0,0;1.5708rad)
  Radius = 0.6
FEATURE [Part::MultiFuse] Fusion248002211  label="Fusion248002352"
  Placement = pos=(17.75,9,13) rot=(0,0,1;0rad)
  Refine = true
  Shapes = -> [Cylinder1320,Cylinder1321]
FEATURE [Part::Cylinder] Cylinder1322  label="Cylinder1734"
  Angle = 360
  AttacherType = Attacher::AttachEngine3D
  Height = 7
  Placement = pos=(203.5,44.5,-42) rot=(1,0,0;1.5708rad)
  Radius = 1.1
FEATURE [Part::Cylinder] Cylinder1323  label="Cylinder1735"
  Angle = 360
  AttacherType = Attacher::AttachEngine3D
  Height = 7
  Placement = pos=(203.5,42.5,-42) rot=(1,0,0;1.5708rad)
  Radius = 0.6
FEATURE [Part::MultiFuse] Fusion248002212  label="Fusion248002353"
  Placement = pos=(20.25,9,13) rot=(0,0,1;0rad)
  Refine = true
  Shapes = -> [Cylinder1322,Cylinder1323]
FEATURE [Part::MultiFuse] Fusion248002213  label="Fusion248002354"
  Refine = true
  Shapes = -> [Fusion248002212,Fusion248002211]
FEATURE [Part::Cut] Cut014347  label="axles-diff-lock-wires-holder-TEMP"
  Base = -> Cut014346
  Refine = true
  Tool = -> Fusion248002213
FEATURE [App::DocumentObjectGroup] Group011  label="to-be-removed"
  Group = -> [Cut534,Cut604,Part__Mirroring098,Cut014104,Cut697,Chamfer108,Chamfer147,Cut014234,Cut014239,Cut014240,Cut014347]
FEATURE [Part::Cylinder] Cylinder1324  label="Cylinder1736"
  Angle = 360
  AttacherType = Attacher::AttachEngine3D
  Height = 7
  Placement = pos=(203.5,44.5,-42) rot=(1,0,0;1.5708rad)
  Radius = 1.1
FEATURE [Part::Cylinder] Cylinder1325  label="Cylinder1737"
  Angle = 360
  AttacherType = Attacher::AttachEngine3D
  Height = 7
  Placement = pos=(203.5,42.5,-42) rot=(1,0,0;1.5708rad)
  Radius = 0.6
FEATURE [Part::MultiFuse] Fusion248002214  label="Fusion248002355"
  Placement = pos=(17.75,9,13) rot=(0,0,1;0rad)
  Refine = true
  Shapes = -> [Cylinder1324,Cylinder1325]
FEATURE [Part::Cylinder] Cylinder1326  label="Cylinder1738"
  Angle = 360
  AttacherType = Attacher::AttachEngine3D
  Height = 7
  Placement = pos=(203.5,44.5,-42) rot=(1,0,0;1.5708rad)
  Radius = 1.1
FEATURE [Part::Cylinder] Cylinder1327  label="Cylinder1739"
  Angle = 360
  AttacherType = Attacher::AttachEngine3D
  Height = 7
  Placement = pos=(203.5,42.5,-42) rot=(1,0,0;1.5708rad)
  Radius = 0.6
FEATURE [Part::MultiFuse] Fusion248002215  label="Fusion248002356"
  Placement = pos=(20.25,9,13) rot=(0,0,1;0rad)
  Refine = true
  Shapes = -> [Cylinder1326,Cylinder1327]
FEATURE [Part::MultiFuse] Fusion248002216  label="Fusion248002357"
  Refine = true
  Shapes = -> [Fusion248002215,Fusion248002214]
FEATURE [Part::Box] Box805  label="Cube966"
  AttacherType = Attacher::AttachEngine3D
  Height = 10
  Length = 7
  Placement = pos=(219,44.5,-32) rot=(0,0,1;0rad)
  Width = 9
FEATURE [Part::Cylinder] Cylinder1328  label="Cylinder1740"
  Angle = 360
  AttacherType = Attacher::AttachEngine3D
  Height = 3
  Placement = pos=(212.5,9.5,-23) rot=(0,0,1;0rad)
  Radius = 2.2
FEATURE [Part::Cylinder] Cylinder1329  label="Cylinder1741"
  Angle = 360
  AttacherType = Attacher::AttachEngine3D
  Height = 3
  Placement = pos=(232.5,9.5,-23) rot=(0,0,1;0rad)
  Radius = 2.2
FEATURE [Part::Cylinder] Cylinder1330  label="Cylinder1742"
  Angle = 360
  AttacherType = Attacher::AttachEngine3D
  Height = 3
  Placement = pos=(212.5,44.5,-23) rot=(0,0,1;0rad)
  Radius = 2.2
FEATURE [Part::Cylinder] Cylinder1331  label="Cylinder1743"
  Angle = 360
  AttacherType = Attacher::AttachEngine3D
  Height = 3
  Placement = pos=(232.5,44.5,-23) rot=(0,0,1;0rad)
  Radius = 2.2
FEATURE [Part::MultiFuse] Fusion248002218  label="hitec-hs85bb-90deg-screws001"
  Refine = true
  Shapes = -> [Cylinder1328,Cylinder1329,Cylinder1331,Cylinder1330]
FEATURE [Part::Box] Box806  label="Cube967"
  AttacherType = Attacher::AttachEngine3D
  Height = 15.5
  Length = 14
  Placement = pos=(215.5,42,-37.5) rot=(0,0,1;0rad)
  Width = 2.5
FEATURE [Part::Box] Box807  label="Cube968"
  AttacherType = Attacher::AttachEngine3D
  Height = 15.5
  Length = 34
  Placement = pos=(205.5,12,-37.5) rot=(0,0,1;0rad)
  Width = 30
FEATURE [Part::MultiFuse] Fusion248002219  label="Fusion248002358"
  Refine = true
  Shapes = -> [Box806,Box807]
FEATURE [Part::Box] Box808  label="Cube969"
  AttacherType = Attacher::AttachEngine3D
  Height = 14.5
  Length = 34
  Placement = pos=(0,-1,2) rot=(0,0,1;0rad)
  Width = 14
FEATURE [Part::Chamfer] Chamfer179
  Base = -> Box808
  Edges = 1 edges r=5: [Edge10]
  Placement = pos=(205.5,7,-39.5) rot=(0,0,1;0rad)
FEATURE [Part::MultiFuse] Fusion248002220  label="Fusion248002359"
  Refine = true
  Shapes = -> [Chamfer179,Fusion248002219]
FEATURE [Part::Box] Box809  label="Cube970"
  AttacherType = Attacher::AttachEngine3D
  Height = 10.5
  Length = 8
  Placement = pos=(218.5,44.5,-32.5) rot=(0,0,1;0rad)
  Width = 9
FEATURE [Part::MultiFuse] Fusion248002221  label="Fusion248002360"
  Refine = true
  Shapes = -> [Fusion248002220,Box809]
FEATURE [Part::Box] Box810  label="Cube971"
  AttacherType = Attacher::AttachEngine3D
  Height = 4
  Length = 33
  Placement = pos=(206,48,-26) rot=(0,0,1;0rad)
  Width = 5.5
FEATURE [Part::Cylinder] Cylinder1332  label="Cylinder1744"
  Angle = 360
  AttacherType = Attacher::AttachEngine3D
  Height = 2
  Placement = pos=(235.5,50.75,-27) rot=(0,0,1;0rad)
  Radius = 2.1
FEATURE [Part::Cylinder] Cylinder1333  label="Cylinder1745"
  Angle = 360
  AttacherType = Attacher::AttachEngine3D
  Height = 2
  Placement = pos=(229.5,50.75,-27) rot=(0,0,1;0rad)
  Radius = 2.1
FEATURE [Part::Cylinder] Cylinder1334  label="Cylinder1746"
  Angle = 360
  AttacherType = Attacher::AttachEngine3D
  Height = 2
  Placement = pos=(215.5,50.75,-27) rot=(0,0,1;0rad)
  Radius = 2.1
FEATURE [Part::Cylinder] Cylinder1335  label="Cylinder1747"
  Angle = 360
  AttacherType = Attacher::AttachEngine3D
  Height = 2
  Placement = pos=(209.5,50.75,-27) rot=(0,0,1;0rad)
  Radius = 2.1
FEATURE [Part::MultiFuse] Fusion248002222  label="Fusion248002361"
  Refine = true
  Shapes = -> [Cylinder1332,Cylinder1333,Cylinder1335,Cylinder1334]
FEATURE [Part::Cylinder] Cylinder1336  label="Cylinder1748"
  Angle = 360
  AttacherType = Attacher::AttachEngine3D
  Height = 5
  Placement = pos=(235.5,50.75,-27) rot=(0,0,1;0rad)
  Radius = 1.2
FEATURE [Part::Cylinder] Cylinder1337  label="Cylinder1749"
  Angle = 360
  AttacherType = Attacher::AttachEngine3D
  Height = 5
  Placement = pos=(229.5,50.75,-27) rot=(0,0,1;0rad)
  Radius = 1.2
FEATURE [Part::Cylinder] Cylinder1338  label="Cylinder1750"
  Angle = 360
  AttacherType = Attacher::AttachEngine3D
  Height = 5
  Placement = pos=(215.5,50.75,-27) rot=(0,0,1;0rad)
  Radius = 1.2
FEATURE [Part::Cylinder] Cylinder1339  label="Cylinder1751"
  Angle = 360
  AttacherType = Attacher::AttachEngine3D
  Height = 5
  Placement = pos=(209.5,50.75,-27) rot=(0,0,1;0rad)
  Radius = 1.2
FEATURE [Part::MultiFuse] Fusion248002223  label="Fusion248002362"
  Refine = true
  Shapes = -> [Cylinder1336,Cylinder1337,Cylinder1339,Cylinder1338]
FEATURE [Part::MultiFuse] Fusion248002224  label="Fusion248002363"
  Refine = true
  Shapes = -> [Fusion248002222,Fusion248002223]
FEATURE [Part::MultiFuse] Fusion248002225  label="Fusion248002364"
  Refine = true
  Shapes = -> [Box810,Box805]
FEATURE [Part::Cut] Cut014349
  Base = -> Fusion248002225
  Refine = true
  Tool = -> Fusion248002216
FEATURE [Part::Cut] Cut014350  label="axles-diff-lock-wires-holder"
  Base = -> Cut014349
  Refine = true
  Tool = -> Fusion248002224
FEATURE [Part::Cylinder] Cylinder1340  label="Cylinder1752"
  Angle = 360
  AttacherType = Attacher::AttachEngine3D
  Height = 10
  Placement = pos=(235.5,50.75,-27) rot=(0,0,1;0rad)
  Radius = 0.9
FEATURE [Part::Cylinder] Cylinder1341  label="Cylinder1753"
  Angle = 360
  AttacherType = Attacher::AttachEngine3D
  Height = 10
  Placement = pos=(229.5,50.75,-27) rot=(0,0,1;0rad)
  Radius = 0.9
FEATURE [Part::Cylinder] Cylinder1342  label="Cylinder1754"
  Angle = 360
  AttacherType = Attacher::AttachEngine3D
  Height = 10
  Placement = pos=(215.5,50.75,-27) rot=(0,0,1;0rad)
  Radius = 0.9
FEATURE [Part::Cylinder] Cylinder1343  label="Cylinder1755"
  Angle = 360
  AttacherType = Attacher::AttachEngine3D
  Height = 10
  Placement = pos=(209.5,50.75,-27) rot=(0,0,1;0rad)
  Radius = 0.9
FEATURE [Part::MultiFuse] Fusion248002226  label="Fusion248002365"
  Placement = pos=(0,0,5) rot=(0,0,1;0rad)
  Refine = true
  Shapes = -> [Cylinder1340,Cylinder1341,Cylinder1343,Cylinder1342]
FEATURE [Part::Cut] Cut014351  label="battery-box-01"
  Base = -> Cut014339
  Refine = true
  Tool = -> Fusion248002226
FEATURE [Part::Cylinder] Cylinder1344  label="Cylinder1756"
  Angle = 360
  AttacherType = Attacher::AttachEngine3D
  Height = 15
  Placement = pos=(203.5,45.5,-30) rot=(0,0,1;0rad)
  Radius = 0.9
FEATURE [Part::Cylinder] Cylinder1345  label="Cylinder1757"
  Angle = 360
  AttacherType = Attacher::AttachEngine3D
  Height = 15
  Placement = pos=(203.5,16.5,-30) rot=(0,0,1;0rad)
  Radius = 0.9
FEATURE [Part::Cylinder] Cylinder1346  label="Cylinder1758"
  Angle = 360
  AttacherType = Attacher::AttachEngine3D
  Height = 15
  Placement = pos=(241.5,45.5,-30) rot=(0,0,1;0rad)
  Radius = 0.9
FEATURE [Part::Cylinder] Cylinder1347  label="Cylinder1759"
  Angle = 360
  AttacherType = Attacher::AttachEngine3D
  Height = 15
  Placement = pos=(241.5,16.5,-30) rot=(0,0,1;0rad)
  Radius = 0.9
FEATURE [Part::MultiFuse] Fusion248002227  label="Fusion248002366"
  Placement = pos=(0,-1,0) rot=(0,0,1;0rad)
  Refine = true
  Shapes = -> [Cylinder1344,Cylinder1346,Cylinder1347,Cylinder1345]
FEATURE [Part::Box] Box811  label="Cube972"
  AttacherType = Attacher::AttachEngine3D
  Height = 3
  Length = 4
  Placement = pos=(201.5,13,-25) rot=(0,0,1;0rad)
  Width = 5
FEATURE [Part::Box] Box812  label="Cube973"
  AttacherType = Attacher::AttachEngine3D
  Height = 3
  Length = 4
  Placement = pos=(201.5,42,-25) rot=(0,0,1;0rad)
  Width = 5
FEATURE [Part::Box] Box813  label="Cube974"
  AttacherType = Attacher::AttachEngine3D
  Height = 3
  Length = 4
  Placement = pos=(239.5,42,-25) rot=(0,0,1;0rad)
  Width = 5
FEATURE [Part::Box] Box814  label="Cube975"
  AttacherType = Attacher::AttachEngine3D
  Height = 3
  Length = 4
  Placement = pos=(239.5,13,-25) rot=(0,0,1;0rad)
  Width = 5
FEATURE [Part::MultiFuse] Fusion248002228  label="Fusion248002367"
  Refine = true
  Shapes = -> [Box811,Box813,Box814,Box812]
FEATURE [Part::MultiFuse] Fusion248002229  label="Fusion248002368"
  Refine = true
  Shapes = -> [Fusion248002139,Fusion248002228]
FEATURE [Part::Cut] Cut014352  label="Cut014501"
  Base = -> Fusion248002229
  Refine = true
  Tool = -> Fusion248002221
FEATURE [Part::Cut] Cut014353  label="Cut014502"
  Base = -> Cut014352
  Refine = true
  Tool = -> Fusion248002218
FEATURE [Part::Cut] Cut014354  label="air-tanks-fake"
  Base = -> Cut014353
  Refine = true
  Tool = -> Fusion248002227
FEATURE [Part::Box] Box815  label="Cube976"
  AttacherType = Attacher::AttachEngine3D
  Height = 24
  Length = 45
  Placement = pos=(200,6.5,-22) rot=(0,0,1;0rad)
  Width = 47
FEATURE [Part::Box] Box816  label="Cube977"
  AttacherType = Attacher::AttachEngine3D
  Height = 20
  Length = 42
  Placement = pos=(201.5,6.5,-18) rot=(0,0,1;0rad)
  Width = 43
FEATURE [Part::Box] Box817  label="Cube978"
  AttacherType = Attacher::AttachEngine3D
  Height = 5
  Length = 45
  Placement = pos=(200,6.5,-20) rot=(0,0,1;0rad)
  Width = 1.5
FEATURE [Part::Cylinder] Cylinder1348  label="Cylinder1772"
  Angle = 360
  AttacherType = Attacher::AttachEngine3D
  Height = 65
  Placement = pos=(190,51.5,0) rot=(0,1,0;1.5708rad)
  Radius = 0.55
FEATURE [Part::Cylinder] Cylinder1349  label="Cylinder1773"
  Angle = 360
  AttacherType = Attacher::AttachEngine3D
  Height = 10
  Placement = pos=(261,1,10) rot=(1,0,0;1.5708rad)
  Radius = 1.6
FEATURE [Part::Cylinder] Cylinder1350  label="Cylinder1774"
  Angle = 360
  AttacherType = Attacher::AttachEngine3D
  Height = 10
  Placement = pos=(294,1,10) rot=(1,0,0;1.5708rad)
  Radius = 1.6
FEATURE [Part::MultiFuse] Fusion248002230  label="Fusion248002369"
  Placement = pos=(-55,55,-18) rot=(0,0,1;0rad)
  Refine = true
  Shapes = -> [Cylinder1349,Cylinder1350]
FEATURE [Part::Cut] Cut014355  label="Cut014503"
  Base = -> Box815
  Refine = true
  Tool = -> Box816
FEATURE [Part::MultiFuse] Fusion248002231  label="Fusion248002370"
  Placement = pos=(0,-1,0) rot=(0,0,1;0rad)
  Refine = true
  Shapes = -> [Cut014355,Box817]
FEATURE [Part::MultiFuse] Fusion248002232  label="Fusion248002371"
  Placement = pos=(0,-1,0) rot=(0,0,1;0rad)
  Refine = true
  Shapes = -> [Fusion248002230,Cylinder1348]
FEATURE [Part::Cylinder] Cylinder1351  label="Cylinder1775"
  Angle = 360
  AttacherType = Attacher::AttachEngine3D
  Height = 15
  Placement = pos=(198.5,48,-8) rot=(1,0,0;1.5708rad)
  Radius = 2
FEATURE [Part::Cylinder] Cylinder1352  label="Cylinder1776"
  Angle = 360
  AttacherType = Attacher::AttachEngine3D
  Height = 15
  Placement = pos=(198.5,30,-8) rot=(1,0,0;1.5708rad)
  Radius = 2
FEATURE [Part::MultiFuse] Fusion248002233  label="Fusion248002372"
  Refine = true
  Shapes = -> [Cylinder1351,Cylinder1352]
FEATURE [Part::Fillet] Fillet007083
  Base = -> Fusion248002233
  Edges = 4 edges r=2: [Edge1,Edge3,Edge4,Edge6]
FEATURE [Part::Cylinder] Cylinder1353  label="Cylinder1777"
  Angle = 360
  AttacherType = Attacher::AttachEngine3D
  Height = 15
  Placement = pos=(198.5,48,-8) rot=(1,0,0;1.5708rad)
  Radius = 2
FEATURE [Part::Cylinder] Cylinder1354  label="Cylinder1778"
  Angle = 360
  AttacherType = Attacher::AttachEngine3D
  Height = 15
  Placement = pos=(198.5,30,-8) rot=(1,0,0;1.5708rad)
  Radius = 2
FEATURE [Part::MultiFuse] Fusion248002234  label="Fusion248002373"
  Refine = true
  Shapes = -> [Cylinder1353,Cylinder1354]
FEATURE [Part::Fillet] Fillet007084
  Base = -> Fusion248002234
  Edges = 4 edges r=2: [Edge1,Edge3,Edge4,Edge6]
  Placement = pos=(48,0,0) rot=(0,0,1;0rad)
FEATURE [Part::MultiFuse] Fusion248002235  label="Fusion248002374"
  Placement = pos=(0,-3,-2) rot=(0,0,1;0rad)
  Refine = true
  Shapes = -> [Fillet007083,Fillet007084]
FEATURE [Part::Cylinder] Cylinder1355  label="Cylinder1779"
  Angle = 360
  AttacherType = Attacher::AttachEngine3D
  Height = 15
  Placement = pos=(212.5,44.65,-24) rot=(0,0,1;0rad)
  Radius = 1
FEATURE [Part::Cylinder] Cylinder1356  label="Cylinder1780"
  Angle = 360
  AttacherType = Attacher::AttachEngine3D
  Height = 15
  Placement = pos=(212.5,9.35,-24) rot=(0,0,1;0rad)
  Radius = 1
FEATURE [Part::Cylinder] Cylinder1357  label="Cylinder1781"
  Angle = 360
  AttacherType = Attacher::AttachEngine3D
  Height = 15
  Placement = pos=(232.5,44.65,-24) rot=(0,0,1;0rad)
  Radius = 1
FEATURE [Part::Cylinder] Cylinder1358  label="Cylinder1782"
  Angle = 360
  AttacherType = Attacher::AttachEngine3D
  Height = 15
  Placement = pos=(232.5,9.35,-24) rot=(0,0,1;0rad)
  Radius = 1
FEATURE [Part::Box] Box818  label="Cube979"
  AttacherType = Attacher::AttachEngine3D
  Height = 6.5
  Length = 43
  Placement = pos=(201,42,-18) rot=(0,0,1;0rad)
  Width = 7
FEATURE [Part::Box] Box819  label="Cube980"
  AttacherType = Attacher::AttachEngine3D
  Height = 21
  Length = 45
  Placement = pos=(200,52.5,-22) rot=(0,0,1;0rad)
  Width = 1
FEATURE [Part::MultiFuse] Fusion248002236  label="Fusion248002375"
  Refine = true
  Shapes = -> [Fusion248002231,Box819]
FEATURE [Part::Cut] Cut014356  label="Cut014504"
  Base = -> Fusion248002236
  Refine = true
  Tool = -> Fusion248002232
FEATURE [Part::Cut] Cut014357  label="Cut014505"
  Base = -> Cut014356
  Refine = true
  Tool = -> Fusion248002235
FEATURE [Part::Cylinder] Cylinder1359  label="Cylinder1783"
  Angle = 360
  AttacherType = Attacher::AttachEngine3D
  Height = 2.5
  Placement = pos=(261,1,10) rot=(1,0,0;1.5708rad)
  Radius = 3.1
FEATURE [Part::Cylinder] Cylinder1360  label="Cylinder1784"
  Angle = 360
  AttacherType = Attacher::AttachEngine3D
  Height = 2.5
  Placement = pos=(294,1,10) rot=(1,0,0;1.5708rad)
  Radius = 3.1
FEATURE [Part::MultiFuse] Fusion248002237  label="Fusion248002376"
  Placement = pos=(-55,50,-18) rot=(0,0,1;0rad)
  Refine = true
  Shapes = -> [Cylinder1359,Cylinder1360]
FEATURE [Part::Cut] Cut014358  label="Cut014506"
  Base = -> Cut014357
  Refine = true
  Tool = -> Fusion248002237
FEATURE [Part::Box] Box820  label="Cube981"
  AttacherType = Attacher::AttachEngine3D
  Height = 7
  Length = 27
  Placement = pos=(209,48.5,-6) rot=(0,0,1;0rad)
  Width = 2
FEATURE [Part::Fillet] Fillet007085
  Base = -> Box820
  Edges = 2 edges r=1.99: [Edge11,Edge12]
FEATURE [Part::Cut] Cut014359  label="Cut014507"
  Base = -> Cut014358
  Refine = true
  Tool = -> Fillet007085
FEATURE [Part::Box] Box821  label="Cube982"
  AttacherType = Attacher::AttachEngine3D
  Height = 6.5
  Length = 43
  Placement = pos=(201,7,-18) rot=(0,0,1;0rad)
  Width = 5
FEATURE [Part::Box] Box822  label="Cube983"
  AttacherType = Attacher::AttachEngine3D
  Height = 6
  Length = 14
  Placement = pos=(205.5,7,-24) rot=(0,0,1;0rad)
  Width = 41
FEATURE [Part::Box] Box823  label="Cube984"
  AttacherType = Attacher::AttachEngine3D
  Height = 6
  Length = 14
  Placement = pos=(225.5,7,-24) rot=(0,0,1;0rad)
  Width = 41
FEATURE [Part::MultiFuse] Fusion248002238  label="Fusion248002377"
  Placement = pos=(0,-0.5,0) rot=(0,0,1;0rad)
  Refine = true
  Shapes = -> [Box823,Box822]
FEATURE [Part::Cut] Cut014360  label="Cut014508"
  Base = -> Cut014359
  Refine = true
  Tool = -> Fusion248002238
FEATURE [Part::MultiFuse] Fusion248002239  label="Fusion248002378"
  Refine = true
  Shapes = -> [Box821,Box818,Cut014360]
FEATURE [Part::MultiFuse] Fusion248002240  label="Fusion248002379"
  Refine = true
  Shapes = -> [Cylinder1355,Cylinder1356,Cylinder1357,Cylinder1358]
FEATURE [Part::Cut] Cut014361  label="Cut014509"
  Base = -> Fusion248002239
  Refine = true
  Tool = -> Fusion248002240
FEATURE [Part::Cylinder] Cylinder1361  label="Cylinder1785"
  Angle = 360
  AttacherType = Attacher::AttachEngine3D
  Height = 15
  Placement = pos=(203.5,45.5,-30) rot=(0,0,1;0rad)
  Radius = 1.2
FEATURE [Part::Cylinder] Cylinder1362  label="Cylinder1786"
  Angle = 360
  AttacherType = Attacher::AttachEngine3D
  Height = 15
  Placement = pos=(203.5,16.5,-30) rot=(0,0,1;0rad)
  Radius = 1.2
FEATURE [Part::Cylinder] Cylinder1363  label="Cylinder1787"
  Angle = 360
  AttacherType = Attacher::AttachEngine3D
  Height = 15
  Placement = pos=(241.5,45.5,-30) rot=(0,0,1;0rad)
  Radius = 1.2
FEATURE [Part::Cylinder] Cylinder1364  label="Cylinder1788"
  Angle = 360
  AttacherType = Attacher::AttachEngine3D
  Height = 15
  Placement = pos=(241.5,16.5,-30) rot=(0,0,1;0rad)
  Radius = 1.2
FEATURE [Part::MultiFuse] Fusion248002241  label="Fusion248002380"
  Placement = pos=(0,-1,6) rot=(0,0,1;0rad)
  Refine = true
  Shapes = -> [Cylinder1361,Cylinder1363,Cylinder1364,Cylinder1362]
FEATURE [Part::Box] Box824  label="Cube985"
  AttacherType = Attacher::AttachEngine3D
  Height = 6.5
  Length = 14
  Placement = pos=(205.5,7,-22) rot=(0,0,1;0rad)
  Width = 42
FEATURE [Part::Box] Box825  label="Cube986"
  AttacherType = Attacher::AttachEngine3D
  Height = 6.5
  Length = 14
  Placement = pos=(225.5,7,-22) rot=(0,0,1;0rad)
  Width = 42
FEATURE [Part::MultiFuse] Fusion248002242  label="Fusion248002381"
  Placement = pos=(0,-1,0) rot=(0,0,1;0rad)
  Refine = true
  Shapes = -> [Box825,Box824]
FEATURE [Part::Fillet] Fillet007086
  Base = -> Cut014361
  Edges = 2 edges r=8: [Edge53,Edge57]
FEATURE [Part::Cut] Cut014362  label="Cut014510"
  Base = -> Fillet007086
  Refine = true
  Tool = -> Fusion248002241
FEATURE [Part::Cut] Cut014363  label="battery-box_"
  Base = -> Cut014362
  Refine = true
  Tool = -> Fusion248002242
FEATURE [Part::Cylinder] Cylinder1369  label="Cylinder1797"
  Angle = 360
  AttacherType = Attacher::AttachEngine3D
  Height = 7
  Placement = pos=(203.5,44.5,-42) rot=(1,0,0;1.5708rad)
  Radius = 1.1
FEATURE [Part::Cylinder] Cylinder1370  label="Cylinder1798"
  Angle = 360
  AttacherType = Attacher::AttachEngine3D
  Height = 7
  Placement = pos=(203.5,42.5,-42) rot=(1,0,0;1.5708rad)
  Radius = 0.6
FEATURE [Part::MultiFuse] Fusion248002244  label="Fusion248002382"
  Placement = pos=(17.75,9,13) rot=(0,0,1;0rad)
  Refine = true
  Shapes = -> [Cylinder1369,Cylinder1370]
FEATURE [Part::Cylinder] Cylinder1371  label="Cylinder1799"
  Angle = 360
  AttacherType = Attacher::AttachEngine3D
  Height = 7
  Placement = pos=(203.5,44.5,-42) rot=(1,0,0;1.5708rad)
  Radius = 1.1
FEATURE [Part::Cylinder] Cylinder1372  label="Cylinder1800"
  Angle = 360
  AttacherType = Attacher::AttachEngine3D
  Height = 7
  Placement = pos=(203.5,42.5,-42) rot=(1,0,0;1.5708rad)
  Radius = 0.6
FEATURE [Part::MultiFuse] Fusion248002245  label="Fusion248002383"
  Placement = pos=(20.25,9,13) rot=(0,0,1;0rad)
  Refine = true
  Shapes = -> [Cylinder1371,Cylinder1372]
FEATURE [Part::MultiFuse] Fusion248002246  label="Fusion248002384"
  Refine = true
  Shapes = -> [Fusion248002245,Fusion248002244]
FEATURE [Part::Box] Box826  label="Cube987"
  AttacherType = Attacher::AttachEngine3D
  Height = 10
  Length = 7
  Placement = pos=(219,44.5,-32) rot=(0,0,1;0rad)
  Width = 9
FEATURE [Part::Box] Box827  label="Cube988"
  AttacherType = Attacher::AttachEngine3D
  Height = 10
  Length = 0.5
  Placement = pos=(219,44.5,-32) rot=(0,0,1;0rad)
  Width = 3.5
FEATURE [Part::Box] Box828  label="Cube989"
  AttacherType = Attacher::AttachEngine3D
  Height = 10
  Length = 0.5
  Placement = pos=(225.5,44.5,-32) rot=(0,0,1;0rad)
  Width = 3.5
FEATURE [Part::MultiFuse] Fusion248002247  label="Fusion248002385"
  Refine = true
  Shapes = -> [Box828,Box827]
FEATURE [Part::Cut] Cut014364  label="Cut014511"
  Base = -> Box826
  Refine = true
  Tool = -> Fusion248002247
FEATURE [Part::MultiFuse] Fusion248002248  label="Fusion248002386"
  Refine = true
  Shapes = -> [Cut014363,Cut014364]
FEATURE [Part::Cut] Cut014365  label="battery-box-02"
  Base = -> Fusion248002248
  Refine = true
  Tool = -> Fusion248002246
FEATURE [App::DocumentObjectGroup] Group009  label="diff-locks"
  Group = -> [Cut014188,Cut014189,Cut014191,Cut014192,Cut014257,Fusion248002202,Fusion248002207,Fusion248002209,Cut014351,Cut014350,Cut014354,Cut014365]
FEATURE [Part::Box] Box829  label="Cube990"
  AttacherType = Attacher::AttachEngine3D
  Height = 17.4
  Length = 8
  Placement = pos=(154.5,56,-16.5) rot=(0,0,1;0rad)
  Width = 10
FEATURE [Part::Fillet] Fillet007087
  Base = -> Box829
  Edges = 2 edges r=3: [Edge9,Edge10]
  Placement = pos=(0,-1,-0.2) rot=(0,0,1;0rad)
FEATURE [Part::Box] Box830  label="Cube991"
  AttacherType = Attacher::AttachEngine3D
  Height = 13
  Length = 8
  Placement = pos=(154.5,53,-14.5) rot=(0,0,1;0rad)
  Width = 10
FEATURE [Part::Cut] Cut014366  label="Cut014512"
  Base = -> Fillet007087
  Refine = true
  Tool = -> Box830
FEATURE [Part::Fillet] Fillet007088
  Base = -> Cut014366
  Edges = 4 edges r=1: [Edge9,Edge11,Edge13,Edge15]
FEATURE [Part::Fillet] Fillet007089
  Base = -> Fillet007088
  Edges = 2 edges r=3: [Edge24,Edge29]
FEATURE [Part::Cylinder] Cylinder1373  label="rear-bumper011"
  Angle = 360
  AttacherType = Attacher::AttachEngine3D
  Height = 30
  Placement = pos=(501,60,-43) rot=(0,0,1;0rad)
  Radius = 1.6
FEATURE [Part::Cylinder] Cylinder1374  label="rear-bumper012"
  Angle = 360
  AttacherType = Attacher::AttachEngine3D
  Height = 16
  Placement = pos=(501,60,-43) rot=(0,0,1;0rad)
  Radius = 3.2
FEATURE [Part::Box] Box831  label="Cube992"
  AttacherType = Attacher::AttachEngine3D
  Height = 16
  Length = 3
  Placement = pos=(498,56.8,-43) rot=(0,0,1;0rad)
  Width = 6.4
FEATURE [Part::Box] Box832  label="Cube993"
  AttacherType = Attacher::AttachEngine3D
  Height = 30
  Length = 3
  Placement = pos=(498,58.4,-43) rot=(0,0,1;0rad)
  Width = 3.2
FEATURE [Part::MultiFuse] Fusion248002249  label="Fusion248002387"
  Refine = true
  Shapes = -> [Cylinder1148,Cylinder1149,Cylinder1373,Box832,Box831,Cylinder1374]
FEATURE [Part::Cylinder] Cylinder1375  label="rear-bumper013"
  Angle = 360
  AttacherType = Attacher::AttachEngine3D
  Height = 30
  Placement = pos=(498,60,-43) rot=(0,0,1;0rad)
  Radius = 1.6
FEATURE [Part::Cylinder] Cylinder1376  label="rear-bumper014"
  Angle = 360
  AttacherType = Attacher::AttachEngine3D
  Height = 16
  Placement = pos=(498,60,-43) rot=(0,0,1;0rad)
  Radius = 3.2
FEATURE [Part::Cylinder] Cylinder1377  label="rear-bumper015"
  Angle = 360
  AttacherType = Attacher::AttachEngine3D
  Height = 30
  Placement = pos=(501,60,-43) rot=(0,0,1;0rad)
  Radius = 1.6
FEATURE [Part::Cylinder] Cylinder1378  label="rear-bumper016"
  Angle = 360
  AttacherType = Attacher::AttachEngine3D
  Height = 16
  Placement = pos=(501,60,-43) rot=(0,0,1;0rad)
  Radius = 3.2
FEATURE [Part::Box] Box833  label="Cube994"
  AttacherType = Attacher::AttachEngine3D
  Height = 16
  Length = 3
  Placement = pos=(498,56.8,-43) rot=(0,0,1;0rad)
  Width = 6.4
FEATURE [Part::Box] Box834  label="Cube995"
  AttacherType = Attacher::AttachEngine3D
  Height = 30
  Length = 3
  Placement = pos=(498,58.4,-43) rot=(0,0,1;0rad)
  Width = 3.2
FEATURE [Part::MultiFuse] Fusion248002250  label="Fusion248002388"
  Refine = true
  Shapes = -> [Cylinder1375,Cylinder1376,Cylinder1377,Box834,Box833,Cylinder1378]
FEATURE [Part::Cut] Cut014367  label="rear-bumper-holder-left"
  Base = -> Cut014262
  Refine = true
  Tool = -> Fusion248002249
FEATURE [Part::Cut] Cut014368  label="rear-bumper-holder-right"
  Base = -> Cut014267
  Placement = pos=(0,50,0) rot=(0,0,1;0rad)
  Refine = true
  Tool = -> Fusion248002250
FEATURE [App::DocumentObjectGroup] Group018  label="rear"
  Group = -> [Cylinder1018,Box772,Cut014310,Cut014321,Chamfer173,Cut014323,Part__Mirroring115,Part__Mirroring116,Box787,Cut014333,Cut014367,Cut014368]
FEATURE [App::DocumentObjectGroup] Group014  label="frame"
  Group = -> [Group017,Group018,Group019]
FEATURE [Part::Box] Box835  label="Cube996"
  AttacherType = Attacher::AttachEngine3D
  Height = 25
  Length = 5
  Placement = pos=(150,40,0) rot=(0,0,1;0rad)
  Width = 100
FEATURE [Part::Box] Box836  label="Cube997"
  AttacherType = Attacher::AttachEngine3D
  Height = 40
  Length = 10
  Placement = pos=(150,19,0) rot=(-1,0,0;0.383972rad)
  Width = 20
FEATURE [Part::Box] Box837  label="Cube998"
  AttacherType = Attacher::AttachEngine3D
  Height = 40
  Length = 10
  Placement = pos=(150,19,0) rot=(-1,0,0;0.383972rad)
  Width = 20
FEATURE [Part::Mirroring] Part__Mirroring120  label="Cube088 (Mirror #13)003"
  Base = (0,0,0)
  Normal = (0,1,0)
  Placement = pos=(0,180,0) rot=(0,0,1;0rad)
  Source = -> Box837
FEATURE [Part::MultiFuse] Fusion248002251  label="Fusion248002407"
  Refine = true
  Shapes = -> [Box836,Part__Mirroring120]
FEATURE [Part::Cut] Cut014369  label="Cut014532"
  Base = -> Box835
  Placement = pos=(-29,-5,35) rot=(0,0,1;0rad)
  Refine = true
  Tool = -> Fusion248002251
FEATURE [Part::Box] Box838  label="Cube999"
  AttacherType = Attacher::AttachEngine3D
  Height = 8
  Length = 45
  Placement = pos=(81,50.5,7) rot=(0,0,1;0rad)
  Width = 3
FEATURE [Part::Cylinder] Cylinder1379  label="Cylinder1827"
  Angle = 360
  AttacherType = Attacher::AttachEngine3D
  Height = 8
  Placement = pos=(96,120,-8) rot=(1,0,0;1.5708rad)
  Radius = 1.25
FEATURE [Part::Cylinder] Cylinder1380  label="Cylinder1828"
  Angle = 360
  AttacherType = Attacher::AttachEngine3D
  Height = 8
  Placement = pos=(86,120,-8) rot=(1,0,0;1.5708rad)
  Radius = 1.25
FEATURE [Part::MultiFuse] Fusion248002252  label="Fusion248002408"
  Placement = pos=(12,-64,20) rot=(0,0,1;0rad)
  Refine = true
  Shapes = -> [Cylinder1380,Cylinder1379]
FEATURE [Part::Box] Box839  label="Cube1000"
  AttacherType = Attacher::AttachEngine3D
  Height = 5
  Length = 8
  Placement = pos=(118,41.5,7) rot=(0,0,1;0rad)
  Width = 9
FEATURE [Part::MultiFuse] Fusion248002253  label="Fusion248002409"
  Refine = true
  Shapes = -> [Box838,Box839]
FEATURE [Part::Fillet] Fillet007090
  Base = -> Cut014369
  Edges = 2 edges r=6: [Edge5,Edge7]
  Placement = pos=(0,0,-7) rot=(0,0,1;0rad)
FEATURE [Part::Box] Box840  label="Cube934"
  AttacherType = Attacher::AttachEngine3D
  Height = 25
  Length = 6
  Placement = pos=(150,40,0) rot=(0,0,1;0rad)
  Width = 100
FEATURE [Part::Box] Box841  label="Cube1001"
  AttacherType = Attacher::AttachEngine3D
  Height = 40
  Length = 10
  Placement = pos=(150,20,0) rot=(-1,0,0;0.383972rad)
  Width = 20
FEATURE [Part::Box] Box842  label="Cube1002"
  AttacherType = Attacher::AttachEngine3D
  Height = 40
  Length = 10
  Placement = pos=(150,19,0) rot=(-1,0,0;0.383972rad)
  Width = 20
FEATURE [Part::Mirroring] Part__Mirroring121  label="Cube088 (Mirror #13)004"
  Base = (0,0,0)
  Normal = (0,1,0)
  Placement = pos=(0,179,0) rot=(0,0,1;0rad)
  Source = -> Box842
FEATURE [Part::MultiFuse] Fusion248002254  label="Fusion248002410"
  Refine = true
  Shapes = -> [Box841,Part__Mirroring121]
FEATURE [Part::Cut] Cut014370  label="Cut014533"
  Base = -> Box840
  Placement = pos=(-29,-5,35) rot=(0,0,1;0rad)
  Refine = true
  Tool = -> Fusion248002254
FEATURE [Part::Fillet] Fillet007091
  Base = -> Cut014370
  Edges = 2 edges r=5: [Edge5,Edge7]
  Placement = pos=(-1,0,-9) rot=(0,0,1;0rad)
FEATURE [Part::Box] Box843  label="Cube1003"
  AttacherType = Attacher::AttachEngine3D
  Height = 25
  Length = 2.75
  Placement = pos=(150,40,0) rot=(0,0,1;0rad)
  Width = 100
FEATURE [Part::Box] Box844  label="Cube1004"
  AttacherType = Attacher::AttachEngine3D
  Height = 40
  Length = 10
  Placement = pos=(150,19,0) rot=(-1,0,0;0.383972rad)
  Width = 20
FEATURE [Part::Box] Box845  label="Cube1005"
  AttacherType = Attacher::AttachEngine3D
  Height = 40
  Length = 10
  Placement = pos=(150,19,0) rot=(-1,0,0;0.383972rad)
  Width = 20
FEATURE [Part::Mirroring] Part__Mirroring122  label="Cube088 (Mirror #13)005"
  Base = (0,0,0)
  Normal = (0,1,0)
  Placement = pos=(0,180,0) rot=(0,0,1;0rad)
  Source = -> Box845
FEATURE [Part::MultiFuse] Fusion248002255  label="Fusion248002411"
  Refine = true
  Shapes = -> [Box844,Part__Mirroring122]
FEATURE [Part::Cut] Cut014371  label="Cut014534"
  Base = -> Box843
  Placement = pos=(-29,-5,35) rot=(0,0,1;0rad)
  Refine = true
  Tool = -> Fusion248002255
FEATURE [Part::Fillet] Fillet007092
  Base = -> Cut014371
  Edges = 2 edges r=6: [Edge5,Edge7]
  Placement = pos=(-1,0,-3) rot=(0,0,1;0rad)
FEATURE [Part::Box] Box846  label="Cube1006"
  AttacherType = Attacher::AttachEngine3D
  Height = 25
  Length = 10
  Placement = pos=(116,31,10) rot=(0,0,1;0rad)
  Width = 110
FEATURE [Part::MultiFuse] Fusion248002256  label="Fusion248002412"
  Refine = true
  Shapes = -> [Fillet007092,Fillet007090]
FEATURE [Part::Box] Box847  label="Cube1007"
  AttacherType = Attacher::AttachEngine3D
  Height = 40
  Length = 10
  Placement = pos=(150,19,0) rot=(-1,0,0;0.383972rad)
  Width = 20
FEATURE [Part::Box] Box848  label="Cube1008"
  AttacherType = Attacher::AttachEngine3D
  Height = 40
  Length = 10
  Placement = pos=(150,19,0) rot=(-1,0,0;0.383972rad)
  Width = 20
FEATURE [Part::Mirroring] Part__Mirroring123  label="Cube088 (Mirror #13)006"
  Base = (0,0,0)
  Normal = (0,1,0)
  Placement = pos=(0,180,0) rot=(0,0,1;0rad)
  Source = -> Box848
FEATURE [Part::MultiFuse] Fusion248002257  label="Fusion248002413"
  Placement = pos=(-27.25,-5,28) rot=(0,0,1;0rad)
  Refine = true
  Shapes = -> [Box847,Part__Mirroring123]
FEATURE [Part::Fillet] Fillet007093
  Base = -> Fusion248002253
  Edges = 2 edges r=3.99: [Edge14,Edge20]
FEATURE [Part::Chamfer] Chamfer180
  Base = -> Fillet007093
  Edges = 1 edges r=3: [Edge24]
  Placement = pos=(1,0,0) rot=(0,0,1;0rad)
FEATURE [Part::Cut] Cut014372  label="Cut014535"
  Base = -> Chamfer180
  Refine = true
  Tool = -> Fusion248002252
FEATURE [Part::Box] Box849  label="Cube1009"
  AttacherType = Attacher::AttachEngine3D
  Height = 40
  Length = 10
  Placement = pos=(150,19,0) rot=(-1,0,0;0.383972rad)
  Width = 20
FEATURE [Part::Box] Box850  label="Cube1010"
  AttacherType = Attacher::AttachEngine3D
  Height = 40
  Length = 10
  Placement = pos=(150,19,0) rot=(-1,0,0;0.383972rad)
  Width = 20
FEATURE [Part::Mirroring] Part__Mirroring124  label="Cube088 (Mirror #13)007"
  Base = (0,0,0)
  Normal = (0,1,0)
  Placement = pos=(0,180,0) rot=(0,0,1;0rad)
  Source = -> Box850
FEATURE [Part::MultiFuse] Fusion248002258  label="Fusion248002414"
  Placement = pos=(-33,-5,32) rot=(0,0,1;0rad)
  Refine = true
  Shapes = -> [Box849,Part__Mirroring124]
FEATURE [Part::Cylinder] Cylinder1381  label="Cylinder1829"
  Angle = 360
  AttacherType = Attacher::AttachEngine3D
  Height = 39
  Placement = pos=(123,46,6) rot=(1,0,0;0.122173rad)
  Radius = 3
FEATURE [Part::Cylinder] Cylinder1382  label="Cylinder1830"
  Angle = 360
  AttacherType = Attacher::AttachEngine3D
  Height = 29
  Placement = pos=(123,46,6) rot=(1,0,0;0.122173rad)
  Radius = 3
FEATURE [Part::Cut] Cut014373  label="Cut014536"
  Base = -> Cylinder1381
  Refine = true
  Tool = -> Cylinder1382
FEATURE [Part::Cylinder] Cylinder1383  label="Cylinder1831"
  Angle = 360
  AttacherType = Attacher::AttachEngine3D
  Height = 4
  Placement = pos=(123,46,6) rot=(1,0,0;0.122173rad)
  Radius = 3.1
FEATURE [Part::Cylinder] Cylinder1384  label="Cylinder1832"
  Angle = 360
  AttacherType = Attacher::AttachEngine3D
  Height = 34
  Placement = pos=(123,46,6) rot=(1,0,0;0.122173rad)
  Radius = 1.25
FEATURE [Part::MultiFuse] Fusion248002167  label="Fusion248002415"
  Refine = true
  Shapes = -> [Cylinder1383,Cylinder1384]
FEATURE [Part::Cylinder] Cylinder1385  label="Cylinder1833"
  Angle = 360
  AttacherType = Attacher::AttachEngine3D
  Height = 5
  Placement = pos=(123,46,6) rot=(1,0,0;0.122173rad)
  Radius = 3
FEATURE [Part::Cylinder] Cylinder1386  label="Cylinder1834"
  Angle = 360
  AttacherType = Attacher::AttachEngine3D
  Height = 7
  Placement = pos=(123,46,6) rot=(1,0,0;0.122173rad)
  Radius = 3
FEATURE [Part::Cut] Cut014374  label="Cut014537"
  Base = -> Cylinder1386
  Refine = true
  Tool = -> Cylinder1385
FEATURE [Part::MultiFuse] Fusion248002259  label="Fusion248002416"
  Refine = true
  Shapes = -> [Cut014372,Cut014374]
FEATURE [Part::Cut] Cut014375  label="Cut014538"
  Base = -> Fusion248002259
  Refine = true
  Tool = -> Fusion248002167
FEATURE [Part::Cylinder] Cylinder1387  label="Cylinder1835"
  Angle = 360
  AttacherType = Attacher::AttachEngine3D
  Height = 29
  Placement = pos=(123,46,6) rot=(1,0,0;0.122173rad)
  Radius = 2.2
FEATURE [Part::Cylinder] Cylinder1388  label="Cylinder1836"
  Angle = 360
  AttacherType = Attacher::AttachEngine3D
  Height = 7
  Placement = pos=(123,46,6) rot=(1,0,0;0.122173rad)
  Radius = 3
FEATURE [Part::Cut] Cut014376  label="Cut014539"
  Base = -> Cylinder1387
  Refine = true
  Tool = -> Cylinder1388
FEATURE [Part::Cylinder] Cylinder1389  label="Cylinder1837"
  Angle = 360
  AttacherType = Attacher::AttachEngine3D
  Height = 39
  Placement = pos=(123,46,6) rot=(-1,0,0;0.122173rad)
  Radius = 3
FEATURE [Part::Cylinder] Cylinder1390  label="Cylinder1838"
  Angle = 360
  AttacherType = Attacher::AttachEngine3D
  Height = 29
  Placement = pos=(123,46,6) rot=(-1,0,0;0.122173rad)
  Radius = 3
FEATURE [Part::Cut] Cut014377  label="Cut014540"
  Base = -> Cylinder1389
  Placement = pos=(0,78,0) rot=(0,0,1;0rad)
  Refine = true
  Tool = -> Cylinder1390
FEATURE [Part::Cylinder] Cylinder1391  label="Cylinder1839"
  Angle = 360
  AttacherType = Attacher::AttachEngine3D
  Height = 34
  Placement = pos=(123,46,6) rot=(1,0,0;0.122173rad)
  Radius = 1.6
FEATURE [Part::Cut] Cut014378  label="cab-dampers-tube-left"
  Base = -> Cut014376
  Refine = true
  Tool = -> Cylinder1391
FEATURE [Part::Cylinder] Cylinder1392  label="Cylinder1840"
  Angle = 360
  AttacherType = Attacher::AttachEngine3D
  Height = 29
  Placement = pos=(123,46,6) rot=(-1,0,0;0.122173rad)
  Radius = 2.2
FEATURE [Part::Cylinder] Cylinder1251  label="Cylinder1841"
  Angle = 360
  AttacherType = Attacher::AttachEngine3D
  Height = 7
  Placement = pos=(123,46,6) rot=(-1,0,0;0.122173rad)
  Radius = 3
FEATURE [Part::Cut] Cut014322
  Base = -> Cylinder1392
  Refine = true
  Tool = -> Cylinder1251
FEATURE [Part::Cylinder] Cylinder1393  label="Cylinder1842"
  Angle = 360
  AttacherType = Attacher::AttachEngine3D
  Height = 34
  Placement = pos=(123,46,6) rot=(-1,0,0;0.122173rad)
  Radius = 1.6
FEATURE [Part::Cut] Cut014379  label="cab-dampers-tube-right"
  Base = -> Cut014322
  Placement = pos=(0,78,0) rot=(0,0,1;0rad)
  Refine = true
  Tool = -> Cylinder1393
FEATURE [Part::Box] Box851  label="Cube1011"
  AttacherType = Attacher::AttachEngine3D
  Height = 8
  Length = 45
  Placement = pos=(81,50.5,7) rot=(0,0,1;0rad)
  Width = 3
FEATURE [Part::Cylinder] Cylinder1394  label="Cylinder1843"
  Angle = 360
  AttacherType = Attacher::AttachEngine3D
  Height = 8
  Placement = pos=(96,120,-8) rot=(1,0,0;1.5708rad)
  Radius = 1.25
FEATURE [Part::Cylinder] Cylinder1395  label="Cylinder1844"
  Angle = 360
  AttacherType = Attacher::AttachEngine3D
  Height = 8
  Placement = pos=(86,120,-8) rot=(1,0,0;1.5708rad)
  Radius = 1.25
FEATURE [Part::MultiFuse] Fusion248002260  label="Fusion248002417"
  Placement = pos=(12,-64,20) rot=(0,0,1;0rad)
  Refine = true
  Shapes = -> [Cylinder1395,Cylinder1394]
FEATURE [Part::Box] Box852  label="Cube1012"
  AttacherType = Attacher::AttachEngine3D
  Height = 5
  Length = 8
  Placement = pos=(118,41.5,7) rot=(0,0,1;0rad)
  Width = 9
FEATURE [Part::MultiFuse] Fusion248002261  label="Fusion248002418"
  Refine = true
  Shapes = -> [Box851,Box852]
FEATURE [Part::Fillet] Fillet007094
  Base = -> Fusion248002261
  Edges = 2 edges r=3.99: [Edge14,Edge20]
FEATURE [Part::Chamfer] Chamfer181
  Base = -> Fillet007094
  Edges = 1 edges r=3: [Edge24]
  Placement = pos=(1,0,0) rot=(0,0,1;0rad)
FEATURE [Part::Cut] Cut014380  label="Cut014541"
  Base = -> Chamfer181
  Refine = true
  Tool = -> Fusion248002260
FEATURE [Part::Cylinder] Cylinder1396  label="Cylinder1845"
  Angle = 360
  AttacherType = Attacher::AttachEngine3D
  Height = 4
  Placement = pos=(123,46,6) rot=(1,0,0;0.122173rad)
  Radius = 3.1
FEATURE [Part::Cylinder] Cylinder1397  label="Cylinder1846"
  Angle = 360
  AttacherType = Attacher::AttachEngine3D
  Height = 34
  Placement = pos=(123,46,6) rot=(1,0,0;0.122173rad)
  Radius = 1.25
FEATURE [Part::MultiFuse] Fusion248002262  label="Fusion248002419"
  Refine = true
  Shapes = -> [Cylinder1396,Cylinder1397]
FEATURE [Part::Cylinder] Cylinder1398  label="Cylinder1847"
  Angle = 360
  AttacherType = Attacher::AttachEngine3D
  Height = 5
  Placement = pos=(123,46,6) rot=(1,0,0;0.122173rad)
  Radius = 3
FEATURE [Part::Cylinder] Cylinder1399  label="Cylinder1848"
  Angle = 360
  AttacherType = Attacher::AttachEngine3D
  Height = 7
  Placement = pos=(123,46,6) rot=(1,0,0;0.122173rad)
  Radius = 3
FEATURE [Part::Cut] Cut014381  label="Cut014542"
  Base = -> Cylinder1399
  Refine = true
  Tool = -> Cylinder1398
FEATURE [Part::MultiFuse] Fusion248002263  label="Fusion248002420"
  Refine = true
  Shapes = -> [Cut014380,Cut014381]
FEATURE [Part::Cut] Cut014382  label="Cut014543"
  Base = -> Fusion248002263
  Refine = true
  Tool = -> Fusion248002262
FEATURE [Part::Mirroring] Part__Mirroring125  label="Cut014326 (Mirror #30)"
  Base = (0,0,0)
  Normal = (0,1,0)
  Placement = pos=(0,170,0) rot=(0,0,1;0rad)
  Source = -> Cut014382
FEATURE [Part::MultiFuse] Fusion248002264  label="Fusion248002421"
  Refine = true
  Shapes = -> [Fusion248002257,Fusion248002258]
FEATURE [Part::Cut] Cut014383  label="Cut014544"
  Base = -> Fusion248002256
  Refine = true
  Tool = -> Fillet007091
FEATURE [Part::Cut] Cut014384  label="Cut014545"
  Base = -> Cut014383
  Refine = true
  Tool = -> Box846
FEATURE [Part::MultiFuse] Fusion248002265  label="Fusion248002422"
  Refine = true
  Shapes = -> [Cut014384,Cut014373,Cut014377]
FEATURE [Part::Cut] Cut014385  label="Cut014546"
  Base = -> Fusion248002265
  Refine = true
  Tool = -> Fusion248002264
FEATURE [Part::Cylinder] Cylinder1400  label="Cylinder1849"
  Angle = 360
  AttacherType = Attacher::AttachEngine3D
  Height = 10
  Placement = pos=(114,65,55) rot=(0,1,0;1.5708rad)
  Radius = 0.9
FEATURE [Part::Cylinder] Cylinder1401  label="Cylinder1850"
  Angle = 360
  AttacherType = Attacher::AttachEngine3D
  Height = 10
  Placement = pos=(114,105,55) rot=(0,1,0;1.5708rad)
  Radius = 0.9
FEATURE [Part::MultiFuse] Fusion248002266  label="Fusion248002423"
  Refine = true
  Shapes = -> [Cylinder1400,Cylinder1401]
FEATURE [Part::Cut] Cut014386  label="Cut014547"
  Base = -> Cut014385
  Refine = true
  Tool = -> Fusion248002266
FEATURE [Part::Fillet] Fillet007095
  Base = -> Cut014386
  Edges = 4 edges r=0.5: [Edge39,Edge41,Edge44,Edge48]
FEATURE [Part::Fillet] Fillet007096  label="cab-dampers-upper-attach_"
  Base = -> Fillet007095
  Edges = 2 edges r=1: [Edge30,Edge51]
FEATURE [Part::Fillet] Fillet007097  label="cab-dampers-attach-left"
  Base = -> Cut014375
  Edges = 1 edges r=3: [Edge34]
FEATURE [Part::Fillet] Fillet007098  label="cab-dampers-attach-right"
  Base = -> Part__Mirroring125
  Edges = 1 edges r=3: [Edge34]
FEATURE [Part::Cylinder] Cylinder1402  label="Cylinder1851"
  Angle = 360
  AttacherType = Attacher::AttachEngine3D
  Height = 34
  Placement = pos=(123,124,6) rot=(-1,0,0;0.122173rad)
  Radius = 1.25
FEATURE [Part::Cylinder] Cylinder1403  label="Cylinder1852"
  Angle = 360
  AttacherType = Attacher::AttachEngine3D
  Height = 34
  Placement = pos=(123,46,6) rot=(1,0,0;0.122173rad)
  Radius = 1.25
FEATURE [Part::MultiFuse] Fusion248002267  label="Fusion248002424"
  Refine = true
  Shapes = -> [Cylinder1402,Cylinder1403]
FEATURE [Part::Cut] Cut014387  label="cab-dampers-upper-attach"
  Base = -> Fillet007096
  Refine = true
  Tool = -> Fusion248002267
FEATURE [Part::Box] Box853  label="Cube1013"
  AttacherType = Attacher::AttachEngine3D
  Height = 10
  Length = 10
  Placement = pos=(129,117,0) rot=(0,0,1;0rad)
  Width = 25
FEATURE [Mesh::Feature] crane
  Placement = pos=(-3,0,0) rot=(0,0,1;0rad)
FEATURE [Mesh::Feature] bucket
  Placement = pos=(422,561,19) rot=(0,0,1;-1.5708rad)
note: 4 file-system paths scrubbed to <path> (originals preserved in the JSON sidecar)
